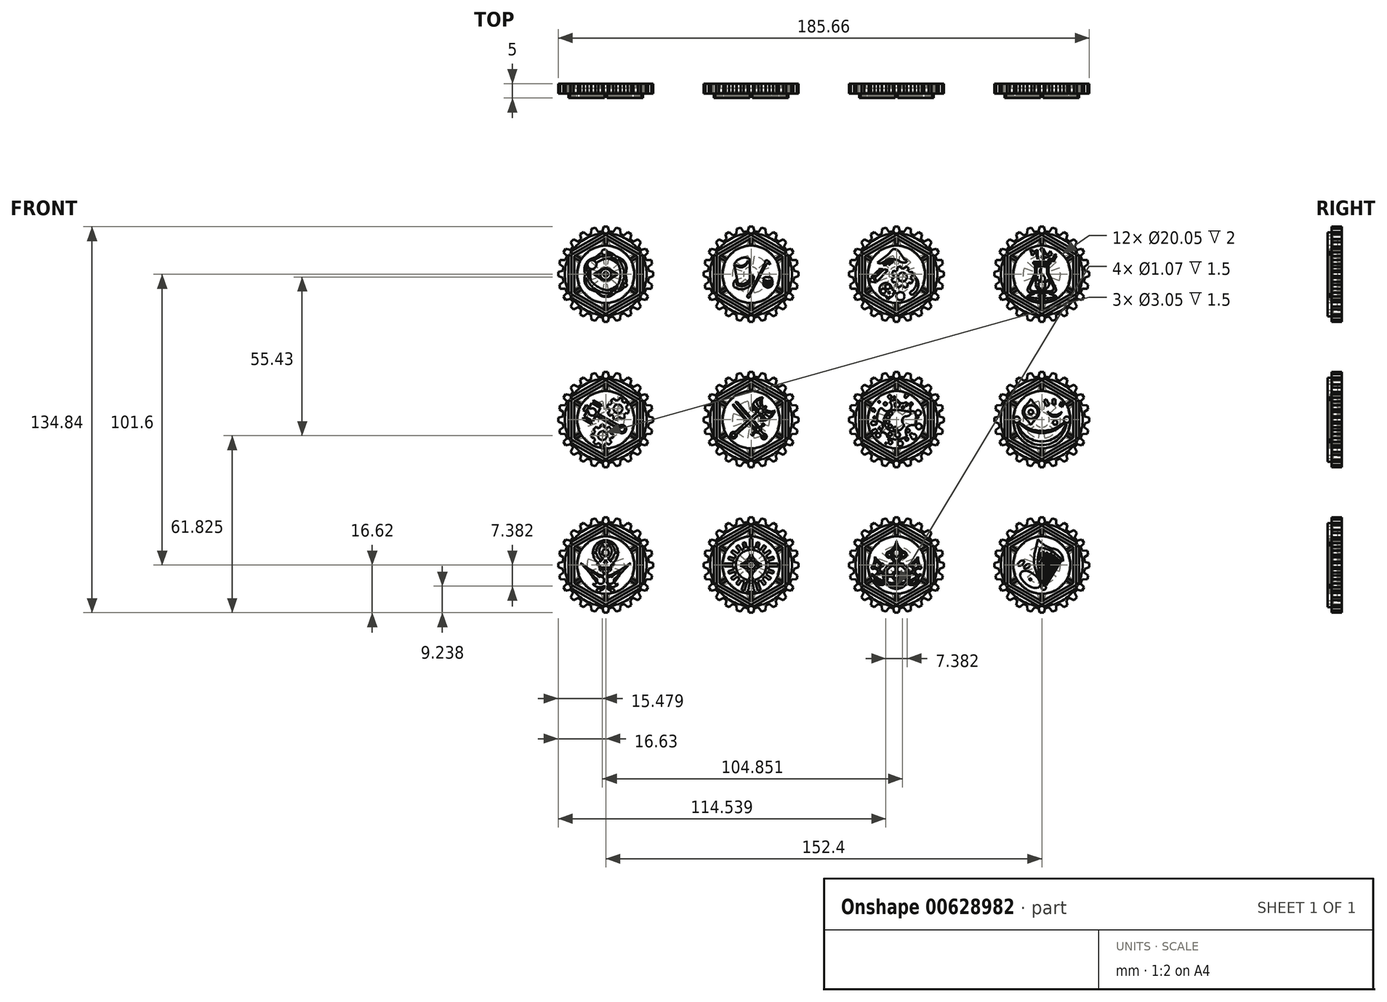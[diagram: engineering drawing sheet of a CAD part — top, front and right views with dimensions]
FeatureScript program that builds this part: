
annotation { "Feature Type Name" : "Feature", "Feature Type Description" : "" }
export const myFeature = defineFeature(function(context is Context, id is Id, definition is map)
    precondition{}
    {
        {
            var Q0;
            Q0=qCreatedBy(makeId("Front.planeOp"),FACE);
            var sketch = newSketch(context, id + "F0", { "sketchPlane" : qUnion([Q0])});
            skLineSegment(sketch, "E0", {"start": v(0, 15) * mm, "end": v(13, 7.5) * mm});
            skLineSegment(sketch, "E1", {"start": v(13, 7.5) * mm, "end": v(13, -7.5) * mm});
            skLineSegment(sketch, "E2", {"start": v(13, -7.5) * mm, "end": v(0, -15) * mm});
            skLineSegment(sketch, "E3", {"start": v(0, -15) * mm, "end": v(-13, -7.5) * mm});
            skLineSegment(sketch, "E4", {"start": v(-13, -7.5) * mm, "end": v(-13, 7.5) * mm});
            skLineSegment(sketch, "E5", {"start": v(-13, 7.5) * mm, "end": v(0, 15) * mm});
            skSolve(sketch);
        }
        {
            var Q0;
            Q0 = qSketchRegion(id + "F0", true);
            extrude(context, id + "F1", {"entities" : qUnion([Q0]), "depth" : 5 * mm, "offsetDistance" : 25.4 * mm});
        }
        {
            var Q0;
            Q0=makeQuery(id+"F1.opExtrude","CAP_FACE",FACE,{"disambiguationData":[OSD([sQuery(id+"F0.wireOp",EDGE,"E0"),sQuery(id+"F0.wireOp",EDGE,"E1"),sQuery(id+"F0.wireOp",EDGE,"E2"),sQuery(id+"F0.wireOp",EDGE,"E3"),sQuery(id+"F0.wireOp",EDGE,"E4"),sQuery(id+"F0.wireOp",EDGE,"E5")])],"isStart":false});
            var sketch = newSketch(context, id + "F2", { "sketchPlane" : qUnion([Q0])});
            skLineSegment(sketch, "E6.0", {"start": v(12, 6.92) * mm, "end": v(0, 13.85) * mm});
            skLineSegment(sketch, "E6.1", {"start": v(-12, 6.92) * mm, "end": v(-12, -6.92) * mm});
            skLineSegment(sketch, "E6.2", {"start": v(-12, -6.92) * mm, "end": v(0, -13.85) * mm});
            skLineSegment(sketch, "E6.3", {"start": v(0, 13.85) * mm, "end": v(-12, 6.92) * mm});
            skLineSegment(sketch, "E6.4", {"start": v(0, -13.85) * mm, "end": v(12, -6.92) * mm});
            skLineSegment(sketch, "E6.5", {"start": v(12, -6.92) * mm, "end": v(12, 6.92) * mm});
            skLineSegment(sketch, "E7.0", {"start": v(11, 6.35) * mm, "end": v(0, 12.7) * mm});
            skLineSegment(sketch, "E7.1", {"start": v(-11, 6.35) * mm, "end": v(-11, -6.35) * mm});
            skLineSegment(sketch, "E7.2", {"start": v(-11, -6.35) * mm, "end": v(0, -12.7) * mm});
            skLineSegment(sketch, "E7.3", {"start": v(0, 12.7) * mm, "end": v(-11, 6.35) * mm});
            skLineSegment(sketch, "E7.4", {"start": v(0, -12.7) * mm, "end": v(11, -6.35) * mm});
            skLineSegment(sketch, "E7.5", {"start": v(11, -6.35) * mm, "end": v(11, 6.35) * mm});
            skSolve(sketch);
        }
        {
            var Q0;
            Q0 = qSketchRegion(id + "F2", true);
            extrude(context, id + "F3", {"entities" : qUnion([Q0]), "operationType" : NewBodyOperationType.REMOVE, "oppositeDirection" : true, "depth" : 2 * mm, "offsetDistance" : 25.4 * mm});
        }
        {
            var Q0;
            Q0=makeQuery(id+"F3.boolean.opBoolean","SPLIT",FACE,{"disambiguationData":[TD([makeQuery(id+"F3.opExtrude","SWEPT_FACE",FACE,{"disambiguationData":[OSD([sQuery(id+"F2.wireOp",EDGE,"E7.0")])]})])],"derivedFrom":makeQuery(id+"F1.opExtrude","CAP_FACE",FACE,{"disambiguationData":[OSD([sQuery(id+"F0.wireOp",EDGE,"E0"),sQuery(id+"F0.wireOp",EDGE,"E1"),sQuery(id+"F0.wireOp",EDGE,"E2"),sQuery(id+"F0.wireOp",EDGE,"E3"),sQuery(id+"F0.wireOp",EDGE,"E4"),sQuery(id+"F0.wireOp",EDGE,"E5")])],"isStart":false})});
            var sketch = newSketch(context, id + "F4", { "sketchPlane" : qUnion([Q0])});
            skCircle(sketch, "E8", {"center": v(0, 0) * mm, "radius": 10.03 * mm});
            skSolve(sketch);
        }
        {
            var Q0;
            Q0 = qSketchRegion(id + "F4", true);
            extrude(context, id + "F5", {"entities" : qUnion([Q0]), "operationType" : NewBodyOperationType.REMOVE, "oppositeDirection" : true, "depth" : 2 * mm, "offsetDistance" : 25.4 * mm});
        }
        {
            var Q0;
            Q0=makeQuery(id+"F3.boolean.opBoolean","SPLIT",FACE,{"disambiguationData":[TD([makeQuery(id+"F3.opExtrude","SWEPT_FACE",FACE,{"disambiguationData":[OSD([sQuery(id+"F2.wireOp",EDGE,"E7.0")])]})])],"derivedFrom":makeQuery(id+"F1.opExtrude","CAP_FACE",FACE,{"disambiguationData":[OSD([sQuery(id+"F0.wireOp",EDGE,"E0"),sQuery(id+"F0.wireOp",EDGE,"E1"),sQuery(id+"F0.wireOp",EDGE,"E2"),sQuery(id+"F0.wireOp",EDGE,"E3"),sQuery(id+"F0.wireOp",EDGE,"E4"),sQuery(id+"F0.wireOp",EDGE,"E5")])],"isStart":false})});
            var sketch = newSketch(context, id + "F6", { "sketchPlane" : qUnion([Q0])});
            skLineSegment(sketch, "E9.bottom", {"start": v(-0.5, 17.5) * mm, "end": v(0.5, 17.5) * mm});
            skLineSegment(sketch, "E9.top", {"start": v(-0.5, -17.5) * mm, "end": v(0.5, -17.5) * mm});
            skLineSegment(sketch, "E9.left", {"start": v(-0.5, 17.5) * mm, "end": v(-0.5, -17.5) * mm});
            skLineSegment(sketch, "E9.right", {"start": v(0.5, 17.5) * mm, "end": v(0.5, -17.5) * mm});
            skPoint(sketch, "E9.middle", {"position": v(0, 0) * mm});
            skLineSegment(sketch, "E10", {"start": v(0, 0) * mm, "end": v(2.21, 3.83) * mm});
            skLineSegment(sketch, "E11.MirrorCS", {"start": v(14.9, 9.18) * mm, "end": v(-15.4, -8.32) * mm});
            skLineSegment(sketch, "E12.MirrorCS", {"start": v(15.4, 8.32) * mm, "end": v(-14.9, -9.18) * mm});
            skLineSegment(sketch, "E13.MirrorCS", {"start": v(15.4, -8.32) * mm, "end": v(-14.9, 9.18) * mm});
            skLineSegment(sketch, "E14.MirrorCS", {"start": v(14.9, -9.18) * mm, "end": v(-15.4, 8.32) * mm});
            skLineSegment(sketch, "E15", {"start": v(14.9, -9.18) * mm, "end": v(15.4, -8.32) * mm});
            skLineSegment(sketch, "E16", {"start": v(14.9, 9.18) * mm, "end": v(15.4, 8.32) * mm});
            skLineSegment(sketch, "E17", {"start": v(-15.4, -8.32) * mm, "end": v(-14.9, -9.18) * mm});
            skLineSegment(sketch, "E18", {"start": v(-14.9, 9.18) * mm, "end": v(-15.4, 8.32) * mm});
            skSolve(sketch);
        }
        {
            var Q0;
            Q0 = qSketchRegion(id + "F6", true);
            extrude(context, id + "F7", {"entities" : qUnion([Q0]), "operationType" : NewBodyOperationType.REMOVE, "oppositeDirection" : true, "depth" : 1.5 * mm, "offsetDistance" : 25.4 * mm});
        }
        {
            var Q0;
            Q0=makeQuery(id+"F5.boolean.opBoolean","COPY",FACE,{"derivedFrom":makeQuery(id+"F5.opExtrude","CAP_FACE",FACE,{"disambiguationData":[OSD([sQuery(id+"F4.wireOp",EDGE,"E8")])],"isStart":false})});
            var sketch = newSketch(context, id + "F8", { "sketchPlane" : qUnion([Q0])});
            skLineSegment(sketch, "E19", {"start": v(-0.66, -0.75) * mm, "end": v(-1.81, -2.05) * mm});
            skLineSegment(sketch, "E20.0", {"start": v(0.33, 0.37) * mm, "end": v(-1.1, 1.64) * mm});
            skLineSegment(sketch, "E20.1", {"start": v(0.33, 0.37) * mm, "end": v(4.83, -3.6) * mm});
            skLineSegment(sketch, "E21.0", {"start": v(-0.33, -0.37) * mm, "end": v(4.16, -4.34) * mm});
            skLineSegment(sketch, "E21.1", {"start": v(-0.33, -0.37) * mm, "end": v(-1.76, 0.9) * mm});
            skLineSegment(sketch, "E22", {"start": v(4.16, -4.34) * mm, "end": v(5.02, -5.1) * mm});
            skLineSegment(sketch, "E23", {"start": v(4.83, -3.6) * mm, "end": v(5.68, -4.34) * mm});
            skArc(sketch, "E24", {"start": v(5.02, -5.1) * mm, "mid": v(6.99, -6.15) * mm, "end": v(5.68, -4.34) * mm});
            skCircle(sketch, "E25", {"center": v(6.12, -5.4) * mm, "radius": 0.64 * mm});
            skArc(sketch, "E26.0", {"start": v(-1.88, 2.32) * mm, "mid": v(-1.75, 2.8) * mm, "end": v(-1.77, 3.29) * mm});
            skArc(sketch, "E27", {"start": v(0, 3.03) * mm, "mid": v(-0.36, 3.28) * mm, "end": v(-0.78, 3.42) * mm});
            skArc(sketch, "E28", {"start": v(0, 3.03) * mm, "mid": v(-1.18, 6.24) * mm, "end": v(-4.14, 7.93) * mm});
            skArc(sketch, "E29", {"start": v(-4.2, 4.37) * mm, "mid": v(-3.7, 6.15) * mm, "end": v(-4.14, 7.93) * mm});
            skPoint(sketch, "E30.orphan", {"position": v(-3.48, 1.35) * mm});
            skPoint(sketch, "E31.orphan", {"position": v(-1.77, 3.29) * mm});
            skCircle(sketch, "E32", {"center": v(-3.37, 2.97) * mm, "radius": 0.95 * mm});
            skArc(sketch, "E33.0", {"start": v(-3.53, 4.6) * mm, "mid": v(-3.22, 5.87) * mm, "end": v(-3.33, 7.19) * mm});
            skArc(sketch, "E34.trimOffspring", {"start": v(-3.9, 7.37) * mm, "mid": v(-4.06, 7.41) * mm, "end": v(-4.23, 7.44) * mm});
            skArc(sketch, "E35.trimOffspring", {"start": v(-3.52, 7.78) * mm, "mid": v(-3.6, 7.98) * mm, "end": v(-3.7, 8.17) * mm});
            skArc(sketch, "E36", {"start": v(-2.87, 4.52) * mm, "mid": v(-2.2, 5.29) * mm, "end": v(-1.86, 6.23) * mm});
            skArc(sketch, "E37", {"start": v(-2.18, 4.08) * mm, "mid": v(-1.5, 4.46) * mm, "end": v(-1, 5.06) * mm});
            skArc(sketch, "E38.trimOffspring", {"start": v(-1.86, 6.23) * mm, "mid": v(-2.55, 6.78) * mm, "end": v(-3.33, 7.19) * mm});
            skArc(sketch, "E39.trimOffspring", {"start": v(-2.87, 4.52) * mm, "mid": v(-3.2, 4.6) * mm, "end": v(-3.53, 4.6) * mm});
            skArc(sketch, "E40.trimOffspring", {"start": v(-4.2, 4.37) * mm, "mid": v(-4.3, 4.3) * mm, "end": v(-4.41, 4.22) * mm});
            skArc(sketch, "E41.trimOffspring", {"start": v(-1.9, 3.66) * mm, "mid": v(-2.02, 3.88) * mm, "end": v(-2.18, 4.08) * mm});
            skLineSegment(sketch, "E42", {"start": v(-1.1, 1.64) * mm, "end": v(-1.88, 2.32) * mm});
            skArc(sketch, "E43", {"start": v(0, 3.03) * mm, "mid": v(-0.85, 3.43) * mm, "end": v(-1.77, 3.29) * mm});
            skArc(sketch, "E44", {"start": v(-1.9, 3.66) * mm, "mid": v(-1.23, 3.71) * mm, "end": v(-0.57, 3.82) * mm});
            skArc(sketch, "E45.trimOffspring", {"start": v(-0.57, 3.82) * mm, "mid": v(-0.74, 4.46) * mm, "end": v(-1, 5.06) * mm});
            skArc(sketch, "E46", {"start": v(-4.41, 4.22) * mm, "mid": v(-4.55, 4.54) * mm, "end": v(-4.9, 4.62) * mm});
            skArc(sketch, "E47", {"start": v(-4.9, 4.62) * mm, "mid": v(-5.27, 4.65) * mm, "end": v(-5.2, 4.28) * mm});
            skArc(sketch, "E48.trimOffspring", {"start": v(-4.74, 3.85) * mm, "mid": v(-4.8, 3.74) * mm, "end": v(-4.86, 3.62) * mm});
            skArc(sketch, "E49.trimOffspring", {"start": v(-5.2, 4.28) * mm, "mid": v(-5.07, 3.95) * mm, "end": v(-4.74, 3.85) * mm});
            skArc(sketch, "E50.MirrorCS", {"start": v(-3.01, -0.38) * mm, "mid": v(-3.5, 0.41) * mm, "end": v(-3.48, 1.35) * mm});
            skArc(sketch, "E51.MirrorCS", {"start": v(-3.86, 1.42) * mm, "mid": v(-3.83, 0.76) * mm, "end": v(-3.86, 0.1) * mm});
            skArc(sketch, "E52.MirrorCS", {"start": v(-4.32, 1.65) * mm, "mid": v(-4.61, 0.93) * mm, "end": v(-5.15, 0.36) * mm});
            skArc(sketch, "E53.MirrorCS", {"start": v(-4.84, 2.28) * mm, "mid": v(-5.52, 1.53) * mm, "end": v(-6.42, 1.07) * mm});
            skArc(sketch, "E54.MirrorCS", {"start": v(-5, 2.93) * mm, "mid": v(-6.23, 2.47) * mm, "end": v(-7.54, 2.4) * mm});
            skArc(sketch, "E55.MirrorCS", {"start": v(-4.86, 3.62) * mm, "mid": v(-6.56, 2.92) * mm, "end": v(-8.39, 3.12) * mm});
            skArc(sketch, "E56.MirrorCS", {"start": v(-3.01, -0.38) * mm, "mid": v(-6.33, 0.4) * mm, "end": v(-8.39, 3.12) * mm});
            skArc(sketch, "E57.MirrorCS", {"start": v(-6.42, 1.07) * mm, "mid": v(-7.05, 1.68) * mm, "end": v(-7.54, 2.4) * mm});
            skArc(sketch, "E58.MirrorCS", {"start": v(-3.86, 0.1) * mm, "mid": v(-4.51, 0.18) * mm, "end": v(-5.15, 0.36) * mm});
            skArc(sketch, "E59.MirrorCS", {"start": v(-4.84, 2.28) * mm, "mid": v(-4.95, 2.6) * mm, "end": v(-5, 2.93) * mm});
            skArc(sketch, "E60.MirrorCS", {"start": v(-3.86, 1.42) * mm, "mid": v(-4.1, 1.52) * mm, "end": v(-4.32, 1.65) * mm});
            skArc(sketch, "E61.trimOffspring", {"start": v(-4.32, 1.65) * mm, "mid": v(-4.1, 1.52) * mm, "end": v(-3.86, 1.42) * mm});
            skArc(sketch, "E62.trimOffspring", {"start": v(-3.48, 1.35) * mm, "mid": v(-3, 1.39) * mm, "end": v(-2.54, 1.57) * mm});
            skLineSegment(sketch, "E63", {"start": v(-1.76, 0.9) * mm, "end": v(-2.54, 1.57) * mm});
            skArc(sketch, "E64", {"start": v(-4.34, -4.92) * mm, "mid": v(-5.15, -6.6) * mm, "end": v(-3.6, -5.58) * mm});
            skLineSegment(sketch, "E65", {"start": v(-3.88, -5.15) * mm, "end": v(-2.36, -3.43) * mm});
            skPoint(sketch, "E65.endSnap0", {"position": v(-1.7, -3.43) * mm});
            skArc(sketch, "E66", {"start": v(-1.35, -3.9) * mm, "mid": v(-1.26, -3.64) * mm, "end": v(-1.24, -3.36) * mm});
            skLineSegment(sketch, "E67", {"start": v(-1.35, -3.9) * mm, "end": v(-0.71, -4.77) * mm});
            skLineSegment(sketch, "E68.MirrorCS", {"start": v(-1.76, -4.38) * mm, "end": v(-0.83, -4.9) * mm});
            skArc(sketch, "E69", {"start": v(-0.83, -4.9) * mm, "mid": v(-0.17, -5.36) * mm, "end": v(-0.71, -4.77) * mm});
            skLineSegment(sketch, "E70.MirrorCS", {"start": v(-3.38, -2.95) * mm, "end": v(-4.01, -2.1) * mm});
            skLineSegment(sketch, "E71.MirrorCS", {"start": v(-2.96, -2.48) * mm, "end": v(-3.9, -1.96) * mm});
            skArc(sketch, "E72.MirrorC", {"start": v(-4.01, -2.1) * mm, "mid": v(-4.55, -1.5) * mm, "end": v(-3.9, -1.96) * mm});
            skLineSegment(sketch, "E73.trimOffspring", {"start": v(-2.65, -4.52) * mm, "end": v(-3.6, -5.58) * mm});
            skPoint(sketch, "E74.orphan", {"position": v(-2.28, -4.1) * mm});
            skLineSegment(sketch, "E75.trimOffspring", {"start": v(-3.4, -3.86) * mm, "end": v(-4.34, -4.92) * mm});
            skPoint(sketch, "E76.orphan", {"position": v(-3.03, -3.43) * mm});
            skPoint(sketch, "E77.orphan", {"position": v(-2.44, -2.77) * mm});
            skArc(sketch, "E78.trimOffspring", {"start": v(-3.38, -2.95) * mm, "mid": v(-3.49, -3.4) * mm, "end": v(-3.4, -3.86) * mm});
            skArc(sketch, "E79.trimOffspring", {"start": v(-2.65, -4.52) * mm, "mid": v(-2.2, -4.54) * mm, "end": v(-1.76, -4.38) * mm});
            skCircle(sketch, "E80", {"center": v(-2.36, -3.43) * mm, "radius": 0.67 * mm});
            skPoint(sketch, "E81.orphan", {"position": v(-4.89, -5.54) * mm});
            skPoint(sketch, "E82.end.orphan", {"position": v(-4.14, -6.2) * mm});
            skCircle(sketch, "E83", {"center": v(-4.51, -5.87) * mm, "radius": 0.5 * mm});
            skLineSegment(sketch, "E84.0", {"start": v(-1.04, -0.42) * mm, "end": v(-2.45, -2.02) * mm});
            skLineSegment(sketch, "E85", {"start": v(-2.45, -2.02) * mm, "end": v(-2.43, -2.31) * mm});
            skArc(sketch, "E86.trimOffspring", {"start": v(-2.43, -2.31) * mm, "mid": v(-2.7, -2.36) * mm, "end": v(-2.96, -2.48) * mm});
            skArc(sketch, "E87", {"start": v(-1.81, -2.05) * mm, "mid": v(-1.88, -2.24) * mm, "end": v(-1.83, -2.44) * mm});
            skLineSegment(sketch, "E88", {"start": v(-1.04, -0.42) * mm, "end": v(-0.66, -0.75) * mm});
            skLineSegment(sketch, "E89", {"start": v(4.76, 6.15) * mm, "end": v(5.48, 6.21) * mm});
            skLineSegment(sketch, "E90", {"start": v(0.29, 1.08) * mm, "end": v(0.66, 0.75) * mm});
            skLineSegment(sketch, "E91.trimOffspring", {"start": v(0.66, 0.75) * mm, "end": v(5.48, 6.21) * mm});
            skLineSegment(sketch, "E92.trimOffspring", {"start": v(0.29, 1.08) * mm, "end": v(4.76, 6.15) * mm});
            skPoint(sketch, "E93.orphan", {"position": v(0.75, -0.66) * mm});
            skLineSegment(sketch, "E94.MirrorCS", {"start": v(-0.95, -3.34) * mm, "end": v(-1.24, -3.36) * mm});
            skArc(sketch, "E95.MirrorCS", {"start": v(-1.06, -2.71) * mm, "mid": v(-1.24, -2.8) * mm, "end": v(-1.45, -2.78) * mm});
            skLineSegment(sketch, "E96.MirrorCS", {"start": v(0.09, -1.41) * mm, "end": v(-1.06, -2.71) * mm});
            skLineSegment(sketch, "E97.MirrorCS", {"start": v(0.46, -1.74) * mm, "end": v(-0.95, -3.34) * mm});
            skLineSegment(sketch, "E98.MirrorCS", {"start": v(0.46, -1.74) * mm, "end": v(0.09, -1.41) * mm});
            skLineSegment(sketch, "E99.MirrorCS", {"start": v(1.79, -0.24) * mm, "end": v(1.41, 0.09) * mm});
            skLineSegment(sketch, "E100.MirrorCS", {"start": v(1.41, 0.09) * mm, "end": v(6.23, 5.55) * mm});
            skLineSegment(sketch, "E101.MirrorCS", {"start": v(1.79, -0.24) * mm, "end": v(6.26, 4.82) * mm});
            skLineSegment(sketch, "E102.MirrorCS", {"start": v(6.26, 4.82) * mm, "end": v(6.23, 5.55) * mm});
            skArc(sketch, "E103.trimOffspring", {"start": v(-1.45, -2.78) * mm, "mid": v(-1.62, -2.59) * mm, "end": v(-1.83, -2.44) * mm});
            skSolve(sketch);
        }
        {
            var Q0;
            Q0 = qSketchRegion(id + "F8", true);
            extrude(context, id + "F9", {"entities" : qUnion([Q0]), "operationType" : NewBodyOperationType.ADD, "depth" : 1.5 * mm, "offsetDistance" : 25.4 * mm});
        }
        {
            var Q0;
            Q0=makeQuery(id+"F1.opExtrude","CAP_FACE",FACE,{"disambiguationData":[OSD([sQuery(id+"F0.wireOp",EDGE,"E0"),sQuery(id+"F0.wireOp",EDGE,"E1"),sQuery(id+"F0.wireOp",EDGE,"E2"),sQuery(id+"F0.wireOp",EDGE,"E3"),sQuery(id+"F0.wireOp",EDGE,"E4"),sQuery(id+"F0.wireOp",EDGE,"E5")])],"isStart":true});
            var sketch = newSketch(context, id + "F10", { "sketchPlane" : qUnion([Q0])});
            skCircle(sketch, "E104", {"center": v(0, 0) * mm, "radius": 14.3 * mm});
            skCircle(sketch, "E105", {"center": v(0, 0) * mm, "radius": 15 * mm});
            skLineSegment(sketch, "E106", {"start": v(4.3, 16.06) * mm, "end": v(3.63, 16.24) * mm});
            skLineSegment(sketch, "E107", {"start": v(3.85, 14.5) * mm, "end": v(2.69, 14.8) * mm});
            skLineSegment(sketch, "E108", {"start": v(3.63, 16.24) * mm, "end": v(2.69, 14.8) * mm});
            skLineSegment(sketch, "E109", {"start": v(2.69, 14.8) * mm, "end": v(2.55, 14.6) * mm});
            skLineSegment(sketch, "E110.MirrorCS", {"start": v(4.98, 15.88) * mm, "end": v(5.08, 14.17) * mm});
            skLineSegment(sketch, "E111.MirrorCS", {"start": v(5.08, 14.17) * mm, "end": v(5.1, 13.92) * mm});
            skLineSegment(sketch, "E112.MirrorCS", {"start": v(4.3, 16.06) * mm, "end": v(4.98, 15.88) * mm});
            skLineSegment(sketch, "E113.MirrorCS", {"start": v(7.7, 14.75) * mm, "end": v(6.43, 13.6) * mm});
            skLineSegment(sketch, "E114.MirrorCS", {"start": v(8.92, 14.05) * mm, "end": v(8.57, 12.37) * mm});
            skLineSegment(sketch, "E115.MirrorCS", {"start": v(6.43, 13.6) * mm, "end": v(6.24, 13.45) * mm});
            skLineSegment(sketch, "E116.MirrorCS", {"start": v(8.57, 12.37) * mm, "end": v(8.52, 12.13) * mm});
            skLineSegment(sketch, "E117.MirrorCS", {"start": v(8.31, 14.4) * mm, "end": v(8.92, 14.05) * mm});
            skLineSegment(sketch, "E118.MirrorCS", {"start": v(8.31, 14.4) * mm, "end": v(7.7, 14.75) * mm});
            skLineSegment(sketch, "E119.MirrorCS", {"start": v(11.26, 12.25) * mm, "end": v(9.73, 11.48) * mm});
            skLineSegment(sketch, "E120.MirrorCS", {"start": v(9.73, 11.48) * mm, "end": v(9.51, 11.37) * mm});
            skLineSegment(sketch, "E121.MirrorCS", {"start": v(11.48, 9.73) * mm, "end": v(11.37, 9.51) * mm});
            skLineSegment(sketch, "E122.MirrorCS", {"start": v(11.76, 11.76) * mm, "end": v(12.25, 11.26) * mm});
            skLineSegment(sketch, "E123.MirrorCS", {"start": v(11.76, 11.76) * mm, "end": v(11.26, 12.25) * mm});
            skLineSegment(sketch, "E124.MirrorCS", {"start": v(12.25, 11.26) * mm, "end": v(11.48, 9.73) * mm});
            skLineSegment(sketch, "E125.MirrorCS", {"start": v(-1.24, 15) * mm, "end": v(-1.31, 14.77) * mm});
            skLineSegment(sketch, "E126.MirrorCS", {"start": v(-0.7, 16.62) * mm, "end": v(-1.24, 15) * mm});
            skLineSegment(sketch, "E127.MirrorCS", {"start": v(1.24, 15) * mm, "end": v(1.31, 14.77) * mm});
            skLineSegment(sketch, "E128.MirrorCS", {"start": v(0.7, 16.62) * mm, "end": v(1.24, 15) * mm});
            skLineSegment(sketch, "E129.MirrorCS", {"start": v(0, 16.62) * mm, "end": v(-0.7, 16.62) * mm});
            skLineSegment(sketch, "E130.MirrorCS", {"start": v(0, 16.62) * mm, "end": v(0.7, 16.62) * mm});
            skLineSegment(sketch, "E131.MirrorCS", {"start": v(14.05, 8.92) * mm, "end": v(12.37, 8.57) * mm});
            skLineSegment(sketch, "E132.MirrorCS", {"start": v(14.75, 7.7) * mm, "end": v(13.6, 6.43) * mm});
            skLineSegment(sketch, "E133.MirrorCS", {"start": v(12.37, 8.57) * mm, "end": v(12.13, 8.52) * mm});
            skLineSegment(sketch, "E134.MirrorCS", {"start": v(13.6, 6.43) * mm, "end": v(13.45, 6.24) * mm});
            skLineSegment(sketch, "E135.MirrorCS", {"start": v(14.4, 8.31) * mm, "end": v(14.75, 7.7) * mm});
            skLineSegment(sketch, "E136.MirrorCS", {"start": v(14.4, 8.31) * mm, "end": v(14.05, 8.92) * mm});
            skLineSegment(sketch, "E137.MirrorCS", {"start": v(14.75, -7.7) * mm, "end": v(13.6, -6.43) * mm});
            skLineSegment(sketch, "E138.MirrorCS", {"start": v(2.69, -14.8) * mm, "end": v(2.55, -14.6) * mm});
            skLineSegment(sketch, "E139.MirrorCS", {"start": v(7.7, -14.75) * mm, "end": v(6.43, -13.6) * mm});
            skLineSegment(sketch, "E140.MirrorCS", {"start": v(8.92, -14.05) * mm, "end": v(8.57, -12.37) * mm});
            skLineSegment(sketch, "E141.MirrorCS", {"start": v(8.57, -12.37) * mm, "end": v(8.52, -12.13) * mm});
            skLineSegment(sketch, "E142.MirrorCS", {"start": v(6.43, -13.6) * mm, "end": v(6.24, -13.45) * mm});
            skLineSegment(sketch, "E143.MirrorCS", {"start": v(3.63, -16.24) * mm, "end": v(2.69, -14.8) * mm});
            skLineSegment(sketch, "E144.MirrorCS", {"start": v(4.3, -16.06) * mm, "end": v(4.98, -15.88) * mm});
            skLineSegment(sketch, "E145.MirrorCS", {"start": v(4.3, -16.06) * mm, "end": v(3.63, -16.24) * mm});
            skLineSegment(sketch, "E146.MirrorCS", {"start": v(8.31, -14.4) * mm, "end": v(7.7, -14.75) * mm});
            skLineSegment(sketch, "E147.MirrorCS", {"start": v(8.31, -14.4) * mm, "end": v(8.92, -14.05) * mm});
            skLineSegment(sketch, "E148.MirrorCS", {"start": v(0, -16.62) * mm, "end": v(-0.7, -16.62) * mm});
            skLineSegment(sketch, "E149.MirrorCS", {"start": v(13.6, -6.43) * mm, "end": v(13.45, -6.24) * mm});
            skLineSegment(sketch, "E150.MirrorCS", {"start": v(1.24, -15) * mm, "end": v(1.31, -14.77) * mm});
            skLineSegment(sketch, "E151.MirrorCS", {"start": v(0, -16.62) * mm, "end": v(0.7, -16.62) * mm});
            skLineSegment(sketch, "E152.MirrorCS", {"start": v(9.73, -11.48) * mm, "end": v(9.51, -11.37) * mm});
            skLineSegment(sketch, "E153.MirrorCS", {"start": v(14.4, -8.31) * mm, "end": v(14.05, -8.92) * mm});
            skLineSegment(sketch, "E154.MirrorCS", {"start": v(11.48, -9.73) * mm, "end": v(11.37, -9.51) * mm});
            skLineSegment(sketch, "E155.MirrorCS", {"start": v(5.08, -14.17) * mm, "end": v(5.1, -13.92) * mm});
            skLineSegment(sketch, "E156.MirrorCS", {"start": v(-0.7, -16.62) * mm, "end": v(-1.24, -15) * mm});
            skLineSegment(sketch, "E157.MirrorCS", {"start": v(11.76, -11.76) * mm, "end": v(11.26, -12.25) * mm});
            skLineSegment(sketch, "E158.MirrorCS", {"start": v(11.76, -11.76) * mm, "end": v(12.25, -11.26) * mm});
            skLineSegment(sketch, "E159.MirrorCS", {"start": v(12.25, -11.26) * mm, "end": v(11.48, -9.73) * mm});
            skLineSegment(sketch, "E160.MirrorCS", {"start": v(14.05, -8.92) * mm, "end": v(12.37, -8.57) * mm});
            skLineSegment(sketch, "E161.MirrorCS", {"start": v(0.7, -16.62) * mm, "end": v(1.24, -15) * mm});
            skLineSegment(sketch, "E162.MirrorCS", {"start": v(-1.24, -15) * mm, "end": v(-1.31, -14.77) * mm});
            skLineSegment(sketch, "E163.MirrorCS", {"start": v(12.37, -8.57) * mm, "end": v(12.13, -8.52) * mm});
            skLineSegment(sketch, "E164.MirrorCS", {"start": v(11.26, -12.25) * mm, "end": v(9.73, -11.48) * mm});
            skLineSegment(sketch, "E165.MirrorCS", {"start": v(14.4, -8.31) * mm, "end": v(14.75, -7.7) * mm});
            skLineSegment(sketch, "E166.MirrorCS", {"start": v(4.98, -15.88) * mm, "end": v(5.08, -14.17) * mm});
            skLineSegment(sketch, "E167.MirrorCS", {"start": v(3.85, -14.5) * mm, "end": v(2.69, -14.8) * mm});
            skLineSegment(sketch, "E168.MirrorCS", {"start": v(15.88, 4.98) * mm, "end": v(14.17, 5.08) * mm});
            skLineSegment(sketch, "E169.MirrorCS", {"start": v(16.24, 3.63) * mm, "end": v(14.8, 2.69) * mm});
            skLineSegment(sketch, "E170.MirrorCS", {"start": v(14.17, 5.08) * mm, "end": v(13.92, 5.1) * mm});
            skLineSegment(sketch, "E171.MirrorCS", {"start": v(16.06, 4.3) * mm, "end": v(16.24, 3.63) * mm});
            skLineSegment(sketch, "E172.MirrorCS", {"start": v(16.06, 4.3) * mm, "end": v(15.88, 4.98) * mm});
            skLineSegment(sketch, "E173.MirrorCS", {"start": v(14.8, 2.69) * mm, "end": v(14.6, 2.55) * mm});
            skLineSegment(sketch, "E174.MirrorCS", {"start": v(15, -1.28) * mm, "end": v(14.76, -1.36) * mm});
            skLineSegment(sketch, "E175.MirrorCS", {"start": v(15, 1.2) * mm, "end": v(14.77, 1.27) * mm});
            skLineSegment(sketch, "E176.MirrorCS", {"start": v(16.63, 0.65) * mm, "end": v(15, 1.2) * mm});
            skLineSegment(sketch, "E177.MirrorCS", {"start": v(16.62, -0.75) * mm, "end": v(15, -1.28) * mm});
            skLineSegment(sketch, "E178.MirrorCS", {"start": v(16.62, -0.05) * mm, "end": v(16.62, -0.75) * mm});
            skLineSegment(sketch, "E179.MirrorCS", {"start": v(16.62, -0.05) * mm, "end": v(16.63, 0.65) * mm});
            skLineSegment(sketch, "E180.MirrorCS", {"start": v(16.25, -3.58) * mm, "end": v(14.82, -2.64) * mm});
            skLineSegment(sketch, "E181.MirrorCS", {"start": v(14.82, -2.64) * mm, "end": v(14.61, -2.51) * mm});
            skLineSegment(sketch, "E182.MirrorCS", {"start": v(14.18, -5.04) * mm, "end": v(13.94, -5.05) * mm});
            skLineSegment(sketch, "E183.MirrorCS", {"start": v(15.9, -4.93) * mm, "end": v(14.18, -5.04) * mm});
            skLineSegment(sketch, "E184.MirrorCS", {"start": v(16.07, -4.26) * mm, "end": v(15.9, -4.93) * mm});
            skLineSegment(sketch, "E185.MirrorCS", {"start": v(16.07, -4.26) * mm, "end": v(16.25, -3.58) * mm});
            skLineSegment(sketch, "E186.MirrorCS", {"start": v(-8.31, 14.4) * mm, "end": v(-8.92, 14.05) * mm});
            skLineSegment(sketch, "E187.MirrorCS", {"start": v(-7.7, 14.75) * mm, "end": v(-6.43, 13.6) * mm});
            skLineSegment(sketch, "E188.MirrorCS", {"start": v(-3.85, 14.5) * mm, "end": v(-2.69, 14.8) * mm});
            skLineSegment(sketch, "E189.MirrorCS", {"start": v(-3.63, 16.24) * mm, "end": v(-2.69, 14.8) * mm});
            skLineSegment(sketch, "E190.MirrorCS", {"start": v(-2.69, 14.8) * mm, "end": v(-2.55, 14.6) * mm});
            skLineSegment(sketch, "E191.MirrorCS", {"start": v(-7.7, -14.75) * mm, "end": v(-6.43, -13.6) * mm});
            skLineSegment(sketch, "E192.MirrorCS", {"start": v(-8.92, -14.05) * mm, "end": v(-8.57, -12.37) * mm});
            skLineSegment(sketch, "E193.MirrorCS", {"start": v(-15, -1.28) * mm, "end": v(-14.76, -1.36) * mm});
            skLineSegment(sketch, "E194.MirrorCS", {"start": v(-14.82, -2.64) * mm, "end": v(-14.61, -2.51) * mm});
            skLineSegment(sketch, "E195.MirrorCS", {"start": v(-2.69, -14.8) * mm, "end": v(-2.55, -14.6) * mm});
            skLineSegment(sketch, "E196.MirrorCS", {"start": v(-3.63, -16.24) * mm, "end": v(-2.69, -14.8) * mm});
            skLineSegment(sketch, "E197.MirrorCS", {"start": v(-4.3, -16.06) * mm, "end": v(-4.98, -15.88) * mm});
            skLineSegment(sketch, "E198.MirrorCS", {"start": v(-3.85, -14.5) * mm, "end": v(-2.69, -14.8) * mm});
            skLineSegment(sketch, "E199.MirrorCS", {"start": v(-15, 1.2) * mm, "end": v(-14.77, 1.27) * mm});
            skLineSegment(sketch, "E200.MirrorCS", {"start": v(-8.31, -14.4) * mm, "end": v(-7.7, -14.75) * mm});
            skLineSegment(sketch, "E201.MirrorCS", {"start": v(-8.31, 14.4) * mm, "end": v(-7.7, 14.75) * mm});
            skLineSegment(sketch, "E202.MirrorCS", {"start": v(-9.73, -11.48) * mm, "end": v(-9.51, -11.37) * mm});
            skLineSegment(sketch, "E203.MirrorCS", {"start": v(-5.08, 14.17) * mm, "end": v(-5.1, 13.92) * mm});
            skLineSegment(sketch, "E204.MirrorCS", {"start": v(-8.92, 14.05) * mm, "end": v(-8.57, 12.37) * mm});
            skLineSegment(sketch, "E205.MirrorCS", {"start": v(-6.43, 13.6) * mm, "end": v(-6.24, 13.45) * mm});
            skLineSegment(sketch, "E206.MirrorCS", {"start": v(-8.57, 12.37) * mm, "end": v(-8.52, 12.13) * mm});
            skLineSegment(sketch, "E207.MirrorCS", {"start": v(-8.57, -12.37) * mm, "end": v(-8.52, -12.13) * mm});
            skLineSegment(sketch, "E208.MirrorCS", {"start": v(-6.43, -13.6) * mm, "end": v(-6.24, -13.45) * mm});
            skLineSegment(sketch, "E209.MirrorCS", {"start": v(-8.31, -14.4) * mm, "end": v(-8.92, -14.05) * mm});
            skLineSegment(sketch, "E210.MirrorCS", {"start": v(-9.73, 11.48) * mm, "end": v(-9.51, 11.37) * mm});
            skLineSegment(sketch, "E211.MirrorCS", {"start": v(-14.75, -7.7) * mm, "end": v(-13.6, -6.43) * mm});
            skLineSegment(sketch, "E212.MirrorCS", {"start": v(-11.76, -11.76) * mm, "end": v(-12.25, -11.26) * mm});
            skLineSegment(sketch, "E213.MirrorCS", {"start": v(-16.06, 4.3) * mm, "end": v(-16.24, 3.63) * mm});
            skLineSegment(sketch, "E214.MirrorCS", {"start": v(-14.8, 2.69) * mm, "end": v(-14.6, 2.55) * mm});
            skLineSegment(sketch, "E215.MirrorCS", {"start": v(-12.25, -11.26) * mm, "end": v(-11.48, -9.73) * mm});
            skLineSegment(sketch, "E216.MirrorCS", {"start": v(-14.05, -8.92) * mm, "end": v(-12.37, -8.57) * mm});
            skLineSegment(sketch, "E217.MirrorCS", {"start": v(-14.18, -5.04) * mm, "end": v(-13.94, -5.05) * mm});
            skLineSegment(sketch, "E218.MirrorCS", {"start": v(-14.4, -8.31) * mm, "end": v(-14.05, -8.92) * mm});
            skLineSegment(sketch, "E219.MirrorCS", {"start": v(-4.3, 16.06) * mm, "end": v(-3.63, 16.24) * mm});
            skLineSegment(sketch, "E220.MirrorCS", {"start": v(-4.98, 15.88) * mm, "end": v(-5.08, 14.17) * mm});
            skLineSegment(sketch, "E221.MirrorCS", {"start": v(-4.3, 16.06) * mm, "end": v(-4.98, 15.88) * mm});
            skLineSegment(sketch, "E222.MirrorCS", {"start": v(-11.76, -11.76) * mm, "end": v(-11.26, -12.25) * mm});
            skLineSegment(sketch, "E223.MirrorCS", {"start": v(-16.24, 3.63) * mm, "end": v(-14.8, 2.69) * mm});
            skLineSegment(sketch, "E224.MirrorCS", {"start": v(-4.3, -16.06) * mm, "end": v(-3.63, -16.24) * mm});
            skLineSegment(sketch, "E225.MirrorCS", {"start": v(-16.25, -3.58) * mm, "end": v(-14.82, -2.64) * mm});
            skLineSegment(sketch, "E226.MirrorCS", {"start": v(-11.26, -12.25) * mm, "end": v(-9.73, -11.48) * mm});
            skLineSegment(sketch, "E227.MirrorCS", {"start": v(-5.08, -14.17) * mm, "end": v(-5.1, -13.92) * mm});
            skLineSegment(sketch, "E228.MirrorCS", {"start": v(-15.88, 4.98) * mm, "end": v(-14.17, 5.08) * mm});
            skLineSegment(sketch, "E229.MirrorCS", {"start": v(-13.6, -6.43) * mm, "end": v(-13.45, -6.24) * mm});
            skLineSegment(sketch, "E230.MirrorCS", {"start": v(-11.26, 12.25) * mm, "end": v(-9.73, 11.48) * mm});
            skLineSegment(sketch, "E231.MirrorCS", {"start": v(-4.98, -15.88) * mm, "end": v(-5.08, -14.17) * mm});
            skLineSegment(sketch, "E232.MirrorCS", {"start": v(-12.37, -8.57) * mm, "end": v(-12.13, -8.52) * mm});
            skLineSegment(sketch, "E233.MirrorCS", {"start": v(-11.48, -9.73) * mm, "end": v(-11.37, -9.51) * mm});
            skLineSegment(sketch, "E234.MirrorCS", {"start": v(-16.06, 4.3) * mm, "end": v(-15.88, 4.98) * mm});
            skLineSegment(sketch, "E235.MirrorCS", {"start": v(-14.4, -8.31) * mm, "end": v(-14.75, -7.7) * mm});
            skLineSegment(sketch, "E236.MirrorCS", {"start": v(-16.07, -4.26) * mm, "end": v(-16.25, -3.58) * mm});
            skLineSegment(sketch, "E237.MirrorCS", {"start": v(-16.62, -0.75) * mm, "end": v(-15, -1.28) * mm});
            skLineSegment(sketch, "E238.MirrorCS", {"start": v(-16.63, 0.65) * mm, "end": v(-15, 1.2) * mm});
            skLineSegment(sketch, "E239.MirrorCS", {"start": v(-14.05, 8.92) * mm, "end": v(-12.37, 8.57) * mm});
            skLineSegment(sketch, "E240.MirrorCS", {"start": v(-11.76, 11.76) * mm, "end": v(-12.25, 11.26) * mm});
            skLineSegment(sketch, "E241.MirrorCS", {"start": v(-14.75, 7.7) * mm, "end": v(-13.6, 6.43) * mm});
            skLineSegment(sketch, "E242.MirrorCS", {"start": v(-11.76, 11.76) * mm, "end": v(-11.26, 12.25) * mm});
            skLineSegment(sketch, "E243.MirrorCS", {"start": v(-14.17, 5.08) * mm, "end": v(-13.92, 5.1) * mm});
            skLineSegment(sketch, "E244.MirrorCS", {"start": v(-14.4, 8.31) * mm, "end": v(-14.75, 7.7) * mm});
            skLineSegment(sketch, "E245.MirrorCS", {"start": v(-16.07, -4.26) * mm, "end": v(-15.9, -4.93) * mm});
            skLineSegment(sketch, "E246.MirrorCS", {"start": v(-13.6, 6.43) * mm, "end": v(-13.45, 6.24) * mm});
            skLineSegment(sketch, "E247.MirrorCS", {"start": v(-12.25, 11.26) * mm, "end": v(-11.48, 9.73) * mm});
            skLineSegment(sketch, "E248.MirrorCS", {"start": v(-12.37, 8.57) * mm, "end": v(-12.13, 8.52) * mm});
            skLineSegment(sketch, "E249.MirrorCS", {"start": v(-16.62, -0.05) * mm, "end": v(-16.63, 0.65) * mm});
            skLineSegment(sketch, "E250.MirrorCS", {"start": v(-15.9, -4.93) * mm, "end": v(-14.18, -5.04) * mm});
            skLineSegment(sketch, "E251.MirrorCS", {"start": v(-11.48, 9.73) * mm, "end": v(-11.37, 9.51) * mm});
            skLineSegment(sketch, "E252.MirrorCS", {"start": v(-16.62, -0.05) * mm, "end": v(-16.62, -0.75) * mm});
            skLineSegment(sketch, "E253.MirrorCS", {"start": v(-14.4, 8.31) * mm, "end": v(-14.05, 8.92) * mm});
            skSolve(sketch);
        }
        {
            var Q0;
            Q0 = qSketchRegion(id + "F10", true);
            extrude(context, id + "F11", {"entities" : qUnion([Q0]), "operationType" : NewBodyOperationType.ADD, "oppositeDirection" : true, "depth" : 3.5 * mm, "offsetDistance" : 25.4 * mm});
        }
        {
            var Q0;
            Q0=makeQuery(id+"F11.boolean.opBoolean","MERGE",FACE,{"derivedFrom":[makeQuery(id+"F1.opExtrude","CAP_FACE",FACE,{"disambiguationData":[OSD([sQuery(id+"F0.wireOp",EDGE,"E0"),sQuery(id+"F0.wireOp",EDGE,"E1"),sQuery(id+"F0.wireOp",EDGE,"E2"),sQuery(id+"F0.wireOp",EDGE,"E3"),sQuery(id+"F0.wireOp",EDGE,"E4"),sQuery(id+"F0.wireOp",EDGE,"E5")])],"isStart":true}),makeQuery(id+"F11.opExtrude","CAP_FACE",FACE,{"disambiguationData":[OSD([sQuery(id+"F10.wireOp",EDGE,"E106"),sQuery(id+"F10.wireOp",EDGE,"E108"),sQuery(id+"F10.wireOp",EDGE,"E109"),sQuery(id+"F10.wireOp",EDGE,"E110.MirrorCS"),sQuery(id+"F10.wireOp",EDGE,"E111.MirrorCS"),sQuery(id+"F10.wireOp",EDGE,"E112.MirrorCS"),sQuery(id+"F10.wireOp",EDGE,"E115.MirrorCS"),sQuery(id+"F10.wireOp",EDGE,"E116.MirrorCS"),sQuery(id+"F10.wireOp",EDGE,"E117.MirrorCS"),sQuery(id+"F10.wireOp",EDGE,"E118.MirrorCS"),sQuery(id+"F10.wireOp",EDGE,"E113.MirrorCS"),sQuery(id+"F10.wireOp",EDGE,"E114.MirrorCS"),sQuery(id+"F10.wireOp",EDGE,"E119.MirrorCS"),sQuery(id+"F10.wireOp",EDGE,"E120.MirrorCS"),sQuery(id+"F10.wireOp",EDGE,"E121.MirrorCS"),sQuery(id+"F10.wireOp",EDGE,"E122.MirrorCS"),sQuery(id+"F10.wireOp",EDGE,"E123.MirrorCS"),sQuery(id+"F10.wireOp",EDGE,"E124.MirrorCS"),sQuery(id+"F10.wireOp",EDGE,"E131.MirrorCS"),sQuery(id+"F10.wireOp",EDGE,"E132.MirrorCS"),sQuery(id+"F10.wireOp",EDGE,"E133.MirrorCS"),sQuery(id+"F10.wireOp",EDGE,"E134.MirrorCS"),sQuery(id+"F10.wireOp",EDGE,"E135.MirrorCS"),sQuery(id+"F10.wireOp",EDGE,"E136.MirrorCS"),sQuery(id+"F10.wireOp",EDGE,"E138.MirrorCS"),sQuery(id+"F10.wireOp",EDGE,"E141.MirrorCS"),sQuery(id+"F10.wireOp",EDGE,"E142.MirrorCS"),sQuery(id+"F10.wireOp",EDGE,"E140.MirrorCS"),sQuery(id+"F10.wireOp",EDGE,"E143.MirrorCS"),sQuery(id+"F10.wireOp",EDGE,"E139.MirrorCS"),sQuery(id+"F10.wireOp",EDGE,"E144.MirrorCS"),sQuery(id+"F10.wireOp",EDGE,"E145.MirrorCS"),sQuery(id+"F10.wireOp",EDGE,"E146.MirrorCS"),sQuery(id+"F10.wireOp",EDGE,"E147.MirrorCS"),sQuery(id+"F10.wireOp",EDGE,"E149.MirrorCS"),sQuery(id+"F10.wireOp",EDGE,"E152.MirrorCS"),sQuery(id+"F10.wireOp",EDGE,"E153.MirrorCS"),sQuery(id+"F10.wireOp",EDGE,"E154.MirrorCS"),sQuery(id+"F10.wireOp",EDGE,"E155.MirrorCS"),sQuery(id+"F10.wireOp",EDGE,"E157.MirrorCS"),sQuery(id+"F10.wireOp",EDGE,"E158.MirrorCS"),sQuery(id+"F10.wireOp",EDGE,"E137.MirrorCS"),sQuery(id+"F10.wireOp",EDGE,"E159.MirrorCS"),sQuery(id+"F10.wireOp",EDGE,"E160.MirrorCS"),sQuery(id+"F10.wireOp",EDGE,"E163.MirrorCS"),sQuery(id+"F10.wireOp",EDGE,"E164.MirrorCS"),sQuery(id+"F10.wireOp",EDGE,"E165.MirrorCS"),sQuery(id+"F10.wireOp",EDGE,"E166.MirrorCS"),sQuery(id+"F10.wireOp",EDGE,"E105"),sQuery(id+"F10.wireOp",EDGE,"E104"),sQuery(id+"F10.wireOp",EDGE,"E168.MirrorCS"),sQuery(id+"F10.wireOp",EDGE,"E169.MirrorCS"),sQuery(id+"F10.wireOp",EDGE,"E170.MirrorCS"),sQuery(id+"F10.wireOp",EDGE,"E171.MirrorCS"),sQuery(id+"F10.wireOp",EDGE,"E172.MirrorCS"),sQuery(id+"F10.wireOp",EDGE,"E173.MirrorCS"),sQuery(id+"F10.wireOp",EDGE,"E174.MirrorCS"),sQuery(id+"F10.wireOp",EDGE,"E175.MirrorCS"),sQuery(id+"F10.wireOp",EDGE,"E176.MirrorCS"),sQuery(id+"F10.wireOp",EDGE,"E177.MirrorCS"),sQuery(id+"F10.wireOp",EDGE,"E178.MirrorCS"),sQuery(id+"F10.wireOp",EDGE,"E179.MirrorCS"),sQuery(id+"F10.wireOp",EDGE,"E180.MirrorCS"),sQuery(id+"F10.wireOp",EDGE,"E181.MirrorCS"),sQuery(id+"F10.wireOp",EDGE,"E182.MirrorCS"),sQuery(id+"F10.wireOp",EDGE,"E183.MirrorCS"),sQuery(id+"F10.wireOp",EDGE,"E184.MirrorCS"),sQuery(id+"F10.wireOp",EDGE,"E185.MirrorCS"),sQuery(id+"F10.wireOp",EDGE,"E186.MirrorCS"),sQuery(id+"F10.wireOp",EDGE,"E189.MirrorCS"),sQuery(id+"F10.wireOp",EDGE,"E190.MirrorCS"),sQuery(id+"F10.wireOp",EDGE,"E125.MirrorCS"),sQuery(id+"F10.wireOp",EDGE,"E193.MirrorCS"),sQuery(id+"F10.wireOp",EDGE,"E194.MirrorCS"),sQuery(id+"F10.wireOp",EDGE,"E195.MirrorCS"),sQuery(id+"F10.wireOp",EDGE,"E196.MirrorCS"),sQuery(id+"F10.wireOp",EDGE,"E197.MirrorCS"),sQuery(id+"F10.wireOp",EDGE,"E191.MirrorCS"),sQuery(id+"F10.wireOp",EDGE,"E199.MirrorCS"),sQuery(id+"F10.wireOp",EDGE,"E200.MirrorCS"),sQuery(id+"F10.wireOp",EDGE,"E201.MirrorCS"),sQuery(id+"F10.wireOp",EDGE,"E202.MirrorCS"),sQuery(id+"F10.wireOp",EDGE,"E203.MirrorCS"),sQuery(id+"F10.wireOp",EDGE,"E187.MirrorCS"),sQuery(id+"F10.wireOp",EDGE,"E192.MirrorCS"),sQuery(id+"F10.wireOp",EDGE,"E205.MirrorCS"),sQuery(id+"F10.wireOp",EDGE,"E206.MirrorCS"),sQuery(id+"F10.wireOp",EDGE,"E207.MirrorCS"),sQuery(id+"F10.wireOp",EDGE,"E208.MirrorCS"),sQuery(id+"F10.wireOp",EDGE,"E127.MirrorCS"),sQuery(id+"F10.wireOp",EDGE,"E162.MirrorCS"),sQuery(id+"F10.wireOp",EDGE,"E209.MirrorCS"),sQuery(id+"F10.wireOp",EDGE,"E210.MirrorCS"),sQuery(id+"F10.wireOp",EDGE,"E126.MirrorCS"),sQuery(id+"F10.wireOp",EDGE,"E212.MirrorCS"),sQuery(id+"F10.wireOp",EDGE,"E213.MirrorCS"),sQuery(id+"F10.wireOp",EDGE,"E214.MirrorCS"),sQuery(id+"F10.wireOp",EDGE,"E215.MirrorCS"),sQuery(id+"F10.wireOp",EDGE,"E129.MirrorCS"),sQuery(id+"F10.wireOp",EDGE,"E216.MirrorCS"),sQuery(id+"F10.wireOp",EDGE,"E217.MirrorCS"),sQuery(id+"F10.wireOp",EDGE,"E218.MirrorCS"),sQuery(id+"F10.wireOp",EDGE,"E219.MirrorCS"),sQuery(id+"F10.wireOp",EDGE,"E220.MirrorCS"),sQuery(id+"F10.wireOp",EDGE,"E221.MirrorCS"),sQuery(id+"F10.wireOp",EDGE,"E222.MirrorCS"),sQuery(id+"F10.wireOp",EDGE,"E223.MirrorCS"),sQuery(id+"F10.wireOp",EDGE,"E224.MirrorCS"),sQuery(id+"F10.wireOp",EDGE,"E225.MirrorCS"),sQuery(id+"F10.wireOp",EDGE,"E226.MirrorCS"),sQuery(id+"F10.wireOp",EDGE,"E227.MirrorCS"),sQuery(id+"F10.wireOp",EDGE,"E228.MirrorCS"),sQuery(id+"F10.wireOp",EDGE,"E229.MirrorCS"),sQuery(id+"F10.wireOp",EDGE,"E128.MirrorCS"),sQuery(id+"F10.wireOp",EDGE,"E230.MirrorCS"),sQuery(id+"F10.wireOp",EDGE,"E231.MirrorCS"),sQuery(id+"F10.wireOp",EDGE,"E232.MirrorCS"),sQuery(id+"F10.wireOp",EDGE,"E233.MirrorCS"),sQuery(id+"F10.wireOp",EDGE,"E150.MirrorCS"),sQuery(id+"F10.wireOp",EDGE,"E234.MirrorCS"),sQuery(id+"F10.wireOp",EDGE,"E211.MirrorCS"),sQuery(id+"F10.wireOp",EDGE,"E204.MirrorCS"),sQuery(id+"F10.wireOp",EDGE,"E235.MirrorCS"),sQuery(id+"F10.wireOp",EDGE,"E236.MirrorCS"),sQuery(id+"F10.wireOp",EDGE,"E237.MirrorCS"),sQuery(id+"F10.wireOp",EDGE,"E130.MirrorCS"),sQuery(id+"F10.wireOp",EDGE,"E238.MirrorCS"),sQuery(id+"F10.wireOp",EDGE,"E239.MirrorCS"),sQuery(id+"F10.wireOp",EDGE,"E240.MirrorCS"),sQuery(id+"F10.wireOp",EDGE,"E241.MirrorCS"),sQuery(id+"F10.wireOp",EDGE,"E242.MirrorCS"),sQuery(id+"F10.wireOp",EDGE,"E156.MirrorCS"),sQuery(id+"F10.wireOp",EDGE,"E243.MirrorCS"),sQuery(id+"F10.wireOp",EDGE,"E148.MirrorCS"),sQuery(id+"F10.wireOp",EDGE,"E161.MirrorCS"),sQuery(id+"F10.wireOp",EDGE,"E244.MirrorCS"),sQuery(id+"F10.wireOp",EDGE,"E245.MirrorCS"),sQuery(id+"F10.wireOp",EDGE,"E246.MirrorCS"),sQuery(id+"F10.wireOp",EDGE,"E151.MirrorCS"),sQuery(id+"F10.wireOp",EDGE,"E247.MirrorCS"),sQuery(id+"F10.wireOp",EDGE,"E248.MirrorCS"),sQuery(id+"F10.wireOp",EDGE,"E249.MirrorCS"),sQuery(id+"F10.wireOp",EDGE,"E250.MirrorCS"),sQuery(id+"F10.wireOp",EDGE,"E251.MirrorCS"),sQuery(id+"F10.wireOp",EDGE,"E252.MirrorCS"),sQuery(id+"F10.wireOp",EDGE,"E253.MirrorCS")])],"isStart":true})]});
            var sketch = newSketch(context, id + "F12", { "sketchPlane" : qUnion([Q0])});
            skArc(sketch, "E254", {"start": v(-1.7, 9.54) * mm, "mid": v(-4.84, 8.4) * mm, "end": v(-7.41, 6.24) * mm});
            skLineSegment(sketch, "E255.0", {"start": v(-0.7, 12.62) * mm, "end": v(0.7, 12.62) * mm});
            skLineSegment(sketch, "E256", {"start": v(-0.7, 12.62) * mm, "end": v(-1.7, 9.54) * mm});
            skLineSegment(sketch, "E257.MirrorCS", {"start": v(0.7, 12.62) * mm, "end": v(1.7, 9.54) * mm});
            skLineSegment(sketch, "E258", {"start": v(1.32, 2.28) * mm, "end": v(6.5, 11.25) * mm});
            skLineSegment(sketch, "E259.MirrorCS", {"start": v(1.84, 13.44) * mm, "end": v(0.7, 12.62) * mm});
            skLineSegment(sketch, "E260.MirrorCS", {"start": v(10.58, 6.92) * mm, "end": v(7.41, 6.24) * mm});
            skLineSegment(sketch, "E261.MirrorCS", {"start": v(11.28, 5.7) * mm, "end": v(9.1, 3.3) * mm});
            skLineSegment(sketch, "E262.MirrorCS", {"start": v(11.28, 5.7) * mm, "end": v(10.58, 6.92) * mm});
            skLineSegment(sketch, "E263.MirrorCS", {"start": v(11.28, -5.7) * mm, "end": v(9.1, -3.3) * mm});
            skLineSegment(sketch, "E264.MirrorCS", {"start": v(10.58, -6.92) * mm, "end": v(7.41, -6.24) * mm});
            skLineSegment(sketch, "E265.MirrorCS", {"start": v(11.28, -5.7) * mm, "end": v(10.58, -6.92) * mm});
            skLineSegment(sketch, "E266.MirrorCS", {"start": v(0.7, -12.62) * mm, "end": v(1.7, -9.54) * mm});
            skLineSegment(sketch, "E267.MirrorCS", {"start": v(-0.7, -12.62) * mm, "end": v(-1.7, -9.54) * mm});
            skLineSegment(sketch, "E268.MirrorCS", {"start": v(-0.7, -12.62) * mm, "end": v(0.7, -12.62) * mm});
            skLineSegment(sketch, "E269.MirrorCS", {"start": v(-10.58, 6.92) * mm, "end": v(-7.41, 6.24) * mm});
            skLineSegment(sketch, "E270.MirrorCS", {"start": v(-11.28, 5.7) * mm, "end": v(-10.58, 6.92) * mm});
            skLineSegment(sketch, "E271.MirrorCS", {"start": v(-11.28, 5.7) * mm, "end": v(-9.1, 3.3) * mm});
            skLineSegment(sketch, "E272.MirrorCS", {"start": v(-11.28, -5.7) * mm, "end": v(-9.1, -3.3) * mm});
            skLineSegment(sketch, "E273.MirrorCS", {"start": v(-10.58, -6.92) * mm, "end": v(-7.41, -6.24) * mm});
            skLineSegment(sketch, "E274.MirrorCS", {"start": v(-11.28, -5.7) * mm, "end": v(-10.58, -6.92) * mm});
            skArc(sketch, "E275", {"start": v(-1.14, 6.4) * mm, "mid": v(-3.25, 5.63) * mm, "end": v(-4.97, 4.18) * mm});
            skArc(sketch, "E276", {"start": v(0.46, -2.6) * mm, "mid": v(1.32, -2.28) * mm, "end": v(2.01, -1.7) * mm});
            skLineSegment(sketch, "E277", {"start": v(-1.14, 6.4) * mm, "end": v(-0.46, 2.6) * mm});
            skLineSegment(sketch, "E278", {"start": v(1.14, 6.4) * mm, "end": v(0.46, 2.6) * mm});
            skLineSegment(sketch, "E279", {"start": v(4.97, 4.18) * mm, "end": v(2.01, 1.7) * mm});
            skLineSegment(sketch, "E280", {"start": v(6.11, 2.21) * mm, "end": v(2.47, 0.9) * mm});
            skLineSegment(sketch, "E281", {"start": v(6.11, -2.21) * mm, "end": v(2.47, -0.9) * mm});
            skLineSegment(sketch, "E282", {"start": v(4.97, -4.18) * mm, "end": v(2.01, -1.7) * mm});
            skLineSegment(sketch, "E283", {"start": v(-2.01, 1.7) * mm, "end": v(-4.97, 4.18) * mm});
            skLineSegment(sketch, "E284", {"start": v(-6.11, 2.21) * mm, "end": v(-2.47, 0.9) * mm});
            skLineSegment(sketch, "E285", {"start": v(-6.11, -2.21) * mm, "end": v(-2.47, -0.9) * mm});
            skLineSegment(sketch, "E286", {"start": v(-4.97, -4.18) * mm, "end": v(-2.01, -1.7) * mm});
            skLineSegment(sketch, "E287", {"start": v(-1.14, -6.4) * mm, "end": v(-0.46, -2.6) * mm});
            skLineSegment(sketch, "E288", {"start": v(1.14, -6.4) * mm, "end": v(0.46, -2.6) * mm});
            skArc(sketch, "E289.trimOffspring", {"start": v(-6.11, 2.21) * mm, "mid": v(-6.5, 0) * mm, "end": v(-6.11, -2.21) * mm});
            skArc(sketch, "E290.trimOffspring", {"start": v(-4.97, -4.18) * mm, "mid": v(-3.25, -5.63) * mm, "end": v(-1.14, -6.4) * mm});
            skArc(sketch, "E291.trimOffspring", {"start": v(1.14, -6.4) * mm, "mid": v(3.25, -5.63) * mm, "end": v(4.97, -4.18) * mm});
            skArc(sketch, "E292.trimOffspring", {"start": v(6.11, -2.21) * mm, "mid": v(6.5, 0) * mm, "end": v(6.11, 2.21) * mm});
            skArc(sketch, "E293.trimOffspring", {"start": v(4.97, 4.18) * mm, "mid": v(3.25, 5.63) * mm, "end": v(1.14, 6.4) * mm});
            skArc(sketch, "E294.trimOffspring", {"start": v(1.7, -9.54) * mm, "mid": v(4.84, -8.4) * mm, "end": v(7.41, -6.24) * mm});
            skArc(sketch, "E295.trimOffspring", {"start": v(9.1, -3.3) * mm, "mid": v(9.69, 0) * mm, "end": v(9.1, 3.3) * mm});
            skArc(sketch, "E296.trimOffspring", {"start": v(7.41, 6.24) * mm, "mid": v(4.84, 8.4) * mm, "end": v(1.7, 9.54) * mm});
            skArc(sketch, "E297.trimOffspring", {"start": v(-9.1, 3.3) * mm, "mid": v(-9.69, 0) * mm, "end": v(-9.1, -3.3) * mm});
            skArc(sketch, "E298.trimOffspring", {"start": v(-7.41, -6.24) * mm, "mid": v(-4.84, -8.4) * mm, "end": v(-1.7, -9.54) * mm});
            skArc(sketch, "E299.trimOffspring", {"start": v(-2.01, -1.7) * mm, "mid": v(-1.32, -2.28) * mm, "end": v(-0.46, -2.6) * mm});
            skArc(sketch, "E300.trimOffspring", {"start": v(-2.47, 0.9) * mm, "mid": v(-2.63, 0) * mm, "end": v(-2.47, -0.9) * mm});
            skArc(sketch, "E301.trimOffspring", {"start": v(-0.46, 2.6) * mm, "mid": v(-1.32, 2.28) * mm, "end": v(-2.01, 1.7) * mm});
            skArc(sketch, "E302.trimOffspring", {"start": v(2.01, 1.7) * mm, "mid": v(1.32, 2.28) * mm, "end": v(0.46, 2.6) * mm});
            skArc(sketch, "E303.trimOffspring", {"start": v(2.47, -0.9) * mm, "mid": v(2.63, 0) * mm, "end": v(2.47, 0.9) * mm});
            skSolve(sketch);
        }
        {
            var Q0;
            Q0 = qSketchRegion(id + "F12", true);
            extrude(context, id + "F13", {"entities" : qUnion([Q0]), "operationType" : NewBodyOperationType.REMOVE, "oppositeDirection" : true, "depth" : 1.5 * mm, "offsetDistance" : 25.4 * mm});
        }
        {
            var Q0;
            Q0=qCreatedBy(makeId("Right.planeOp"),FACE);
            cPlane(context, id + "F14", {"entities" : qUnion([Q0]), "cplaneType" : CPlaneType.OFFSET, "offset" : 25.4 * mm, "width" : 152.4 * mm, "height" : 152.4 * mm});
        }
        {
            var Q0;
            Q0=qCreatedBy(makeId("Right.planeOp"),FACE);
            cPlane(context, id + "F15", {"entities" : qUnion([Q0]), "cplaneType" : CPlaneType.OFFSET, "offset" : 25.4 * mm, "oppositeDirection" : true, "width" : 152.4 * mm, "height" : 152.4 * mm});
        }
        {
            var Q0;
            Q0=makeQuery(id+"F1.opExtrude","SWEPT_BODY",BODY,{"disambiguationData":[OSD([sQuery(id+"F0.wireOp",EDGE,"E0"),sQuery(id+"F0.wireOp",EDGE,"E1"),sQuery(id+"F0.wireOp",EDGE,"E2"),sQuery(id+"F0.wireOp",EDGE,"E3"),sQuery(id+"F0.wireOp",EDGE,"E4"),sQuery(id+"F0.wireOp",EDGE,"E5")])]});
            var Q1;
            Q1=qCreatedBy(id+"F14.planeOp",FACE);
            mirror(context, id + "F16", {"entities" : qUnion([Q0]), "mirrorPlane" : qUnion([Q1])});
        }
        {
            var Q0;
            Q0=makeQuery(id+"F1.opExtrude","SWEPT_BODY",BODY,{"disambiguationData":[OSD([sQuery(id+"F0.wireOp",EDGE,"E0"),sQuery(id+"F0.wireOp",EDGE,"E1"),sQuery(id+"F0.wireOp",EDGE,"E2"),sQuery(id+"F0.wireOp",EDGE,"E3"),sQuery(id+"F0.wireOp",EDGE,"E4"),sQuery(id+"F0.wireOp",EDGE,"E5")])]});
            var Q1;
            Q1=makeQuery(id+"F16.opPattern","COPY",BODY,{"derivedFrom":makeQuery(id+"F1.opExtrude","SWEPT_BODY",BODY,{"disambiguationData":[OSD([sQuery(id+"F0.wireOp",EDGE,"E0"),sQuery(id+"F0.wireOp",EDGE,"E1"),sQuery(id+"F0.wireOp",EDGE,"E2"),sQuery(id+"F0.wireOp",EDGE,"E3"),sQuery(id+"F0.wireOp",EDGE,"E4"),sQuery(id+"F0.wireOp",EDGE,"E5")])]}),"instanceName":"1"});
            var Q2;
            Q2=qCreatedBy(id+"F15.planeOp",FACE);
            mirror(context, id + "F17", {"entities" : qUnion([Q0, Q1]), "mirrorPlane" : qUnion([Q2])});
        }
        {
            var Q0;
            Q0=qCreatedBy(makeId("Top.planeOp"),FACE);
            cPlane(context, id + "F18", {"entities" : qUnion([Q0]), "cplaneType" : CPlaneType.OFFSET, "offset" : 25.4 * mm, "width" : 152.4 * mm, "height" : 152.4 * mm});
        }
        {
            var Q0;
            Q0=makeQuery(id+"F17.opPattern","COPY",BODY,{"derivedFrom":makeQuery(id+"F1.opExtrude","SWEPT_BODY",BODY,{"disambiguationData":[OSD([sQuery(id+"F0.wireOp",EDGE,"E0"),sQuery(id+"F0.wireOp",EDGE,"E1"),sQuery(id+"F0.wireOp",EDGE,"E2"),sQuery(id+"F0.wireOp",EDGE,"E3"),sQuery(id+"F0.wireOp",EDGE,"E4"),sQuery(id+"F0.wireOp",EDGE,"E5")])]}),"instanceName":"1"});
            var Q1;
            Q1=makeQuery(id+"F1.opExtrude","SWEPT_BODY",BODY,{"disambiguationData":[OSD([sQuery(id+"F0.wireOp",EDGE,"E0"),sQuery(id+"F0.wireOp",EDGE,"E1"),sQuery(id+"F0.wireOp",EDGE,"E2"),sQuery(id+"F0.wireOp",EDGE,"E3"),sQuery(id+"F0.wireOp",EDGE,"E4"),sQuery(id+"F0.wireOp",EDGE,"E5")])]});
            var Q2;
            Q2=makeQuery(id+"F16.opPattern","COPY",BODY,{"derivedFrom":makeQuery(id+"F1.opExtrude","SWEPT_BODY",BODY,{"disambiguationData":[OSD([sQuery(id+"F0.wireOp",EDGE,"E0"),sQuery(id+"F0.wireOp",EDGE,"E1"),sQuery(id+"F0.wireOp",EDGE,"E2"),sQuery(id+"F0.wireOp",EDGE,"E3"),sQuery(id+"F0.wireOp",EDGE,"E4"),sQuery(id+"F0.wireOp",EDGE,"E5")])]}),"instanceName":"1"});
            var Q3;
            Q3=makeQuery(id+"F17.opPattern","COPY",BODY,{"derivedFrom":makeQuery(id+"F16.opPattern","COPY",BODY,{"derivedFrom":makeQuery(id+"F1.opExtrude","SWEPT_BODY",BODY,{"disambiguationData":[OSD([sQuery(id+"F0.wireOp",EDGE,"E0"),sQuery(id+"F0.wireOp",EDGE,"E1"),sQuery(id+"F0.wireOp",EDGE,"E2"),sQuery(id+"F0.wireOp",EDGE,"E3"),sQuery(id+"F0.wireOp",EDGE,"E4"),sQuery(id+"F0.wireOp",EDGE,"E5")])]}),"instanceName":"1"}),"instanceName":"1"});
            var Q4;
            Q4=qCreatedBy(id+"F18.planeOp",FACE);
            mirror(context, id + "F19", {"entities" : qUnion([Q0, Q1, Q2, Q3]), "mirrorPlane" : qUnion([Q4])});
        }
        {
            var Q0;
            Q0=makeQuery(id+"F17.opPattern","COPY",FACE,{"derivedFrom":makeQuery(id+"F16.opPattern","COPY",FACE,{"derivedFrom":makeQuery(id+"F9.opExtrude","CAP_FACE",FACE,{"disambiguationData":[OSD([sQuery(id+"F8.wireOp",EDGE,"E20.0"),sQuery(id+"F8.wireOp",EDGE,"E20.1"),sQuery(id+"F8.wireOp",EDGE,"E21.0"),sQuery(id+"F8.wireOp",EDGE,"E21.1"),sQuery(id+"F8.wireOp",EDGE,"E22"),sQuery(id+"F8.wireOp",EDGE,"E23"),sQuery(id+"F8.wireOp",EDGE,"E24"),sQuery(id+"F8.wireOp",EDGE,"E25"),sQuery(id+"F8.wireOp",EDGE,"E26.0"),sQuery(id+"F8.wireOp",EDGE,"E28"),sQuery(id+"F8.wireOp",EDGE,"E29"),sQuery(id+"F8.wireOp",EDGE,"E32"),sQuery(id+"F8.wireOp",EDGE,"E33.0"),sQuery(id+"F8.wireOp",EDGE,"E36"),sQuery(id+"F8.wireOp",EDGE,"E37"),sQuery(id+"F8.wireOp",EDGE,"E38.trimOffspring"),sQuery(id+"F8.wireOp",EDGE,"E39.trimOffspring"),sQuery(id+"F8.wireOp",EDGE,"E40.trimOffspring"),sQuery(id+"F8.wireOp",EDGE,"E41.trimOffspring"),sQuery(id+"F8.wireOp",EDGE,"E42"),sQuery(id+"F8.wireOp",EDGE,"E43"),sQuery(id+"F8.wireOp",EDGE,"E44"),sQuery(id+"F8.wireOp",EDGE,"E45.trimOffspring"),sQuery(id+"F8.wireOp",EDGE,"E46"),sQuery(id+"F8.wireOp",EDGE,"E47"),sQuery(id+"F8.wireOp",EDGE,"E48.trimOffspring"),sQuery(id+"F8.wireOp",EDGE,"E49.trimOffspring"),sQuery(id+"F8.wireOp",EDGE,"E50.MirrorCS"),sQuery(id+"F8.wireOp",EDGE,"E51.MirrorCS"),sQuery(id+"F8.wireOp",EDGE,"E52.MirrorCS"),sQuery(id+"F8.wireOp",EDGE,"E53.MirrorCS"),sQuery(id+"F8.wireOp",EDGE,"E54.MirrorCS"),sQuery(id+"F8.wireOp",EDGE,"E55.MirrorCS"),sQuery(id+"F8.wireOp",EDGE,"E56.MirrorCS"),sQuery(id+"F8.wireOp",EDGE,"E57.MirrorCS"),sQuery(id+"F8.wireOp",EDGE,"E58.MirrorCS"),sQuery(id+"F8.wireOp",EDGE,"E59.MirrorCS"),sQuery(id+"F8.wireOp",EDGE,"E61.trimOffspring"),sQuery(id+"F8.wireOp",EDGE,"E62.trimOffspring"),sQuery(id+"F8.wireOp",EDGE,"E63")])],"isStart":false}),"instanceName":"1"}),"instanceName":"1"});
            var sketch = newSketch(context, id + "F20", { "sketchPlane" : qUnion([Q0])});
            skCircle(sketch, "E304.0.0", {"center": v(-101.6, 0) * mm, "radius": 10.03 * mm});
            skCircle(sketch, "E305.0.0", {"center": v(0, 0) * mm, "radius": 10.03 * mm});
            skCircle(sketch, "E306.0.0", {"center": v(50.8, 0) * mm, "radius": 10.03 * mm});
            skCircle(sketch, "E307.0.0", {"center": v(50.8, 50.8) * mm, "radius": 10.03 * mm});
            skCircle(sketch, "E308.0.0", {"center": v(0, 50.8) * mm, "radius": 10.03 * mm});
            skCircle(sketch, "E309.0.0", {"center": v(-50.8, 50.8) * mm, "radius": 10.03 * mm});
            skCircle(sketch, "E310.0.0", {"center": v(-101.6, 50.8) * mm, "radius": 10.03 * mm});
            skSolve(sketch);
        }
        {
            var Q0;
            Q0 = qSketchRegion(id + "F20", true);
            var Q1;
            {var subQ0=sQuery(id+"F4.wireOp",EDGE,"E8");Q1=makeQuery(id+"F19.opPattern","COPY",FACE,{"derivedFrom":makeQuery(id+"F17.opPattern","COPY",FACE,{"derivedFrom":makeQuery(id+"F9.boolean.opBoolean","SPLIT",FACE,{"disambiguationData":[TD([makeQuery(id+"F5.boolean.opBoolean","COPY",FACE,{"derivedFrom":makeQuery(id+"F5.opExtrude","SWEPT_FACE",FACE,{"disambiguationData":[OSD([subQ0])]})})])],"derivedFrom":makeQuery(id+"F5.boolean.opBoolean","COPY",FACE,{"derivedFrom":makeQuery(id+"F5.opExtrude","CAP_FACE",FACE,{"disambiguationData":[OSD([subQ0])],"isStart":false})})}),"instanceName":"1"}),"instanceName":"1"});}
            extrude(context, id + "F21", {"entities" : qUnion([Q0]), "operationType" : NewBodyOperationType.REMOVE, "endBound" : BoundingType.UP_TO_SURFACE, "oppositeDirection" : true, "depth" : 25.4 * mm, "endBoundEntityFace" : qUnion([Q1]), "offsetDistance" : 25.4 * mm});
        }
        {
            var Q0;
            {var subQ0=sQuery(id+"F4.wireOp",EDGE,"E8");var subQ1=makeQuery(id+"F5.boolean.opBoolean","COPY",FACE,{"derivedFrom":makeQuery(id+"F5.opExtrude","CAP_FACE",FACE,{"disambiguationData":[OSD([subQ0])],"isStart":false})});Q0=makeQuery(id+"F21.boolean.opBoolean","MERGE",FACE,{"derivedFrom":[makeQuery(id+"F9.boolean.opBoolean","SPLIT",FACE,{"disambiguationData":[TD([makeQuery(id+"F5.boolean.opBoolean","COPY",FACE,{"derivedFrom":makeQuery(id+"F5.opExtrude","SWEPT_FACE",FACE,{"disambiguationData":[OSD([subQ0])]})})])],"derivedFrom":subQ1}),makeQuery(id+"F9.boolean.opBoolean","SPLIT",FACE,{"disambiguationData":[TD([makeQuery(id+"F9.opExtrude","SWEPT_FACE",FACE,{"disambiguationData":[OSD([sQuery(id+"F8.wireOp",EDGE,"E25")])]})])],"derivedFrom":subQ1}),makeQuery(id+"F9.boolean.opBoolean","SPLIT",FACE,{"disambiguationData":[TD([makeQuery(id+"F9.opExtrude","SWEPT_FACE",FACE,{"disambiguationData":[OSD([sQuery(id+"F8.wireOp",EDGE,"E32")])]})])],"derivedFrom":subQ1}),makeQuery(id+"F9.boolean.opBoolean","SPLIT",FACE,{"disambiguationData":[TD([makeQuery(id+"F9.opExtrude","SWEPT_FACE",FACE,{"disambiguationData":[OSD([sQuery(id+"F8.wireOp",EDGE,"E33.0")])]})])],"derivedFrom":subQ1}),makeQuery(id+"F9.boolean.opBoolean","SPLIT",FACE,{"disambiguationData":[TD([makeQuery(id+"F9.opExtrude","SWEPT_FACE",FACE,{"disambiguationData":[OSD([sQuery(id+"F8.wireOp",EDGE,"E37")])]})])],"derivedFrom":subQ1}),makeQuery(id+"F9.boolean.opBoolean","SPLIT",FACE,{"disambiguationData":[TD([makeQuery(id+"F9.opExtrude","SWEPT_FACE",FACE,{"disambiguationData":[OSD([sQuery(id+"F8.wireOp",EDGE,"E51.MirrorCS")])]})])],"derivedFrom":subQ1}),makeQuery(id+"F9.boolean.opBoolean","SPLIT",FACE,{"disambiguationData":[TD([makeQuery(id+"F9.opExtrude","SWEPT_FACE",FACE,{"disambiguationData":[OSD([sQuery(id+"F8.wireOp",EDGE,"E53.MirrorCS")])]})])],"derivedFrom":subQ1}),makeQuery(id+"F9.boolean.opBoolean","SPLIT",FACE,{"disambiguationData":[TD([makeQuery(id+"F9.opExtrude","SWEPT_FACE",FACE,{"disambiguationData":[OSD([sQuery(id+"F8.wireOp",EDGE,"E80")])]})])],"derivedFrom":subQ1}),makeQuery(id+"F9.boolean.opBoolean","SPLIT",FACE,{"disambiguationData":[TD([makeQuery(id+"F9.opExtrude","SWEPT_FACE",FACE,{"disambiguationData":[OSD([sQuery(id+"F8.wireOp",EDGE,"E83")])]})])],"derivedFrom":subQ1}),makeQuery(id+"F21.opExtrude","CAP_FACE",FACE,{"disambiguationData":[OSD([sQuery(id+"F20.wireOp",EDGE,"E305.0.0")])],"isStart":false})]});}
            var sketch = newSketch(context, id + "F22", { "sketchPlane" : qUnion([Q0])});
            skArc(sketch, "E311", {"start": v(-0.67, 3.34) * mm, "mid": v(-3.74, -2.49) * mm, "end": v(2.8, -1.7) * mm});
            skArc(sketch, "E312", {"start": v(5.27, 2.55) * mm, "mid": v(2.33, 3.2) * mm, "end": v(-0.67, 3.34) * mm});
            skArc(sketch, "E313", {"start": v(3.6, 1.23) * mm, "mid": v(2.01, 0.08) * mm, "end": v(2.8, -1.7) * mm});
            skArc(sketch, "E314", {"start": v(3.46, 1.23) * mm, "mid": v(4.6, 1.57) * mm, "end": v(5.27, 2.55) * mm});
            skArc(sketch, "E315", {"start": v(6.62, -2.1) * mm, "mid": v(6.93, 0.5) * mm, "end": v(6.25, 3.03) * mm});
            skArc(sketch, "E316", {"start": v(-5.73, -3.93) * mm, "mid": v(-4.84, -1.7) * mm, "end": v(-6.93, -0.53) * mm});
            skArc(sketch, "E317", {"start": v(6.62, -2.1) * mm, "mid": v(3.7, -2.77) * mm, "end": v(3.88, -5.77) * mm});
            skCircle(sketch, "E318", {"center": v(0.42, -5.27) * mm, "radius": 0.87 * mm});
            skArc(sketch, "E319", {"start": v(-5.04, 4.78) * mm, "mid": v(-2.35, 3.28) * mm, "end": v(-2.91, 6.3) * mm});
            skArc(sketch, "E320", {"start": v(0.53, 6.93) * mm, "mid": v(1.66, 5.79) * mm, "end": v(3.22, 6.16) * mm});
            skCircle(sketch, "E321", {"center": v(5.2, 5.53) * mm, "radius": 0.47 * mm});
            skArc(sketch, "E322", {"start": v(-1.94, 7.64) * mm, "mid": v(-2.51, 8.61) * mm, "end": v(-2.55, 7.49) * mm});
            skCircle(sketch, "E323", {"center": v(-0.71, 7.86) * mm, "radius": 0.32 * mm});
            skCircle(sketch, "E324", {"center": v(-6.05, 6.24) * mm, "radius": 0.31 * mm});
            skArc(sketch, "E325", {"start": v(-7.6, 3.42) * mm, "mid": v(-8.51, 3.8) * mm, "end": v(-8.02, 2.94) * mm});
            skCircle(sketch, "E326", {"center": v(7.6, 2.4) * mm, "radius": 0.95 * mm});
            skCircle(sketch, "E327", {"center": v(7.33, 0.94) * mm, "radius": 0.4 * mm});
            skArc(sketch, "E328.trimOffspring", {"start": v(0.53, 6.93) * mm, "mid": v(-1.23, 6.84) * mm, "end": v(-2.91, 6.3) * mm});
            skArc(sketch, "E329.trimOffspring", {"start": v(-5.04, 4.78) * mm, "mid": v(-6.55, 2.32) * mm, "end": v(-6.93, -0.53) * mm});
            skArc(sketch, "E330.trimOffspring", {"start": v(-5.73, -3.93) * mm, "mid": v(-5.5, -4.26) * mm, "end": v(-5.24, -4.56) * mm});
            skArc(sketch, "E331", {"start": v(5.18, 4.63) * mm, "mid": v(4.97, 3.33) * mm, "end": v(6.25, 3.03) * mm});
            skArc(sketch, "E332.trimOffspring", {"start": v(5.18, 4.63) * mm, "mid": v(4.27, 5.48) * mm, "end": v(3.22, 6.16) * mm});
            skCircle(sketch, "E333", {"center": v(0.27, 5.22) * mm, "radius": 0.9 * mm});
            skCircle(sketch, "E334", {"center": v(2.3, 4.32) * mm, "radius": 0.42 * mm});
            skCircle(sketch, "E335", {"center": v(3.54, 5.04) * mm, "radius": 0.26 * mm});
            skArc(sketch, "E336", {"start": v(-3.3, -6.11) * mm, "mid": v(-3.8, -4.74) * mm, "end": v(-5.24, -4.56) * mm});
            skCircle(sketch, "E337", {"center": v(-2.22, -5.08) * mm, "radius": 0.63 * mm});
            skCircle(sketch, "E338", {"center": v(1.32, -8.35) * mm, "radius": 0.93 * mm});
            skArc(sketch, "E339", {"start": v(5.13, -5.84) * mm, "mid": v(6.76, -6.51) * mm, "end": v(5.85, -5) * mm});
            skCircle(sketch, "E340", {"center": v(4.06, -3.84) * mm, "radius": 0.58 * mm});
            skCircle(sketch, "E341", {"center": v(3.61, -6.8) * mm, "radius": 0.56 * mm});
            skCircle(sketch, "E342", {"center": v(7.82, -2.33) * mm, "radius": 1 * mm});
            skArc(sketch, "E343", {"start": v(-7.57, -0.73) * mm, "mid": v(-8.84, -1.17) * mm, "end": v(-7.62, -1.73) * mm});
            skCircle(sketch, "E344", {"center": v(-7.67, 0.75) * mm, "radius": 0.4 * mm});
            skArc(sketch, "E345", {"start": v(-7.9, -3.53) * mm, "mid": v(-8.52, -4.4) * mm, "end": v(-7.44, -4.45) * mm});
            skCircle(sketch, "E346", {"center": v(-2.48, -6.92) * mm, "radius": 0.35 * mm});
            skCircle(sketch, "E347", {"center": v(-3.68, -8.24) * mm, "radius": 0.24 * mm});
            skArc(sketch, "E348.trimOffspring", {"start": v(-3.3, -6.11) * mm, "mid": v(0.34, -6.94) * mm, "end": v(3.88, -5.77) * mm});
            skCircle(sketch, "E349", {"center": v(-6.39, -5.42) * mm, "radius": 0.79 * mm});
            skCircle(sketch, "E350", {"center": v(-0.75, -2.97) * mm, "radius": 0.8 * mm});
            skCircle(sketch, "E351", {"center": v(-2.3, -2.3) * mm, "radius": 0.8 * mm});
            skCircle(sketch, "E352", {"center": v(-3.38, -0.5) * mm, "radius": 0.8 * mm});
            skCircle(sketch, "E353", {"center": v(-2, 1.84) * mm, "radius": 0.8 * mm});
            skArc(sketch, "E354", {"start": v(-2.55, 7.49) * mm, "mid": v(-2.14, 7.16) * mm, "end": v(-1.94, 7.64) * mm});
            skArc(sketch, "E355", {"start": v(-8.02, 2.94) * mm, "mid": v(-7.47, 2.88) * mm, "end": v(-7.6, 3.42) * mm});
            skArc(sketch, "E356", {"start": v(-7.62, -1.73) * mm, "mid": v(-6.86, -1.26) * mm, "end": v(-7.57, -0.73) * mm});
            skArc(sketch, "E357", {"start": v(-7.44, -4.45) * mm, "mid": v(-6.9, -3.61) * mm, "end": v(-7.9, -3.53) * mm});
            skCircle(sketch, "E358", {"center": v(-5.91, -3) * mm, "radius": 0.32 * mm});
            skArc(sketch, "E359", {"start": v(5.85, -5) * mm, "mid": v(4.91, -4.92) * mm, "end": v(5.13, -5.84) * mm});
            skCircle(sketch, "E360", {"center": v(-2.1, -7.9) * mm, "radius": 0.66 * mm});
            skCircle(sketch, "E361", {"center": v(-3.9, 5.53) * mm, "radius": 0.55 * mm});
            skArc(sketch, "E362", {"start": v(3.68, 7.97) * mm, "mid": v(3.84, 9) * mm, "end": v(3, 8.37) * mm});
            skArc(sketch, "E363", {"start": v(3, 8.37) * mm, "mid": v(3.04, 7.66) * mm, "end": v(3.68, 7.97) * mm});
            skSolve(sketch);
        }
        {
            var Q0;
            Q0 = qSketchRegion(id + "F22", true);
            var Q1;
            Q1=makeQuery(id+"F17.opPattern","COPY",FACE,{"derivedFrom":makeQuery(id+"F9.opExtrude","CAP_FACE",FACE,{"disambiguationData":[OSD([sQuery(id+"F8.wireOp",EDGE,"E20.0"),sQuery(id+"F8.wireOp",EDGE,"E20.1"),sQuery(id+"F8.wireOp",EDGE,"E21.0"),sQuery(id+"F8.wireOp",EDGE,"E21.1"),sQuery(id+"F8.wireOp",EDGE,"E22"),sQuery(id+"F8.wireOp",EDGE,"E23"),sQuery(id+"F8.wireOp",EDGE,"E24"),sQuery(id+"F8.wireOp",EDGE,"E25"),sQuery(id+"F8.wireOp",EDGE,"E26.0"),sQuery(id+"F8.wireOp",EDGE,"E28"),sQuery(id+"F8.wireOp",EDGE,"E29"),sQuery(id+"F8.wireOp",EDGE,"E32"),sQuery(id+"F8.wireOp",EDGE,"E33.0"),sQuery(id+"F8.wireOp",EDGE,"E36"),sQuery(id+"F8.wireOp",EDGE,"E37"),sQuery(id+"F8.wireOp",EDGE,"E38.trimOffspring"),sQuery(id+"F8.wireOp",EDGE,"E39.trimOffspring"),sQuery(id+"F8.wireOp",EDGE,"E40.trimOffspring"),sQuery(id+"F8.wireOp",EDGE,"E41.trimOffspring"),sQuery(id+"F8.wireOp",EDGE,"E42"),sQuery(id+"F8.wireOp",EDGE,"E43"),sQuery(id+"F8.wireOp",EDGE,"E44"),sQuery(id+"F8.wireOp",EDGE,"E45.trimOffspring"),sQuery(id+"F8.wireOp",EDGE,"E46"),sQuery(id+"F8.wireOp",EDGE,"E47"),sQuery(id+"F8.wireOp",EDGE,"E48.trimOffspring"),sQuery(id+"F8.wireOp",EDGE,"E49.trimOffspring"),sQuery(id+"F8.wireOp",EDGE,"E50.MirrorCS"),sQuery(id+"F8.wireOp",EDGE,"E51.MirrorCS"),sQuery(id+"F8.wireOp",EDGE,"E52.MirrorCS"),sQuery(id+"F8.wireOp",EDGE,"E53.MirrorCS"),sQuery(id+"F8.wireOp",EDGE,"E54.MirrorCS"),sQuery(id+"F8.wireOp",EDGE,"E55.MirrorCS"),sQuery(id+"F8.wireOp",EDGE,"E56.MirrorCS"),sQuery(id+"F8.wireOp",EDGE,"E57.MirrorCS"),sQuery(id+"F8.wireOp",EDGE,"E58.MirrorCS"),sQuery(id+"F8.wireOp",EDGE,"E59.MirrorCS"),sQuery(id+"F8.wireOp",EDGE,"E61.trimOffspring"),sQuery(id+"F8.wireOp",EDGE,"E62.trimOffspring"),sQuery(id+"F8.wireOp",EDGE,"E63")])],"isStart":false}),"instanceName":"1"});
            extrude(context, id + "F23", {"entities" : qUnion([Q0]), "operationType" : NewBodyOperationType.ADD, "endBound" : BoundingType.UP_TO_SURFACE, "depth" : 25.4 * mm, "endBoundEntityFace" : qUnion([Q1]), "offsetDistance" : 25.4 * mm});
        }
        {
            var Q0;
            Q0=makeQuery(id+"F23.opExtrude","SWEPT_EDGE",EDGE,{"disambiguationData":[OSD([sQuery(id+"F22.wireOp",EDGE,"E312"),sQuery(id+"F22.wireOp",EDGE,"E314")])]});
            var Q1;
            Q1=makeQuery(id+"F23.opExtrude","SWEPT_EDGE",EDGE,{"disambiguationData":[OSD([sQuery(id+"F22.wireOp",EDGE,"E311"),sQuery(id+"F22.wireOp",EDGE,"E313")])]});
            var Q2;
            Q2=makeQuery(id+"F23.opExtrude","SWEPT_EDGE",EDGE,{"disambiguationData":[OSD([sQuery(id+"F22.wireOp",EDGE,"E319"),sQuery(id+"F22.wireOp",EDGE,"E329.trimOffspring")])]});
            var Q3;
            Q3=makeQuery(id+"F23.opExtrude","SWEPT_EDGE",EDGE,{"disambiguationData":[OSD([sQuery(id+"F22.wireOp",EDGE,"E316"),sQuery(id+"F22.wireOp",EDGE,"E329.trimOffspring")])]});
            var Q4;
            Q4=makeQuery(id+"F23.opExtrude","SWEPT_EDGE",EDGE,{"disambiguationData":[OSD([sQuery(id+"F22.wireOp",EDGE,"E316"),sQuery(id+"F22.wireOp",EDGE,"E330.trimOffspring")])]});
            var Q5;
            Q5=makeQuery(id+"F23.opExtrude","SWEPT_EDGE",EDGE,{"disambiguationData":[OSD([sQuery(id+"F22.wireOp",EDGE,"E336"),sQuery(id+"F22.wireOp",EDGE,"E348.trimOffspring")])]});
            var Q6;
            Q6=makeQuery(id+"F23.opExtrude","SWEPT_EDGE",EDGE,{"disambiguationData":[OSD([sQuery(id+"F22.wireOp",EDGE,"E315"),sQuery(id+"F22.wireOp",EDGE,"E317")])]});
            var Q7;
            Q7=makeQuery(id+"F23.opExtrude","SWEPT_EDGE",EDGE,{"disambiguationData":[OSD([sQuery(id+"F22.wireOp",EDGE,"E320"),sQuery(id+"F22.wireOp",EDGE,"E328.trimOffspring")])]});
            var Q8;
            Q8=makeQuery(id+"F23.opExtrude","SWEPT_EDGE",EDGE,{"disambiguationData":[OSD([sQuery(id+"F22.wireOp",EDGE,"E320"),sQuery(id+"F22.wireOp",EDGE,"E332.trimOffspring")])]});
            var Q9;
            Q9=makeQuery(id+"F23.opExtrude","SWEPT_EDGE",EDGE,{"disambiguationData":[OSD([sQuery(id+"F22.wireOp",EDGE,"E331"),sQuery(id+"F22.wireOp",EDGE,"E332.trimOffspring")])]});
            var Q10;
            Q10=makeQuery(id+"F23.opExtrude","SWEPT_EDGE",EDGE,{"disambiguationData":[OSD([sQuery(id+"F22.wireOp",EDGE,"E315"),sQuery(id+"F22.wireOp",EDGE,"E331")])]});
            var Q11;
            Q11=makeQuery(id+"F23.opExtrude","SWEPT_EDGE",EDGE,{"disambiguationData":[OSD([sQuery(id+"F22.wireOp",EDGE,"E319"),sQuery(id+"F22.wireOp",EDGE,"E328.trimOffspring")])]});
            var Q12;
            Q12=makeQuery(id+"F23.opExtrude","SWEPT_EDGE",EDGE,{"disambiguationData":[OSD([sQuery(id+"F22.wireOp",EDGE,"E317"),sQuery(id+"F22.wireOp",EDGE,"E348.trimOffspring")])]});
            fillet(context, id + "F24", {"entities" : qUnion([Q0, Q1, Q2, Q3, Q4, Q5, Q6, Q7, Q8, Q9, Q10, Q11, Q12]), "radius" : 0.7 * mm, "tangentPropagation" : true, "allowEdgeOverflow" : false});
        }
        {
            var Q0;
            {var subQ0=sQuery(id+"F4.wireOp",EDGE,"E8");var subQ1=makeQuery(id+"F5.boolean.opBoolean","COPY",FACE,{"derivedFrom":makeQuery(id+"F5.opExtrude","CAP_FACE",FACE,{"disambiguationData":[OSD([subQ0])],"isStart":false})});Q0=makeQuery(id+"F23.boolean.opBoolean","SPLIT",FACE,{"disambiguationData":[TD([makeQuery(id+"F23.opExtrude","SWEPT_FACE",FACE,{"disambiguationData":[OSD([sQuery(id+"F22.wireOp",EDGE,"E311")])]})])],"derivedFrom":makeQuery(id+"F21.boolean.opBoolean","MERGE",FACE,{"derivedFrom":[makeQuery(id+"F9.boolean.opBoolean","SPLIT",FACE,{"disambiguationData":[TD([makeQuery(id+"F5.boolean.opBoolean","COPY",FACE,{"derivedFrom":makeQuery(id+"F5.opExtrude","SWEPT_FACE",FACE,{"disambiguationData":[OSD([subQ0])]})})])],"derivedFrom":subQ1}),makeQuery(id+"F9.boolean.opBoolean","SPLIT",FACE,{"disambiguationData":[TD([makeQuery(id+"F9.opExtrude","SWEPT_FACE",FACE,{"disambiguationData":[OSD([sQuery(id+"F8.wireOp",EDGE,"E25")])]})])],"derivedFrom":subQ1}),makeQuery(id+"F9.boolean.opBoolean","SPLIT",FACE,{"disambiguationData":[TD([makeQuery(id+"F9.opExtrude","SWEPT_FACE",FACE,{"disambiguationData":[OSD([sQuery(id+"F8.wireOp",EDGE,"E32")])]})])],"derivedFrom":subQ1}),makeQuery(id+"F9.boolean.opBoolean","SPLIT",FACE,{"disambiguationData":[TD([makeQuery(id+"F9.opExtrude","SWEPT_FACE",FACE,{"disambiguationData":[OSD([sQuery(id+"F8.wireOp",EDGE,"E33.0")])]})])],"derivedFrom":subQ1}),makeQuery(id+"F9.boolean.opBoolean","SPLIT",FACE,{"disambiguationData":[TD([makeQuery(id+"F9.opExtrude","SWEPT_FACE",FACE,{"disambiguationData":[OSD([sQuery(id+"F8.wireOp",EDGE,"E37")])]})])],"derivedFrom":subQ1}),makeQuery(id+"F9.boolean.opBoolean","SPLIT",FACE,{"disambiguationData":[TD([makeQuery(id+"F9.opExtrude","SWEPT_FACE",FACE,{"disambiguationData":[OSD([sQuery(id+"F8.wireOp",EDGE,"E51.MirrorCS")])]})])],"derivedFrom":subQ1}),makeQuery(id+"F9.boolean.opBoolean","SPLIT",FACE,{"disambiguationData":[TD([makeQuery(id+"F9.opExtrude","SWEPT_FACE",FACE,{"disambiguationData":[OSD([sQuery(id+"F8.wireOp",EDGE,"E53.MirrorCS")])]})])],"derivedFrom":subQ1}),makeQuery(id+"F9.boolean.opBoolean","SPLIT",FACE,{"disambiguationData":[TD([makeQuery(id+"F9.opExtrude","SWEPT_FACE",FACE,{"disambiguationData":[OSD([sQuery(id+"F8.wireOp",EDGE,"E80")])]})])],"derivedFrom":subQ1}),makeQuery(id+"F9.boolean.opBoolean","SPLIT",FACE,{"disambiguationData":[TD([makeQuery(id+"F9.opExtrude","SWEPT_FACE",FACE,{"disambiguationData":[OSD([sQuery(id+"F8.wireOp",EDGE,"E83")])]})])],"derivedFrom":subQ1})],"fromTools":[makeQuery(id+"F21.opExtrude","CAP_FACE",FACE,{"disambiguationData":[OSD([sQuery(id+"F20.wireOp",EDGE,"E305.0.0")])],"isStart":false})]})});}
            var sketch = newSketch(context, id + "F25", { "sketchPlane" : qUnion([Q0])});
            skArc(sketch, "E364", {"start": v(-2, 2.18) * mm, "mid": v(-2.85, -1.4) * mm, "end": v(0.44, -3.03) * mm});
            skCircle(sketch, "E365", {"center": v(-0.44, -3.08) * mm, "radius": 0.61 * mm});
            skCircle(sketch, "E366", {"center": v(-2.2, -2.3) * mm, "radius": 0.61 * mm});
            skCircle(sketch, "E367", {"center": v(-3.07, -0.73) * mm, "radius": 0.61 * mm});
            skCircle(sketch, "E368", {"center": v(-2.94, 0.9) * mm, "radius": 0.61 * mm});
            skCircle(sketch, "E369", {"center": v(-2, 2.18) * mm, "radius": 0.61 * mm});
            skSolve(sketch);
        }
        {
            var Q0;
            Q0 = qSketchRegion(id + "F25", true);
            var Q1;
            Q1=makeQuery(id+"F23.opExtrude","CAP_FACE",FACE,{"disambiguationData":[OSD([sQuery(id+"F22.wireOp",EDGE,"E311"),sQuery(id+"F22.wireOp",EDGE,"E312"),sQuery(id+"F22.wireOp",EDGE,"E313"),sQuery(id+"F22.wireOp",EDGE,"E314"),sQuery(id+"F22.wireOp",EDGE,"E315"),sQuery(id+"F22.wireOp",EDGE,"E316"),sQuery(id+"F22.wireOp",EDGE,"E317"),sQuery(id+"F22.wireOp",EDGE,"E318"),sQuery(id+"F22.wireOp",EDGE,"E319"),sQuery(id+"F22.wireOp",EDGE,"E320"),sQuery(id+"F22.wireOp",EDGE,"E328.trimOffspring"),sQuery(id+"F22.wireOp",EDGE,"E329.trimOffspring"),sQuery(id+"F22.wireOp",EDGE,"E330.trimOffspring"),sQuery(id+"F22.wireOp",EDGE,"E331"),sQuery(id+"F22.wireOp",EDGE,"E332.trimOffspring"),sQuery(id+"F22.wireOp",EDGE,"E333"),sQuery(id+"F22.wireOp",EDGE,"E334"),sQuery(id+"F22.wireOp",EDGE,"E335"),sQuery(id+"F22.wireOp",EDGE,"E336"),sQuery(id+"F22.wireOp",EDGE,"E337"),sQuery(id+"F22.wireOp",EDGE,"E348.trimOffspring")])],"isStart":false});
            extrude(context, id + "F26", {"entities" : qUnion([Q0]), "operationType" : NewBodyOperationType.ADD, "depth" : 0.5 * mm, "endBoundEntityFace" : qUnion([Q1]), "offsetDistance" : 25.4 * mm});
        }
        {
            var Q0;
            {var subQ0=sQuery(id+"F4.wireOp",EDGE,"E8");var subQ1=makeQuery(id+"F5.boolean.opBoolean","COPY",FACE,{"derivedFrom":makeQuery(id+"F5.opExtrude","CAP_FACE",FACE,{"disambiguationData":[OSD([subQ0])],"isStart":false})});Q0=makeQuery(id+"F21.boolean.opBoolean","MERGE",FACE,{"derivedFrom":[makeQuery(id+"F16.opPattern","COPY",FACE,{"derivedFrom":makeQuery(id+"F9.boolean.opBoolean","SPLIT",FACE,{"disambiguationData":[TD([makeQuery(id+"F5.boolean.opBoolean","COPY",FACE,{"derivedFrom":makeQuery(id+"F5.opExtrude","SWEPT_FACE",FACE,{"disambiguationData":[OSD([subQ0])]})})])],"derivedFrom":subQ1}),"instanceName":"1"}),makeQuery(id+"F16.opPattern","COPY",FACE,{"derivedFrom":makeQuery(id+"F9.boolean.opBoolean","SPLIT",FACE,{"disambiguationData":[TD([makeQuery(id+"F9.opExtrude","SWEPT_FACE",FACE,{"disambiguationData":[OSD([sQuery(id+"F8.wireOp",EDGE,"E25")])]})])],"derivedFrom":subQ1}),"instanceName":"1"}),makeQuery(id+"F16.opPattern","COPY",FACE,{"derivedFrom":makeQuery(id+"F9.boolean.opBoolean","SPLIT",FACE,{"disambiguationData":[TD([makeQuery(id+"F9.opExtrude","SWEPT_FACE",FACE,{"disambiguationData":[OSD([sQuery(id+"F8.wireOp",EDGE,"E32")])]})])],"derivedFrom":subQ1}),"instanceName":"1"}),makeQuery(id+"F16.opPattern","COPY",FACE,{"derivedFrom":makeQuery(id+"F9.boolean.opBoolean","SPLIT",FACE,{"disambiguationData":[TD([makeQuery(id+"F9.opExtrude","SWEPT_FACE",FACE,{"disambiguationData":[OSD([sQuery(id+"F8.wireOp",EDGE,"E33.0")])]})])],"derivedFrom":subQ1}),"instanceName":"1"}),makeQuery(id+"F16.opPattern","COPY",FACE,{"derivedFrom":makeQuery(id+"F9.boolean.opBoolean","SPLIT",FACE,{"disambiguationData":[TD([makeQuery(id+"F9.opExtrude","SWEPT_FACE",FACE,{"disambiguationData":[OSD([sQuery(id+"F8.wireOp",EDGE,"E37")])]})])],"derivedFrom":subQ1}),"instanceName":"1"}),makeQuery(id+"F16.opPattern","COPY",FACE,{"derivedFrom":makeQuery(id+"F9.boolean.opBoolean","SPLIT",FACE,{"disambiguationData":[TD([makeQuery(id+"F9.opExtrude","SWEPT_FACE",FACE,{"disambiguationData":[OSD([sQuery(id+"F8.wireOp",EDGE,"E51.MirrorCS")])]})])],"derivedFrom":subQ1}),"instanceName":"1"}),makeQuery(id+"F16.opPattern","COPY",FACE,{"derivedFrom":makeQuery(id+"F9.boolean.opBoolean","SPLIT",FACE,{"disambiguationData":[TD([makeQuery(id+"F9.opExtrude","SWEPT_FACE",FACE,{"disambiguationData":[OSD([sQuery(id+"F8.wireOp",EDGE,"E53.MirrorCS")])]})])],"derivedFrom":subQ1}),"instanceName":"1"}),makeQuery(id+"F16.opPattern","COPY",FACE,{"derivedFrom":makeQuery(id+"F9.boolean.opBoolean","SPLIT",FACE,{"disambiguationData":[TD([makeQuery(id+"F9.opExtrude","SWEPT_FACE",FACE,{"disambiguationData":[OSD([sQuery(id+"F8.wireOp",EDGE,"E80")])]})])],"derivedFrom":subQ1}),"instanceName":"1"}),makeQuery(id+"F16.opPattern","COPY",FACE,{"derivedFrom":makeQuery(id+"F9.boolean.opBoolean","SPLIT",FACE,{"disambiguationData":[TD([makeQuery(id+"F9.opExtrude","SWEPT_FACE",FACE,{"disambiguationData":[OSD([sQuery(id+"F8.wireOp",EDGE,"E83")])]})])],"derivedFrom":subQ1}),"instanceName":"1"}),makeQuery(id+"F21.opExtrude","CAP_FACE",FACE,{"disambiguationData":[OSD([sQuery(id+"F20.wireOp",EDGE,"E306.0.0")])],"isStart":false})]});}
            var sketch = newSketch(context, id + "F27", { "sketchPlane" : qUnion([Q0])});
            skPoint(sketch, "E370.0", {"position": v(50.8, 12.7) * mm});
            skLineSegment(sketch, "E371", {"start": v(50.8, 12.7) * mm, "end": v(50.8, -3.45) * mm});
            skArc(sketch, "E372", {"start": v(43.3, -3.45) * mm, "mid": v(50.8, -7.63) * mm, "end": v(58.3, -3.45) * mm});
            skArc(sketch, "E373", {"start": v(42.27, -1.05) * mm, "mid": v(50.8, -7.63) * mm, "end": v(59.33, -1.05) * mm});
            skPoint(sketch, "E373.third.point", {"position": v(55.77, -6.1) * mm});
            skArc(sketch, "E374", {"start": v(42.7, -0.86) * mm, "mid": v(50.8, -4.67) * mm, "end": v(58.9, -0.86) * mm});
            skArc(sketch, "E375", {"start": v(42.8, -0.76) * mm, "mid": v(50.8, -3.9) * mm, "end": v(58.8, -0.76) * mm});
            skArc(sketch, "E376", {"start": v(42.1, -1.07) * mm, "mid": v(50.8, -8.88) * mm, "end": v(59.5, -1.07) * mm});
            skArc(sketch, "E377", {"start": v(42.8, -0.76) * mm, "mid": v(41.63, 0.98) * mm, "end": v(42.1, -1.07) * mm});
            skArc(sketch, "E378.MirrorC", {"start": v(58.8, -0.76) * mm, "mid": v(59.97, 0.98) * mm, "end": v(59.5, -1.07) * mm});
            skArc(sketch, "E379.trimOffspring", {"start": v(42.27, -1.05) * mm, "mid": v(42.5, -0.98) * mm, "end": v(42.7, -0.86) * mm});
            skArc(sketch, "E380.trimOffspring", {"start": v(59.33, -1.05) * mm, "mid": v(59.1, -0.98) * mm, "end": v(58.9, -0.86) * mm});
            skArc(sketch, "E381", {"start": v(45.17, 4.91) * mm, "mid": v(44.11, 2.68) * mm, "end": v(45.17, 0.44) * mm});
            skCircle(sketch, "E382", {"center": v(47, 2.68) * mm, "radius": 2.34 * mm});
            skCircle(sketch, "E383", {"center": v(47, 2.68) * mm, "radius": 1.22 * mm});
            skArc(sketch, "E384", {"start": v(47, -1.91) * mm, "mid": v(46.03, -0.5) * mm, "end": v(44.86, 0.73) * mm});
            skArc(sketch, "E385.MirrorCS", {"start": v(47, -1.91) * mm, "mid": v(47.97, -0.5) * mm, "end": v(49.13, 0.73) * mm});
            skArc(sketch, "E386.MirrorCS", {"start": v(47, 7.27) * mm, "mid": v(46.03, 5.86) * mm, "end": v(44.86, 4.62) * mm});
            skArc(sketch, "E387.MirrorCS", {"start": v(47, 7.27) * mm, "mid": v(47.97, 5.86) * mm, "end": v(49.13, 4.62) * mm});
            skArc(sketch, "E388.trimOffspring", {"start": v(48.83, 0.44) * mm, "mid": v(49.89, 2.68) * mm, "end": v(48.83, 4.91) * mm});
            skArc(sketch, "E389", {"start": v(52.82, 2.92) * mm, "mid": v(55.31, 1) * mm, "end": v(57.82, 2.9) * mm});
            skArc(sketch, "E390", {"start": v(52.82, 2.92) * mm, "mid": v(55.32, 1.66) * mm, "end": v(57.82, 2.9) * mm});
            skArc(sketch, "E391", {"start": v(54.91, -0.44) * mm, "mid": v(55.46, -1.77) * mm, "end": v(56.01, -0.44) * mm});
            skLineSegment(sketch, "E392", {"start": v(54.91, -0.44) * mm, "end": v(55.46, 0.1) * mm});
            skLineSegment(sketch, "E393.MirrorCS", {"start": v(56.01, -0.44) * mm, "end": v(55.46, 0.1) * mm});
            skSolve(sketch);
        }
        {
            var Q0;
            Q0 = qSketchRegion(id + "F27", true);
            var Q1;
            Q1=makeQuery(id+"F23.opExtrude","CAP_FACE",FACE,{"disambiguationData":[OSD([sQuery(id+"F22.wireOp",EDGE,"E338")])],"isStart":false});
            extrude(context, id + "F28", {"entities" : qUnion([Q0]), "operationType" : NewBodyOperationType.ADD, "endBound" : BoundingType.UP_TO_SURFACE, "depth" : 25.4 * mm, "endBoundEntityFace" : qUnion([Q1]), "offsetDistance" : 25.4 * mm});
        }
        {
            var Q0;
            {var subQ0=sQuery(id+"F4.wireOp",EDGE,"E8");var subQ1=makeQuery(id+"F5.boolean.opBoolean","COPY",FACE,{"derivedFrom":makeQuery(id+"F5.opExtrude","SWEPT_FACE",FACE,{"disambiguationData":[OSD([subQ0])]})});var subQ2=makeQuery(id+"F5.boolean.opBoolean","COPY",FACE,{"derivedFrom":makeQuery(id+"F5.opExtrude","CAP_FACE",FACE,{"disambiguationData":[OSD([subQ0])],"isStart":false})});Q0=makeQuery(id+"F28.boolean.opBoolean","SPLIT",FACE,{"disambiguationData":[TD([makeQuery(id+"F16.opPattern","COPY",FACE,{"derivedFrom":subQ1,"instanceName":"1"})])],"derivedFrom":makeQuery(id+"F21.boolean.opBoolean","MERGE",FACE,{"derivedFrom":[makeQuery(id+"F16.opPattern","COPY",FACE,{"derivedFrom":makeQuery(id+"F9.boolean.opBoolean","SPLIT",FACE,{"disambiguationData":[TD([subQ1])],"derivedFrom":subQ2}),"instanceName":"1"}),makeQuery(id+"F16.opPattern","COPY",FACE,{"derivedFrom":makeQuery(id+"F9.boolean.opBoolean","SPLIT",FACE,{"disambiguationData":[TD([makeQuery(id+"F9.opExtrude","SWEPT_FACE",FACE,{"disambiguationData":[OSD([sQuery(id+"F8.wireOp",EDGE,"E25")])]})])],"derivedFrom":subQ2}),"instanceName":"1"}),makeQuery(id+"F16.opPattern","COPY",FACE,{"derivedFrom":makeQuery(id+"F9.boolean.opBoolean","SPLIT",FACE,{"disambiguationData":[TD([makeQuery(id+"F9.opExtrude","SWEPT_FACE",FACE,{"disambiguationData":[OSD([sQuery(id+"F8.wireOp",EDGE,"E32")])]})])],"derivedFrom":subQ2}),"instanceName":"1"}),makeQuery(id+"F16.opPattern","COPY",FACE,{"derivedFrom":makeQuery(id+"F9.boolean.opBoolean","SPLIT",FACE,{"disambiguationData":[TD([makeQuery(id+"F9.opExtrude","SWEPT_FACE",FACE,{"disambiguationData":[OSD([sQuery(id+"F8.wireOp",EDGE,"E33.0")])]})])],"derivedFrom":subQ2}),"instanceName":"1"}),makeQuery(id+"F16.opPattern","COPY",FACE,{"derivedFrom":makeQuery(id+"F9.boolean.opBoolean","SPLIT",FACE,{"disambiguationData":[TD([makeQuery(id+"F9.opExtrude","SWEPT_FACE",FACE,{"disambiguationData":[OSD([sQuery(id+"F8.wireOp",EDGE,"E37")])]})])],"derivedFrom":subQ2}),"instanceName":"1"}),makeQuery(id+"F16.opPattern","COPY",FACE,{"derivedFrom":makeQuery(id+"F9.boolean.opBoolean","SPLIT",FACE,{"disambiguationData":[TD([makeQuery(id+"F9.opExtrude","SWEPT_FACE",FACE,{"disambiguationData":[OSD([sQuery(id+"F8.wireOp",EDGE,"E51.MirrorCS")])]})])],"derivedFrom":subQ2}),"instanceName":"1"}),makeQuery(id+"F16.opPattern","COPY",FACE,{"derivedFrom":makeQuery(id+"F9.boolean.opBoolean","SPLIT",FACE,{"disambiguationData":[TD([makeQuery(id+"F9.opExtrude","SWEPT_FACE",FACE,{"disambiguationData":[OSD([sQuery(id+"F8.wireOp",EDGE,"E53.MirrorCS")])]})])],"derivedFrom":subQ2}),"instanceName":"1"}),makeQuery(id+"F16.opPattern","COPY",FACE,{"derivedFrom":makeQuery(id+"F9.boolean.opBoolean","SPLIT",FACE,{"disambiguationData":[TD([makeQuery(id+"F9.opExtrude","SWEPT_FACE",FACE,{"disambiguationData":[OSD([sQuery(id+"F8.wireOp",EDGE,"E80")])]})])],"derivedFrom":subQ2}),"instanceName":"1"}),makeQuery(id+"F16.opPattern","COPY",FACE,{"derivedFrom":makeQuery(id+"F9.boolean.opBoolean","SPLIT",FACE,{"disambiguationData":[TD([makeQuery(id+"F9.opExtrude","SWEPT_FACE",FACE,{"disambiguationData":[OSD([sQuery(id+"F8.wireOp",EDGE,"E83")])]})])],"derivedFrom":subQ2}),"instanceName":"1"})],"fromTools":[makeQuery(id+"F21.opExtrude","CAP_FACE",FACE,{"disambiguationData":[OSD([sQuery(id+"F20.wireOp",EDGE,"E306.0.0")])],"isStart":false})]})});}
            var sketch = newSketch(context, id + "F29", { "sketchPlane" : qUnion([Q0])});
            skCircle(sketch, "E394", {"center": v(47, 2.68) * mm, "radius": 0.79 * mm});
            skArc(sketch, "E395", {"start": v(57.8, 4.5) * mm, "mid": v(55.15, 5.33) * mm, "end": v(52.42, 4.76) * mm});
            skLineSegment(sketch, "E396", {"start": v(52.42, 4.76) * mm, "end": v(51.97, 5.66) * mm});
            skLineSegment(sketch, "E397", {"start": v(57.8, 4.5) * mm, "end": v(58.33, 5.36) * mm});
            skLineSegment(sketch, "E398", {"start": v(51.97, 5.66) * mm, "end": v(51.45, 6.69) * mm});
            skLineSegment(sketch, "E399", {"start": v(51.45, 6.69) * mm, "end": v(52.34, 7.14) * mm});
            skLineSegment(sketch, "E400", {"start": v(58.33, 5.36) * mm, "end": v(58.56, 5.73) * mm});
            skLineSegment(sketch, "E401", {"start": v(58.56, 5.73) * mm, "end": v(57.7, 6.26) * mm});
            skLineSegment(sketch, "E402", {"start": v(57.7, 6.26) * mm, "end": v(56.9, 4.95) * mm});
            skLineSegment(sketch, "E403", {"start": v(55.57, 5.3) * mm, "end": v(55.57, 7.13) * mm});
            skLineSegment(sketch, "E404", {"start": v(55.57, 7.13) * mm, "end": v(54.57, 7.13) * mm});
            skLineSegment(sketch, "E405", {"start": v(54.57, 7.13) * mm, "end": v(54.57, 5.32) * mm});
            skLineSegment(sketch, "E406", {"start": v(52.34, 7.14) * mm, "end": v(53.36, 5.12) * mm});
            skSolve(sketch);
        }
        {
            var Q0;
            Q0 = qSketchRegion(id + "F29", true);
            extrude(context, id + "F30", {"entities" : qUnion([Q0]), "operationType" : NewBodyOperationType.ADD, "depth" : 1 * mm, "offsetDistance" : 25.4 * mm});
        }
        {
            var Q0;
            {var subQ0=sQuery(id+"F4.wireOp",EDGE,"E8");var subQ1=makeQuery(id+"F5.boolean.opBoolean","COPY",FACE,{"derivedFrom":makeQuery(id+"F5.opExtrude","CAP_FACE",FACE,{"disambiguationData":[OSD([subQ0])],"isStart":false})});Q0=makeQuery(id+"F21.boolean.opBoolean","MERGE",FACE,{"derivedFrom":[makeQuery(id+"F17.opPattern","COPY",FACE,{"derivedFrom":makeQuery(id+"F16.opPattern","COPY",FACE,{"derivedFrom":makeQuery(id+"F9.boolean.opBoolean","SPLIT",FACE,{"disambiguationData":[TD([makeQuery(id+"F5.boolean.opBoolean","COPY",FACE,{"derivedFrom":makeQuery(id+"F5.opExtrude","SWEPT_FACE",FACE,{"disambiguationData":[OSD([subQ0])]})})])],"derivedFrom":subQ1}),"instanceName":"1"}),"instanceName":"1"}),makeQuery(id+"F17.opPattern","COPY",FACE,{"derivedFrom":makeQuery(id+"F16.opPattern","COPY",FACE,{"derivedFrom":makeQuery(id+"F9.boolean.opBoolean","SPLIT",FACE,{"disambiguationData":[TD([makeQuery(id+"F9.opExtrude","SWEPT_FACE",FACE,{"disambiguationData":[OSD([sQuery(id+"F8.wireOp",EDGE,"E25")])]})])],"derivedFrom":subQ1}),"instanceName":"1"}),"instanceName":"1"}),makeQuery(id+"F17.opPattern","COPY",FACE,{"derivedFrom":makeQuery(id+"F16.opPattern","COPY",FACE,{"derivedFrom":makeQuery(id+"F9.boolean.opBoolean","SPLIT",FACE,{"disambiguationData":[TD([makeQuery(id+"F9.opExtrude","SWEPT_FACE",FACE,{"disambiguationData":[OSD([sQuery(id+"F8.wireOp",EDGE,"E32")])]})])],"derivedFrom":subQ1}),"instanceName":"1"}),"instanceName":"1"}),makeQuery(id+"F17.opPattern","COPY",FACE,{"derivedFrom":makeQuery(id+"F16.opPattern","COPY",FACE,{"derivedFrom":makeQuery(id+"F9.boolean.opBoolean","SPLIT",FACE,{"disambiguationData":[TD([makeQuery(id+"F9.opExtrude","SWEPT_FACE",FACE,{"disambiguationData":[OSD([sQuery(id+"F8.wireOp",EDGE,"E33.0")])]})])],"derivedFrom":subQ1}),"instanceName":"1"}),"instanceName":"1"}),makeQuery(id+"F17.opPattern","COPY",FACE,{"derivedFrom":makeQuery(id+"F16.opPattern","COPY",FACE,{"derivedFrom":makeQuery(id+"F9.boolean.opBoolean","SPLIT",FACE,{"disambiguationData":[TD([makeQuery(id+"F9.opExtrude","SWEPT_FACE",FACE,{"disambiguationData":[OSD([sQuery(id+"F8.wireOp",EDGE,"E37")])]})])],"derivedFrom":subQ1}),"instanceName":"1"}),"instanceName":"1"}),makeQuery(id+"F17.opPattern","COPY",FACE,{"derivedFrom":makeQuery(id+"F16.opPattern","COPY",FACE,{"derivedFrom":makeQuery(id+"F9.boolean.opBoolean","SPLIT",FACE,{"disambiguationData":[TD([makeQuery(id+"F9.opExtrude","SWEPT_FACE",FACE,{"disambiguationData":[OSD([sQuery(id+"F8.wireOp",EDGE,"E51.MirrorCS")])]})])],"derivedFrom":subQ1}),"instanceName":"1"}),"instanceName":"1"}),makeQuery(id+"F17.opPattern","COPY",FACE,{"derivedFrom":makeQuery(id+"F16.opPattern","COPY",FACE,{"derivedFrom":makeQuery(id+"F9.boolean.opBoolean","SPLIT",FACE,{"disambiguationData":[TD([makeQuery(id+"F9.opExtrude","SWEPT_FACE",FACE,{"disambiguationData":[OSD([sQuery(id+"F8.wireOp",EDGE,"E53.MirrorCS")])]})])],"derivedFrom":subQ1}),"instanceName":"1"}),"instanceName":"1"}),makeQuery(id+"F17.opPattern","COPY",FACE,{"derivedFrom":makeQuery(id+"F16.opPattern","COPY",FACE,{"derivedFrom":makeQuery(id+"F9.boolean.opBoolean","SPLIT",FACE,{"disambiguationData":[TD([makeQuery(id+"F9.opExtrude","SWEPT_FACE",FACE,{"disambiguationData":[OSD([sQuery(id+"F8.wireOp",EDGE,"E80")])]})])],"derivedFrom":subQ1}),"instanceName":"1"}),"instanceName":"1"}),makeQuery(id+"F17.opPattern","COPY",FACE,{"derivedFrom":makeQuery(id+"F16.opPattern","COPY",FACE,{"derivedFrom":makeQuery(id+"F9.boolean.opBoolean","SPLIT",FACE,{"disambiguationData":[TD([makeQuery(id+"F9.opExtrude","SWEPT_FACE",FACE,{"disambiguationData":[OSD([sQuery(id+"F8.wireOp",EDGE,"E83")])]})])],"derivedFrom":subQ1}),"instanceName":"1"}),"instanceName":"1"}),makeQuery(id+"F21.opExtrude","CAP_FACE",FACE,{"disambiguationData":[OSD([sQuery(id+"F20.wireOp",EDGE,"E304.0.0")])],"isStart":false})]});}
            var sketch = newSketch(context, id + "F31", { "sketchPlane" : qUnion([Q0])});
            skPoint(sketch, "E407.0", {"position": v(-92.68, -4.57) * mm});
            skPoint(sketch, "E408.0", {"position": v(-110.52, 4.57) * mm});
            skPoint(sketch, "E409.0", {"position": v(-110.02, 5.44) * mm});
            skPoint(sketch, "E410.0", {"position": v(-93.18, -5.44) * mm});
            skLineSegment(sketch, "E411", {"start": v(-96.84, -2.17) * mm, "end": v(-104.5, 2.26) * mm});
            skArc(sketch, "E412", {"start": v(-97.34, -3.04) * mm, "mid": v(-94.65, -4.01) * mm, "end": v(-96.84, -2.17) * mm});
            skPoint(sketch, "E413.orphan", {"position": v(-96.16, -3.72) * mm});
            skPoint(sketch, "E414.end.orphan", {"position": v(-95.66, -2.85) * mm});
            skLineSegment(sketch, "E415", {"start": v(-106.27, 2.7) * mm, "end": v(-103.75, 1.24) * mm});
            skArc(sketch, "E416", {"start": v(-107.57, 2.87) * mm, "mid": v(-105.13, 2.04) * mm, "end": v(-107.07, 3.73) * mm});
            skLineSegment(sketch, "E417", {"start": v(-107.52, 4) * mm, "end": v(-106.43, 5.89) * mm});
            skLineSegment(sketch, "E418", {"start": v(-106.43, 5.89) * mm, "end": v(-103.76, 4.34) * mm});
            skLineSegment(sketch, "E419.MirrorCS", {"start": v(-104.5, 2.26) * mm, "end": v(-103.42, 4.15) * mm});
            skLineSegment(sketch, "E420", {"start": v(-103.76, 4.34) * mm, "end": v(-103.42, 4.15) * mm});
            skLineSegment(sketch, "E421", {"start": v(-106.16, 6.36) * mm, "end": v(-105.9, 6.82) * mm});
            skLineSegment(sketch, "E422", {"start": v(-105.9, 6.82) * mm, "end": v(-102.63, 4.94) * mm});
            skLineSegment(sketch, "E423", {"start": v(-103.14, 4.62) * mm, "end": v(-102.53, 5.68) * mm});
            skLineSegment(sketch, "E424", {"start": v(-103.14, 4.62) * mm, "end": v(-106.81, 6.74) * mm});
            skLineSegment(sketch, "E425.trimOffspring", {"start": v(-107.07, 3.73) * mm, "end": v(-107.52, 4) * mm});
            skPoint(sketch, "E426.orphan", {"position": v(-106.02, 3.13) * mm});
            skPoint(sketch, "E427.end.orphan", {"position": v(-106.52, 2.26) * mm});
            skLineSegment(sketch, "E428.trimOffspring", {"start": v(-105.47, 1.65) * mm, "end": v(-97.34, -3.04) * mm});
            skLineSegment(sketch, "E429.MirrorCS", {"start": v(-105, 1.4) * mm, "end": v(-106.1, -0.5) * mm});
            skLineSegment(sketch, "E430.MirrorCS", {"start": v(-109.12, 1.24) * mm, "end": v(-106.44, -0.3) * mm});
            skLineSegment(sketch, "E431.MirrorCS", {"start": v(-106.44, -0.3) * mm, "end": v(-106.1, -0.5) * mm});
            skLineSegment(sketch, "E432.MirrorCS", {"start": v(-108.02, 3.13) * mm, "end": v(-109.12, 1.24) * mm});
            skLineSegment(sketch, "E433.MirrorCS", {"start": v(-107.57, 2.87) * mm, "end": v(-108.02, 3.13) * mm});
            skLineSegment(sketch, "E434.MirrorCS", {"start": v(-106.37, -0.98) * mm, "end": v(-110.04, 1.14) * mm});
            skLineSegment(sketch, "E435.MirrorCS", {"start": v(-106.37, -0.98) * mm, "end": v(-106.99, -2.04) * mm});
            skLineSegment(sketch, "E436.MirrorCS", {"start": v(-109.66, 0.3) * mm, "end": v(-106.39, -1.58) * mm});
            skLineSegment(sketch, "E437.MirrorCS", {"start": v(-109.4, 0.77) * mm, "end": v(-109.66, 0.3) * mm});
            skLineSegment(sketch, "E438", {"start": v(-109.5, 3.31) * mm, "end": v(-108.42, 5.18) * mm});
            skLineSegment(sketch, "E439", {"start": v(-106.27, 2.7) * mm, "end": v(-108.96, 4.25) * mm});
            skLineSegment(sketch, "E440", {"start": v(-109.5, 3.31) * mm, "end": v(-108.57, 2.78) * mm});
            skLineSegment(sketch, "E441", {"start": v(-108.57, 2.78) * mm, "end": v(-107.4, 4.8) * mm});
            skLineSegment(sketch, "E442", {"start": v(-108.42, 5.18) * mm, "end": v(-107.5, 4.65) * mm});
            skCircle(sketch, "E443", {"center": v(-95.9, -3.29) * mm, "radius": 0.96 * mm});
            skArc(sketch, "E444", {"start": v(-101.17, -3.03) * mm, "mid": v(-101.6, -2.81) * mm, "end": v(-102.06, -2.66) * mm});
            skArc(sketch, "E445", {"start": v(-104.91, -2.45) * mm, "mid": v(-105.45, -2.9) * mm, "end": v(-105.9, -3.43) * mm});
            skLineSegment(sketch, "E446.left", {"start": v(-103.44, -1.01) * mm, "end": v(-103.44, -2.66) * mm});
            skLineSegment(sketch, "E446.right", {"start": v(-102.06, -1.01) * mm, "end": v(-102.06, -2.66) * mm});
            skLineSegment(sketch, "E447.MirrorCS", {"start": v(-100, -1.86) * mm, "end": v(-101.17, -3.03) * mm});
            skLineSegment(sketch, "E448.MirrorCS", {"start": v(-99.02, -2.84) * mm, "end": v(-100.19, -4.01) * mm});
            skLineSegment(sketch, "E449.MirrorCS", {"start": v(-98.17, -4.9) * mm, "end": v(-99.82, -4.9) * mm});
            skLineSegment(sketch, "E450.MirrorCS", {"start": v(-98.17, -6.29) * mm, "end": v(-99.82, -6.29) * mm});
            skLineSegment(sketch, "E451.MirrorCS", {"start": v(-105.5, -1.86) * mm, "end": v(-104.33, -3.03) * mm});
            skLineSegment(sketch, "E452.MirrorCS", {"start": v(-106.48, -2.84) * mm, "end": v(-105.31, -4.01) * mm});
            skLineSegment(sketch, "E453.trimOffspring", {"start": v(-105.68, -4.9) * mm, "end": v(-107.33, -4.9) * mm});
            skLineSegment(sketch, "E454.trimOffspring", {"start": v(-105.68, -6.29) * mm, "end": v(-107.33, -6.29) * mm});
            skLineSegment(sketch, "E455.trimOffspring", {"start": v(-105.31, -7.18) * mm, "end": v(-106.48, -8.35) * mm});
            skLineSegment(sketch, "E456.trimOffspring", {"start": v(-104.33, -8.16) * mm, "end": v(-105.5, -9.33) * mm});
            skLineSegment(sketch, "E457.trimOffspring", {"start": v(-103.44, -8.53) * mm, "end": v(-103.44, -10.18) * mm});
            skLineSegment(sketch, "E458.trimOffspring", {"start": v(-102.06, -8.53) * mm, "end": v(-102.06, -10.18) * mm});
            skLineSegment(sketch, "E459.trimOffspring", {"start": v(-101.17, -8.16) * mm, "end": v(-100, -9.33) * mm});
            skLineSegment(sketch, "E460.trimOffspring", {"start": v(-100.19, -7.18) * mm, "end": v(-99.02, -8.35) * mm});
            skArc(sketch, "E461.trimOffspring", {"start": v(-106.5, -4.9) * mm, "mid": v(-106.57, -5.6) * mm, "end": v(-106.5, -6.29) * mm});
            skArc(sketch, "E462.trimOffspring", {"start": v(-105.9, -7.76) * mm, "mid": v(-105.45, -8.3) * mm, "end": v(-104.91, -8.74) * mm});
            skArc(sketch, "E463.trimOffspring", {"start": v(-103.44, -9.35) * mm, "mid": v(-102.75, -9.41) * mm, "end": v(-102.06, -9.35) * mm});
            skArc(sketch, "E464.trimOffspring", {"start": v(-100.59, -8.74) * mm, "mid": v(-100.05, -8.3) * mm, "end": v(-99.6, -7.76) * mm});
            skArc(sketch, "E465.trimOffspring", {"start": v(-99, -6.29) * mm, "mid": v(-98.93, -5.6) * mm, "end": v(-99, -4.9) * mm});
            skArc(sketch, "E466.trimOffspring", {"start": v(-99.6, -3.43) * mm, "mid": v(-100.05, -2.9) * mm, "end": v(-100.59, -2.45) * mm});
            skArc(sketch, "E467.trimOffspring", {"start": v(-102.06, -1.84) * mm, "mid": v(-102.75, -1.78) * mm, "end": v(-103.44, -1.84) * mm});
            skArc(sketch, "E468.trimOffspring", {"start": v(-103.44, -2.66) * mm, "mid": v(-103.9, -2.81) * mm, "end": v(-104.33, -3.03) * mm});
            skArc(sketch, "E469.trimOffspring", {"start": v(-105.31, -4.01) * mm, "mid": v(-105.53, -4.44) * mm, "end": v(-105.68, -4.9) * mm});
            skArc(sketch, "E470.trimOffspring", {"start": v(-105.68, -6.29) * mm, "mid": v(-105.53, -6.75) * mm, "end": v(-105.31, -7.18) * mm});
            skArc(sketch, "E471.trimOffspring", {"start": v(-104.33, -8.16) * mm, "mid": v(-103.9, -8.38) * mm, "end": v(-103.44, -8.53) * mm});
            skArc(sketch, "E472.trimOffspring", {"start": v(-102.06, -8.53) * mm, "mid": v(-101.6, -8.38) * mm, "end": v(-101.17, -8.16) * mm});
            skArc(sketch, "E473.trimOffspring", {"start": v(-100.19, -7.18) * mm, "mid": v(-99.97, -6.75) * mm, "end": v(-99.82, -6.29) * mm});
            skArc(sketch, "E474.trimOffspring", {"start": v(-99.82, -4.9) * mm, "mid": v(-99.97, -4.44) * mm, "end": v(-100.19, -4.01) * mm});
            skCircle(sketch, "E475", {"center": v(-102.75, -5.6) * mm, "radius": 1.53 * mm});
            skArc(sketch, "E476.MirrorCS", {"start": v(-94.45, 4.66) * mm, "mid": v(-94.34, 4.19) * mm, "end": v(-94.32, 3.7) * mm});
            skArc(sketch, "E477.MirrorCS", {"start": v(-99.98, 5.22) * mm, "mid": v(-99.72, 5.63) * mm, "end": v(-99.4, 5.99) * mm});
            skArc(sketch, "E478.MirrorCS", {"start": v(-100.22, 2.93) * mm, "mid": v(-100.32, 3.4) * mm, "end": v(-100.34, 3.88) * mm});
            skArc(sketch, "E479.MirrorCS", {"start": v(-96.47, 0.9) * mm, "mid": v(-96.94, 0.8) * mm, "end": v(-97.42, 0.78) * mm});
            skArc(sketch, "E480.MirrorCS", {"start": v(-98.2, 6.68) * mm, "mid": v(-97.72, 6.78) * mm, "end": v(-97.24, 6.8) * mm});
            skArc(sketch, "E481.MirrorCS", {"start": v(-98.76, 1.14) * mm, "mid": v(-99.16, 1.4) * mm, "end": v(-99.52, 1.73) * mm});
            skArc(sketch, "E482.MirrorCS", {"start": v(-95.9, 6.45) * mm, "mid": v(-95.5, 6.18) * mm, "end": v(-95.14, 5.86) * mm});
            skArc(sketch, "E483.MirrorCS", {"start": v(-94.68, 2.37) * mm, "mid": v(-94.94, 1.96) * mm, "end": v(-95.26, 1.6) * mm});
            skLineSegment(sketch, "E484.MirrorCS", {"start": v(-99.4, 5.99) * mm, "end": v(-100.22, 7.42) * mm});
            skLineSegment(sketch, "E485.MirrorCS", {"start": v(-94.32, 3.7) * mm, "end": v(-92.72, 3.28) * mm});
            skLineSegment(sketch, "E486.MirrorCS", {"start": v(-101.65, 2.1) * mm, "end": v(-100.22, 2.93) * mm});
            skLineSegment(sketch, "E487.MirrorCS", {"start": v(-95.64, -0.52) * mm, "end": v(-96.47, 0.9) * mm});
            skLineSegment(sketch, "E488.MirrorCS", {"start": v(-101.58, 5.65) * mm, "end": v(-99.98, 5.22) * mm});
            skLineSegment(sketch, "E489.MirrorCS", {"start": v(-95.9, 6.45) * mm, "end": v(-95.47, 8.04) * mm});
            skLineSegment(sketch, "E490.MirrorCS", {"start": v(-94.45, 4.66) * mm, "end": v(-93.01, 5.49) * mm});
            skLineSegment(sketch, "E491.MirrorCS", {"start": v(-94.44, 0.17) * mm, "end": v(-95.26, 1.6) * mm});
            skLineSegment(sketch, "E492.MirrorCS", {"start": v(-98.2, 6.68) * mm, "end": v(-99.02, 8.1) * mm});
            skLineSegment(sketch, "E493.MirrorCS", {"start": v(-97.85, -0.81) * mm, "end": v(-97.42, 0.78) * mm});
            skLineSegment(sketch, "E494.MirrorCS", {"start": v(-95.14, 5.86) * mm, "end": v(-93.7, 6.69) * mm});
            skLineSegment(sketch, "E495.MirrorCS", {"start": v(-97.24, 6.8) * mm, "end": v(-96.81, 8.4) * mm});
            skLineSegment(sketch, "E496.MirrorCS", {"start": v(-99.19, -0.45) * mm, "end": v(-98.76, 1.14) * mm});
            skLineSegment(sketch, "E497.MirrorCS", {"start": v(-100.95, 0.9) * mm, "end": v(-99.52, 1.73) * mm});
            skLineSegment(sketch, "E498.MirrorCS", {"start": v(-101.94, 4.31) * mm, "end": v(-100.34, 3.88) * mm});
            skLineSegment(sketch, "E499.MirrorCS", {"start": v(-94.68, 2.37) * mm, "end": v(-93.08, 1.94) * mm});
            skArc(sketch, "E500.MirrorCS", {"start": v(-94.85, 0.9) * mm, "mid": v(-95.42, 0.49) * mm, "end": v(-96.05, 0.2) * mm});
            skArc(sketch, "E501.MirrorCS", {"start": v(-97.63, 0) * mm, "mid": v(-98.32, 0.1) * mm, "end": v(-98.97, 0.35) * mm});
            skArc(sketch, "E502.MirrorCS", {"start": v(-97.03, 7.6) * mm, "mid": v(-96.34, 7.48) * mm, "end": v(-95.69, 7.24) * mm});
            skArc(sketch, "E503.MirrorCS", {"start": v(-94.43, 6.27) * mm, "mid": v(-94.03, 5.7) * mm, "end": v(-93.73, 5.07) * mm});
            skLineSegment(sketch, "E504.MirrorCS", {"start": v(-97.34, -3.04) * mm, "end": v(-105, 1.4) * mm});
            skArc(sketch, "E505.MirrorCS", {"start": v(-99.8, 6.7) * mm, "mid": v(-99.24, 7.1) * mm, "end": v(-98.6, 7.4) * mm});
            skArc(sketch, "E506.MirrorCS", {"start": v(-93.53, 3.5) * mm, "mid": v(-93.64, 2.8) * mm, "end": v(-93.88, 2.15) * mm});
            skArc(sketch, "E507.MirrorCS", {"start": v(-96.84, -2.17) * mm, "mid": v(-94.65, -4.01) * mm, "end": v(-97.34, -3.04) * mm});
            skArc(sketch, "E508.MirrorCS", {"start": v(-101.13, 4.1) * mm, "mid": v(-101.02, 4.78) * mm, "end": v(-100.78, 5.43) * mm});
            skArc(sketch, "E509.MirrorCS", {"start": v(-100.23, 1.32) * mm, "mid": v(-100.64, 1.89) * mm, "end": v(-100.93, 2.52) * mm});
            skCircle(sketch, "E510.MirrorC", {"center": v(-97.33, 3.8) * mm, "radius": 1.53 * mm});
            skLineSegment(sketch, "E511.MirrorCS", {"start": v(-104.97, 2.52) * mm, "end": v(-96.84, -2.17) * mm});
            skSolve(sketch);
        }
        {
            var Q0;
            Q0 = qSketchRegion(id + "F31", true);
            var Q1;
            Q1=makeQuery(id+"F17.opPattern","COPY",FACE,{"derivedFrom":makeQuery(id+"F9.opExtrude","CAP_FACE",FACE,{"disambiguationData":[OSD([sQuery(id+"F8.wireOp",EDGE,"E20.0"),sQuery(id+"F8.wireOp",EDGE,"E20.1"),sQuery(id+"F8.wireOp",EDGE,"E21.0"),sQuery(id+"F8.wireOp",EDGE,"E21.1"),sQuery(id+"F8.wireOp",EDGE,"E22"),sQuery(id+"F8.wireOp",EDGE,"E23"),sQuery(id+"F8.wireOp",EDGE,"E24"),sQuery(id+"F8.wireOp",EDGE,"E25"),sQuery(id+"F8.wireOp",EDGE,"E26.0"),sQuery(id+"F8.wireOp",EDGE,"E28"),sQuery(id+"F8.wireOp",EDGE,"E29"),sQuery(id+"F8.wireOp",EDGE,"E32"),sQuery(id+"F8.wireOp",EDGE,"E33.0"),sQuery(id+"F8.wireOp",EDGE,"E36"),sQuery(id+"F8.wireOp",EDGE,"E37"),sQuery(id+"F8.wireOp",EDGE,"E38.trimOffspring"),sQuery(id+"F8.wireOp",EDGE,"E39.trimOffspring"),sQuery(id+"F8.wireOp",EDGE,"E40.trimOffspring"),sQuery(id+"F8.wireOp",EDGE,"E41.trimOffspring"),sQuery(id+"F8.wireOp",EDGE,"E42"),sQuery(id+"F8.wireOp",EDGE,"E43"),sQuery(id+"F8.wireOp",EDGE,"E44"),sQuery(id+"F8.wireOp",EDGE,"E45.trimOffspring"),sQuery(id+"F8.wireOp",EDGE,"E46"),sQuery(id+"F8.wireOp",EDGE,"E47"),sQuery(id+"F8.wireOp",EDGE,"E48.trimOffspring"),sQuery(id+"F8.wireOp",EDGE,"E49.trimOffspring"),sQuery(id+"F8.wireOp",EDGE,"E50.MirrorCS"),sQuery(id+"F8.wireOp",EDGE,"E51.MirrorCS"),sQuery(id+"F8.wireOp",EDGE,"E52.MirrorCS"),sQuery(id+"F8.wireOp",EDGE,"E53.MirrorCS"),sQuery(id+"F8.wireOp",EDGE,"E54.MirrorCS"),sQuery(id+"F8.wireOp",EDGE,"E55.MirrorCS"),sQuery(id+"F8.wireOp",EDGE,"E56.MirrorCS"),sQuery(id+"F8.wireOp",EDGE,"E57.MirrorCS"),sQuery(id+"F8.wireOp",EDGE,"E58.MirrorCS"),sQuery(id+"F8.wireOp",EDGE,"E59.MirrorCS"),sQuery(id+"F8.wireOp",EDGE,"E61.trimOffspring"),sQuery(id+"F8.wireOp",EDGE,"E62.trimOffspring"),sQuery(id+"F8.wireOp",EDGE,"E63")])],"isStart":false}),"instanceName":"1"});
            extrude(context, id + "F32", {"entities" : qUnion([Q0]), "operationType" : NewBodyOperationType.ADD, "endBound" : BoundingType.UP_TO_SURFACE, "depth" : 25.4 * mm, "endBoundEntityFace" : qUnion([Q1]), "offsetDistance" : 25.4 * mm});
        }
        {
            var Q0;
            {var subQ0=sQuery(id+"F4.wireOp",EDGE,"E8");var subQ1=makeQuery(id+"F5.boolean.opBoolean","COPY",FACE,{"derivedFrom":makeQuery(id+"F5.opExtrude","CAP_FACE",FACE,{"disambiguationData":[OSD([subQ0])],"isStart":false})});Q0=makeQuery(id+"F21.boolean.opBoolean","MERGE",FACE,{"derivedFrom":[makeQuery(id+"F19.opPattern","COPY",FACE,{"derivedFrom":makeQuery(id+"F17.opPattern","COPY",FACE,{"derivedFrom":makeQuery(id+"F16.opPattern","COPY",FACE,{"derivedFrom":makeQuery(id+"F9.boolean.opBoolean","SPLIT",FACE,{"disambiguationData":[TD([makeQuery(id+"F5.boolean.opBoolean","COPY",FACE,{"derivedFrom":makeQuery(id+"F5.opExtrude","SWEPT_FACE",FACE,{"disambiguationData":[OSD([subQ0])]})})])],"derivedFrom":subQ1}),"instanceName":"1"}),"instanceName":"1"}),"instanceName":"1"}),makeQuery(id+"F19.opPattern","COPY",FACE,{"derivedFrom":makeQuery(id+"F17.opPattern","COPY",FACE,{"derivedFrom":makeQuery(id+"F16.opPattern","COPY",FACE,{"derivedFrom":makeQuery(id+"F9.boolean.opBoolean","SPLIT",FACE,{"disambiguationData":[TD([makeQuery(id+"F9.opExtrude","SWEPT_FACE",FACE,{"disambiguationData":[OSD([sQuery(id+"F8.wireOp",EDGE,"E25")])]})])],"derivedFrom":subQ1}),"instanceName":"1"}),"instanceName":"1"}),"instanceName":"1"}),makeQuery(id+"F19.opPattern","COPY",FACE,{"derivedFrom":makeQuery(id+"F17.opPattern","COPY",FACE,{"derivedFrom":makeQuery(id+"F16.opPattern","COPY",FACE,{"derivedFrom":makeQuery(id+"F9.boolean.opBoolean","SPLIT",FACE,{"disambiguationData":[TD([makeQuery(id+"F9.opExtrude","SWEPT_FACE",FACE,{"disambiguationData":[OSD([sQuery(id+"F8.wireOp",EDGE,"E32")])]})])],"derivedFrom":subQ1}),"instanceName":"1"}),"instanceName":"1"}),"instanceName":"1"}),makeQuery(id+"F19.opPattern","COPY",FACE,{"derivedFrom":makeQuery(id+"F17.opPattern","COPY",FACE,{"derivedFrom":makeQuery(id+"F16.opPattern","COPY",FACE,{"derivedFrom":makeQuery(id+"F9.boolean.opBoolean","SPLIT",FACE,{"disambiguationData":[TD([makeQuery(id+"F9.opExtrude","SWEPT_FACE",FACE,{"disambiguationData":[OSD([sQuery(id+"F8.wireOp",EDGE,"E33.0")])]})])],"derivedFrom":subQ1}),"instanceName":"1"}),"instanceName":"1"}),"instanceName":"1"}),makeQuery(id+"F19.opPattern","COPY",FACE,{"derivedFrom":makeQuery(id+"F17.opPattern","COPY",FACE,{"derivedFrom":makeQuery(id+"F16.opPattern","COPY",FACE,{"derivedFrom":makeQuery(id+"F9.boolean.opBoolean","SPLIT",FACE,{"disambiguationData":[TD([makeQuery(id+"F9.opExtrude","SWEPT_FACE",FACE,{"disambiguationData":[OSD([sQuery(id+"F8.wireOp",EDGE,"E37")])]})])],"derivedFrom":subQ1}),"instanceName":"1"}),"instanceName":"1"}),"instanceName":"1"}),makeQuery(id+"F19.opPattern","COPY",FACE,{"derivedFrom":makeQuery(id+"F17.opPattern","COPY",FACE,{"derivedFrom":makeQuery(id+"F16.opPattern","COPY",FACE,{"derivedFrom":makeQuery(id+"F9.boolean.opBoolean","SPLIT",FACE,{"disambiguationData":[TD([makeQuery(id+"F9.opExtrude","SWEPT_FACE",FACE,{"disambiguationData":[OSD([sQuery(id+"F8.wireOp",EDGE,"E51.MirrorCS")])]})])],"derivedFrom":subQ1}),"instanceName":"1"}),"instanceName":"1"}),"instanceName":"1"}),makeQuery(id+"F19.opPattern","COPY",FACE,{"derivedFrom":makeQuery(id+"F17.opPattern","COPY",FACE,{"derivedFrom":makeQuery(id+"F16.opPattern","COPY",FACE,{"derivedFrom":makeQuery(id+"F9.boolean.opBoolean","SPLIT",FACE,{"disambiguationData":[TD([makeQuery(id+"F9.opExtrude","SWEPT_FACE",FACE,{"disambiguationData":[OSD([sQuery(id+"F8.wireOp",EDGE,"E53.MirrorCS")])]})])],"derivedFrom":subQ1}),"instanceName":"1"}),"instanceName":"1"}),"instanceName":"1"}),makeQuery(id+"F19.opPattern","COPY",FACE,{"derivedFrom":makeQuery(id+"F17.opPattern","COPY",FACE,{"derivedFrom":makeQuery(id+"F16.opPattern","COPY",FACE,{"derivedFrom":makeQuery(id+"F9.boolean.opBoolean","SPLIT",FACE,{"disambiguationData":[TD([makeQuery(id+"F9.opExtrude","SWEPT_FACE",FACE,{"disambiguationData":[OSD([sQuery(id+"F8.wireOp",EDGE,"E80")])]})])],"derivedFrom":subQ1}),"instanceName":"1"}),"instanceName":"1"}),"instanceName":"1"}),makeQuery(id+"F19.opPattern","COPY",FACE,{"derivedFrom":makeQuery(id+"F17.opPattern","COPY",FACE,{"derivedFrom":makeQuery(id+"F16.opPattern","COPY",FACE,{"derivedFrom":makeQuery(id+"F9.boolean.opBoolean","SPLIT",FACE,{"disambiguationData":[TD([makeQuery(id+"F9.opExtrude","SWEPT_FACE",FACE,{"disambiguationData":[OSD([sQuery(id+"F8.wireOp",EDGE,"E83")])]})])],"derivedFrom":subQ1}),"instanceName":"1"}),"instanceName":"1"}),"instanceName":"1"}),makeQuery(id+"F21.opExtrude","CAP_FACE",FACE,{"disambiguationData":[OSD([sQuery(id+"F20.wireOp",EDGE,"E310.0.0")])],"isStart":false})]});}
            var sketch = newSketch(context, id + "F33", { "sketchPlane" : qUnion([Q0])});
            skPoint(sketch, "E512.0", {"position": v(-101.6, 38.1) * mm});
            skCircle(sketch, "E513", {"center": v(-101.6, 50.8) * mm, "radius": 1.35 * mm});
            skArc(sketch, "E514", {"start": v(-102.73, 48.95) * mm, "mid": v(-101.6, 48.64) * mm, "end": v(-100.47, 48.95) * mm});
            skLineSegment(sketch, "E515", {"start": v(-100.7, 52.78) * mm, "end": v(-97.05, 50.55) * mm});
            skLineSegment(sketch, "E516.bottom", {"start": v(-101.6, 50.8) * mm, "end": v(-101.04, 50.8) * mm});
            skLineSegment(sketch, "E516.left", {"start": v(-101.6, 50.8) * mm, "end": v(-101.6, 51.35) * mm});
            skLineSegment(sketch, "E516.right", {"start": v(-101.04, 50.8) * mm, "end": v(-101.04, 51.35) * mm});
            skLineSegment(sketch, "E517.MirrorCS", {"start": v(-100.7, 48.82) * mm, "end": v(-97.05, 51.05) * mm});
            skLineSegment(sketch, "E518.MirrorCS", {"start": v(-102.5, 52.78) * mm, "end": v(-106.15, 50.55) * mm});
            skLineSegment(sketch, "E519.MirrorCS", {"start": v(-102.5, 48.82) * mm, "end": v(-106.15, 51.05) * mm});
            skArc(sketch, "E520.trimOffspring", {"start": v(-100.47, 52.65) * mm, "mid": v(-101.6, 52.96) * mm, "end": v(-102.73, 52.65) * mm});
            skCircle(sketch, "E521", {"center": v(-101.6, 50.8) * mm, "radius": 1.9 * mm});
            skLineSegment(sketch, "E522", {"start": v(-101.6, 42.54) * mm, "end": v(-101.6, 59.06) * mm});
            skArc(sketch, "E523", {"start": v(-99.52, 43.94) * mm, "mid": v(-99.32, 44.12) * mm, "end": v(-99.13, 44.3) * mm});
            skArc(sketch, "E524", {"start": v(-99.6, 43.37) * mm, "mid": v(-98.77, 43.92) * mm, "end": v(-98, 44.56) * mm});
            skArc(sketch, "E525", {"start": v(-103.5, 58.1) * mm, "mid": v(-104.32, 57.48) * mm, "end": v(-105.05, 56.78) * mm});
            skArc(sketch, "E526", {"start": v(-99.52, 57.66) * mm, "mid": v(-101.65, 58.42) * mm, "end": v(-103.8, 57.72) * mm});
            skArc(sketch, "E527", {"start": v(-99.6, 58.23) * mm, "mid": v(-101.58, 58.7) * mm, "end": v(-103.5, 58.1) * mm});
            skArc(sketch, "E528.trimOffspring", {"start": v(-103.8, 57.72) * mm, "mid": v(-104.26, 57.3) * mm, "end": v(-104.7, 56.85) * mm});
            skArc(sketch, "E529.MirrorCS", {"start": v(-99.52, 43.94) * mm, "mid": v(-101.65, 43.18) * mm, "end": v(-103.8, 43.88) * mm});
            skArc(sketch, "E530.MirrorCS", {"start": v(-99.6, 43.37) * mm, "mid": v(-101.58, 42.9) * mm, "end": v(-103.5, 43.5) * mm});
            skPoint(sketch, "E531.orphan", {"position": v(-99.27, 58.03) * mm});
            skPoint(sketch, "E532.orphan", {"position": v(-99.27, 43.57) * mm});
            skLineSegment(sketch, "E533", {"start": v(-101.6, 50.8) * mm, "end": v(-99.83, 53.87) * mm});
            skArc(sketch, "E534.MirrorCS", {"start": v(-108.58, 49.17) * mm, "mid": v(-108.53, 49.43) * mm, "end": v(-108.46, 49.69) * mm});
            skArc(sketch, "E535.MirrorCS", {"start": v(-109.03, 48.81) * mm, "mid": v(-108.98, 49.81) * mm, "end": v(-108.8, 50.8) * mm});
            skArc(sketch, "E536.MirrorCS", {"start": v(-96.7, 56.04) * mm, "mid": v(-94.98, 54.57) * mm, "end": v(-94.5, 52.36) * mm});
            skArc(sketch, "E537.MirrorCS", {"start": v(-96.16, 56.24) * mm, "mid": v(-94.78, 54.77) * mm, "end": v(-94.33, 52.8) * mm});
            skArc(sketch, "E538.MirrorCS", {"start": v(-94.5, 52.36) * mm, "mid": v(-94.64, 51.75) * mm, "end": v(-94.8, 51.14) * mm});
            skArc(sketch, "E539.MirrorCS", {"start": v(-94.33, 52.8) * mm, "mid": v(-94.45, 51.79) * mm, "end": v(-94.7, 50.8) * mm});
            skArc(sketch, "E540.MirrorCS", {"start": v(-108.58, 49.17) * mm, "mid": v(-108.17, 46.95) * mm, "end": v(-106.5, 45.44) * mm});
            skArc(sketch, "E541.MirrorCS", {"start": v(-109.03, 48.81) * mm, "mid": v(-108.45, 46.87) * mm, "end": v(-106.97, 45.5) * mm});
            skArc(sketch, "E542.MirrorCS", {"start": v(-108.58, 52.43) * mm, "mid": v(-108.53, 52.17) * mm, "end": v(-108.46, 51.91) * mm});
            skArc(sketch, "E543.MirrorCS", {"start": v(-109.03, 52.79) * mm, "mid": v(-108.98, 51.79) * mm, "end": v(-108.8, 50.8) * mm});
            skArc(sketch, "E544.MirrorCS", {"start": v(-96.16, 45.36) * mm, "mid": v(-94.78, 46.83) * mm, "end": v(-94.33, 48.8) * mm});
            skArc(sketch, "E545.MirrorCS", {"start": v(-96.7, 45.56) * mm, "mid": v(-94.98, 47.03) * mm, "end": v(-94.5, 49.24) * mm});
            skArc(sketch, "E546.MirrorCS", {"start": v(-94.33, 48.8) * mm, "mid": v(-94.45, 49.81) * mm, "end": v(-94.7, 50.8) * mm});
            skArc(sketch, "E547.MirrorCS", {"start": v(-94.5, 49.24) * mm, "mid": v(-94.64, 49.85) * mm, "end": v(-94.8, 50.46) * mm});
            skArc(sketch, "E548.MirrorCS", {"start": v(-109.03, 52.79) * mm, "mid": v(-108.45, 54.73) * mm, "end": v(-106.97, 56.1) * mm});
            skArc(sketch, "E549.MirrorCS", {"start": v(-108.58, 52.43) * mm, "mid": v(-108.17, 54.65) * mm, "end": v(-106.5, 56.16) * mm});
            skPoint(sketch, "E550.centerSnap0", {"position": v(-98.88, 46.08) * mm});
            skArc(sketch, "E551.trimOffspring", {"start": v(-103.85, 56.7) * mm, "mid": v(-104.4, 56.66) * mm, "end": v(-104.94, 56.58) * mm});
            skArc(sketch, "E552.trimOffspring", {"start": v(-103.05, 57) * mm, "mid": v(-103.88, 56.97) * mm, "end": v(-104.7, 56.85) * mm});
            skArc(sketch, "E553.trimOffspring", {"start": v(-100.1, 56.48) * mm, "mid": v(-99.23, 56.49) * mm, "end": v(-98.36, 56.42) * mm});
            skArc(sketch, "E554.trimOffspring", {"start": v(-103.05, 57) * mm, "mid": v(-101.11, 57.38) * mm, "end": v(-99.13, 57.3) * mm});
            skArc(sketch, "E555.trimOffspring", {"start": v(-105.3, 56.51) * mm, "mid": v(-105.9, 56.36) * mm, "end": v(-106.5, 56.16) * mm});
            skArc(sketch, "E556.trimOffspring", {"start": v(-105.05, 56.78) * mm, "mid": v(-106.03, 56.5) * mm, "end": v(-106.97, 56.1) * mm});
            skArc(sketch, "E557.trimOffspring", {"start": v(-104.94, 56.58) * mm, "mid": v(-105.28, 56.15) * mm, "end": v(-105.6, 55.7) * mm});
            skArc(sketch, "E558.trimOffspring", {"start": v(-105.3, 56.51) * mm, "mid": v(-105.8, 55.86) * mm, "end": v(-106.25, 55.16) * mm});
            skArc(sketch, "E559.trimOffspring", {"start": v(-105.6, 55.7) * mm, "mid": v(-104.75, 56.26) * mm, "end": v(-103.85, 56.7) * mm});
            skArc(sketch, "E560.trimOffspring", {"start": v(-106.76, 53.04) * mm, "mid": v(-107.05, 50.8) * mm, "end": v(-106.76, 48.56) * mm});
            skArc(sketch, "E561.trimOffspring", {"start": v(-107.27, 52.35) * mm, "mid": v(-107.4, 50.8) * mm, "end": v(-107.27, 49.25) * mm});
            skArc(sketch, "E562.trimOffspring", {"start": v(-106.76, 53.04) * mm, "mid": v(-104.18, 55.26) * mm, "end": v(-100.96, 56.4) * mm});
            skArc(sketch, "E563.trimOffspring", {"start": v(-108.46, 51.91) * mm, "mid": v(-107.54, 53.67) * mm, "end": v(-106.25, 55.16) * mm});
            skArc(sketch, "E564.trimOffspring", {"start": v(-108.08, 50.8) * mm, "mid": v(-107.71, 50) * mm, "end": v(-107.27, 49.25) * mm});
            skArc(sketch, "E565.trimOffspring", {"start": v(-108.08, 50.8) * mm, "mid": v(-107.71, 51.6) * mm, "end": v(-107.27, 52.35) * mm});
            skArc(sketch, "E566.trimOffspring", {"start": v(-108.46, 49.69) * mm, "mid": v(-107.54, 47.93) * mm, "end": v(-106.25, 46.44) * mm});
            skArc(sketch, "E567.trimOffspring", {"start": v(-106.25, 46.44) * mm, "mid": v(-105.8, 45.74) * mm, "end": v(-105.3, 45.09) * mm});
            skArc(sketch, "E568.trimOffspring", {"start": v(-105.6, 45.9) * mm, "mid": v(-105.28, 45.45) * mm, "end": v(-104.94, 45.02) * mm});
            skArc(sketch, "E569.trimOffspring", {"start": v(-106.76, 48.56) * mm, "mid": v(-104.18, 46.34) * mm, "end": v(-100.96, 45.2) * mm});
            skArc(sketch, "E570.trimOffspring", {"start": v(-105.6, 45.9) * mm, "mid": v(-104.75, 45.34) * mm, "end": v(-103.85, 44.9) * mm});
            skArc(sketch, "E571.trimOffspring", {"start": v(-105.05, 44.82) * mm, "mid": v(-106.03, 45.1) * mm, "end": v(-106.97, 45.5) * mm});
            skArc(sketch, "E572.trimOffspring", {"start": v(-104.7, 44.75) * mm, "mid": v(-104.26, 44.3) * mm, "end": v(-103.8, 43.88) * mm});
            skArc(sketch, "E573.trimOffspring", {"start": v(-105.3, 45.09) * mm, "mid": v(-105.9, 45.24) * mm, "end": v(-106.5, 45.44) * mm});
            skArc(sketch, "E574.trimOffspring", {"start": v(-105.05, 44.82) * mm, "mid": v(-104.32, 44.12) * mm, "end": v(-103.5, 43.5) * mm});
            skArc(sketch, "E575.trimOffspring", {"start": v(-103.05, 44.6) * mm, "mid": v(-103.88, 44.63) * mm, "end": v(-104.7, 44.75) * mm});
            skArc(sketch, "E576.trimOffspring", {"start": v(-103.85, 44.9) * mm, "mid": v(-104.4, 44.94) * mm, "end": v(-104.94, 45.02) * mm});
            skArc(sketch, "E577.trimOffspring", {"start": v(-103.05, 44.6) * mm, "mid": v(-101.11, 44.22) * mm, "end": v(-99.13, 44.3) * mm});
            skArc(sketch, "E578.trimOffspring", {"start": v(-100.1, 45.12) * mm, "mid": v(-99.23, 45.11) * mm, "end": v(-98.36, 45.18) * mm});
            skArc(sketch, "E579.trimOffspring", {"start": v(-98.36, 45.18) * mm, "mid": v(-97.86, 45.9) * mm, "end": v(-97.43, 46.66) * mm});
            skArc(sketch, "E580.trimOffspring", {"start": v(-97.2, 45.41) * mm, "mid": v(-96.15, 47.09) * mm, "end": v(-95.5, 48.96) * mm});
            skArc(sketch, "E581.trimOffspring", {"start": v(-97.2, 45.41) * mm, "mid": v(-96.95, 45.49) * mm, "end": v(-96.7, 45.56) * mm});
            skArc(sketch, "E582.trimOffspring", {"start": v(-98, 44.56) * mm, "mid": v(-97.05, 44.9) * mm, "end": v(-96.16, 45.36) * mm});
            skArc(sketch, "E583.trimOffspring", {"start": v(-97.08, 47.45) * mm, "mid": v(-98.88, 46.08) * mm, "end": v(-100.96, 45.2) * mm});
            skArc(sketch, "E584.trimOffspring", {"start": v(-97.43, 46.66) * mm, "mid": v(-98.7, 45.77) * mm, "end": v(-100.1, 45.12) * mm});
            skArc(sketch, "E585.trimOffspring", {"start": v(-95.36, 49.8) * mm, "mid": v(-95.3, 50.8) * mm, "end": v(-95.36, 51.8) * mm});
            skArc(sketch, "E586.trimOffspring", {"start": v(-97.08, 47.45) * mm, "mid": v(-96.45, 50.8) * mm, "end": v(-97.08, 54.15) * mm});
            skArc(sketch, "E587.trimOffspring", {"start": v(-94.92, 50.8) * mm, "mid": v(-95.13, 50.29) * mm, "end": v(-95.36, 49.8) * mm});
            skArc(sketch, "E588.trimOffspring", {"start": v(-94.8, 51.14) * mm, "mid": v(-95.12, 51.9) * mm, "end": v(-95.5, 52.64) * mm});
            skArc(sketch, "E589.trimOffspring", {"start": v(-94.8, 50.46) * mm, "mid": v(-95.12, 49.7) * mm, "end": v(-95.5, 48.96) * mm});
            skArc(sketch, "E590.trimOffspring", {"start": v(-94.92, 50.8) * mm, "mid": v(-95.13, 51.31) * mm, "end": v(-95.36, 51.8) * mm});
            skArc(sketch, "E591.trimOffspring", {"start": v(-97.08, 54.15) * mm, "mid": v(-98.88, 55.52) * mm, "end": v(-100.96, 56.4) * mm});
            skArc(sketch, "E592.trimOffspring", {"start": v(-97.43, 54.94) * mm, "mid": v(-98.7, 55.83) * mm, "end": v(-100.1, 56.48) * mm});
            skArc(sketch, "E593.trimOffspring", {"start": v(-95.5, 52.64) * mm, "mid": v(-96.15, 54.51) * mm, "end": v(-97.2, 56.19) * mm});
            skArc(sketch, "E594.trimOffspring", {"start": v(-97.43, 54.94) * mm, "mid": v(-97.86, 55.7) * mm, "end": v(-98.36, 56.42) * mm});
            skArc(sketch, "E595.trimOffspring", {"start": v(-98, 57.04) * mm, "mid": v(-97.05, 56.7) * mm, "end": v(-96.16, 56.24) * mm});
            skArc(sketch, "E596.trimOffspring", {"start": v(-97.2, 56.19) * mm, "mid": v(-96.95, 56.11) * mm, "end": v(-96.7, 56.04) * mm});
            skArc(sketch, "E597.trimOffspring", {"start": v(-98, 57.04) * mm, "mid": v(-98.77, 57.68) * mm, "end": v(-99.6, 58.23) * mm});
            skArc(sketch, "E598.trimOffspring", {"start": v(-99.13, 57.3) * mm, "mid": v(-99.32, 57.48) * mm, "end": v(-99.52, 57.66) * mm});
            skSolve(sketch);
        }
        {
            var Q0;
            Q0 = qSketchRegion(id + "F33", true);
            extrude(context, id + "F34", {"entities" : qUnion([Q0]), "operationType" : NewBodyOperationType.ADD, "depth" : 1 * mm, "offsetDistance" : 25.4 * mm});
        }
        {
            var Q0;
            {var subQ4=sQuery(id+"F33.wireOp",EDGE,"E524");Q0=makeQuery(id+"F33.imprint","IMPRINT",FACE,{"disambiguationData":[TD([[makeQuery(id+"F33.imprint","IMPRINT",EDGE,{"derivedFrom":subQ4}),-1.0]])]});}
            var sketch = newSketch(context, id + "F35", { "sketchPlane" : qUnion([Q0])});
            skArc(sketch, "E599.0", {"start": v(-102.73, 48.95) * mm, "mid": v(-101.6, 48.64) * mm, "end": v(-100.47, 48.95) * mm});
            skLineSegment(sketch, "E599.1", {"start": v(-101.6, 50.8) * mm, "end": v(-101.04, 50.8) * mm});
            skArc(sketch, "E599.2", {"start": v(-100.47, 52.65) * mm, "mid": v(-101.6, 52.96) * mm, "end": v(-102.73, 52.65) * mm});
            skCircle(sketch, "E599.3", {"center": v(-101.6, 50.8) * mm, "radius": 1.35 * mm});
            skLineSegment(sketch, "E599.4", {"start": v(-100.7, 52.78) * mm, "end": v(-97.05, 50.55) * mm});
            skLineSegment(sketch, "E599.5", {"start": v(-101.6, 50.8) * mm, "end": v(-101.6, 51.35) * mm});
            skLineSegment(sketch, "E599.6", {"start": v(-101.04, 50.8) * mm, "end": v(-101.04, 51.35) * mm});
            skLineSegment(sketch, "E599.7", {"start": v(-100.7, 48.82) * mm, "end": v(-97.05, 51.05) * mm});
            skLineSegment(sketch, "E599.8", {"start": v(-102.5, 52.78) * mm, "end": v(-106.15, 50.55) * mm});
            skLineSegment(sketch, "E599.9", {"start": v(-102.5, 48.82) * mm, "end": v(-106.15, 51.05) * mm});
            skCircle(sketch, "E599.10", {"center": v(-101.6, 50.8) * mm, "radius": 1.9 * mm});
            skCircle(sketch, "E600", {"center": v(-102.04, 58.53) * mm, "radius": 0.95 * mm});
            skCircle(sketch, "E601", {"center": v(-106.42, 54.19) * mm, "radius": 1.55 * mm});
            skCircle(sketch, "E602", {"center": v(-94.83, 47.06) * mm, "radius": 0.64 * mm});
            skSolve(sketch);
        }
        {
            var Q0;
            Q0 = qSketchRegion(id + "F35", true);
            var Q1;
            Q1=makeQuery(id+"F32.opExtrude","CAP_FACE",FACE,{"disambiguationData":[OSD([sQuery(id+"F31.wireOp",EDGE,"E476.MirrorCS"),sQuery(id+"F31.wireOp",EDGE,"E477.MirrorCS"),sQuery(id+"F31.wireOp",EDGE,"E478.MirrorCS"),sQuery(id+"F31.wireOp",EDGE,"E479.MirrorCS"),sQuery(id+"F31.wireOp",EDGE,"E480.MirrorCS"),sQuery(id+"F31.wireOp",EDGE,"E481.MirrorCS"),sQuery(id+"F31.wireOp",EDGE,"E482.MirrorCS"),sQuery(id+"F31.wireOp",EDGE,"E483.MirrorCS"),sQuery(id+"F31.wireOp",EDGE,"E484.MirrorCS"),sQuery(id+"F31.wireOp",EDGE,"E485.MirrorCS"),sQuery(id+"F31.wireOp",EDGE,"E486.MirrorCS"),sQuery(id+"F31.wireOp",EDGE,"E487.MirrorCS"),sQuery(id+"F31.wireOp",EDGE,"E488.MirrorCS"),sQuery(id+"F31.wireOp",EDGE,"E489.MirrorCS"),sQuery(id+"F31.wireOp",EDGE,"E490.MirrorCS"),sQuery(id+"F31.wireOp",EDGE,"E491.MirrorCS"),sQuery(id+"F31.wireOp",EDGE,"E492.MirrorCS"),sQuery(id+"F31.wireOp",EDGE,"E493.MirrorCS"),sQuery(id+"F31.wireOp",EDGE,"E494.MirrorCS"),sQuery(id+"F31.wireOp",EDGE,"E495.MirrorCS"),sQuery(id+"F31.wireOp",EDGE,"E496.MirrorCS"),sQuery(id+"F31.wireOp",EDGE,"E497.MirrorCS"),sQuery(id+"F31.wireOp",EDGE,"E498.MirrorCS"),sQuery(id+"F31.wireOp",EDGE,"E499.MirrorCS"),sQuery(id+"F31.wireOp",EDGE,"E500.MirrorCS"),sQuery(id+"F31.wireOp",EDGE,"E501.MirrorCS"),sQuery(id+"F31.wireOp",EDGE,"E502.MirrorCS"),sQuery(id+"F31.wireOp",EDGE,"E503.MirrorCS"),sQuery(id+"F31.wireOp",EDGE,"E505.MirrorCS"),sQuery(id+"F31.wireOp",EDGE,"E506.MirrorCS"),sQuery(id+"F31.wireOp",EDGE,"E508.MirrorCS"),sQuery(id+"F31.wireOp",EDGE,"E509.MirrorCS"),sQuery(id+"F31.wireOp",EDGE,"E510.MirrorC")])],"isStart":false});
            extrude(context, id + "F36", {"entities" : qUnion([Q0]), "operationType" : NewBodyOperationType.ADD, "endBound" : BoundingType.UP_TO_SURFACE, "depth" : 25.4 * mm, "endBoundEntityFace" : qUnion([Q1]), "offsetDistance" : 25.4 * mm});
        }
        {
            var Q0;
            {var subQ0=sQuery(id+"F4.wireOp",EDGE,"E8");var subQ1=makeQuery(id+"F5.boolean.opBoolean","COPY",FACE,{"derivedFrom":makeQuery(id+"F5.opExtrude","CAP_FACE",FACE,{"disambiguationData":[OSD([subQ0])],"isStart":false})});Q0=makeQuery(id+"F36.boolean.opBoolean","SPLIT",FACE,{"disambiguationData":[TD([makeQuery(id+"F36.opExtrude","SWEPT_FACE",FACE,{"disambiguationData":[OSD([sQuery(id+"F35.wireOp",EDGE,"E599.10")])]})])],"derivedFrom":makeQuery(id+"F34.boolean.opBoolean","SPLIT",FACE,{"disambiguationData":[TD([makeQuery(id+"F34.opExtrude","SWEPT_FACE",FACE,{"disambiguationData":[OSD([sQuery(id+"F33.wireOp",EDGE,"E560.trimOffspring")])]})])],"derivedFrom":makeQuery(id+"F21.boolean.opBoolean","MERGE",FACE,{"derivedFrom":[makeQuery(id+"F19.opPattern","COPY",FACE,{"derivedFrom":makeQuery(id+"F17.opPattern","COPY",FACE,{"derivedFrom":makeQuery(id+"F16.opPattern","COPY",FACE,{"derivedFrom":makeQuery(id+"F9.boolean.opBoolean","SPLIT",FACE,{"disambiguationData":[TD([makeQuery(id+"F5.boolean.opBoolean","COPY",FACE,{"derivedFrom":makeQuery(id+"F5.opExtrude","SWEPT_FACE",FACE,{"disambiguationData":[OSD([subQ0])]})})])],"derivedFrom":subQ1}),"instanceName":"1"}),"instanceName":"1"}),"instanceName":"1"}),makeQuery(id+"F19.opPattern","COPY",FACE,{"derivedFrom":makeQuery(id+"F17.opPattern","COPY",FACE,{"derivedFrom":makeQuery(id+"F16.opPattern","COPY",FACE,{"derivedFrom":makeQuery(id+"F9.boolean.opBoolean","SPLIT",FACE,{"disambiguationData":[TD([makeQuery(id+"F9.opExtrude","SWEPT_FACE",FACE,{"disambiguationData":[OSD([sQuery(id+"F8.wireOp",EDGE,"E25")])]})])],"derivedFrom":subQ1}),"instanceName":"1"}),"instanceName":"1"}),"instanceName":"1"}),makeQuery(id+"F19.opPattern","COPY",FACE,{"derivedFrom":makeQuery(id+"F17.opPattern","COPY",FACE,{"derivedFrom":makeQuery(id+"F16.opPattern","COPY",FACE,{"derivedFrom":makeQuery(id+"F9.boolean.opBoolean","SPLIT",FACE,{"disambiguationData":[TD([makeQuery(id+"F9.opExtrude","SWEPT_FACE",FACE,{"disambiguationData":[OSD([sQuery(id+"F8.wireOp",EDGE,"E32")])]})])],"derivedFrom":subQ1}),"instanceName":"1"}),"instanceName":"1"}),"instanceName":"1"}),makeQuery(id+"F19.opPattern","COPY",FACE,{"derivedFrom":makeQuery(id+"F17.opPattern","COPY",FACE,{"derivedFrom":makeQuery(id+"F16.opPattern","COPY",FACE,{"derivedFrom":makeQuery(id+"F9.boolean.opBoolean","SPLIT",FACE,{"disambiguationData":[TD([makeQuery(id+"F9.opExtrude","SWEPT_FACE",FACE,{"disambiguationData":[OSD([sQuery(id+"F8.wireOp",EDGE,"E33.0")])]})])],"derivedFrom":subQ1}),"instanceName":"1"}),"instanceName":"1"}),"instanceName":"1"}),makeQuery(id+"F19.opPattern","COPY",FACE,{"derivedFrom":makeQuery(id+"F17.opPattern","COPY",FACE,{"derivedFrom":makeQuery(id+"F16.opPattern","COPY",FACE,{"derivedFrom":makeQuery(id+"F9.boolean.opBoolean","SPLIT",FACE,{"disambiguationData":[TD([makeQuery(id+"F9.opExtrude","SWEPT_FACE",FACE,{"disambiguationData":[OSD([sQuery(id+"F8.wireOp",EDGE,"E37")])]})])],"derivedFrom":subQ1}),"instanceName":"1"}),"instanceName":"1"}),"instanceName":"1"}),makeQuery(id+"F19.opPattern","COPY",FACE,{"derivedFrom":makeQuery(id+"F17.opPattern","COPY",FACE,{"derivedFrom":makeQuery(id+"F16.opPattern","COPY",FACE,{"derivedFrom":makeQuery(id+"F9.boolean.opBoolean","SPLIT",FACE,{"disambiguationData":[TD([makeQuery(id+"F9.opExtrude","SWEPT_FACE",FACE,{"disambiguationData":[OSD([sQuery(id+"F8.wireOp",EDGE,"E51.MirrorCS")])]})])],"derivedFrom":subQ1}),"instanceName":"1"}),"instanceName":"1"}),"instanceName":"1"}),makeQuery(id+"F19.opPattern","COPY",FACE,{"derivedFrom":makeQuery(id+"F17.opPattern","COPY",FACE,{"derivedFrom":makeQuery(id+"F16.opPattern","COPY",FACE,{"derivedFrom":makeQuery(id+"F9.boolean.opBoolean","SPLIT",FACE,{"disambiguationData":[TD([makeQuery(id+"F9.opExtrude","SWEPT_FACE",FACE,{"disambiguationData":[OSD([sQuery(id+"F8.wireOp",EDGE,"E53.MirrorCS")])]})])],"derivedFrom":subQ1}),"instanceName":"1"}),"instanceName":"1"}),"instanceName":"1"}),makeQuery(id+"F19.opPattern","COPY",FACE,{"derivedFrom":makeQuery(id+"F17.opPattern","COPY",FACE,{"derivedFrom":makeQuery(id+"F16.opPattern","COPY",FACE,{"derivedFrom":makeQuery(id+"F9.boolean.opBoolean","SPLIT",FACE,{"disambiguationData":[TD([makeQuery(id+"F9.opExtrude","SWEPT_FACE",FACE,{"disambiguationData":[OSD([sQuery(id+"F8.wireOp",EDGE,"E80")])]})])],"derivedFrom":subQ1}),"instanceName":"1"}),"instanceName":"1"}),"instanceName":"1"}),makeQuery(id+"F19.opPattern","COPY",FACE,{"derivedFrom":makeQuery(id+"F17.opPattern","COPY",FACE,{"derivedFrom":makeQuery(id+"F16.opPattern","COPY",FACE,{"derivedFrom":makeQuery(id+"F9.boolean.opBoolean","SPLIT",FACE,{"disambiguationData":[TD([makeQuery(id+"F9.opExtrude","SWEPT_FACE",FACE,{"disambiguationData":[OSD([sQuery(id+"F8.wireOp",EDGE,"E83")])]})])],"derivedFrom":subQ1}),"instanceName":"1"}),"instanceName":"1"}),"instanceName":"1"})],"fromTools":[makeQuery(id+"F21.opExtrude","CAP_FACE",FACE,{"disambiguationData":[OSD([sQuery(id+"F20.wireOp",EDGE,"E310.0.0")])],"isStart":false})]})})});}
            var sketch = newSketch(context, id + "F37", { "sketchPlane" : qUnion([Q0])});
            skCircle(sketch, "E603", {"center": v(-101.6, 50.8) * mm, "radius": 0.8 * mm});
            skSolve(sketch);
        }
        {
            var Q0;
            Q0 = qSketchRegion(id + "F37", true);
            var Q1;
            Q1=makeQuery(id+"F34.opExtrude","CAP_FACE",FACE,{"disambiguationData":[OSD([sQuery(id+"F33.wireOp",EDGE,"E523"),sQuery(id+"F33.wireOp",EDGE,"E524"),sQuery(id+"F33.wireOp",EDGE,"E525"),sQuery(id+"F33.wireOp",EDGE,"E526"),sQuery(id+"F33.wireOp",EDGE,"E527"),sQuery(id+"F33.wireOp",EDGE,"E528.trimOffspring"),sQuery(id+"F33.wireOp",EDGE,"E529.MirrorCS"),sQuery(id+"F33.wireOp",EDGE,"E530.MirrorCS"),sQuery(id+"F33.wireOp",EDGE,"E534.MirrorCS"),sQuery(id+"F33.wireOp",EDGE,"E535.MirrorCS"),sQuery(id+"F33.wireOp",EDGE,"E536.MirrorCS"),sQuery(id+"F33.wireOp",EDGE,"E537.MirrorCS"),sQuery(id+"F33.wireOp",EDGE,"E538.MirrorCS"),sQuery(id+"F33.wireOp",EDGE,"E539.MirrorCS"),sQuery(id+"F33.wireOp",EDGE,"E540.MirrorCS"),sQuery(id+"F33.wireOp",EDGE,"E541.MirrorCS"),sQuery(id+"F33.wireOp",EDGE,"E542.MirrorCS"),sQuery(id+"F33.wireOp",EDGE,"E543.MirrorCS"),sQuery(id+"F33.wireOp",EDGE,"E544.MirrorCS"),sQuery(id+"F33.wireOp",EDGE,"E545.MirrorCS"),sQuery(id+"F33.wireOp",EDGE,"E546.MirrorCS"),sQuery(id+"F33.wireOp",EDGE,"E547.MirrorCS"),sQuery(id+"F33.wireOp",EDGE,"E548.MirrorCS"),sQuery(id+"F33.wireOp",EDGE,"E549.MirrorCS"),sQuery(id+"F33.wireOp",EDGE,"E551.trimOffspring"),sQuery(id+"F33.wireOp",EDGE,"E552.trimOffspring"),sQuery(id+"F33.wireOp",EDGE,"E553.trimOffspring"),sQuery(id+"F33.wireOp",EDGE,"E554.trimOffspring"),sQuery(id+"F33.wireOp",EDGE,"E555.trimOffspring"),sQuery(id+"F33.wireOp",EDGE,"E556.trimOffspring"),sQuery(id+"F33.wireOp",EDGE,"E557.trimOffspring"),sQuery(id+"F33.wireOp",EDGE,"E558.trimOffspring"),sQuery(id+"F33.wireOp",EDGE,"E559.trimOffspring"),sQuery(id+"F33.wireOp",EDGE,"E560.trimOffspring"),sQuery(id+"F33.wireOp",EDGE,"E561.trimOffspring"),sQuery(id+"F33.wireOp",EDGE,"E562.trimOffspring"),sQuery(id+"F33.wireOp",EDGE,"E563.trimOffspring"),sQuery(id+"F33.wireOp",EDGE,"E564.trimOffspring"),sQuery(id+"F33.wireOp",EDGE,"E565.trimOffspring"),sQuery(id+"F33.wireOp",EDGE,"E566.trimOffspring"),sQuery(id+"F33.wireOp",EDGE,"E567.trimOffspring"),sQuery(id+"F33.wireOp",EDGE,"E568.trimOffspring"),sQuery(id+"F33.wireOp",EDGE,"E569.trimOffspring"),sQuery(id+"F33.wireOp",EDGE,"E570.trimOffspring"),sQuery(id+"F33.wireOp",EDGE,"E571.trimOffspring"),sQuery(id+"F33.wireOp",EDGE,"E572.trimOffspring"),sQuery(id+"F33.wireOp",EDGE,"E573.trimOffspring"),sQuery(id+"F33.wireOp",EDGE,"E574.trimOffspring"),sQuery(id+"F33.wireOp",EDGE,"E575.trimOffspring"),sQuery(id+"F33.wireOp",EDGE,"E576.trimOffspring"),sQuery(id+"F33.wireOp",EDGE,"E577.trimOffspring"),sQuery(id+"F33.wireOp",EDGE,"E578.trimOffspring"),sQuery(id+"F33.wireOp",EDGE,"E579.trimOffspring"),sQuery(id+"F33.wireOp",EDGE,"E580.trimOffspring"),sQuery(id+"F33.wireOp",EDGE,"E581.trimOffspring"),sQuery(id+"F33.wireOp",EDGE,"E582.trimOffspring"),sQuery(id+"F33.wireOp",EDGE,"E583.trimOffspring"),sQuery(id+"F33.wireOp",EDGE,"E584.trimOffspring"),sQuery(id+"F33.wireOp",EDGE,"E585.trimOffspring"),sQuery(id+"F33.wireOp",EDGE,"E586.trimOffspring"),sQuery(id+"F33.wireOp",EDGE,"E587.trimOffspring"),sQuery(id+"F33.wireOp",EDGE,"E588.trimOffspring"),sQuery(id+"F33.wireOp",EDGE,"E589.trimOffspring"),sQuery(id+"F33.wireOp",EDGE,"E590.trimOffspring"),sQuery(id+"F33.wireOp",EDGE,"E591.trimOffspring"),sQuery(id+"F33.wireOp",EDGE,"E592.trimOffspring"),sQuery(id+"F33.wireOp",EDGE,"E593.trimOffspring"),sQuery(id+"F33.wireOp",EDGE,"E594.trimOffspring"),sQuery(id+"F33.wireOp",EDGE,"E595.trimOffspring"),sQuery(id+"F33.wireOp",EDGE,"E596.trimOffspring"),sQuery(id+"F33.wireOp",EDGE,"E597.trimOffspring"),sQuery(id+"F33.wireOp",EDGE,"E598.trimOffspring")])],"isStart":false});
            extrude(context, id + "F38", {"entities" : qUnion([Q0]), "operationType" : NewBodyOperationType.ADD, "endBound" : BoundingType.UP_TO_SURFACE, "depth" : 25.4 * mm, "endBoundEntityFace" : qUnion([Q1]), "offsetDistance" : 25.4 * mm});
        }
        {
            var Q0;
            Q0=makeQuery(id+"F19.opPattern","COPY",BODY,{"derivedFrom":makeQuery(id+"F16.opPattern","COPY",BODY,{"derivedFrom":makeQuery(id+"F1.opExtrude","SWEPT_BODY",BODY,{"disambiguationData":[OSD([sQuery(id+"F0.wireOp",EDGE,"E0"),sQuery(id+"F0.wireOp",EDGE,"E1"),sQuery(id+"F0.wireOp",EDGE,"E2"),sQuery(id+"F0.wireOp",EDGE,"E3"),sQuery(id+"F0.wireOp",EDGE,"E4"),sQuery(id+"F0.wireOp",EDGE,"E5")])]}),"instanceName":"1"}),"instanceName":"1"});
            var Q1;
            Q1=makeQuery(id+"F19.opPattern","COPY",BODY,{"derivedFrom":makeQuery(id+"F1.opExtrude","SWEPT_BODY",BODY,{"disambiguationData":[OSD([sQuery(id+"F0.wireOp",EDGE,"E0"),sQuery(id+"F0.wireOp",EDGE,"E1"),sQuery(id+"F0.wireOp",EDGE,"E2"),sQuery(id+"F0.wireOp",EDGE,"E3"),sQuery(id+"F0.wireOp",EDGE,"E4"),sQuery(id+"F0.wireOp",EDGE,"E5")])]}),"instanceName":"1"});
            var Q2;
            Q2=makeQuery(id+"F19.opPattern","COPY",BODY,{"derivedFrom":makeQuery(id+"F17.opPattern","COPY",BODY,{"derivedFrom":makeQuery(id+"F1.opExtrude","SWEPT_BODY",BODY,{"disambiguationData":[OSD([sQuery(id+"F0.wireOp",EDGE,"E0"),sQuery(id+"F0.wireOp",EDGE,"E1"),sQuery(id+"F0.wireOp",EDGE,"E2"),sQuery(id+"F0.wireOp",EDGE,"E3"),sQuery(id+"F0.wireOp",EDGE,"E4"),sQuery(id+"F0.wireOp",EDGE,"E5")])]}),"instanceName":"1"}),"instanceName":"1"});
            var Q3;
            Q3=qCreatedBy(makeId("Top.planeOp"),FACE);
            mirror(context, id + "F39", {"entities" : qUnion([Q0, Q1, Q2]), "mirrorPlane" : qUnion([Q3])});
        }
        {
            var Q0;
            Q0=makeQuery(id+"F39.opPattern","COPY",BODY,{"derivedFrom":makeQuery(id+"F19.opPattern","COPY",BODY,{"derivedFrom":makeQuery(id+"F16.opPattern","COPY",BODY,{"derivedFrom":makeQuery(id+"F1.opExtrude","SWEPT_BODY",BODY,{"disambiguationData":[OSD([sQuery(id+"F0.wireOp",EDGE,"E0"),sQuery(id+"F0.wireOp",EDGE,"E1"),sQuery(id+"F0.wireOp",EDGE,"E2"),sQuery(id+"F0.wireOp",EDGE,"E3"),sQuery(id+"F0.wireOp",EDGE,"E4"),sQuery(id+"F0.wireOp",EDGE,"E5")])]}),"instanceName":"1"}),"instanceName":"1"}),"instanceName":"1"});
            var Q1;
            Q1=qCreatedBy(id+"F15.planeOp",FACE);
            mirror(context, id + "F40", {"entities" : qUnion([Q0]), "mirrorPlane" : qUnion([Q1])});
        }
        {
            var Q0;
            {var subQ0=sQuery(id+"F4.wireOp",EDGE,"E8");var subQ1=makeQuery(id+"F5.boolean.opBoolean","COPY",FACE,{"derivedFrom":makeQuery(id+"F5.opExtrude","CAP_FACE",FACE,{"disambiguationData":[OSD([subQ0])],"isStart":false})});Q0=makeQuery(id+"F21.boolean.opBoolean","MERGE",FACE,{"derivedFrom":[makeQuery(id+"F19.opPattern","COPY",FACE,{"derivedFrom":makeQuery(id+"F17.opPattern","COPY",FACE,{"derivedFrom":makeQuery(id+"F9.boolean.opBoolean","SPLIT",FACE,{"disambiguationData":[TD([makeQuery(id+"F5.boolean.opBoolean","COPY",FACE,{"derivedFrom":makeQuery(id+"F5.opExtrude","SWEPT_FACE",FACE,{"disambiguationData":[OSD([subQ0])]})})])],"derivedFrom":subQ1}),"instanceName":"1"}),"instanceName":"1"}),makeQuery(id+"F19.opPattern","COPY",FACE,{"derivedFrom":makeQuery(id+"F17.opPattern","COPY",FACE,{"derivedFrom":makeQuery(id+"F9.boolean.opBoolean","SPLIT",FACE,{"disambiguationData":[TD([makeQuery(id+"F9.opExtrude","SWEPT_FACE",FACE,{"disambiguationData":[OSD([sQuery(id+"F8.wireOp",EDGE,"E25")])]})])],"derivedFrom":subQ1}),"instanceName":"1"}),"instanceName":"1"}),makeQuery(id+"F19.opPattern","COPY",FACE,{"derivedFrom":makeQuery(id+"F17.opPattern","COPY",FACE,{"derivedFrom":makeQuery(id+"F9.boolean.opBoolean","SPLIT",FACE,{"disambiguationData":[TD([makeQuery(id+"F9.opExtrude","SWEPT_FACE",FACE,{"disambiguationData":[OSD([sQuery(id+"F8.wireOp",EDGE,"E32")])]})])],"derivedFrom":subQ1}),"instanceName":"1"}),"instanceName":"1"}),makeQuery(id+"F19.opPattern","COPY",FACE,{"derivedFrom":makeQuery(id+"F17.opPattern","COPY",FACE,{"derivedFrom":makeQuery(id+"F9.boolean.opBoolean","SPLIT",FACE,{"disambiguationData":[TD([makeQuery(id+"F9.opExtrude","SWEPT_FACE",FACE,{"disambiguationData":[OSD([sQuery(id+"F8.wireOp",EDGE,"E33.0")])]})])],"derivedFrom":subQ1}),"instanceName":"1"}),"instanceName":"1"}),makeQuery(id+"F19.opPattern","COPY",FACE,{"derivedFrom":makeQuery(id+"F17.opPattern","COPY",FACE,{"derivedFrom":makeQuery(id+"F9.boolean.opBoolean","SPLIT",FACE,{"disambiguationData":[TD([makeQuery(id+"F9.opExtrude","SWEPT_FACE",FACE,{"disambiguationData":[OSD([sQuery(id+"F8.wireOp",EDGE,"E37")])]})])],"derivedFrom":subQ1}),"instanceName":"1"}),"instanceName":"1"}),makeQuery(id+"F19.opPattern","COPY",FACE,{"derivedFrom":makeQuery(id+"F17.opPattern","COPY",FACE,{"derivedFrom":makeQuery(id+"F9.boolean.opBoolean","SPLIT",FACE,{"disambiguationData":[TD([makeQuery(id+"F9.opExtrude","SWEPT_FACE",FACE,{"disambiguationData":[OSD([sQuery(id+"F8.wireOp",EDGE,"E51.MirrorCS")])]})])],"derivedFrom":subQ1}),"instanceName":"1"}),"instanceName":"1"}),makeQuery(id+"F19.opPattern","COPY",FACE,{"derivedFrom":makeQuery(id+"F17.opPattern","COPY",FACE,{"derivedFrom":makeQuery(id+"F9.boolean.opBoolean","SPLIT",FACE,{"disambiguationData":[TD([makeQuery(id+"F9.opExtrude","SWEPT_FACE",FACE,{"disambiguationData":[OSD([sQuery(id+"F8.wireOp",EDGE,"E53.MirrorCS")])]})])],"derivedFrom":subQ1}),"instanceName":"1"}),"instanceName":"1"}),makeQuery(id+"F19.opPattern","COPY",FACE,{"derivedFrom":makeQuery(id+"F17.opPattern","COPY",FACE,{"derivedFrom":makeQuery(id+"F9.boolean.opBoolean","SPLIT",FACE,{"disambiguationData":[TD([makeQuery(id+"F9.opExtrude","SWEPT_FACE",FACE,{"disambiguationData":[OSD([sQuery(id+"F8.wireOp",EDGE,"E80")])]})])],"derivedFrom":subQ1}),"instanceName":"1"}),"instanceName":"1"}),makeQuery(id+"F19.opPattern","COPY",FACE,{"derivedFrom":makeQuery(id+"F17.opPattern","COPY",FACE,{"derivedFrom":makeQuery(id+"F9.boolean.opBoolean","SPLIT",FACE,{"disambiguationData":[TD([makeQuery(id+"F9.opExtrude","SWEPT_FACE",FACE,{"disambiguationData":[OSD([sQuery(id+"F8.wireOp",EDGE,"E83")])]})])],"derivedFrom":subQ1}),"instanceName":"1"}),"instanceName":"1"}),makeQuery(id+"F21.opExtrude","CAP_FACE",FACE,{"disambiguationData":[OSD([sQuery(id+"F20.wireOp",EDGE,"E309.0.0")])],"isStart":false})]});}
            var sketch = newSketch(context, id + "F41", { "sketchPlane" : qUnion([Q0])});
            skLineSegment(sketch, "E604", {"start": v(-55.42, 47.63) * mm, "end": v(-56.7, 54.28) * mm});
            skArc(sketch, "E605", {"start": v(-52.76, 56.67) * mm, "mid": v(-55.1, 56.09) * mm, "end": v(-56.7, 54.28) * mm});
            skArc(sketch, "E606", {"start": v(-51.27, 56.09) * mm, "mid": v(-52, 56.43) * mm, "end": v(-52.76, 56.67) * mm});
            skLineSegment(sketch, "E607", {"start": v(-51.27, 56.09) * mm, "end": v(-51.27, 49.33) * mm});
            skArc(sketch, "E608", {"start": v(-55.42, 47.63) * mm, "mid": v(-52.98, 47.6) * mm, "end": v(-51.27, 49.33) * mm});
            skArc(sketch, "E609", {"start": v(-56.77, 46.44) * mm, "mid": v(-52.18, 46.1) * mm, "end": v(-49.89, 50.08) * mm});
            skArc(sketch, "E610", {"start": v(-56.13, 48.83) * mm, "mid": v(-56.9, 47.75) * mm, "end": v(-56.77, 46.44) * mm});
            skLineSegment(sketch, "E611", {"start": v(-56.13, 48.83) * mm, "end": v(-55.81, 47.16) * mm});
            skArc(sketch, "E612", {"start": v(-55.81, 47.16) * mm, "mid": v(-52.56, 47.01) * mm, "end": v(-50.52, 49.55) * mm});
            skLineSegment(sketch, "E613", {"start": v(-50.77, 48.8) * mm, "end": v(-50.77, 50.48) * mm});
            skArc(sketch, "E614", {"start": v(-49.89, 50.08) * mm, "mid": v(-50.28, 50.4) * mm, "end": v(-50.77, 50.48) * mm});
            skArc(sketch, "E615", {"start": v(-56.24, 54.12) * mm, "mid": v(-53.69, 53.87) * mm, "end": v(-51.85, 55.66) * mm});
            skArc(sketch, "E616", {"start": v(-56.24, 54.12) * mm, "mid": v(-53.53, 53.4) * mm, "end": v(-51.85, 55.66) * mm});
            skLineSegment(sketch, "E617", {"start": v(-51.85, 43.18) * mm, "end": v(-51.65, 43.56) * mm});
            skArc(sketch, "E618", {"start": v(-51.96, 43.48) * mm, "mid": v(-51.9, 42.7) * mm, "end": v(-51.23, 43.1) * mm});
            skLineSegment(sketch, "E619.trimOffspring", {"start": v(-51.43, 43.99) * mm, "end": v(-46.38, 53.66) * mm});
            skArc(sketch, "E620.trimOffspring", {"start": v(-51.23, 43.1) * mm, "mid": v(-51, 43.43) * mm, "end": v(-51.1, 43.82) * mm});
            skLineSegment(sketch, "E621.trimOffspring", {"start": v(-51.1, 43.82) * mm, "end": v(-45.93, 53.5) * mm});
            skArc(sketch, "E622.trimOffspring", {"start": v(-51.43, 43.99) * mm, "mid": v(-51.81, 43.86) * mm, "end": v(-51.96, 43.48) * mm});
            skArc(sketch, "E623", {"start": v(-45.41, 54.47) * mm, "mid": v(-45.14, 54.5) * mm, "end": v(-44.91, 54.65) * mm});
            skArc(sketch, "E624", {"start": v(-44.11, 54.38) * mm, "mid": v(-44.46, 55.1) * mm, "end": v(-45.07, 55.63) * mm});
            skLineSegment(sketch, "E625", {"start": v(-44.11, 54.38) * mm, "end": v(-44.18, 54.26) * mm});
            skLineSegment(sketch, "E626", {"start": v(-44.18, 54.26) * mm, "end": v(-45.4, 54.9) * mm});
            skArc(sketch, "E627", {"start": v(-46.04, 54.3) * mm, "mid": v(-46.4, 54.08) * mm, "end": v(-46.38, 53.66) * mm});
            skLineSegment(sketch, "E628.trimOffspring", {"start": v(-45.65, 54.03) * mm, "end": v(-45.41, 54.47) * mm});
            skLineSegment(sketch, "E629.trimOffspring", {"start": v(-46.04, 54.3) * mm, "end": v(-45.84, 54.7) * mm});
            skArc(sketch, "E630.trimOffspring", {"start": v(-45.93, 53.5) * mm, "mid": v(-45.68, 53.7) * mm, "end": v(-45.65, 54.03) * mm});
            skPoint(sketch, "E631.orphan", {"position": v(-45.58, 55.2) * mm});
            skPoint(sketch, "E632.trimOffspring.end.orphan", {"position": v(-45.14, 54.97) * mm});
            skArc(sketch, "E633.trimOffspring", {"start": v(-45.02, 55.6) * mm, "mid": v(-45.8, 55.5) * mm, "end": v(-45.84, 54.7) * mm});
            skPoint(sketch, "E634.end.orphan", {"position": v(-44.71, 54.75) * mm});
            skArc(sketch, "E635", {"start": v(-43.25, 49.2) * mm, "mid": v(-44.91, 49.88) * mm, "end": v(-46.63, 49.35) * mm});
            skArc(sketch, "E636", {"start": v(-46.63, 49.35) * mm, "mid": v(-44.98, 48.45) * mm, "end": v(-43.25, 49.2) * mm});
            skArc(sketch, "E637", {"start": v(-46.63, 48.83) * mm, "mid": v(-44.94, 48.12) * mm, "end": v(-43.25, 48.83) * mm});
            skPoint(sketch, "E637.startSnap0", {"position": v(-48.9, 48.83) * mm});
            skPoint(sketch, "E637.endSnap0", {"position": v(-48.9, 48.83) * mm});
            skArc(sketch, "E638", {"start": v(-46.63, 48.83) * mm, "mid": v(-44.94, 47.75) * mm, "end": v(-43.25, 48.83) * mm});
            skArc(sketch, "E639", {"start": v(-46.63, 48.22) * mm, "mid": v(-44.94, 47.35) * mm, "end": v(-43.25, 48.24) * mm});
            skArc(sketch, "E640", {"start": v(-46.63, 48.22) * mm, "mid": v(-44.93, 46.87) * mm, "end": v(-43.25, 48.24) * mm});
            skArc(sketch, "E641", {"start": v(-46.63, 47.64) * mm, "mid": v(-44.97, 46.55) * mm, "end": v(-43.25, 47.55) * mm});
            skArc(sketch, "E642", {"start": v(-46.63, 47.64) * mm, "mid": v(-44.98, 46.16) * mm, "end": v(-43.25, 47.55) * mm});
            skSolve(sketch);
        }
        {
            var Q0;
            Q0 = qSketchRegion(id + "F41", true);
            var Q1;
            Q1=makeQuery(id+"F17.opPattern","COPY",FACE,{"derivedFrom":makeQuery(id+"F9.opExtrude","CAP_FACE",FACE,{"disambiguationData":[OSD([sQuery(id+"F8.wireOp",EDGE,"E20.0"),sQuery(id+"F8.wireOp",EDGE,"E20.1"),sQuery(id+"F8.wireOp",EDGE,"E21.0"),sQuery(id+"F8.wireOp",EDGE,"E21.1"),sQuery(id+"F8.wireOp",EDGE,"E22"),sQuery(id+"F8.wireOp",EDGE,"E23"),sQuery(id+"F8.wireOp",EDGE,"E24"),sQuery(id+"F8.wireOp",EDGE,"E25"),sQuery(id+"F8.wireOp",EDGE,"E26.0"),sQuery(id+"F8.wireOp",EDGE,"E28"),sQuery(id+"F8.wireOp",EDGE,"E29"),sQuery(id+"F8.wireOp",EDGE,"E32"),sQuery(id+"F8.wireOp",EDGE,"E33.0"),sQuery(id+"F8.wireOp",EDGE,"E36"),sQuery(id+"F8.wireOp",EDGE,"E37"),sQuery(id+"F8.wireOp",EDGE,"E38.trimOffspring"),sQuery(id+"F8.wireOp",EDGE,"E39.trimOffspring"),sQuery(id+"F8.wireOp",EDGE,"E40.trimOffspring"),sQuery(id+"F8.wireOp",EDGE,"E41.trimOffspring"),sQuery(id+"F8.wireOp",EDGE,"E42"),sQuery(id+"F8.wireOp",EDGE,"E43"),sQuery(id+"F8.wireOp",EDGE,"E44"),sQuery(id+"F8.wireOp",EDGE,"E45.trimOffspring"),sQuery(id+"F8.wireOp",EDGE,"E46"),sQuery(id+"F8.wireOp",EDGE,"E47"),sQuery(id+"F8.wireOp",EDGE,"E48.trimOffspring"),sQuery(id+"F8.wireOp",EDGE,"E49.trimOffspring"),sQuery(id+"F8.wireOp",EDGE,"E50.MirrorCS"),sQuery(id+"F8.wireOp",EDGE,"E51.MirrorCS"),sQuery(id+"F8.wireOp",EDGE,"E52.MirrorCS"),sQuery(id+"F8.wireOp",EDGE,"E53.MirrorCS"),sQuery(id+"F8.wireOp",EDGE,"E54.MirrorCS"),sQuery(id+"F8.wireOp",EDGE,"E55.MirrorCS"),sQuery(id+"F8.wireOp",EDGE,"E56.MirrorCS"),sQuery(id+"F8.wireOp",EDGE,"E57.MirrorCS"),sQuery(id+"F8.wireOp",EDGE,"E58.MirrorCS"),sQuery(id+"F8.wireOp",EDGE,"E59.MirrorCS"),sQuery(id+"F8.wireOp",EDGE,"E61.trimOffspring"),sQuery(id+"F8.wireOp",EDGE,"E62.trimOffspring"),sQuery(id+"F8.wireOp",EDGE,"E63")])],"isStart":false}),"instanceName":"1"});
            extrude(context, id + "F42", {"entities" : qUnion([Q0]), "operationType" : NewBodyOperationType.ADD, "endBound" : BoundingType.UP_TO_SURFACE, "depth" : 25.4 * mm, "endBoundEntityFace" : qUnion([Q1]), "offsetDistance" : 25.4 * mm});
        }
        {
            var Q0;
            Q0=makeQuery(id+"F42.opExtrude","CAP_FACE",FACE,{"disambiguationData":[OSD([sQuery(id+"F41.wireOp",EDGE,"E604"),sQuery(id+"F41.wireOp",EDGE,"E605"),sQuery(id+"F41.wireOp",EDGE,"E606"),sQuery(id+"F41.wireOp",EDGE,"E607"),sQuery(id+"F41.wireOp",EDGE,"E608"),sQuery(id+"F41.wireOp",EDGE,"E615"),sQuery(id+"F41.wireOp",EDGE,"E616")])],"isStart":false});
            var sketch = newSketch(context, id + "F43", { "sketchPlane" : qUnion([Q0])});
            skLineSegment(sketch, "E643.0.0", {"start": v(-56.7, 54.28) * mm, "end": v(-55.42, 47.63) * mm});
            skArc(sketch, "E643.0.1", {"start": v(-55.42, 47.63) * mm, "mid": v(-52.98, 47.6) * mm, "end": v(-51.27, 49.33) * mm});
            skLineSegment(sketch, "E643.0.2", {"start": v(-51.27, 49.33) * mm, "end": v(-51.27, 56.09) * mm});
            skArc(sketch, "E643.0.3", {"start": v(-51.27, 56.09) * mm, "mid": v(-52, 56.43) * mm, "end": v(-52.76, 56.67) * mm});
            skArc(sketch, "E643.0.4", {"start": v(-52.76, 56.67) * mm, "mid": v(-55.1, 56.09) * mm, "end": v(-56.7, 54.28) * mm});
            skSolve(sketch);
        }
        {
            var Q0;
            Q0 = qSketchRegion(id + "F43", true);
            extrude(context, id + "F44", {"entities" : qUnion([Q0]), "operationType" : NewBodyOperationType.REMOVE, "oppositeDirection" : true, "depth" : 0.5 * mm, "offsetDistance" : 25.4 * mm});
        }
        {
            var Q0;
            {var subQ0=sQuery(id+"F4.wireOp",EDGE,"E8");var subQ1=makeQuery(id+"F5.boolean.opBoolean","COPY",FACE,{"derivedFrom":makeQuery(id+"F5.opExtrude","CAP_FACE",FACE,{"disambiguationData":[OSD([subQ0])],"isStart":false})});Q0=makeQuery(id+"F21.boolean.opBoolean","MERGE",FACE,{"derivedFrom":[makeQuery(id+"F19.opPattern","COPY",FACE,{"derivedFrom":makeQuery(id+"F9.boolean.opBoolean","SPLIT",FACE,{"disambiguationData":[TD([makeQuery(id+"F5.boolean.opBoolean","COPY",FACE,{"derivedFrom":makeQuery(id+"F5.opExtrude","SWEPT_FACE",FACE,{"disambiguationData":[OSD([subQ0])]})})])],"derivedFrom":subQ1}),"instanceName":"1"}),makeQuery(id+"F19.opPattern","COPY",FACE,{"derivedFrom":makeQuery(id+"F9.boolean.opBoolean","SPLIT",FACE,{"disambiguationData":[TD([makeQuery(id+"F9.opExtrude","SWEPT_FACE",FACE,{"disambiguationData":[OSD([sQuery(id+"F8.wireOp",EDGE,"E25")])]})])],"derivedFrom":subQ1}),"instanceName":"1"}),makeQuery(id+"F19.opPattern","COPY",FACE,{"derivedFrom":makeQuery(id+"F9.boolean.opBoolean","SPLIT",FACE,{"disambiguationData":[TD([makeQuery(id+"F9.opExtrude","SWEPT_FACE",FACE,{"disambiguationData":[OSD([sQuery(id+"F8.wireOp",EDGE,"E32")])]})])],"derivedFrom":subQ1}),"instanceName":"1"}),makeQuery(id+"F19.opPattern","COPY",FACE,{"derivedFrom":makeQuery(id+"F9.boolean.opBoolean","SPLIT",FACE,{"disambiguationData":[TD([makeQuery(id+"F9.opExtrude","SWEPT_FACE",FACE,{"disambiguationData":[OSD([sQuery(id+"F8.wireOp",EDGE,"E33.0")])]})])],"derivedFrom":subQ1}),"instanceName":"1"}),makeQuery(id+"F19.opPattern","COPY",FACE,{"derivedFrom":makeQuery(id+"F9.boolean.opBoolean","SPLIT",FACE,{"disambiguationData":[TD([makeQuery(id+"F9.opExtrude","SWEPT_FACE",FACE,{"disambiguationData":[OSD([sQuery(id+"F8.wireOp",EDGE,"E37")])]})])],"derivedFrom":subQ1}),"instanceName":"1"}),makeQuery(id+"F19.opPattern","COPY",FACE,{"derivedFrom":makeQuery(id+"F9.boolean.opBoolean","SPLIT",FACE,{"disambiguationData":[TD([makeQuery(id+"F9.opExtrude","SWEPT_FACE",FACE,{"disambiguationData":[OSD([sQuery(id+"F8.wireOp",EDGE,"E51.MirrorCS")])]})])],"derivedFrom":subQ1}),"instanceName":"1"}),makeQuery(id+"F19.opPattern","COPY",FACE,{"derivedFrom":makeQuery(id+"F9.boolean.opBoolean","SPLIT",FACE,{"disambiguationData":[TD([makeQuery(id+"F9.opExtrude","SWEPT_FACE",FACE,{"disambiguationData":[OSD([sQuery(id+"F8.wireOp",EDGE,"E53.MirrorCS")])]})])],"derivedFrom":subQ1}),"instanceName":"1"}),makeQuery(id+"F19.opPattern","COPY",FACE,{"derivedFrom":makeQuery(id+"F9.boolean.opBoolean","SPLIT",FACE,{"disambiguationData":[TD([makeQuery(id+"F9.opExtrude","SWEPT_FACE",FACE,{"disambiguationData":[OSD([sQuery(id+"F8.wireOp",EDGE,"E80")])]})])],"derivedFrom":subQ1}),"instanceName":"1"}),makeQuery(id+"F19.opPattern","COPY",FACE,{"derivedFrom":makeQuery(id+"F9.boolean.opBoolean","SPLIT",FACE,{"disambiguationData":[TD([makeQuery(id+"F9.opExtrude","SWEPT_FACE",FACE,{"disambiguationData":[OSD([sQuery(id+"F8.wireOp",EDGE,"E83")])]})])],"derivedFrom":subQ1}),"instanceName":"1"}),makeQuery(id+"F21.opExtrude","CAP_FACE",FACE,{"disambiguationData":[OSD([sQuery(id+"F20.wireOp",EDGE,"E308.0.0")])],"isStart":false})]});}
            var sketch = newSketch(context, id + "F45", { "sketchPlane" : qUnion([Q0])});
            skArc(sketch, "E644", {"start": v(-1.56, 45.54) * mm, "mid": v(-5.29, 47.16) * mm, "end": v(-3.78, 43.38) * mm});
            skLineSegment(sketch, "E645", {"start": v(-3.78, 43.38) * mm, "end": v(-2.98, 42.03) * mm});
            skLineSegment(sketch, "E646.MirrorCS", {"start": v(-1.56, 45.54) * mm, "end": v(-0.23, 44.7) * mm});
            skArc(sketch, "E647", {"start": v(-2.98, 42.03) * mm, "mid": v(-2.63, 42.25) * mm, "end": v(-2.3, 42.5) * mm});
            skLineSegment(sketch, "E648", {"start": v(-2.3, 42.5) * mm, "end": v(-2.58, 43.19) * mm});
            skLineSegment(sketch, "E649", {"start": v(-2.58, 43.19) * mm, "end": v(-2, 42.73) * mm});
            skLineSegment(sketch, "E650.MirrorCS", {"start": v(-1.4, 44.34) * mm, "end": v(-0.96, 43.74) * mm});
            skLineSegment(sketch, "E651.MirrorCS", {"start": v(-0.7, 44.04) * mm, "end": v(-1.4, 44.34) * mm});
            skLineSegment(sketch, "E652", {"start": v(-2.9, 44.7) * mm, "end": v(-2.73, 43.86) * mm});
            skLineSegment(sketch, "E653", {"start": v(-2.73, 43.86) * mm, "end": v(-2.4, 44.18) * mm});
            skLineSegment(sketch, "E654.MirrorCS", {"start": v(-2.9, 44.7) * mm, "end": v(-2.06, 44.5) * mm});
            skLineSegment(sketch, "E655.MirrorCS", {"start": v(-2.06, 44.5) * mm, "end": v(-2.4, 44.18) * mm});
            skCircle(sketch, "E656", {"center": v(-4.62, 44.92) * mm, "radius": 0.86 * mm});
            skCircle(sketch, "E657.MirrorC", {"center": v(-3.07, 46.43) * mm, "radius": 0.86 * mm});
            skArc(sketch, "E658.trimOffspring", {"start": v(-2, 42.73) * mm, "mid": v(-1.45, 43.22) * mm, "end": v(-0.96, 43.74) * mm});
            skArc(sketch, "E659.trimOffspring", {"start": v(-0.7, 44.04) * mm, "mid": v(-0.46, 44.36) * mm, "end": v(-0.23, 44.7) * mm});
            skArc(sketch, "E660", {"start": v(5.06, 44.8) * mm, "mid": v(6.87, 47.13) * mm, "end": v(6.47, 50.06) * mm});
            skArc(sketch, "E661", {"start": v(5.7, 43.78) * mm, "mid": v(7.65, 46.73) * mm, "end": v(6.47, 50.06) * mm});
            skLineSegment(sketch, "E662", {"start": v(-47.62, 26.81) * mm, "end": v(-49.71, 31.34) * mm});
            skArc(sketch, "E663.MirrorCS", {"start": v(1.47, 46.89) * mm, "mid": v(1.95, 46.83) * mm, "end": v(2.43, 46.84) * mm});
            skLineSegment(sketch, "E664.MirrorCS", {"start": v(1.47, 46.89) * mm, "end": v(1.12, 46.15) * mm});
            skLineSegment(sketch, "E665.MirrorCS", {"start": v(-0.43, 48.2) * mm, "end": v(-1.2, 47.92) * mm});
            skArc(sketch, "E666.MirrorCS", {"start": v(-1.67, 49.22) * mm, "mid": v(-1.5, 48.55) * mm, "end": v(-1.2, 47.92) * mm});
            skLineSegment(sketch, "E667.MirrorCS", {"start": v(-0.13, 46.74) * mm, "end": v(0.22, 47.48) * mm});
            skArc(sketch, "E668.MirrorCS", {"start": v(-0.43, 48.2) * mm, "mid": v(-0.13, 47.81) * mm, "end": v(0.22, 47.48) * mm});
            skLineSegment(sketch, "E669.MirrorCS", {"start": v(4.63, 51.48) * mm, "end": v(5.4, 51.75) * mm});
            skArc(sketch, "E670.MirrorCS", {"start": v(-0.13, 46.74) * mm, "mid": v(0.47, 46.39) * mm, "end": v(1.12, 46.15) * mm});
            skArc(sketch, "E671.MirrorCS", {"start": v(0.46, 52.36) * mm, "mid": v(0.08, 52.07) * mm, "end": v(-0.25, 51.71) * mm});
            skArc(sketch, "E672.MirrorCS", {"start": v(3.74, 47.3) * mm, "mid": v(4.12, 47.6) * mm, "end": v(4.45, 47.96) * mm});
            skLineSegment(sketch, "E673.MirrorCS", {"start": v(2.73, 52.78) * mm, "end": v(3.08, 53.52) * mm});
            skArc(sketch, "E674.MirrorCS", {"start": v(4.63, 51.48) * mm, "mid": v(4.33, 51.86) * mm, "end": v(3.98, 52.19) * mm});
            skLineSegment(sketch, "E675.MirrorCS", {"start": v(4.33, 52.93) * mm, "end": v(3.98, 52.19) * mm});
            skArc(sketch, "E676.MirrorCS", {"start": v(4.33, 52.93) * mm, "mid": v(3.73, 53.29) * mm, "end": v(3.08, 53.52) * mm});
            skArc(sketch, "E677.MirrorCS", {"start": v(2.73, 52.78) * mm, "mid": v(2.25, 52.84) * mm, "end": v(1.76, 52.83) * mm});
            skLineSegment(sketch, "E678.MirrorCS", {"start": v(5.87, 50.45) * mm, "end": v(5.1, 50.17) * mm});
            skLineSegment(sketch, "E679.MirrorCS", {"start": v(-1.67, 49.22) * mm, "end": v(-0.9, 49.5) * mm});
            skLineSegment(sketch, "E680.MirrorCS", {"start": v(0.46, 52.36) * mm, "end": v(0.18, 53.13) * mm});
            skLineSegment(sketch, "E681.MirrorCS", {"start": v(1.49, 53.6) * mm, "end": v(1.76, 52.83) * mm});
            skArc(sketch, "E682.MirrorCS", {"start": v(5.87, 50.45) * mm, "mid": v(5.7, 51.12) * mm, "end": v(5.4, 51.75) * mm});
            skLineSegment(sketch, "E683.MirrorCS", {"start": v(2.71, 46.07) * mm, "end": v(2.43, 46.84) * mm});
            skArc(sketch, "E684.MirrorCS", {"start": v(5.05, 49.2) * mm, "mid": v(5.1, 49.69) * mm, "end": v(5.1, 50.17) * mm});
            skArc(sketch, "E685.MirrorCS", {"start": v(-0.85, 50.46) * mm, "mid": v(-0.9, 49.98) * mm, "end": v(-0.9, 49.5) * mm});
            skArc(sketch, "E686.MirrorCS", {"start": v(5.2, 47.6) * mm, "mid": v(5.55, 48.2) * mm, "end": v(5.79, 48.86) * mm});
            skLineSegment(sketch, "E687.MirrorCS", {"start": v(5.2, 47.6) * mm, "end": v(4.45, 47.96) * mm});
            skArc(sketch, "E688.MirrorCS", {"start": v(-1, 52.07) * mm, "mid": v(-1.35, 51.47) * mm, "end": v(-1.59, 50.81) * mm});
            skLineSegment(sketch, "E689.MirrorCS", {"start": v(-1, 52.07) * mm, "end": v(-0.25, 51.71) * mm});
            skLineSegment(sketch, "E690.MirrorCS", {"start": v(5.05, 49.2) * mm, "end": v(5.79, 48.86) * mm});
            skLineSegment(sketch, "E691.MirrorCS", {"start": v(-0.85, 50.46) * mm, "end": v(-1.59, 50.81) * mm});
            skLineSegment(sketch, "E692.MirrorCS", {"start": v(3.74, 47.3) * mm, "end": v(4.02, 46.54) * mm});
            skArc(sketch, "E693.MirrorCS", {"start": v(2.71, 46.07) * mm, "mid": v(3.39, 46.24) * mm, "end": v(4.02, 46.54) * mm});
            skArc(sketch, "E694.MirrorCS", {"start": v(1.49, 53.6) * mm, "mid": v(0.81, 53.43) * mm, "end": v(0.18, 53.13) * mm});
            skCircle(sketch, "E695.MirrorC", {"center": v(2.1, 49.84) * mm, "radius": 1.53 * mm});
            skLineSegment(sketch, "E696", {"start": v(-7.6, 49.54) * mm, "end": v(-4.25, 52.62) * mm});
            skLineSegment(sketch, "E697", {"start": v(-4.25, 52.62) * mm, "end": v(-2.95, 52.22) * mm});
            skLineSegment(sketch, "E698", {"start": v(-2.95, 52.22) * mm, "end": v(-6.9, 48.17) * mm});
            skLineSegment(sketch, "E699", {"start": v(-6.9, 48.17) * mm, "end": v(-7.6, 49.54) * mm});
            skLineSegment(sketch, "E700", {"start": v(-7.9, 49.44) * mm, "end": v(-7.1, 47.92) * mm});
            skLineSegment(sketch, "E701", {"start": v(-7.1, 47.92) * mm, "end": v(-9.3, 48.3) * mm});
            skLineSegment(sketch, "E702", {"start": v(-9.3, 48.3) * mm, "end": v(-8.91, 49.54) * mm});
            skLineSegment(sketch, "E703", {"start": v(-8.91, 49.54) * mm, "end": v(-7.9, 49.44) * mm});
            skLineSegment(sketch, "E704", {"start": v(-8.79, 49.86) * mm, "end": v(-7.93, 49.77) * mm});
            skLineSegment(sketch, "E705", {"start": v(-7.93, 49.77) * mm, "end": v(-4.78, 52.67) * mm});
            skLineSegment(sketch, "E706", {"start": v(-4.78, 52.67) * mm, "end": v(-5.68, 52.76) * mm});
            skLineSegment(sketch, "E707", {"start": v(-5.68, 52.76) * mm, "end": v(-8.79, 49.86) * mm});
            skArc(sketch, "E708", {"start": v(1.4, 57.9) * mm, "mid": v(0.36, 59.26) * mm, "end": v(-1.32, 59.52) * mm});
            skLineSegment(sketch, "E709", {"start": v(-3.1, 57.52) * mm, "end": v(-6.68, 54.95) * mm});
            skLineSegment(sketch, "E710", {"start": v(-6.68, 54.95) * mm, "end": v(-6.34, 54.76) * mm});
            skLineSegment(sketch, "E711", {"start": v(-5.2, 54.75) * mm, "end": v(-2.77, 56.08) * mm});
            skLineSegment(sketch, "E712", {"start": v(1.4, 57.9) * mm, "end": v(2.71, 56) * mm});
            skLineSegment(sketch, "E713", {"start": v(2.71, 56) * mm, "end": v(3.75, 55.53) * mm});
            skArc(sketch, "E714", {"start": v(0.78, 55.62) * mm, "mid": v(-0.97, 56.07) * mm, "end": v(-2.77, 56.08) * mm});
            skLineSegment(sketch, "E715", {"start": v(-3.63, 55.6) * mm, "end": v(-4.58, 54.03) * mm});
            skLineSegment(sketch, "E716", {"start": v(-3.29, 54.44) * mm, "end": v(-2.17, 56.12) * mm});
            skLineSegment(sketch, "E717", {"start": v(-2.5, 55.62) * mm, "end": v(-2.74, 54.18) * mm});
            skLineSegment(sketch, "E718", {"start": v(-2.16, 54.44) * mm, "end": v(-1.6, 56.12) * mm});
            skLineSegment(sketch, "E719", {"start": v(-1.7, 55.86) * mm, "end": v(-1.7, 54.75) * mm});
            skLineSegment(sketch, "E720", {"start": v(-1.3, 55.07) * mm, "end": v(-1.3, 56.1) * mm});
            skLineSegment(sketch, "E721", {"start": v(-3.1, 57.52) * mm, "end": v(-1.32, 59.52) * mm});
            skArc(sketch, "E722", {"start": v(0.78, 55.62) * mm, "mid": v(2.1, 54.93) * mm, "end": v(3.58, 55.14) * mm});
            skLineSegment(sketch, "E723", {"start": v(3.58, 55.14) * mm, "end": v(3.75, 55.53) * mm});
            skArc(sketch, "E724", {"start": v(-6.4, 54.8) * mm, "mid": v(-5.77, 54.62) * mm, "end": v(-5.13, 54.79) * mm});
            skArc(sketch, "E725", {"start": v(-4, 54.03) * mm, "mid": v(-3.6, 54.17) * mm, "end": v(-3.29, 54.44) * mm});
            skPoint(sketch, "E726.orphan", {"position": v(-5.77, 54.44) * mm});
            skSolve(sketch);
        }
        {
            var Q0;
            Q0 = qSketchRegion(id + "F45", true);
            var Q1;
            Q1=makeQuery(id+"F23.opExtrude","CAP_FACE",FACE,{"disambiguationData":[OSD([sQuery(id+"F22.wireOp",EDGE,"E311"),sQuery(id+"F22.wireOp",EDGE,"E312"),sQuery(id+"F22.wireOp",EDGE,"E313"),sQuery(id+"F22.wireOp",EDGE,"E314"),sQuery(id+"F22.wireOp",EDGE,"E315"),sQuery(id+"F22.wireOp",EDGE,"E316"),sQuery(id+"F22.wireOp",EDGE,"E317"),sQuery(id+"F22.wireOp",EDGE,"E318"),sQuery(id+"F22.wireOp",EDGE,"E319"),sQuery(id+"F22.wireOp",EDGE,"E320"),sQuery(id+"F22.wireOp",EDGE,"E328.trimOffspring"),sQuery(id+"F22.wireOp",EDGE,"E329.trimOffspring"),sQuery(id+"F22.wireOp",EDGE,"E330.trimOffspring"),sQuery(id+"F22.wireOp",EDGE,"E331"),sQuery(id+"F22.wireOp",EDGE,"E332.trimOffspring"),sQuery(id+"F22.wireOp",EDGE,"E333"),sQuery(id+"F22.wireOp",EDGE,"E334"),sQuery(id+"F22.wireOp",EDGE,"E335"),sQuery(id+"F22.wireOp",EDGE,"E336"),sQuery(id+"F22.wireOp",EDGE,"E337"),sQuery(id+"F22.wireOp",EDGE,"E348.trimOffspring")])],"isStart":false});
            extrude(context, id + "F46", {"entities" : qUnion([Q0]), "operationType" : NewBodyOperationType.ADD, "endBound" : BoundingType.UP_TO_SURFACE, "depth" : 25.4 * mm, "endBoundEntityFace" : qUnion([Q1]), "offsetDistance" : 25.4 * mm});
        }
        {
            var Q0;
            {var subQ0=sQuery(id+"F4.wireOp",EDGE,"E8");var subQ1=makeQuery(id+"F5.boolean.opBoolean","COPY",FACE,{"derivedFrom":makeQuery(id+"F5.opExtrude","SWEPT_FACE",FACE,{"disambiguationData":[OSD([subQ0])]})});var subQ2=makeQuery(id+"F5.boolean.opBoolean","COPY",FACE,{"derivedFrom":makeQuery(id+"F5.opExtrude","CAP_FACE",FACE,{"disambiguationData":[OSD([subQ0])],"isStart":false})});Q0=makeQuery(id+"F46.boolean.opBoolean","SPLIT",FACE,{"disambiguationData":[TD([makeQuery(id+"F19.opPattern","COPY",FACE,{"derivedFrom":subQ1,"instanceName":"1"})])],"derivedFrom":makeQuery(id+"F21.boolean.opBoolean","MERGE",FACE,{"derivedFrom":[makeQuery(id+"F19.opPattern","COPY",FACE,{"derivedFrom":makeQuery(id+"F9.boolean.opBoolean","SPLIT",FACE,{"disambiguationData":[TD([subQ1])],"derivedFrom":subQ2}),"instanceName":"1"}),makeQuery(id+"F19.opPattern","COPY",FACE,{"derivedFrom":makeQuery(id+"F9.boolean.opBoolean","SPLIT",FACE,{"disambiguationData":[TD([makeQuery(id+"F9.opExtrude","SWEPT_FACE",FACE,{"disambiguationData":[OSD([sQuery(id+"F8.wireOp",EDGE,"E25")])]})])],"derivedFrom":subQ2}),"instanceName":"1"}),makeQuery(id+"F19.opPattern","COPY",FACE,{"derivedFrom":makeQuery(id+"F9.boolean.opBoolean","SPLIT",FACE,{"disambiguationData":[TD([makeQuery(id+"F9.opExtrude","SWEPT_FACE",FACE,{"disambiguationData":[OSD([sQuery(id+"F8.wireOp",EDGE,"E32")])]})])],"derivedFrom":subQ2}),"instanceName":"1"}),makeQuery(id+"F19.opPattern","COPY",FACE,{"derivedFrom":makeQuery(id+"F9.boolean.opBoolean","SPLIT",FACE,{"disambiguationData":[TD([makeQuery(id+"F9.opExtrude","SWEPT_FACE",FACE,{"disambiguationData":[OSD([sQuery(id+"F8.wireOp",EDGE,"E33.0")])]})])],"derivedFrom":subQ2}),"instanceName":"1"}),makeQuery(id+"F19.opPattern","COPY",FACE,{"derivedFrom":makeQuery(id+"F9.boolean.opBoolean","SPLIT",FACE,{"disambiguationData":[TD([makeQuery(id+"F9.opExtrude","SWEPT_FACE",FACE,{"disambiguationData":[OSD([sQuery(id+"F8.wireOp",EDGE,"E37")])]})])],"derivedFrom":subQ2}),"instanceName":"1"}),makeQuery(id+"F19.opPattern","COPY",FACE,{"derivedFrom":makeQuery(id+"F9.boolean.opBoolean","SPLIT",FACE,{"disambiguationData":[TD([makeQuery(id+"F9.opExtrude","SWEPT_FACE",FACE,{"disambiguationData":[OSD([sQuery(id+"F8.wireOp",EDGE,"E51.MirrorCS")])]})])],"derivedFrom":subQ2}),"instanceName":"1"}),makeQuery(id+"F19.opPattern","COPY",FACE,{"derivedFrom":makeQuery(id+"F9.boolean.opBoolean","SPLIT",FACE,{"disambiguationData":[TD([makeQuery(id+"F9.opExtrude","SWEPT_FACE",FACE,{"disambiguationData":[OSD([sQuery(id+"F8.wireOp",EDGE,"E53.MirrorCS")])]})])],"derivedFrom":subQ2}),"instanceName":"1"}),makeQuery(id+"F19.opPattern","COPY",FACE,{"derivedFrom":makeQuery(id+"F9.boolean.opBoolean","SPLIT",FACE,{"disambiguationData":[TD([makeQuery(id+"F9.opExtrude","SWEPT_FACE",FACE,{"disambiguationData":[OSD([sQuery(id+"F8.wireOp",EDGE,"E80")])]})])],"derivedFrom":subQ2}),"instanceName":"1"}),makeQuery(id+"F19.opPattern","COPY",FACE,{"derivedFrom":makeQuery(id+"F9.boolean.opBoolean","SPLIT",FACE,{"disambiguationData":[TD([makeQuery(id+"F9.opExtrude","SWEPT_FACE",FACE,{"disambiguationData":[OSD([sQuery(id+"F8.wireOp",EDGE,"E83")])]})])],"derivedFrom":subQ2}),"instanceName":"1"})],"fromTools":[makeQuery(id+"F21.opExtrude","CAP_FACE",FACE,{"disambiguationData":[OSD([sQuery(id+"F20.wireOp",EDGE,"E308.0.0")])],"isStart":false})]})});}
            var sketch = newSketch(context, id + "F47", { "sketchPlane" : qUnion([Q0])});
            skArc(sketch, "E727.0", {"start": v(5.06, 44.8) * mm, "mid": v(6.87, 47.13) * mm, "end": v(6.47, 50.06) * mm});
            skLineSegment(sketch, "E728.0", {"start": v(-3.63, 55.6) * mm, "end": v(-4.58, 54.03) * mm});
            skArc(sketch, "E729.0", {"start": v(-4, 54.03) * mm, "mid": v(-3.6, 54.17) * mm, "end": v(-3.29, 54.44) * mm});
            skLineSegment(sketch, "E730.0", {"start": v(-3.29, 54.44) * mm, "end": v(-2.17, 56.12) * mm});
            skLineSegment(sketch, "E731.0", {"start": v(-2.5, 55.62) * mm, "end": v(-2.74, 54.18) * mm});
            skLineSegment(sketch, "E732.0", {"start": v(-2.16, 54.44) * mm, "end": v(-1.6, 56.12) * mm});
            skLineSegment(sketch, "E733.0", {"start": v(-1.7, 55.86) * mm, "end": v(-1.7, 54.75) * mm});
            skLineSegment(sketch, "E734.0", {"start": v(-1.3, 55.07) * mm, "end": v(-1.3, 56.1) * mm});
            skLineSegment(sketch, "E735", {"start": v(-4, 54.03) * mm, "end": v(-4.58, 54.03) * mm});
            skArc(sketch, "E736", {"start": v(-2.74, 54.18) * mm, "mid": v(-2.4, 54.18) * mm, "end": v(-2.16, 54.44) * mm});
            skArc(sketch, "E737", {"start": v(-1.7, 54.75) * mm, "mid": v(-1.42, 54.82) * mm, "end": v(-1.3, 55.07) * mm});
            skLineSegment(sketch, "E738.0", {"start": v(-5.2, 54.75) * mm, "end": v(-2.77, 56.08) * mm});
            skArc(sketch, "E739.0", {"start": v(0.78, 55.62) * mm, "mid": v(-0.97, 56.07) * mm, "end": v(-2.77, 56.08) * mm});
            skArc(sketch, "E740.0", {"start": v(5.7, 43.78) * mm, "mid": v(7.65, 46.73) * mm, "end": v(6.47, 50.06) * mm});
            skLineSegment(sketch, "E741", {"start": v(5.06, 44.8) * mm, "end": v(5.7, 43.78) * mm});
            skCircle(sketch, "E742", {"center": v(5.38, 44.29) * mm, "radius": 0.6 * mm});
            skCircle(sketch, "E743", {"center": v(1.4, 43.16) * mm, "radius": 1.4 * mm});
            skSolve(sketch);
        }
        {
            var Q0;
            Q0 = qSketchRegion(id + "F47", true);
            var Q1;
            Q1=makeQuery(id+"F34.opExtrude","CAP_FACE",FACE,{"disambiguationData":[OSD([sQuery(id+"F33.wireOp",EDGE,"E523"),sQuery(id+"F33.wireOp",EDGE,"E524"),sQuery(id+"F33.wireOp",EDGE,"E525"),sQuery(id+"F33.wireOp",EDGE,"E526"),sQuery(id+"F33.wireOp",EDGE,"E527"),sQuery(id+"F33.wireOp",EDGE,"E528.trimOffspring"),sQuery(id+"F33.wireOp",EDGE,"E529.MirrorCS"),sQuery(id+"F33.wireOp",EDGE,"E530.MirrorCS"),sQuery(id+"F33.wireOp",EDGE,"E534.MirrorCS"),sQuery(id+"F33.wireOp",EDGE,"E535.MirrorCS"),sQuery(id+"F33.wireOp",EDGE,"E536.MirrorCS"),sQuery(id+"F33.wireOp",EDGE,"E537.MirrorCS"),sQuery(id+"F33.wireOp",EDGE,"E538.MirrorCS"),sQuery(id+"F33.wireOp",EDGE,"E539.MirrorCS"),sQuery(id+"F33.wireOp",EDGE,"E540.MirrorCS"),sQuery(id+"F33.wireOp",EDGE,"E541.MirrorCS"),sQuery(id+"F33.wireOp",EDGE,"E542.MirrorCS"),sQuery(id+"F33.wireOp",EDGE,"E543.MirrorCS"),sQuery(id+"F33.wireOp",EDGE,"E544.MirrorCS"),sQuery(id+"F33.wireOp",EDGE,"E545.MirrorCS"),sQuery(id+"F33.wireOp",EDGE,"E546.MirrorCS"),sQuery(id+"F33.wireOp",EDGE,"E547.MirrorCS"),sQuery(id+"F33.wireOp",EDGE,"E548.MirrorCS"),sQuery(id+"F33.wireOp",EDGE,"E549.MirrorCS"),sQuery(id+"F33.wireOp",EDGE,"E551.trimOffspring"),sQuery(id+"F33.wireOp",EDGE,"E552.trimOffspring"),sQuery(id+"F33.wireOp",EDGE,"E553.trimOffspring"),sQuery(id+"F33.wireOp",EDGE,"E554.trimOffspring"),sQuery(id+"F33.wireOp",EDGE,"E555.trimOffspring"),sQuery(id+"F33.wireOp",EDGE,"E556.trimOffspring"),sQuery(id+"F33.wireOp",EDGE,"E557.trimOffspring"),sQuery(id+"F33.wireOp",EDGE,"E558.trimOffspring"),sQuery(id+"F33.wireOp",EDGE,"E559.trimOffspring"),sQuery(id+"F33.wireOp",EDGE,"E560.trimOffspring"),sQuery(id+"F33.wireOp",EDGE,"E561.trimOffspring"),sQuery(id+"F33.wireOp",EDGE,"E562.trimOffspring"),sQuery(id+"F33.wireOp",EDGE,"E563.trimOffspring"),sQuery(id+"F33.wireOp",EDGE,"E564.trimOffspring"),sQuery(id+"F33.wireOp",EDGE,"E565.trimOffspring"),sQuery(id+"F33.wireOp",EDGE,"E566.trimOffspring"),sQuery(id+"F33.wireOp",EDGE,"E567.trimOffspring"),sQuery(id+"F33.wireOp",EDGE,"E568.trimOffspring"),sQuery(id+"F33.wireOp",EDGE,"E569.trimOffspring"),sQuery(id+"F33.wireOp",EDGE,"E570.trimOffspring"),sQuery(id+"F33.wireOp",EDGE,"E571.trimOffspring"),sQuery(id+"F33.wireOp",EDGE,"E572.trimOffspring"),sQuery(id+"F33.wireOp",EDGE,"E573.trimOffspring"),sQuery(id+"F33.wireOp",EDGE,"E574.trimOffspring"),sQuery(id+"F33.wireOp",EDGE,"E575.trimOffspring"),sQuery(id+"F33.wireOp",EDGE,"E576.trimOffspring"),sQuery(id+"F33.wireOp",EDGE,"E577.trimOffspring"),sQuery(id+"F33.wireOp",EDGE,"E578.trimOffspring"),sQuery(id+"F33.wireOp",EDGE,"E579.trimOffspring"),sQuery(id+"F33.wireOp",EDGE,"E580.trimOffspring"),sQuery(id+"F33.wireOp",EDGE,"E581.trimOffspring"),sQuery(id+"F33.wireOp",EDGE,"E582.trimOffspring"),sQuery(id+"F33.wireOp",EDGE,"E583.trimOffspring"),sQuery(id+"F33.wireOp",EDGE,"E584.trimOffspring"),sQuery(id+"F33.wireOp",EDGE,"E585.trimOffspring"),sQuery(id+"F33.wireOp",EDGE,"E586.trimOffspring"),sQuery(id+"F33.wireOp",EDGE,"E587.trimOffspring"),sQuery(id+"F33.wireOp",EDGE,"E588.trimOffspring"),sQuery(id+"F33.wireOp",EDGE,"E589.trimOffspring"),sQuery(id+"F33.wireOp",EDGE,"E590.trimOffspring"),sQuery(id+"F33.wireOp",EDGE,"E591.trimOffspring"),sQuery(id+"F33.wireOp",EDGE,"E592.trimOffspring"),sQuery(id+"F33.wireOp",EDGE,"E593.trimOffspring"),sQuery(id+"F33.wireOp",EDGE,"E594.trimOffspring"),sQuery(id+"F33.wireOp",EDGE,"E595.trimOffspring"),sQuery(id+"F33.wireOp",EDGE,"E596.trimOffspring"),sQuery(id+"F33.wireOp",EDGE,"E597.trimOffspring"),sQuery(id+"F33.wireOp",EDGE,"E598.trimOffspring")])],"isStart":false});
            extrude(context, id + "F48", {"entities" : qUnion([Q0]), "operationType" : NewBodyOperationType.ADD, "endBound" : BoundingType.UP_TO_SURFACE, "depth" : 25.4 * mm, "endBoundEntityFace" : qUnion([Q1]), "offsetDistance" : 25.4 * mm});
        }
        {
            var Q0;
            {var subQ0=sQuery(id+"F4.wireOp",EDGE,"E8");var subQ1=makeQuery(id+"F5.boolean.opBoolean","COPY",FACE,{"derivedFrom":makeQuery(id+"F5.opExtrude","CAP_FACE",FACE,{"disambiguationData":[OSD([subQ0])],"isStart":false})});Q0=makeQuery(id+"F21.boolean.opBoolean","MERGE",FACE,{"derivedFrom":[makeQuery(id+"F19.opPattern","COPY",FACE,{"derivedFrom":makeQuery(id+"F16.opPattern","COPY",FACE,{"derivedFrom":makeQuery(id+"F9.boolean.opBoolean","SPLIT",FACE,{"disambiguationData":[TD([makeQuery(id+"F5.boolean.opBoolean","COPY",FACE,{"derivedFrom":makeQuery(id+"F5.opExtrude","SWEPT_FACE",FACE,{"disambiguationData":[OSD([subQ0])]})})])],"derivedFrom":subQ1}),"instanceName":"1"}),"instanceName":"1"}),makeQuery(id+"F19.opPattern","COPY",FACE,{"derivedFrom":makeQuery(id+"F16.opPattern","COPY",FACE,{"derivedFrom":makeQuery(id+"F9.boolean.opBoolean","SPLIT",FACE,{"disambiguationData":[TD([makeQuery(id+"F9.opExtrude","SWEPT_FACE",FACE,{"disambiguationData":[OSD([sQuery(id+"F8.wireOp",EDGE,"E25")])]})])],"derivedFrom":subQ1}),"instanceName":"1"}),"instanceName":"1"}),makeQuery(id+"F19.opPattern","COPY",FACE,{"derivedFrom":makeQuery(id+"F16.opPattern","COPY",FACE,{"derivedFrom":makeQuery(id+"F9.boolean.opBoolean","SPLIT",FACE,{"disambiguationData":[TD([makeQuery(id+"F9.opExtrude","SWEPT_FACE",FACE,{"disambiguationData":[OSD([sQuery(id+"F8.wireOp",EDGE,"E32")])]})])],"derivedFrom":subQ1}),"instanceName":"1"}),"instanceName":"1"}),makeQuery(id+"F19.opPattern","COPY",FACE,{"derivedFrom":makeQuery(id+"F16.opPattern","COPY",FACE,{"derivedFrom":makeQuery(id+"F9.boolean.opBoolean","SPLIT",FACE,{"disambiguationData":[TD([makeQuery(id+"F9.opExtrude","SWEPT_FACE",FACE,{"disambiguationData":[OSD([sQuery(id+"F8.wireOp",EDGE,"E33.0")])]})])],"derivedFrom":subQ1}),"instanceName":"1"}),"instanceName":"1"}),makeQuery(id+"F19.opPattern","COPY",FACE,{"derivedFrom":makeQuery(id+"F16.opPattern","COPY",FACE,{"derivedFrom":makeQuery(id+"F9.boolean.opBoolean","SPLIT",FACE,{"disambiguationData":[TD([makeQuery(id+"F9.opExtrude","SWEPT_FACE",FACE,{"disambiguationData":[OSD([sQuery(id+"F8.wireOp",EDGE,"E37")])]})])],"derivedFrom":subQ1}),"instanceName":"1"}),"instanceName":"1"}),makeQuery(id+"F19.opPattern","COPY",FACE,{"derivedFrom":makeQuery(id+"F16.opPattern","COPY",FACE,{"derivedFrom":makeQuery(id+"F9.boolean.opBoolean","SPLIT",FACE,{"disambiguationData":[TD([makeQuery(id+"F9.opExtrude","SWEPT_FACE",FACE,{"disambiguationData":[OSD([sQuery(id+"F8.wireOp",EDGE,"E51.MirrorCS")])]})])],"derivedFrom":subQ1}),"instanceName":"1"}),"instanceName":"1"}),makeQuery(id+"F19.opPattern","COPY",FACE,{"derivedFrom":makeQuery(id+"F16.opPattern","COPY",FACE,{"derivedFrom":makeQuery(id+"F9.boolean.opBoolean","SPLIT",FACE,{"disambiguationData":[TD([makeQuery(id+"F9.opExtrude","SWEPT_FACE",FACE,{"disambiguationData":[OSD([sQuery(id+"F8.wireOp",EDGE,"E53.MirrorCS")])]})])],"derivedFrom":subQ1}),"instanceName":"1"}),"instanceName":"1"}),makeQuery(id+"F19.opPattern","COPY",FACE,{"derivedFrom":makeQuery(id+"F16.opPattern","COPY",FACE,{"derivedFrom":makeQuery(id+"F9.boolean.opBoolean","SPLIT",FACE,{"disambiguationData":[TD([makeQuery(id+"F9.opExtrude","SWEPT_FACE",FACE,{"disambiguationData":[OSD([sQuery(id+"F8.wireOp",EDGE,"E80")])]})])],"derivedFrom":subQ1}),"instanceName":"1"}),"instanceName":"1"}),makeQuery(id+"F19.opPattern","COPY",FACE,{"derivedFrom":makeQuery(id+"F16.opPattern","COPY",FACE,{"derivedFrom":makeQuery(id+"F9.boolean.opBoolean","SPLIT",FACE,{"disambiguationData":[TD([makeQuery(id+"F9.opExtrude","SWEPT_FACE",FACE,{"disambiguationData":[OSD([sQuery(id+"F8.wireOp",EDGE,"E83")])]})])],"derivedFrom":subQ1}),"instanceName":"1"}),"instanceName":"1"}),makeQuery(id+"F21.opExtrude","CAP_FACE",FACE,{"disambiguationData":[OSD([sQuery(id+"F20.wireOp",EDGE,"E307.0.0")])],"isStart":false})]});}
            var sketch = newSketch(context, id + "F49", { "sketchPlane" : qUnion([Q0])});
            skPoint(sketch, "E744.middle", {"position": v(50.8, 50.8) * mm});
            skLineSegment(sketch, "E745", {"start": v(50.8, 50.8) * mm, "end": v(50.8, 49.82) * mm});
            skLineSegment(sketch, "E746", {"start": v(50.8, 49.82) * mm, "end": v(50.8, 45.22) * mm});
            skPoint(sketch, "E747.orphan", {"position": v(50.8, 42.58) * mm});
            skLineSegment(sketch, "E748", {"start": v(45.25, 44.38) * mm, "end": v(56.35, 44.38) * mm});
            skLineSegment(sketch, "E749", {"start": v(50.8, 45.22) * mm, "end": v(50.8, 44.38) * mm});
            skLineSegment(sketch, "E750", {"start": v(48.5, 51.25) * mm, "end": v(45.25, 44.38) * mm});
            skLineSegment(sketch, "E751", {"start": v(53.1, 51.25) * mm, "end": v(56.35, 44.38) * mm});
            skLineSegment(sketch, "E752.top", {"start": v(48.5, 54.1) * mm, "end": v(53.1, 54.1) * mm});
            skLineSegment(sketch, "E752.left", {"start": v(48.5, 51.25) * mm, "end": v(48.5, 54.1) * mm});
            skLineSegment(sketch, "E752.right", {"start": v(53.1, 51.25) * mm, "end": v(53.1, 54.1) * mm});
            skLineSegment(sketch, "E753.bottom", {"start": v(47.78, 54.37) * mm, "end": v(53.82, 54.37) * mm});
            skLineSegment(sketch, "E753.top", {"start": v(47.78, 55.18) * mm, "end": v(53.82, 55.18) * mm});
            skLineSegment(sketch, "E753.left", {"start": v(47.78, 54.37) * mm, "end": v(47.78, 55.18) * mm});
            skLineSegment(sketch, "E753.right", {"start": v(53.82, 54.37) * mm, "end": v(53.82, 55.18) * mm});
            skLineSegment(sketch, "E754", {"start": v(50.8, 50.8) * mm, "end": v(50.8, 54.37) * mm});
            skSolve(sketch);
        }
        {
            var Q0;
            Q0 = qSketchRegion(id + "F49", true);
            var Q1;
            Q1=makeQuery(id+"F23.opExtrude","CAP_FACE",FACE,{"disambiguationData":[OSD([sQuery(id+"F22.wireOp",EDGE,"E311"),sQuery(id+"F22.wireOp",EDGE,"E312"),sQuery(id+"F22.wireOp",EDGE,"E313"),sQuery(id+"F22.wireOp",EDGE,"E314"),sQuery(id+"F22.wireOp",EDGE,"E315"),sQuery(id+"F22.wireOp",EDGE,"E316"),sQuery(id+"F22.wireOp",EDGE,"E317"),sQuery(id+"F22.wireOp",EDGE,"E318"),sQuery(id+"F22.wireOp",EDGE,"E319"),sQuery(id+"F22.wireOp",EDGE,"E320"),sQuery(id+"F22.wireOp",EDGE,"E328.trimOffspring"),sQuery(id+"F22.wireOp",EDGE,"E329.trimOffspring"),sQuery(id+"F22.wireOp",EDGE,"E330.trimOffspring"),sQuery(id+"F22.wireOp",EDGE,"E331"),sQuery(id+"F22.wireOp",EDGE,"E332.trimOffspring"),sQuery(id+"F22.wireOp",EDGE,"E333"),sQuery(id+"F22.wireOp",EDGE,"E334"),sQuery(id+"F22.wireOp",EDGE,"E335"),sQuery(id+"F22.wireOp",EDGE,"E336"),sQuery(id+"F22.wireOp",EDGE,"E337"),sQuery(id+"F22.wireOp",EDGE,"E348.trimOffspring")])],"isStart":false});
            extrude(context, id + "F50", {"entities" : qUnion([Q0]), "operationType" : NewBodyOperationType.ADD, "endBound" : BoundingType.UP_TO_SURFACE, "depth" : 25.4 * mm, "endBoundEntityFace" : qUnion([Q1]), "offsetDistance" : 25.4 * mm});
        }
        {
            var Q0;
            Q0=makeQuery(id+"F50.opExtrude","SWEPT_EDGE",EDGE,{"disambiguationData":[OSD([sQuery(id+"F49.wireOp",EDGE,"iLWqzsmg-zepa-Gpg1-nXND-mnUxTbBmFSW4"),sQuery(id+"F49.wireOp",EDGE,"S1MNSfih-TVQp-NaXl-chtE-904AVflmhuvJ")])]});
            var Q1;
            Q1=makeQuery(id+"F50.opExtrude","SWEPT_EDGE",EDGE,{"disambiguationData":[OSD([sQuery(id+"F49.wireOp",EDGE,"S1MNSfih-TVQp-NaXl-chtE-904AVflmhuvJ"),sQuery(id+"F49.wireOp",EDGE,"a3d734aa-b8b1-48fe-a1d4-cdd2bb729c6e0.MirrorCS")])]});
            var Q2;
            Q2=makeQuery(id+"F50.opExtrude","SWEPT_EDGE",EDGE,{"disambiguationData":[OSD([sQuery(id+"F49.wireOp",EDGE,"E748"),sQuery(id+"F49.wireOp",EDGE,"E750")])]});
            var Q3;
            Q3=makeQuery(id+"F50.opExtrude","SWEPT_EDGE",EDGE,{"disambiguationData":[OSD([sQuery(id+"F49.wireOp",EDGE,"E748"),sQuery(id+"F49.wireOp",EDGE,"E751")])]});
            fillet(context, id + "F51", {"entities" : qUnion([Q0, Q1, Q2, Q3]), "radius" : 1 * mm, "tangentPropagation" : true, "allowEdgeOverflow" : false});
        }
        {
            var Q0;
            {var subQ0=sQuery(id+"F4.wireOp",EDGE,"E8");var subQ1=makeQuery(id+"F5.boolean.opBoolean","COPY",FACE,{"derivedFrom":makeQuery(id+"F5.opExtrude","CAP_FACE",FACE,{"disambiguationData":[OSD([subQ0])],"isStart":false})});Q0=makeQuery(id+"F21.boolean.opBoolean","MERGE",FACE,{"derivedFrom":[makeQuery(id+"F19.opPattern","COPY",FACE,{"derivedFrom":makeQuery(id+"F16.opPattern","COPY",FACE,{"derivedFrom":makeQuery(id+"F9.boolean.opBoolean","SPLIT",FACE,{"disambiguationData":[TD([makeQuery(id+"F5.boolean.opBoolean","COPY",FACE,{"derivedFrom":makeQuery(id+"F5.opExtrude","SWEPT_FACE",FACE,{"disambiguationData":[OSD([subQ0])]})})])],"derivedFrom":subQ1}),"instanceName":"1"}),"instanceName":"1"}),makeQuery(id+"F19.opPattern","COPY",FACE,{"derivedFrom":makeQuery(id+"F16.opPattern","COPY",FACE,{"derivedFrom":makeQuery(id+"F9.boolean.opBoolean","SPLIT",FACE,{"disambiguationData":[TD([makeQuery(id+"F9.opExtrude","SWEPT_FACE",FACE,{"disambiguationData":[OSD([sQuery(id+"F8.wireOp",EDGE,"E25")])]})])],"derivedFrom":subQ1}),"instanceName":"1"}),"instanceName":"1"}),makeQuery(id+"F19.opPattern","COPY",FACE,{"derivedFrom":makeQuery(id+"F16.opPattern","COPY",FACE,{"derivedFrom":makeQuery(id+"F9.boolean.opBoolean","SPLIT",FACE,{"disambiguationData":[TD([makeQuery(id+"F9.opExtrude","SWEPT_FACE",FACE,{"disambiguationData":[OSD([sQuery(id+"F8.wireOp",EDGE,"E32")])]})])],"derivedFrom":subQ1}),"instanceName":"1"}),"instanceName":"1"}),makeQuery(id+"F19.opPattern","COPY",FACE,{"derivedFrom":makeQuery(id+"F16.opPattern","COPY",FACE,{"derivedFrom":makeQuery(id+"F9.boolean.opBoolean","SPLIT",FACE,{"disambiguationData":[TD([makeQuery(id+"F9.opExtrude","SWEPT_FACE",FACE,{"disambiguationData":[OSD([sQuery(id+"F8.wireOp",EDGE,"E33.0")])]})])],"derivedFrom":subQ1}),"instanceName":"1"}),"instanceName":"1"}),makeQuery(id+"F19.opPattern","COPY",FACE,{"derivedFrom":makeQuery(id+"F16.opPattern","COPY",FACE,{"derivedFrom":makeQuery(id+"F9.boolean.opBoolean","SPLIT",FACE,{"disambiguationData":[TD([makeQuery(id+"F9.opExtrude","SWEPT_FACE",FACE,{"disambiguationData":[OSD([sQuery(id+"F8.wireOp",EDGE,"E37")])]})])],"derivedFrom":subQ1}),"instanceName":"1"}),"instanceName":"1"}),makeQuery(id+"F19.opPattern","COPY",FACE,{"derivedFrom":makeQuery(id+"F16.opPattern","COPY",FACE,{"derivedFrom":makeQuery(id+"F9.boolean.opBoolean","SPLIT",FACE,{"disambiguationData":[TD([makeQuery(id+"F9.opExtrude","SWEPT_FACE",FACE,{"disambiguationData":[OSD([sQuery(id+"F8.wireOp",EDGE,"E51.MirrorCS")])]})])],"derivedFrom":subQ1}),"instanceName":"1"}),"instanceName":"1"}),makeQuery(id+"F19.opPattern","COPY",FACE,{"derivedFrom":makeQuery(id+"F16.opPattern","COPY",FACE,{"derivedFrom":makeQuery(id+"F9.boolean.opBoolean","SPLIT",FACE,{"disambiguationData":[TD([makeQuery(id+"F9.opExtrude","SWEPT_FACE",FACE,{"disambiguationData":[OSD([sQuery(id+"F8.wireOp",EDGE,"E53.MirrorCS")])]})])],"derivedFrom":subQ1}),"instanceName":"1"}),"instanceName":"1"}),makeQuery(id+"F19.opPattern","COPY",FACE,{"derivedFrom":makeQuery(id+"F16.opPattern","COPY",FACE,{"derivedFrom":makeQuery(id+"F9.boolean.opBoolean","SPLIT",FACE,{"disambiguationData":[TD([makeQuery(id+"F9.opExtrude","SWEPT_FACE",FACE,{"disambiguationData":[OSD([sQuery(id+"F8.wireOp",EDGE,"E80")])]})])],"derivedFrom":subQ1}),"instanceName":"1"}),"instanceName":"1"}),makeQuery(id+"F19.opPattern","COPY",FACE,{"derivedFrom":makeQuery(id+"F16.opPattern","COPY",FACE,{"derivedFrom":makeQuery(id+"F9.boolean.opBoolean","SPLIT",FACE,{"disambiguationData":[TD([makeQuery(id+"F9.opExtrude","SWEPT_FACE",FACE,{"disambiguationData":[OSD([sQuery(id+"F8.wireOp",EDGE,"E83")])]})])],"derivedFrom":subQ1}),"instanceName":"1"}),"instanceName":"1"}),makeQuery(id+"F21.opExtrude","CAP_FACE",FACE,{"disambiguationData":[OSD([sQuery(id+"F20.wireOp",EDGE,"E307.0.0")])],"isStart":false})]});}
            var sketch = newSketch(context, id + "F52", { "sketchPlane" : qUnion([Q0])});
            skLineSegment(sketch, "E755", {"start": v(46.74, 59.32) * mm, "end": v(47.5, 57.26) * mm});
            skLineSegment(sketch, "E756", {"start": v(47.5, 57.26) * mm, "end": v(48.75, 58.56) * mm});
            skLineSegment(sketch, "E757", {"start": v(48.75, 58.56) * mm, "end": v(49.33, 56.1) * mm});
            skLineSegment(sketch, "E758", {"start": v(49.33, 56.1) * mm, "end": v(49.33, 59.36) * mm});
            skLineSegment(sketch, "E759", {"start": v(49.33, 59.36) * mm, "end": v(47.76, 58.6) * mm});
            skLineSegment(sketch, "E760", {"start": v(47.76, 58.6) * mm, "end": v(47.35, 59.45) * mm});
            skLineSegment(sketch, "E761", {"start": v(47.35, 59.45) * mm, "end": v(46.74, 59.32) * mm});
            skLineSegment(sketch, "E762", {"start": v(51.52, 55.88) * mm, "end": v(50.54, 56.9) * mm});
            skLineSegment(sketch, "E763", {"start": v(50.54, 56.9) * mm, "end": v(51.79, 57.48) * mm});
            skLineSegment(sketch, "E764", {"start": v(51.79, 57.48) * mm, "end": v(50.22, 59.8) * mm});
            skLineSegment(sketch, "E765", {"start": v(50.22, 59.8) * mm, "end": v(51.2, 59.8) * mm});
            skLineSegment(sketch, "E766", {"start": v(51.2, 59.8) * mm, "end": v(52.6, 57.35) * mm});
            skLineSegment(sketch, "E767", {"start": v(52.6, 57.35) * mm, "end": v(53.82, 58.92) * mm});
            skLineSegment(sketch, "E768", {"start": v(53.82, 58.92) * mm, "end": v(54.47, 57.7) * mm});
            skLineSegment(sketch, "E769", {"start": v(54.47, 57.7) * mm, "end": v(52.51, 56.65) * mm});
            skLineSegment(sketch, "E770", {"start": v(52.51, 56.65) * mm, "end": v(51.43, 56.65) * mm});
            skLineSegment(sketch, "E771", {"start": v(51.43, 56.65) * mm, "end": v(51.52, 55.88) * mm});
            skLineSegment(sketch, "E772", {"start": v(52.94, 55.6) * mm, "end": v(53.5, 56.42) * mm});
            skLineSegment(sketch, "E773", {"start": v(53.5, 56.42) * mm, "end": v(54.46, 55.76) * mm});
            skLineSegment(sketch, "E774", {"start": v(54.46, 55.76) * mm, "end": v(55.45, 58.02) * mm});
            skLineSegment(sketch, "E775", {"start": v(55.45, 58.02) * mm, "end": v(55.94, 57.35) * mm});
            skLineSegment(sketch, "E776", {"start": v(55.94, 57.35) * mm, "end": v(54.66, 55.18) * mm});
            skLineSegment(sketch, "E777", {"start": v(54.66, 55.18) * mm, "end": v(53.48, 55.88) * mm});
            skLineSegment(sketch, "E778", {"start": v(53.48, 55.88) * mm, "end": v(52.94, 55.6) * mm});
            skSolve(sketch);
        }
        {
            var Q0;
            Q0 = qSketchRegion(id + "F52", true);
            var Q1;
            Q1=makeQuery(id+"F34.opExtrude","CAP_FACE",FACE,{"disambiguationData":[OSD([sQuery(id+"F33.wireOp",EDGE,"E523"),sQuery(id+"F33.wireOp",EDGE,"E524"),sQuery(id+"F33.wireOp",EDGE,"E525"),sQuery(id+"F33.wireOp",EDGE,"E526"),sQuery(id+"F33.wireOp",EDGE,"E527"),sQuery(id+"F33.wireOp",EDGE,"E528.trimOffspring"),sQuery(id+"F33.wireOp",EDGE,"E529.MirrorCS"),sQuery(id+"F33.wireOp",EDGE,"E530.MirrorCS"),sQuery(id+"F33.wireOp",EDGE,"E534.MirrorCS"),sQuery(id+"F33.wireOp",EDGE,"E535.MirrorCS"),sQuery(id+"F33.wireOp",EDGE,"E536.MirrorCS"),sQuery(id+"F33.wireOp",EDGE,"E537.MirrorCS"),sQuery(id+"F33.wireOp",EDGE,"E538.MirrorCS"),sQuery(id+"F33.wireOp",EDGE,"E539.MirrorCS"),sQuery(id+"F33.wireOp",EDGE,"E540.MirrorCS"),sQuery(id+"F33.wireOp",EDGE,"E541.MirrorCS"),sQuery(id+"F33.wireOp",EDGE,"E542.MirrorCS"),sQuery(id+"F33.wireOp",EDGE,"E543.MirrorCS"),sQuery(id+"F33.wireOp",EDGE,"E544.MirrorCS"),sQuery(id+"F33.wireOp",EDGE,"E545.MirrorCS"),sQuery(id+"F33.wireOp",EDGE,"E546.MirrorCS"),sQuery(id+"F33.wireOp",EDGE,"E547.MirrorCS"),sQuery(id+"F33.wireOp",EDGE,"E548.MirrorCS"),sQuery(id+"F33.wireOp",EDGE,"E549.MirrorCS"),sQuery(id+"F33.wireOp",EDGE,"E551.trimOffspring"),sQuery(id+"F33.wireOp",EDGE,"E552.trimOffspring"),sQuery(id+"F33.wireOp",EDGE,"E553.trimOffspring"),sQuery(id+"F33.wireOp",EDGE,"E554.trimOffspring"),sQuery(id+"F33.wireOp",EDGE,"E555.trimOffspring"),sQuery(id+"F33.wireOp",EDGE,"E556.trimOffspring"),sQuery(id+"F33.wireOp",EDGE,"E557.trimOffspring"),sQuery(id+"F33.wireOp",EDGE,"E558.trimOffspring"),sQuery(id+"F33.wireOp",EDGE,"E559.trimOffspring"),sQuery(id+"F33.wireOp",EDGE,"E560.trimOffspring"),sQuery(id+"F33.wireOp",EDGE,"E561.trimOffspring"),sQuery(id+"F33.wireOp",EDGE,"E562.trimOffspring"),sQuery(id+"F33.wireOp",EDGE,"E563.trimOffspring"),sQuery(id+"F33.wireOp",EDGE,"E564.trimOffspring"),sQuery(id+"F33.wireOp",EDGE,"E565.trimOffspring"),sQuery(id+"F33.wireOp",EDGE,"E566.trimOffspring"),sQuery(id+"F33.wireOp",EDGE,"E567.trimOffspring"),sQuery(id+"F33.wireOp",EDGE,"E568.trimOffspring"),sQuery(id+"F33.wireOp",EDGE,"E569.trimOffspring"),sQuery(id+"F33.wireOp",EDGE,"E570.trimOffspring"),sQuery(id+"F33.wireOp",EDGE,"E571.trimOffspring"),sQuery(id+"F33.wireOp",EDGE,"E572.trimOffspring"),sQuery(id+"F33.wireOp",EDGE,"E573.trimOffspring"),sQuery(id+"F33.wireOp",EDGE,"E574.trimOffspring"),sQuery(id+"F33.wireOp",EDGE,"E575.trimOffspring"),sQuery(id+"F33.wireOp",EDGE,"E576.trimOffspring"),sQuery(id+"F33.wireOp",EDGE,"E577.trimOffspring"),sQuery(id+"F33.wireOp",EDGE,"E578.trimOffspring"),sQuery(id+"F33.wireOp",EDGE,"E579.trimOffspring"),sQuery(id+"F33.wireOp",EDGE,"E580.trimOffspring"),sQuery(id+"F33.wireOp",EDGE,"E581.trimOffspring"),sQuery(id+"F33.wireOp",EDGE,"E582.trimOffspring"),sQuery(id+"F33.wireOp",EDGE,"E583.trimOffspring"),sQuery(id+"F33.wireOp",EDGE,"E584.trimOffspring"),sQuery(id+"F33.wireOp",EDGE,"E585.trimOffspring"),sQuery(id+"F33.wireOp",EDGE,"E586.trimOffspring"),sQuery(id+"F33.wireOp",EDGE,"E587.trimOffspring"),sQuery(id+"F33.wireOp",EDGE,"E588.trimOffspring"),sQuery(id+"F33.wireOp",EDGE,"E589.trimOffspring"),sQuery(id+"F33.wireOp",EDGE,"E590.trimOffspring"),sQuery(id+"F33.wireOp",EDGE,"E591.trimOffspring"),sQuery(id+"F33.wireOp",EDGE,"E592.trimOffspring"),sQuery(id+"F33.wireOp",EDGE,"E593.trimOffspring"),sQuery(id+"F33.wireOp",EDGE,"E594.trimOffspring"),sQuery(id+"F33.wireOp",EDGE,"E595.trimOffspring"),sQuery(id+"F33.wireOp",EDGE,"E596.trimOffspring"),sQuery(id+"F33.wireOp",EDGE,"E597.trimOffspring"),sQuery(id+"F33.wireOp",EDGE,"E598.trimOffspring")])],"isStart":false});
            extrude(context, id + "F53", {"entities" : qUnion([Q0]), "operationType" : NewBodyOperationType.ADD, "endBound" : BoundingType.UP_TO_SURFACE, "depth" : 25.4 * mm, "endBoundEntityFace" : qUnion([Q1]), "offsetDistance" : 25.4 * mm});
        }
        {
            var Q0;
            {var subQ0=sQuery(id+"F4.wireOp",EDGE,"E8");var subQ1=makeQuery(id+"F5.boolean.opBoolean","COPY",FACE,{"derivedFrom":makeQuery(id+"F5.opExtrude","CAP_FACE",FACE,{"disambiguationData":[OSD([subQ0])],"isStart":false})});Q0=makeQuery(id+"F21.boolean.opBoolean","MERGE",FACE,{"derivedFrom":[makeQuery(id+"F19.opPattern","COPY",FACE,{"derivedFrom":makeQuery(id+"F16.opPattern","COPY",FACE,{"derivedFrom":makeQuery(id+"F9.boolean.opBoolean","SPLIT",FACE,{"disambiguationData":[TD([makeQuery(id+"F5.boolean.opBoolean","COPY",FACE,{"derivedFrom":makeQuery(id+"F5.opExtrude","SWEPT_FACE",FACE,{"disambiguationData":[OSD([subQ0])]})})])],"derivedFrom":subQ1}),"instanceName":"1"}),"instanceName":"1"}),makeQuery(id+"F19.opPattern","COPY",FACE,{"derivedFrom":makeQuery(id+"F16.opPattern","COPY",FACE,{"derivedFrom":makeQuery(id+"F9.boolean.opBoolean","SPLIT",FACE,{"disambiguationData":[TD([makeQuery(id+"F9.opExtrude","SWEPT_FACE",FACE,{"disambiguationData":[OSD([sQuery(id+"F8.wireOp",EDGE,"E25")])]})])],"derivedFrom":subQ1}),"instanceName":"1"}),"instanceName":"1"}),makeQuery(id+"F19.opPattern","COPY",FACE,{"derivedFrom":makeQuery(id+"F16.opPattern","COPY",FACE,{"derivedFrom":makeQuery(id+"F9.boolean.opBoolean","SPLIT",FACE,{"disambiguationData":[TD([makeQuery(id+"F9.opExtrude","SWEPT_FACE",FACE,{"disambiguationData":[OSD([sQuery(id+"F8.wireOp",EDGE,"E32")])]})])],"derivedFrom":subQ1}),"instanceName":"1"}),"instanceName":"1"}),makeQuery(id+"F19.opPattern","COPY",FACE,{"derivedFrom":makeQuery(id+"F16.opPattern","COPY",FACE,{"derivedFrom":makeQuery(id+"F9.boolean.opBoolean","SPLIT",FACE,{"disambiguationData":[TD([makeQuery(id+"F9.opExtrude","SWEPT_FACE",FACE,{"disambiguationData":[OSD([sQuery(id+"F8.wireOp",EDGE,"E33.0")])]})])],"derivedFrom":subQ1}),"instanceName":"1"}),"instanceName":"1"}),makeQuery(id+"F19.opPattern","COPY",FACE,{"derivedFrom":makeQuery(id+"F16.opPattern","COPY",FACE,{"derivedFrom":makeQuery(id+"F9.boolean.opBoolean","SPLIT",FACE,{"disambiguationData":[TD([makeQuery(id+"F9.opExtrude","SWEPT_FACE",FACE,{"disambiguationData":[OSD([sQuery(id+"F8.wireOp",EDGE,"E37")])]})])],"derivedFrom":subQ1}),"instanceName":"1"}),"instanceName":"1"}),makeQuery(id+"F19.opPattern","COPY",FACE,{"derivedFrom":makeQuery(id+"F16.opPattern","COPY",FACE,{"derivedFrom":makeQuery(id+"F9.boolean.opBoolean","SPLIT",FACE,{"disambiguationData":[TD([makeQuery(id+"F9.opExtrude","SWEPT_FACE",FACE,{"disambiguationData":[OSD([sQuery(id+"F8.wireOp",EDGE,"E51.MirrorCS")])]})])],"derivedFrom":subQ1}),"instanceName":"1"}),"instanceName":"1"}),makeQuery(id+"F19.opPattern","COPY",FACE,{"derivedFrom":makeQuery(id+"F16.opPattern","COPY",FACE,{"derivedFrom":makeQuery(id+"F9.boolean.opBoolean","SPLIT",FACE,{"disambiguationData":[TD([makeQuery(id+"F9.opExtrude","SWEPT_FACE",FACE,{"disambiguationData":[OSD([sQuery(id+"F8.wireOp",EDGE,"E53.MirrorCS")])]})])],"derivedFrom":subQ1}),"instanceName":"1"}),"instanceName":"1"}),makeQuery(id+"F19.opPattern","COPY",FACE,{"derivedFrom":makeQuery(id+"F16.opPattern","COPY",FACE,{"derivedFrom":makeQuery(id+"F9.boolean.opBoolean","SPLIT",FACE,{"disambiguationData":[TD([makeQuery(id+"F9.opExtrude","SWEPT_FACE",FACE,{"disambiguationData":[OSD([sQuery(id+"F8.wireOp",EDGE,"E80")])]})])],"derivedFrom":subQ1}),"instanceName":"1"}),"instanceName":"1"}),makeQuery(id+"F19.opPattern","COPY",FACE,{"derivedFrom":makeQuery(id+"F16.opPattern","COPY",FACE,{"derivedFrom":makeQuery(id+"F9.boolean.opBoolean","SPLIT",FACE,{"disambiguationData":[TD([makeQuery(id+"F9.opExtrude","SWEPT_FACE",FACE,{"disambiguationData":[OSD([sQuery(id+"F8.wireOp",EDGE,"E83")])]})])],"derivedFrom":subQ1}),"instanceName":"1"}),"instanceName":"1"}),makeQuery(id+"F21.opExtrude","CAP_FACE",FACE,{"disambiguationData":[OSD([sQuery(id+"F20.wireOp",EDGE,"E307.0.0")])],"isStart":false})]});}
            var sketch = newSketch(context, id + "F54", { "sketchPlane" : qUnion([Q0])});
            skLineSegment(sketch, "E779", {"start": v(50.8, 44.38) * mm, "end": v(50.8, 45.14) * mm});
            skPoint(sketch, "E779.endSnap0", {"position": v(50.8, 44.38) * mm});
            skArc(sketch, "E780", {"start": v(48.65, 47.48) * mm, "mid": v(50, 45.3) * mm, "end": v(52.5, 45.96) * mm});
            skArc(sketch, "E781", {"start": v(49.4, 50.21) * mm, "mid": v(48.85, 48.9) * mm, "end": v(48.65, 47.48) * mm});
            skArc(sketch, "E782", {"start": v(49.4, 50.21) * mm, "mid": v(49.28, 49.24) * mm, "end": v(49.76, 48.39) * mm});
            skArc(sketch, "E783", {"start": v(49.76, 48.39) * mm, "mid": v(50.63, 49.66) * mm, "end": v(50.28, 51.15) * mm});
            skArc(sketch, "E784", {"start": v(50.62, 52.98) * mm, "mid": v(50.16, 52.12) * mm, "end": v(50.28, 51.15) * mm});
            skArc(sketch, "E785", {"start": v(50.62, 52.98) * mm, "mid": v(50.56, 51.55) * mm, "end": v(51.37, 50.38) * mm});
            skArc(sketch, "E786", {"start": v(51.82, 48.39) * mm, "mid": v(52.65, 48.3) * mm, "end": v(52.84, 49.1) * mm});
            skArc(sketch, "E787", {"start": v(52.5, 45.96) * mm, "mid": v(53.43, 47.45) * mm, "end": v(52.84, 49.1) * mm});
            skCircle(sketch, "E788", {"center": v(50.8, 47.02) * mm, "radius": 1.27 * mm});
            skArc(sketch, "E789.trimOffspring", {"start": v(51.82, 48.39) * mm, "mid": v(51.9, 49.45) * mm, "end": v(51.37, 50.38) * mm});
            skPoint(sketch, "E790.start.orphan", {"position": v(51.37, 47.7) * mm});
            skSolve(sketch);
        }
        {
            var Q0;
            Q0 = qSketchRegion(id + "F54", true);
            extrude(context, id + "F55", {"entities" : qUnion([Q0]), "operationType" : NewBodyOperationType.REMOVE, "depth" : 25.4 * mm, "offsetDistance" : 25.4 * mm});
        }
        {
            var Q0;
            {var subQ0=sQuery(id+"F49.wireOp",EDGE,"E751");var subQ1=sQuery(id+"F49.wireOp",EDGE,"E748");var subQ2=sQuery(id+"F49.wireOp",EDGE,"E750");var subQ3=sQuery(id+"F49.wireOp",EDGE,"E752.right");var subQ4=sQuery(id+"F49.wireOp",EDGE,"E752.left");var subQ5=sQuery(id+"F49.wireOp",EDGE,"E752.top");Q0=makeQuery(id+"F55.boolean.opBoolean","SPLIT",FACE,{"disambiguationData":[TD([makeQuery(id+"F50.opExtrude","SWEPT_FACE",FACE,{"disambiguationData":[OSD([subQ1])]})])],"derivedFrom":makeQuery(id+"F50.opExtrude","CAP_FACE",FACE,{"disambiguationData":[OSD([subQ1,subQ2,subQ0,subQ5,subQ4,subQ3])],"isStart":false})});}
            var sketch = newSketch(context, id + "F56", { "sketchPlane" : qUnion([Q0])});
            skLineSegment(sketch, "E791.0", {"start": v(49, 51.13) * mm, "end": v(46.04, 44.88) * mm});
            skLineSegment(sketch, "E791.1", {"start": v(55.56, 44.88) * mm, "end": v(52.6, 51.13) * mm});
            skLineSegment(sketch, "E791.2", {"start": v(52.6, 51.13) * mm, "end": v(52.6, 53.6) * mm});
            skLineSegment(sketch, "E791.3", {"start": v(46.04, 44.88) * mm, "end": v(55.56, 44.88) * mm});
            skLineSegment(sketch, "E791.4", {"start": v(52.6, 53.6) * mm, "end": v(49, 53.6) * mm});
            skLineSegment(sketch, "E791.5", {"start": v(49, 53.6) * mm, "end": v(49, 51.13) * mm});
            skSolve(sketch);
        }
        {
            var Q0;
            Q0 = qSketchRegion(id + "F56", true);
            var Q1;
            Q1=makeQuery(id+"F53.opExtrude","CAP_FACE",FACE,{"disambiguationData":[OSD([sQuery(id+"F52.wireOp",EDGE,"E762"),sQuery(id+"F52.wireOp",EDGE,"E763"),sQuery(id+"F52.wireOp",EDGE,"E764"),sQuery(id+"F52.wireOp",EDGE,"E765"),sQuery(id+"F52.wireOp",EDGE,"E766"),sQuery(id+"F52.wireOp",EDGE,"E767"),sQuery(id+"F52.wireOp",EDGE,"E768"),sQuery(id+"F52.wireOp",EDGE,"E769"),sQuery(id+"F52.wireOp",EDGE,"E770"),sQuery(id+"F52.wireOp",EDGE,"E771")])],"isStart":false});
            extrude(context, id + "F57", {"entities" : qUnion([Q0]), "operationType" : NewBodyOperationType.REMOVE, "endBound" : BoundingType.UP_TO_SURFACE, "oppositeDirection" : true, "depth" : 25.4 * mm, "endBoundEntityFace" : qUnion([Q1]), "offsetDistance" : 25.4 * mm});
        }
        {
            var Q0;
            Q0=makeQuery(id+"F57.boolean.opBoolean","COPY",EDGE,{"derivedFrom":makeQuery(id+"F57.opExtrude","SWEPT_EDGE",EDGE,{"disambiguationData":[OSD([sQuery(id+"F56.wireOp",EDGE,"E791.1"),sQuery(id+"F56.wireOp",EDGE,"E791.3")])]})});
            var Q1;
            Q1=makeQuery(id+"F57.boolean.opBoolean","COPY",EDGE,{"derivedFrom":makeQuery(id+"F57.opExtrude","SWEPT_EDGE",EDGE,{"disambiguationData":[OSD([sQuery(id+"F56.wireOp",EDGE,"E791.0"),sQuery(id+"F56.wireOp",EDGE,"E791.3")])]})});
            fillet(context, id + "F58", {"entities" : qUnion([Q0, Q1]), "radius" : 1 * mm, "tangentPropagation" : true, "allowEdgeOverflow" : false});
        }
        {
            var Q0;
            Q0=makeQuery(id+"F55.boolean.opBoolean","COPY",EDGE,{"derivedFrom":makeQuery(id+"F55.opExtrude","SWEPT_EDGE",EDGE,{"disambiguationData":[OSD([sQuery(id+"F54.wireOp",EDGE,"E782"),sQuery(id+"F54.wireOp",EDGE,"E783")])]})});
            var Q1;
            Q1=makeQuery(id+"F55.boolean.opBoolean","COPY",EDGE,{"derivedFrom":makeQuery(id+"F55.opExtrude","SWEPT_EDGE",EDGE,{"disambiguationData":[OSD([sQuery(id+"F54.wireOp",EDGE,"E786"),sQuery(id+"F54.wireOp",EDGE,"E789.trimOffspring")])]})});
            var Q2;
            Q2=makeQuery(id+"F55.boolean.opBoolean","COPY",EDGE,{"derivedFrom":makeQuery(id+"F55.opExtrude","SWEPT_EDGE",EDGE,{"disambiguationData":[OSD([sQuery(id+"F54.wireOp",EDGE,"E780"),sQuery(id+"F54.wireOp",EDGE,"E787")])]})});
            fillet(context, id + "F59", {"entities" : qUnion([Q0, Q1, Q2]), "radius" : 0.4 * mm, "tangentPropagation" : true, "allowEdgeOverflow" : false});
        }
        {
            var Q0;
            Q0=makeQuery(id+"F23.opExtrude","CAP_FACE",FACE,{"disambiguationData":[OSD([sQuery(id+"F22.wireOp",EDGE,"E311"),sQuery(id+"F22.wireOp",EDGE,"E312"),sQuery(id+"F22.wireOp",EDGE,"E313"),sQuery(id+"F22.wireOp",EDGE,"E314"),sQuery(id+"F22.wireOp",EDGE,"E315"),sQuery(id+"F22.wireOp",EDGE,"E316"),sQuery(id+"F22.wireOp",EDGE,"E317"),sQuery(id+"F22.wireOp",EDGE,"E318"),sQuery(id+"F22.wireOp",EDGE,"E319"),sQuery(id+"F22.wireOp",EDGE,"E320"),sQuery(id+"F22.wireOp",EDGE,"E328.trimOffspring"),sQuery(id+"F22.wireOp",EDGE,"E329.trimOffspring"),sQuery(id+"F22.wireOp",EDGE,"E330.trimOffspring"),sQuery(id+"F22.wireOp",EDGE,"E331"),sQuery(id+"F22.wireOp",EDGE,"E332.trimOffspring"),sQuery(id+"F22.wireOp",EDGE,"E333"),sQuery(id+"F22.wireOp",EDGE,"E334"),sQuery(id+"F22.wireOp",EDGE,"E335"),sQuery(id+"F22.wireOp",EDGE,"E336"),sQuery(id+"F22.wireOp",EDGE,"E337"),sQuery(id+"F22.wireOp",EDGE,"E348.trimOffspring")])],"isStart":false});
            var sketch = newSketch(context, id + "F60", { "sketchPlane" : qUnion([Q0])});
            skPoint(sketch, "E792.0", {"position": v(3.84, 9) * mm});
            skCircle(sketch, "E793.0", {"center": v(5.2, 5.53) * mm, "radius": 0.47 * mm});
            skArc(sketch, "E794.0.0", {"start": v(3, 8.37) * mm, "mid": v(3.04, 7.66) * mm, "end": v(3.68, 7.97) * mm});
            skArc(sketch, "E794.0.1", {"start": v(3.68, 7.97) * mm, "mid": v(3.84, 9) * mm, "end": v(3, 8.37) * mm});
            skCircle(sketch, "E795.0.0", {"center": v(7.33, 0.94) * mm, "radius": 0.4 * mm});
            skCircle(sketch, "E796.0.0", {"center": v(7.82, -2.33) * mm, "radius": 1 * mm});
            skCircle(sketch, "E797.0.0", {"center": v(4.06, -3.84) * mm, "radius": 0.58 * mm});
            skArc(sketch, "E798.0.0", {"start": v(5.85, -5) * mm, "mid": v(4.91, -4.92) * mm, "end": v(5.13, -5.84) * mm});
            skCircle(sketch, "E799.0.0", {"center": v(3.61, -6.8) * mm, "radius": 0.56 * mm});
            skCircle(sketch, "E800.0.0", {"center": v(-2.1, -7.9) * mm, "radius": 0.66 * mm});
            skCircle(sketch, "E801.0.0", {"center": v(-2.48, -6.92) * mm, "radius": 0.35 * mm});
            skCircle(sketch, "E802.0", {"center": v(-3.68, -8.24) * mm, "radius": 0.24 * mm});
            skCircle(sketch, "E803.0.0", {"center": v(-6.39, -5.42) * mm, "radius": 0.79 * mm});
            skArc(sketch, "E804.0.0", {"start": v(-7.44, -4.45) * mm, "mid": v(-6.9, -3.61) * mm, "end": v(-7.9, -3.53) * mm});
            skArc(sketch, "E804.0.1", {"start": v(-7.9, -3.53) * mm, "mid": v(-8.52, -4.4) * mm, "end": v(-7.44, -4.45) * mm});
            skCircle(sketch, "E805.0.0", {"center": v(-5.91, -3) * mm, "radius": 0.32 * mm});
            skArc(sketch, "E806.0.0", {"start": v(-7.62, -1.73) * mm, "mid": v(-6.86, -1.26) * mm, "end": v(-7.57, -0.73) * mm});
            skCircle(sketch, "E807.0.0", {"center": v(-7.67, 0.75) * mm, "radius": 0.4 * mm});
            skArc(sketch, "E808.0.0", {"start": v(-8.02, 2.94) * mm, "mid": v(-7.47, 2.88) * mm, "end": v(-7.6, 3.42) * mm});
            skArc(sketch, "E808.0.1", {"start": v(-7.6, 3.42) * mm, "mid": v(-8.51, 3.8) * mm, "end": v(-8.02, 2.94) * mm});
            skCircle(sketch, "E809.0.0", {"center": v(-6.05, 6.24) * mm, "radius": 0.31 * mm});
            skArc(sketch, "E810.0.0", {"start": v(-2.55, 7.49) * mm, "mid": v(-2.14, 7.16) * mm, "end": v(-1.94, 7.64) * mm});
            skArc(sketch, "E810.0.1", {"start": v(-1.94, 7.64) * mm, "mid": v(-2.51, 8.61) * mm, "end": v(-2.55, 7.49) * mm});
            skCircle(sketch, "E811.0.0", {"center": v(-0.71, 7.86) * mm, "radius": 0.32 * mm});
            skCircle(sketch, "E812.0.0", {"center": v(-2, 2.18) * mm, "radius": 0.61 * mm});
            skCircle(sketch, "E813.0.0", {"center": v(-2.94, 0.9) * mm, "radius": 0.61 * mm});
            skCircle(sketch, "E814.0.0", {"center": v(-3.07, -0.73) * mm, "radius": 0.61 * mm});
            skCircle(sketch, "E815.0.0", {"center": v(-2.2, -2.3) * mm, "radius": 0.61 * mm});
            skCircle(sketch, "E816.0.0", {"center": v(-0.44, -3.08) * mm, "radius": 0.61 * mm});
            skSolve(sketch);
        }
        {
            var Q0;
            Q0 = qSketchRegion(id + "F60", true);
            var Q1;
            Q1=makeQuery(id+"F34.opExtrude","CAP_FACE",FACE,{"disambiguationData":[OSD([sQuery(id+"F33.wireOp",EDGE,"E523"),sQuery(id+"F33.wireOp",EDGE,"E524"),sQuery(id+"F33.wireOp",EDGE,"E525"),sQuery(id+"F33.wireOp",EDGE,"E526"),sQuery(id+"F33.wireOp",EDGE,"E527"),sQuery(id+"F33.wireOp",EDGE,"E528.trimOffspring"),sQuery(id+"F33.wireOp",EDGE,"E529.MirrorCS"),sQuery(id+"F33.wireOp",EDGE,"E530.MirrorCS"),sQuery(id+"F33.wireOp",EDGE,"E534.MirrorCS"),sQuery(id+"F33.wireOp",EDGE,"E535.MirrorCS"),sQuery(id+"F33.wireOp",EDGE,"E536.MirrorCS"),sQuery(id+"F33.wireOp",EDGE,"E537.MirrorCS"),sQuery(id+"F33.wireOp",EDGE,"E538.MirrorCS"),sQuery(id+"F33.wireOp",EDGE,"E539.MirrorCS"),sQuery(id+"F33.wireOp",EDGE,"E540.MirrorCS"),sQuery(id+"F33.wireOp",EDGE,"E541.MirrorCS"),sQuery(id+"F33.wireOp",EDGE,"E542.MirrorCS"),sQuery(id+"F33.wireOp",EDGE,"E543.MirrorCS"),sQuery(id+"F33.wireOp",EDGE,"E544.MirrorCS"),sQuery(id+"F33.wireOp",EDGE,"E545.MirrorCS"),sQuery(id+"F33.wireOp",EDGE,"E546.MirrorCS"),sQuery(id+"F33.wireOp",EDGE,"E547.MirrorCS"),sQuery(id+"F33.wireOp",EDGE,"E548.MirrorCS"),sQuery(id+"F33.wireOp",EDGE,"E549.MirrorCS"),sQuery(id+"F33.wireOp",EDGE,"E551.trimOffspring"),sQuery(id+"F33.wireOp",EDGE,"E552.trimOffspring"),sQuery(id+"F33.wireOp",EDGE,"E553.trimOffspring"),sQuery(id+"F33.wireOp",EDGE,"E554.trimOffspring"),sQuery(id+"F33.wireOp",EDGE,"E555.trimOffspring"),sQuery(id+"F33.wireOp",EDGE,"E556.trimOffspring"),sQuery(id+"F33.wireOp",EDGE,"E557.trimOffspring"),sQuery(id+"F33.wireOp",EDGE,"E558.trimOffspring"),sQuery(id+"F33.wireOp",EDGE,"E559.trimOffspring"),sQuery(id+"F33.wireOp",EDGE,"E560.trimOffspring"),sQuery(id+"F33.wireOp",EDGE,"E561.trimOffspring"),sQuery(id+"F33.wireOp",EDGE,"E562.trimOffspring"),sQuery(id+"F33.wireOp",EDGE,"E563.trimOffspring"),sQuery(id+"F33.wireOp",EDGE,"E564.trimOffspring"),sQuery(id+"F33.wireOp",EDGE,"E565.trimOffspring"),sQuery(id+"F33.wireOp",EDGE,"E566.trimOffspring"),sQuery(id+"F33.wireOp",EDGE,"E567.trimOffspring"),sQuery(id+"F33.wireOp",EDGE,"E568.trimOffspring"),sQuery(id+"F33.wireOp",EDGE,"E569.trimOffspring"),sQuery(id+"F33.wireOp",EDGE,"E570.trimOffspring"),sQuery(id+"F33.wireOp",EDGE,"E571.trimOffspring"),sQuery(id+"F33.wireOp",EDGE,"E572.trimOffspring"),sQuery(id+"F33.wireOp",EDGE,"E573.trimOffspring"),sQuery(id+"F33.wireOp",EDGE,"E574.trimOffspring"),sQuery(id+"F33.wireOp",EDGE,"E575.trimOffspring"),sQuery(id+"F33.wireOp",EDGE,"E576.trimOffspring"),sQuery(id+"F33.wireOp",EDGE,"E577.trimOffspring"),sQuery(id+"F33.wireOp",EDGE,"E578.trimOffspring"),sQuery(id+"F33.wireOp",EDGE,"E579.trimOffspring"),sQuery(id+"F33.wireOp",EDGE,"E580.trimOffspring"),sQuery(id+"F33.wireOp",EDGE,"E581.trimOffspring"),sQuery(id+"F33.wireOp",EDGE,"E582.trimOffspring"),sQuery(id+"F33.wireOp",EDGE,"E583.trimOffspring"),sQuery(id+"F33.wireOp",EDGE,"E584.trimOffspring"),sQuery(id+"F33.wireOp",EDGE,"E585.trimOffspring"),sQuery(id+"F33.wireOp",EDGE,"E586.trimOffspring"),sQuery(id+"F33.wireOp",EDGE,"E587.trimOffspring"),sQuery(id+"F33.wireOp",EDGE,"E588.trimOffspring"),sQuery(id+"F33.wireOp",EDGE,"E589.trimOffspring"),sQuery(id+"F33.wireOp",EDGE,"E590.trimOffspring"),sQuery(id+"F33.wireOp",EDGE,"E591.trimOffspring"),sQuery(id+"F33.wireOp",EDGE,"E592.trimOffspring"),sQuery(id+"F33.wireOp",EDGE,"E593.trimOffspring"),sQuery(id+"F33.wireOp",EDGE,"E594.trimOffspring"),sQuery(id+"F33.wireOp",EDGE,"E595.trimOffspring"),sQuery(id+"F33.wireOp",EDGE,"E596.trimOffspring"),sQuery(id+"F33.wireOp",EDGE,"E597.trimOffspring"),sQuery(id+"F33.wireOp",EDGE,"E598.trimOffspring")])],"isStart":false});
            extrude(context, id + "F61", {"entities" : qUnion([Q0]), "operationType" : NewBodyOperationType.REMOVE, "endBound" : BoundingType.UP_TO_SURFACE, "oppositeDirection" : true, "depth" : 25.4 * mm, "endBoundEntityFace" : qUnion([Q1]), "offsetDistance" : 25.4 * mm});
        }
        {
            var Q0;
            {var subQ0=sQuery(id+"F4.wireOp",EDGE,"E8");var subQ1=makeQuery(id+"F5.boolean.opBoolean","COPY",FACE,{"derivedFrom":makeQuery(id+"F5.opExtrude","CAP_FACE",FACE,{"disambiguationData":[OSD([subQ0])],"isStart":false})});Q0=makeQuery(id+"F40.opPattern","COPY",FACE,{"derivedFrom":makeQuery(id+"F39.opPattern","COPY",FACE,{"derivedFrom":makeQuery(id+"F21.boolean.opBoolean","MERGE",FACE,{"derivedFrom":[makeQuery(id+"F19.opPattern","COPY",FACE,{"derivedFrom":makeQuery(id+"F16.opPattern","COPY",FACE,{"derivedFrom":makeQuery(id+"F9.boolean.opBoolean","SPLIT",FACE,{"disambiguationData":[TD([makeQuery(id+"F5.boolean.opBoolean","COPY",FACE,{"derivedFrom":makeQuery(id+"F5.opExtrude","SWEPT_FACE",FACE,{"disambiguationData":[OSD([subQ0])]})})])],"derivedFrom":subQ1}),"instanceName":"1"}),"instanceName":"1"}),makeQuery(id+"F19.opPattern","COPY",FACE,{"derivedFrom":makeQuery(id+"F16.opPattern","COPY",FACE,{"derivedFrom":makeQuery(id+"F9.boolean.opBoolean","SPLIT",FACE,{"disambiguationData":[TD([makeQuery(id+"F9.opExtrude","SWEPT_FACE",FACE,{"disambiguationData":[OSD([sQuery(id+"F8.wireOp",EDGE,"E25")])]})])],"derivedFrom":subQ1}),"instanceName":"1"}),"instanceName":"1"}),makeQuery(id+"F19.opPattern","COPY",FACE,{"derivedFrom":makeQuery(id+"F16.opPattern","COPY",FACE,{"derivedFrom":makeQuery(id+"F9.boolean.opBoolean","SPLIT",FACE,{"disambiguationData":[TD([makeQuery(id+"F9.opExtrude","SWEPT_FACE",FACE,{"disambiguationData":[OSD([sQuery(id+"F8.wireOp",EDGE,"E32")])]})])],"derivedFrom":subQ1}),"instanceName":"1"}),"instanceName":"1"}),makeQuery(id+"F19.opPattern","COPY",FACE,{"derivedFrom":makeQuery(id+"F16.opPattern","COPY",FACE,{"derivedFrom":makeQuery(id+"F9.boolean.opBoolean","SPLIT",FACE,{"disambiguationData":[TD([makeQuery(id+"F9.opExtrude","SWEPT_FACE",FACE,{"disambiguationData":[OSD([sQuery(id+"F8.wireOp",EDGE,"E33.0")])]})])],"derivedFrom":subQ1}),"instanceName":"1"}),"instanceName":"1"}),makeQuery(id+"F19.opPattern","COPY",FACE,{"derivedFrom":makeQuery(id+"F16.opPattern","COPY",FACE,{"derivedFrom":makeQuery(id+"F9.boolean.opBoolean","SPLIT",FACE,{"disambiguationData":[TD([makeQuery(id+"F9.opExtrude","SWEPT_FACE",FACE,{"disambiguationData":[OSD([sQuery(id+"F8.wireOp",EDGE,"E37")])]})])],"derivedFrom":subQ1}),"instanceName":"1"}),"instanceName":"1"}),makeQuery(id+"F19.opPattern","COPY",FACE,{"derivedFrom":makeQuery(id+"F16.opPattern","COPY",FACE,{"derivedFrom":makeQuery(id+"F9.boolean.opBoolean","SPLIT",FACE,{"disambiguationData":[TD([makeQuery(id+"F9.opExtrude","SWEPT_FACE",FACE,{"disambiguationData":[OSD([sQuery(id+"F8.wireOp",EDGE,"E51.MirrorCS")])]})])],"derivedFrom":subQ1}),"instanceName":"1"}),"instanceName":"1"}),makeQuery(id+"F19.opPattern","COPY",FACE,{"derivedFrom":makeQuery(id+"F16.opPattern","COPY",FACE,{"derivedFrom":makeQuery(id+"F9.boolean.opBoolean","SPLIT",FACE,{"disambiguationData":[TD([makeQuery(id+"F9.opExtrude","SWEPT_FACE",FACE,{"disambiguationData":[OSD([sQuery(id+"F8.wireOp",EDGE,"E53.MirrorCS")])]})])],"derivedFrom":subQ1}),"instanceName":"1"}),"instanceName":"1"}),makeQuery(id+"F19.opPattern","COPY",FACE,{"derivedFrom":makeQuery(id+"F16.opPattern","COPY",FACE,{"derivedFrom":makeQuery(id+"F9.boolean.opBoolean","SPLIT",FACE,{"disambiguationData":[TD([makeQuery(id+"F9.opExtrude","SWEPT_FACE",FACE,{"disambiguationData":[OSD([sQuery(id+"F8.wireOp",EDGE,"E80")])]})])],"derivedFrom":subQ1}),"instanceName":"1"}),"instanceName":"1"}),makeQuery(id+"F19.opPattern","COPY",FACE,{"derivedFrom":makeQuery(id+"F16.opPattern","COPY",FACE,{"derivedFrom":makeQuery(id+"F9.boolean.opBoolean","SPLIT",FACE,{"disambiguationData":[TD([makeQuery(id+"F9.opExtrude","SWEPT_FACE",FACE,{"disambiguationData":[OSD([sQuery(id+"F8.wireOp",EDGE,"E83")])]})])],"derivedFrom":subQ1}),"instanceName":"1"}),"instanceName":"1"}),makeQuery(id+"F21.opExtrude","CAP_FACE",FACE,{"disambiguationData":[OSD([sQuery(id+"F20.wireOp",EDGE,"E307.0.0")])],"isStart":false})]}),"instanceName":"1"}),"instanceName":"1"});}
            var sketch = newSketch(context, id + "F62", { "sketchPlane" : qUnion([Q0])});
            skPoint(sketch, "E817.0", {"position": v(-101.6, -38.1) * mm});
            skLineSegment(sketch, "E818", {"start": v(-101.6, -38.1) * mm, "end": v(-101.6, -46.35) * mm});
            skArc(sketch, "E819", {"start": v(-99.34, -49.75) * mm, "mid": v(-101.6, -42.27) * mm, "end": v(-103.86, -49.75) * mm});
            skLineSegment(sketch, "E820.MirrorCS", {"start": v(-99.34, -49.75) * mm, "end": v(-98.94, -51.1) * mm});
            skLineSegment(sketch, "E821", {"start": v(-102.23, -51.89) * mm, "end": v(-102.13, -50.98) * mm});
            skLineSegment(sketch, "E822", {"start": v(-102.13, -50.98) * mm, "end": v(-102.4, -51.86) * mm});
            skLineSegment(sketch, "E823", {"start": v(-103.14, -50.84) * mm, "end": v(-103.51, -51.52) * mm});
            skLineSegment(sketch, "E824.MirrorCS", {"start": v(-100.97, -51.89) * mm, "end": v(-101.07, -50.98) * mm});
            skLineSegment(sketch, "E825.MirrorCS", {"start": v(-101.07, -50.98) * mm, "end": v(-100.8, -51.86) * mm});
            skLineSegment(sketch, "E826.MirrorCS", {"start": v(-99.83, -51.58) * mm, "end": v(-100.06, -50.84) * mm});
            skLineSegment(sketch, "E827.MirrorCS", {"start": v(-100.06, -50.84) * mm, "end": v(-99.69, -51.52) * mm});
            skLineSegment(sketch, "E828", {"start": v(-101.6, -49.03) * mm, "end": v(-102.11, -48.67) * mm});
            skLineSegment(sketch, "E829", {"start": v(-102.11, -48.67) * mm, "end": v(-102.11, -49.63) * mm});
            skLineSegment(sketch, "E830", {"start": v(-102.11, -49.63) * mm, "end": v(-101.6, -49.63) * mm});
            skLineSegment(sketch, "E831.MirrorCS", {"start": v(-101.6, -49.03) * mm, "end": v(-101.09, -48.67) * mm});
            skLineSegment(sketch, "E832.MirrorCS", {"start": v(-101.09, -48.67) * mm, "end": v(-101.09, -49.63) * mm});
            skLineSegment(sketch, "E833.MirrorCS", {"start": v(-101.09, -49.63) * mm, "end": v(-101.6, -49.63) * mm});
            skLineSegment(sketch, "E834", {"start": v(-104.66, -47.24) * mm, "end": v(-103.3, -48.25) * mm});
            skLineSegment(sketch, "E835", {"start": v(-102.31, -47.24) * mm, "end": v(-103.34, -45.54) * mm});
            skArc(sketch, "E836", {"start": v(-103.34, -45.54) * mm, "mid": v(-104.87, -45.72) * mm, "end": v(-104.66, -47.24) * mm});
            skArc(sketch, "E837", {"start": v(-103.3, -48.25) * mm, "mid": v(-102.41, -48.13) * mm, "end": v(-102.31, -47.24) * mm});
            skLineSegment(sketch, "E838.MirrorCS", {"start": v(-100.89, -47.24) * mm, "end": v(-99.86, -45.54) * mm});
            skArc(sketch, "E839.MirrorCS", {"start": v(-99.86, -45.54) * mm, "mid": v(-98.33, -45.72) * mm, "end": v(-98.54, -47.24) * mm});
            skLineSegment(sketch, "E840.MirrorCS", {"start": v(-98.54, -47.24) * mm, "end": v(-99.9, -48.25) * mm});
            skArc(sketch, "E841.MirrorCS", {"start": v(-99.9, -48.25) * mm, "mid": v(-100.79, -48.13) * mm, "end": v(-100.89, -47.24) * mm});
            skCircle(sketch, "E842", {"center": v(-101.6, -56.85) * mm, "radius": 0.73 * mm});
            skCircle(sketch, "E843", {"center": v(-101.6, -56.85) * mm, "radius": 1.53 * mm});
            skLineSegment(sketch, "E844", {"start": v(-109.5, -49.9) * mm, "end": v(-99, -59.14) * mm});
            skArc(sketch, "E845.MirrorCS", {"start": v(-109.5, -49.9) * mm, "mid": v(-108.33, -50.06) * mm, "end": v(-107.19, -50.36) * mm});
            skArc(sketch, "E846", {"start": v(-104.26, -51.1) * mm, "mid": v(-104, -51.26) * mm, "end": v(-103.75, -51.4) * mm});
            skLineSegment(sketch, "E847.trimOffspring", {"start": v(-103.37, -51.58) * mm, "end": v(-103.14, -50.84) * mm});
            skPoint(sketch, "E848.trimOffspring.end.orphan", {"position": v(-104.66, -52.45) * mm});
            skPoint(sketch, "E849.trimOffspring.end.orphan", {"position": v(-104.15, -52.68) * mm});
            skPoint(sketch, "E850.orphan", {"position": v(-103.74, -52.83) * mm});
            skPoint(sketch, "E851.trimOffspring.end.orphan", {"position": v(-100.85, -53.13) * mm});
            skPoint(sketch, "E851.trimOffspring.start.orphan", {"position": v(-102.35, -53.13) * mm});
            skPoint(sketch, "E852.trimOffspring.end.orphan", {"position": v(-99.46, -52.83) * mm});
            skPoint(sketch, "E852.trimOffspring.start.orphan", {"position": v(-100.43, -53.07) * mm});
            skPoint(sketch, "E853.trimOffspring.end.orphan", {"position": v(-98.54, -52.45) * mm});
            skPoint(sketch, "E853.trimOffspring.start.orphan", {"position": v(-99.05, -52.68) * mm});
            skPoint(sketch, "E854.trimOffspring.end.orphan", {"position": v(-102.77, -53.07) * mm});
            skLineSegment(sketch, "E855", {"start": v(-103.86, -49.75) * mm, "end": v(-104.26, -51.1) * mm});
            skArc(sketch, "E856.trimOffspring", {"start": v(-103.37, -51.58) * mm, "mid": v(-103.03, -51.7) * mm, "end": v(-102.7, -51.8) * mm});
            skArc(sketch, "E857.trimOffspring", {"start": v(-102.23, -51.89) * mm, "mid": v(-101.6, -51.93) * mm, "end": v(-100.97, -51.89) * mm});
            skArc(sketch, "E858.trimOffspring", {"start": v(-100.5, -51.8) * mm, "mid": v(-100.17, -51.7) * mm, "end": v(-99.83, -51.58) * mm});
            skArc(sketch, "E859.trimOffspring", {"start": v(-99.45, -51.4) * mm, "mid": v(-99.2, -51.26) * mm, "end": v(-98.94, -51.1) * mm});
            skLineSegment(sketch, "E860", {"start": v(-102.23, -51.89) * mm, "end": v(-102.05, -50.17) * mm});
            skLineSegment(sketch, "E861", {"start": v(-102.05, -50.17) * mm, "end": v(-102.7, -51.8) * mm});
            skLineSegment(sketch, "E862", {"start": v(-103.37, -51.58) * mm, "end": v(-102.94, -50.17) * mm});
            skLineSegment(sketch, "E863", {"start": v(-102.94, -50.17) * mm, "end": v(-103.75, -51.4) * mm});
            skLineSegment(sketch, "E864.MirrorCS", {"start": v(-100.97, -51.89) * mm, "end": v(-101.15, -50.17) * mm});
            skLineSegment(sketch, "E865.MirrorCS", {"start": v(-101.15, -50.17) * mm, "end": v(-100.5, -51.8) * mm});
            skLineSegment(sketch, "E866.MirrorCS", {"start": v(-99.83, -51.58) * mm, "end": v(-100.26, -50.17) * mm});
            skLineSegment(sketch, "E867.MirrorCS", {"start": v(-100.26, -50.17) * mm, "end": v(-99.45, -51.4) * mm});
            skArc(sketch, "E868.MirrorCS", {"start": v(-109.5, -49.9) * mm, "mid": v(-109.2, -51.04) * mm, "end": v(-108.75, -52.14) * mm});
            skCircle(sketch, "E869", {"center": v(-99, -59.14) * mm, "radius": 0.8 * mm});
            skArc(sketch, "E870", {"start": v(-100.94, -58.23) * mm, "mid": v(-100.48, -58.82) * mm, "end": v(-99.8, -59.14) * mm});
            skArc(sketch, "E871.MirrorCS", {"start": v(-100.14, -57.33) * mm, "mid": v(-99.5, -57.71) * mm, "end": v(-99.1, -58.34) * mm});
            skArc(sketch, "E872.MirrorCS", {"start": v(-103.06, -57.33) * mm, "mid": v(-103.7, -57.71) * mm, "end": v(-104.1, -58.34) * mm});
            skArc(sketch, "E873", {"start": v(-107.19, -50.36) * mm, "mid": v(-104.74, -53.27) * mm, "end": v(-101.54, -55.32) * mm});
            skArc(sketch, "E874", {"start": v(-108.75, -52.14) * mm, "mid": v(-106.32, -55.06) * mm, "end": v(-103.11, -57.1) * mm});
            skSolve(sketch);
        }
        {
            var Q0;
            Q0 = qSketchRegion(id + "F62", true);
            var Q1;
            Q1=makeQuery(id+"F23.opExtrude","CAP_FACE",FACE,{"disambiguationData":[OSD([sQuery(id+"F22.wireOp",EDGE,"E311"),sQuery(id+"F22.wireOp",EDGE,"E312"),sQuery(id+"F22.wireOp",EDGE,"E313"),sQuery(id+"F22.wireOp",EDGE,"E314"),sQuery(id+"F22.wireOp",EDGE,"E315"),sQuery(id+"F22.wireOp",EDGE,"E316"),sQuery(id+"F22.wireOp",EDGE,"E317"),sQuery(id+"F22.wireOp",EDGE,"E318"),sQuery(id+"F22.wireOp",EDGE,"E319"),sQuery(id+"F22.wireOp",EDGE,"E320"),sQuery(id+"F22.wireOp",EDGE,"E328.trimOffspring"),sQuery(id+"F22.wireOp",EDGE,"E329.trimOffspring"),sQuery(id+"F22.wireOp",EDGE,"E330.trimOffspring"),sQuery(id+"F22.wireOp",EDGE,"E331"),sQuery(id+"F22.wireOp",EDGE,"E332.trimOffspring"),sQuery(id+"F22.wireOp",EDGE,"E333"),sQuery(id+"F22.wireOp",EDGE,"E334"),sQuery(id+"F22.wireOp",EDGE,"E335"),sQuery(id+"F22.wireOp",EDGE,"E336"),sQuery(id+"F22.wireOp",EDGE,"E337"),sQuery(id+"F22.wireOp",EDGE,"E348.trimOffspring")])],"isStart":false});
            extrude(context, id + "F63", {"entities" : qUnion([Q0]), "operationType" : NewBodyOperationType.ADD, "endBound" : BoundingType.UP_TO_SURFACE, "depth" : 25.4 * mm, "endBoundEntityFace" : qUnion([Q1]), "offsetDistance" : 25.4 * mm});
        }
        {
            var Q0;
            {var subQ4=sQuery(id+"F4.wireOp",EDGE,"E8");var subQ5=makeQuery(id+"F5.boolean.opBoolean","COPY",FACE,{"derivedFrom":makeQuery(id+"F5.opExtrude","SWEPT_FACE",FACE,{"disambiguationData":[OSD([subQ4])]})});var subQ8=makeQuery(id+"F5.boolean.opBoolean","COPY",FACE,{"derivedFrom":makeQuery(id+"F5.opExtrude","CAP_FACE",FACE,{"disambiguationData":[OSD([subQ4])],"isStart":false})});Q0=makeQuery(id+"F63.boolean.opBoolean","SPLIT",FACE,{"disambiguationData":[TD([makeQuery(id+"F40.opPattern","COPY",FACE,{"derivedFrom":makeQuery(id+"F39.opPattern","COPY",FACE,{"derivedFrom":makeQuery(id+"F19.opPattern","COPY",FACE,{"derivedFrom":makeQuery(id+"F16.opPattern","COPY",FACE,{"derivedFrom":subQ5,"instanceName":"1"}),"instanceName":"1"}),"instanceName":"1"}),"instanceName":"1"})])],"derivedFrom":makeQuery(id+"F40.opPattern","COPY",FACE,{"derivedFrom":makeQuery(id+"F39.opPattern","COPY",FACE,{"derivedFrom":makeQuery(id+"F21.boolean.opBoolean","MERGE",FACE,{"derivedFrom":[makeQuery(id+"F19.opPattern","COPY",FACE,{"derivedFrom":makeQuery(id+"F16.opPattern","COPY",FACE,{"derivedFrom":makeQuery(id+"F9.boolean.opBoolean","SPLIT",FACE,{"disambiguationData":[TD([subQ5])],"derivedFrom":subQ8}),"instanceName":"1"}),"instanceName":"1"}),makeQuery(id+"F19.opPattern","COPY",FACE,{"derivedFrom":makeQuery(id+"F16.opPattern","COPY",FACE,{"derivedFrom":makeQuery(id+"F9.boolean.opBoolean","SPLIT",FACE,{"disambiguationData":[TD([makeQuery(id+"F9.opExtrude","SWEPT_FACE",FACE,{"disambiguationData":[OSD([sQuery(id+"F8.wireOp",EDGE,"E25")])]})])],"derivedFrom":subQ8}),"instanceName":"1"}),"instanceName":"1"}),makeQuery(id+"F19.opPattern","COPY",FACE,{"derivedFrom":makeQuery(id+"F16.opPattern","COPY",FACE,{"derivedFrom":makeQuery(id+"F9.boolean.opBoolean","SPLIT",FACE,{"disambiguationData":[TD([makeQuery(id+"F9.opExtrude","SWEPT_FACE",FACE,{"disambiguationData":[OSD([sQuery(id+"F8.wireOp",EDGE,"E32")])]})])],"derivedFrom":subQ8}),"instanceName":"1"}),"instanceName":"1"}),makeQuery(id+"F19.opPattern","COPY",FACE,{"derivedFrom":makeQuery(id+"F16.opPattern","COPY",FACE,{"derivedFrom":makeQuery(id+"F9.boolean.opBoolean","SPLIT",FACE,{"disambiguationData":[TD([makeQuery(id+"F9.opExtrude","SWEPT_FACE",FACE,{"disambiguationData":[OSD([sQuery(id+"F8.wireOp",EDGE,"E33.0")])]})])],"derivedFrom":subQ8}),"instanceName":"1"}),"instanceName":"1"}),makeQuery(id+"F19.opPattern","COPY",FACE,{"derivedFrom":makeQuery(id+"F16.opPattern","COPY",FACE,{"derivedFrom":makeQuery(id+"F9.boolean.opBoolean","SPLIT",FACE,{"disambiguationData":[TD([makeQuery(id+"F9.opExtrude","SWEPT_FACE",FACE,{"disambiguationData":[OSD([sQuery(id+"F8.wireOp",EDGE,"E37")])]})])],"derivedFrom":subQ8}),"instanceName":"1"}),"instanceName":"1"}),makeQuery(id+"F19.opPattern","COPY",FACE,{"derivedFrom":makeQuery(id+"F16.opPattern","COPY",FACE,{"derivedFrom":makeQuery(id+"F9.boolean.opBoolean","SPLIT",FACE,{"disambiguationData":[TD([makeQuery(id+"F9.opExtrude","SWEPT_FACE",FACE,{"disambiguationData":[OSD([sQuery(id+"F8.wireOp",EDGE,"E51.MirrorCS")])]})])],"derivedFrom":subQ8}),"instanceName":"1"}),"instanceName":"1"}),makeQuery(id+"F19.opPattern","COPY",FACE,{"derivedFrom":makeQuery(id+"F16.opPattern","COPY",FACE,{"derivedFrom":makeQuery(id+"F9.boolean.opBoolean","SPLIT",FACE,{"disambiguationData":[TD([makeQuery(id+"F9.opExtrude","SWEPT_FACE",FACE,{"disambiguationData":[OSD([sQuery(id+"F8.wireOp",EDGE,"E53.MirrorCS")])]})])],"derivedFrom":subQ8}),"instanceName":"1"}),"instanceName":"1"}),makeQuery(id+"F19.opPattern","COPY",FACE,{"derivedFrom":makeQuery(id+"F16.opPattern","COPY",FACE,{"derivedFrom":makeQuery(id+"F9.boolean.opBoolean","SPLIT",FACE,{"disambiguationData":[TD([makeQuery(id+"F9.opExtrude","SWEPT_FACE",FACE,{"disambiguationData":[OSD([sQuery(id+"F8.wireOp",EDGE,"E80")])]})])],"derivedFrom":subQ8}),"instanceName":"1"}),"instanceName":"1"}),makeQuery(id+"F19.opPattern","COPY",FACE,{"derivedFrom":makeQuery(id+"F16.opPattern","COPY",FACE,{"derivedFrom":makeQuery(id+"F9.boolean.opBoolean","SPLIT",FACE,{"disambiguationData":[TD([makeQuery(id+"F9.opExtrude","SWEPT_FACE",FACE,{"disambiguationData":[OSD([sQuery(id+"F8.wireOp",EDGE,"E83")])]})])],"derivedFrom":subQ8}),"instanceName":"1"}),"instanceName":"1"})],"fromTools":[makeQuery(id+"F21.opExtrude","CAP_FACE",FACE,{"disambiguationData":[OSD([sQuery(id+"F20.wireOp",EDGE,"E307.0.0")])],"isStart":false})]}),"instanceName":"1"}),"instanceName":"1"})});}
            var sketch = newSketch(context, id + "F64", { "sketchPlane" : qUnion([Q0])});
            skCircle(sketch, "E875.5", {"center": v(-101.6, -56.85) * mm, "radius": 1.53 * mm});
            skCircle(sketch, "E875.9", {"center": v(-99, -59.14) * mm, "radius": 0.8 * mm});
            skArc(sketch, "E875.11", {"start": v(-109.5, -49.9) * mm, "mid": v(-108.33, -50.06) * mm, "end": v(-107.19, -50.36) * mm});
            skArc(sketch, "E875.12", {"start": v(-102.23, -51.89) * mm, "mid": v(-101.6, -51.93) * mm, "end": v(-100.97, -51.89) * mm});
            skCircle(sketch, "E875.14", {"center": v(-101.6, -56.85) * mm, "radius": 0.73 * mm});
            skArc(sketch, "E875.15", {"start": v(-100.94, -58.23) * mm, "mid": v(-100.48, -58.82) * mm, "end": v(-99.8, -59.14) * mm});
            skArc(sketch, "E875.20", {"start": v(-100.14, -57.33) * mm, "mid": v(-99.5, -57.71) * mm, "end": v(-99.1, -58.34) * mm});
            skArc(sketch, "E875.22", {"start": v(-103.06, -57.33) * mm, "mid": v(-103.7, -57.71) * mm, "end": v(-104.1, -58.34) * mm});
            skLineSegment(sketch, "E875.23", {"start": v(-109.5, -49.9) * mm, "end": v(-99, -59.14) * mm});
            skArc(sketch, "E875.24", {"start": v(-109.5, -49.9) * mm, "mid": v(-109.2, -51.04) * mm, "end": v(-108.75, -52.14) * mm});
            skCircle(sketch, "E876.MirrorC", {"center": v(-104.2, -59.14) * mm, "radius": 0.8 * mm});
            skArc(sketch, "E877.MirrorCS", {"start": v(-100.97, -51.89) * mm, "mid": v(-101.6, -51.93) * mm, "end": v(-102.23, -51.89) * mm});
            skArc(sketch, "E878.MirrorCS", {"start": v(-93.7, -49.9) * mm, "mid": v(-94.87, -50.06) * mm, "end": v(-96.01, -50.36) * mm});
            skArc(sketch, "E879.MirrorCS", {"start": v(-102.26, -58.23) * mm, "mid": v(-102.72, -58.82) * mm, "end": v(-103.4, -59.14) * mm});
            skArc(sketch, "E880.MirrorCS", {"start": v(-93.7, -49.9) * mm, "mid": v(-94, -51.04) * mm, "end": v(-94.45, -52.14) * mm});
            skLineSegment(sketch, "E881.MirrorCS", {"start": v(-93.7, -49.9) * mm, "end": v(-104.2, -59.14) * mm});
            skLineSegment(sketch, "E882", {"start": v(-101.6, -47.27) * mm, "end": v(-101.6, -51.29) * mm});
            skArc(sketch, "E883.0", {"start": v(-107.19, -50.36) * mm, "mid": v(-104.74, -53.27) * mm, "end": v(-101.54, -55.32) * mm});
            skArc(sketch, "E884.0", {"start": v(-108.75, -52.14) * mm, "mid": v(-106.32, -55.06) * mm, "end": v(-103.11, -57.1) * mm});
            skArc(sketch, "E885.MirrorCS", {"start": v(-96.01, -50.36) * mm, "mid": v(-98.46, -53.27) * mm, "end": v(-101.66, -55.32) * mm});
            skArc(sketch, "E886.MirrorCS", {"start": v(-94.45, -52.14) * mm, "mid": v(-96.88, -55.06) * mm, "end": v(-100.09, -57.1) * mm});
            skSolve(sketch);
        }
        {
            var Q0;
            Q0 = qSketchRegion(id + "F64", true);
            var Q1;
            Q1=makeQuery(id+"F34.opExtrude","CAP_FACE",FACE,{"disambiguationData":[OSD([sQuery(id+"F33.wireOp",EDGE,"E523"),sQuery(id+"F33.wireOp",EDGE,"E524"),sQuery(id+"F33.wireOp",EDGE,"E525"),sQuery(id+"F33.wireOp",EDGE,"E526"),sQuery(id+"F33.wireOp",EDGE,"E527"),sQuery(id+"F33.wireOp",EDGE,"E528.trimOffspring"),sQuery(id+"F33.wireOp",EDGE,"E529.MirrorCS"),sQuery(id+"F33.wireOp",EDGE,"E530.MirrorCS"),sQuery(id+"F33.wireOp",EDGE,"E534.MirrorCS"),sQuery(id+"F33.wireOp",EDGE,"E535.MirrorCS"),sQuery(id+"F33.wireOp",EDGE,"E536.MirrorCS"),sQuery(id+"F33.wireOp",EDGE,"E537.MirrorCS"),sQuery(id+"F33.wireOp",EDGE,"E538.MirrorCS"),sQuery(id+"F33.wireOp",EDGE,"E539.MirrorCS"),sQuery(id+"F33.wireOp",EDGE,"E540.MirrorCS"),sQuery(id+"F33.wireOp",EDGE,"E541.MirrorCS"),sQuery(id+"F33.wireOp",EDGE,"E542.MirrorCS"),sQuery(id+"F33.wireOp",EDGE,"E543.MirrorCS"),sQuery(id+"F33.wireOp",EDGE,"E544.MirrorCS"),sQuery(id+"F33.wireOp",EDGE,"E545.MirrorCS"),sQuery(id+"F33.wireOp",EDGE,"E546.MirrorCS"),sQuery(id+"F33.wireOp",EDGE,"E547.MirrorCS"),sQuery(id+"F33.wireOp",EDGE,"E548.MirrorCS"),sQuery(id+"F33.wireOp",EDGE,"E549.MirrorCS"),sQuery(id+"F33.wireOp",EDGE,"E551.trimOffspring"),sQuery(id+"F33.wireOp",EDGE,"E552.trimOffspring"),sQuery(id+"F33.wireOp",EDGE,"E553.trimOffspring"),sQuery(id+"F33.wireOp",EDGE,"E554.trimOffspring"),sQuery(id+"F33.wireOp",EDGE,"E555.trimOffspring"),sQuery(id+"F33.wireOp",EDGE,"E556.trimOffspring"),sQuery(id+"F33.wireOp",EDGE,"E557.trimOffspring"),sQuery(id+"F33.wireOp",EDGE,"E558.trimOffspring"),sQuery(id+"F33.wireOp",EDGE,"E559.trimOffspring"),sQuery(id+"F33.wireOp",EDGE,"E560.trimOffspring"),sQuery(id+"F33.wireOp",EDGE,"E561.trimOffspring"),sQuery(id+"F33.wireOp",EDGE,"E562.trimOffspring"),sQuery(id+"F33.wireOp",EDGE,"E563.trimOffspring"),sQuery(id+"F33.wireOp",EDGE,"E564.trimOffspring"),sQuery(id+"F33.wireOp",EDGE,"E565.trimOffspring"),sQuery(id+"F33.wireOp",EDGE,"E566.trimOffspring"),sQuery(id+"F33.wireOp",EDGE,"E567.trimOffspring"),sQuery(id+"F33.wireOp",EDGE,"E568.trimOffspring"),sQuery(id+"F33.wireOp",EDGE,"E569.trimOffspring"),sQuery(id+"F33.wireOp",EDGE,"E570.trimOffspring"),sQuery(id+"F33.wireOp",EDGE,"E571.trimOffspring"),sQuery(id+"F33.wireOp",EDGE,"E572.trimOffspring"),sQuery(id+"F33.wireOp",EDGE,"E573.trimOffspring"),sQuery(id+"F33.wireOp",EDGE,"E574.trimOffspring"),sQuery(id+"F33.wireOp",EDGE,"E575.trimOffspring"),sQuery(id+"F33.wireOp",EDGE,"E576.trimOffspring"),sQuery(id+"F33.wireOp",EDGE,"E577.trimOffspring"),sQuery(id+"F33.wireOp",EDGE,"E578.trimOffspring"),sQuery(id+"F33.wireOp",EDGE,"E579.trimOffspring"),sQuery(id+"F33.wireOp",EDGE,"E580.trimOffspring"),sQuery(id+"F33.wireOp",EDGE,"E581.trimOffspring"),sQuery(id+"F33.wireOp",EDGE,"E582.trimOffspring"),sQuery(id+"F33.wireOp",EDGE,"E583.trimOffspring"),sQuery(id+"F33.wireOp",EDGE,"E584.trimOffspring"),sQuery(id+"F33.wireOp",EDGE,"E585.trimOffspring"),sQuery(id+"F33.wireOp",EDGE,"E586.trimOffspring"),sQuery(id+"F33.wireOp",EDGE,"E587.trimOffspring"),sQuery(id+"F33.wireOp",EDGE,"E588.trimOffspring"),sQuery(id+"F33.wireOp",EDGE,"E589.trimOffspring"),sQuery(id+"F33.wireOp",EDGE,"E590.trimOffspring"),sQuery(id+"F33.wireOp",EDGE,"E591.trimOffspring"),sQuery(id+"F33.wireOp",EDGE,"E592.trimOffspring"),sQuery(id+"F33.wireOp",EDGE,"E593.trimOffspring"),sQuery(id+"F33.wireOp",EDGE,"E594.trimOffspring"),sQuery(id+"F33.wireOp",EDGE,"E595.trimOffspring"),sQuery(id+"F33.wireOp",EDGE,"E596.trimOffspring"),sQuery(id+"F33.wireOp",EDGE,"E597.trimOffspring"),sQuery(id+"F33.wireOp",EDGE,"E598.trimOffspring")])],"isStart":false});
            extrude(context, id + "F65", {"entities" : qUnion([Q0]), "operationType" : NewBodyOperationType.ADD, "endBound" : BoundingType.UP_TO_SURFACE, "depth" : 25.4 * mm, "endBoundEntityFace" : qUnion([Q1]), "offsetDistance" : 25.4 * mm});
        }
        {
            var Q0;
            Q0=makeQuery(id+"F63.opExtrude","CAP_FACE",FACE,{"disambiguationData":[OSD([sQuery(id+"F62.wireOp",EDGE,"E842"),sQuery(id+"F62.wireOp",EDGE,"E843"),sQuery(id+"F62.wireOp",EDGE,"E845.MirrorCS"),sQuery(id+"F62.wireOp",EDGE,"E868.MirrorCS"),sQuery(id+"F62.wireOp",EDGE,"E869"),sQuery(id+"F62.wireOp",EDGE,"E870"),sQuery(id+"F62.wireOp",EDGE,"E871.MirrorCS"),sQuery(id+"F62.wireOp",EDGE,"E873"),sQuery(id+"F62.wireOp",EDGE,"E874")])],"isStart":false});
            var sketch = newSketch(context, id + "F66", { "sketchPlane" : qUnion([Q0])});
            skArc(sketch, "E887", {"start": v(-100.09, -57.1) * mm, "mid": v(-101.6, -55.32) * mm, "end": v(-103.11, -57.1) * mm});
            skArc(sketch, "E888", {"start": v(-99.52, -56.83) * mm, "mid": v(-99.88, -55.67) * mm, "end": v(-100.83, -54.91) * mm});
            skArc(sketch, "E889.0", {"start": v(-107.19, -50.36) * mm, "mid": v(-104.74, -53.27) * mm, "end": v(-101.54, -55.32) * mm});
            skArc(sketch, "E890.0", {"start": v(-108.75, -52.14) * mm, "mid": v(-106.32, -55.06) * mm, "end": v(-103.11, -57.1) * mm});
            skLineSegment(sketch, "E891", {"start": v(-101.6, -56.85) * mm, "end": v(-101.6, -55.8) * mm});
            skArc(sketch, "E892.MirrorCS", {"start": v(-96.01, -50.36) * mm, "mid": v(-98.46, -53.27) * mm, "end": v(-101.66, -55.32) * mm});
            skArc(sketch, "E893.MirrorCS", {"start": v(-94.45, -52.14) * mm, "mid": v(-96.88, -55.06) * mm, "end": v(-100.09, -57.1) * mm});
            skArc(sketch, "E894.trimOffspring", {"start": v(-102.37, -54.91) * mm, "mid": v(-103.32, -55.67) * mm, "end": v(-103.68, -56.83) * mm});
            skArc(sketch, "E895", {"start": v(-99.98, -55.54) * mm, "mid": v(-98.1, -54.3) * mm, "end": v(-96.4, -52.82) * mm});
            skArc(sketch, "E896", {"start": v(-99.63, -56.18) * mm, "mid": v(-97.78, -54.72) * mm, "end": v(-96.4, -52.82) * mm});
            skArc(sketch, "E897.MirrorCS", {"start": v(-103.22, -55.54) * mm, "mid": v(-105.1, -54.3) * mm, "end": v(-106.8, -52.82) * mm});
            skArc(sketch, "E898.MirrorCS", {"start": v(-103.57, -56.18) * mm, "mid": v(-105.42, -54.72) * mm, "end": v(-106.8, -52.82) * mm});
            skSolve(sketch);
        }
        {
            var Q0;
            Q0 = qSketchRegion(id + "F66", true);
            var Q1;
            {var subQ4=sQuery(id+"F4.wireOp",EDGE,"E8");var subQ5=makeQuery(id+"F5.boolean.opBoolean","COPY",FACE,{"derivedFrom":makeQuery(id+"F5.opExtrude","SWEPT_FACE",FACE,{"disambiguationData":[OSD([subQ4])]})});var subQ8=makeQuery(id+"F5.boolean.opBoolean","COPY",FACE,{"derivedFrom":makeQuery(id+"F5.opExtrude","CAP_FACE",FACE,{"disambiguationData":[OSD([subQ4])],"isStart":false})});Q1=makeQuery(id+"F63.boolean.opBoolean","SPLIT",FACE,{"disambiguationData":[TD([makeQuery(id+"F40.opPattern","COPY",FACE,{"derivedFrom":makeQuery(id+"F39.opPattern","COPY",FACE,{"derivedFrom":makeQuery(id+"F19.opPattern","COPY",FACE,{"derivedFrom":makeQuery(id+"F16.opPattern","COPY",FACE,{"derivedFrom":subQ5,"instanceName":"1"}),"instanceName":"1"}),"instanceName":"1"}),"instanceName":"1"})])],"derivedFrom":makeQuery(id+"F40.opPattern","COPY",FACE,{"derivedFrom":makeQuery(id+"F39.opPattern","COPY",FACE,{"derivedFrom":makeQuery(id+"F21.boolean.opBoolean","MERGE",FACE,{"derivedFrom":[makeQuery(id+"F19.opPattern","COPY",FACE,{"derivedFrom":makeQuery(id+"F16.opPattern","COPY",FACE,{"derivedFrom":makeQuery(id+"F9.boolean.opBoolean","SPLIT",FACE,{"disambiguationData":[TD([subQ5])],"derivedFrom":subQ8}),"instanceName":"1"}),"instanceName":"1"}),makeQuery(id+"F19.opPattern","COPY",FACE,{"derivedFrom":makeQuery(id+"F16.opPattern","COPY",FACE,{"derivedFrom":makeQuery(id+"F9.boolean.opBoolean","SPLIT",FACE,{"disambiguationData":[TD([makeQuery(id+"F9.opExtrude","SWEPT_FACE",FACE,{"disambiguationData":[OSD([sQuery(id+"F8.wireOp",EDGE,"E25")])]})])],"derivedFrom":subQ8}),"instanceName":"1"}),"instanceName":"1"}),makeQuery(id+"F19.opPattern","COPY",FACE,{"derivedFrom":makeQuery(id+"F16.opPattern","COPY",FACE,{"derivedFrom":makeQuery(id+"F9.boolean.opBoolean","SPLIT",FACE,{"disambiguationData":[TD([makeQuery(id+"F9.opExtrude","SWEPT_FACE",FACE,{"disambiguationData":[OSD([sQuery(id+"F8.wireOp",EDGE,"E32")])]})])],"derivedFrom":subQ8}),"instanceName":"1"}),"instanceName":"1"}),makeQuery(id+"F19.opPattern","COPY",FACE,{"derivedFrom":makeQuery(id+"F16.opPattern","COPY",FACE,{"derivedFrom":makeQuery(id+"F9.boolean.opBoolean","SPLIT",FACE,{"disambiguationData":[TD([makeQuery(id+"F9.opExtrude","SWEPT_FACE",FACE,{"disambiguationData":[OSD([sQuery(id+"F8.wireOp",EDGE,"E33.0")])]})])],"derivedFrom":subQ8}),"instanceName":"1"}),"instanceName":"1"}),makeQuery(id+"F19.opPattern","COPY",FACE,{"derivedFrom":makeQuery(id+"F16.opPattern","COPY",FACE,{"derivedFrom":makeQuery(id+"F9.boolean.opBoolean","SPLIT",FACE,{"disambiguationData":[TD([makeQuery(id+"F9.opExtrude","SWEPT_FACE",FACE,{"disambiguationData":[OSD([sQuery(id+"F8.wireOp",EDGE,"E37")])]})])],"derivedFrom":subQ8}),"instanceName":"1"}),"instanceName":"1"}),makeQuery(id+"F19.opPattern","COPY",FACE,{"derivedFrom":makeQuery(id+"F16.opPattern","COPY",FACE,{"derivedFrom":makeQuery(id+"F9.boolean.opBoolean","SPLIT",FACE,{"disambiguationData":[TD([makeQuery(id+"F9.opExtrude","SWEPT_FACE",FACE,{"disambiguationData":[OSD([sQuery(id+"F8.wireOp",EDGE,"E51.MirrorCS")])]})])],"derivedFrom":subQ8}),"instanceName":"1"}),"instanceName":"1"}),makeQuery(id+"F19.opPattern","COPY",FACE,{"derivedFrom":makeQuery(id+"F16.opPattern","COPY",FACE,{"derivedFrom":makeQuery(id+"F9.boolean.opBoolean","SPLIT",FACE,{"disambiguationData":[TD([makeQuery(id+"F9.opExtrude","SWEPT_FACE",FACE,{"disambiguationData":[OSD([sQuery(id+"F8.wireOp",EDGE,"E53.MirrorCS")])]})])],"derivedFrom":subQ8}),"instanceName":"1"}),"instanceName":"1"}),makeQuery(id+"F19.opPattern","COPY",FACE,{"derivedFrom":makeQuery(id+"F16.opPattern","COPY",FACE,{"derivedFrom":makeQuery(id+"F9.boolean.opBoolean","SPLIT",FACE,{"disambiguationData":[TD([makeQuery(id+"F9.opExtrude","SWEPT_FACE",FACE,{"disambiguationData":[OSD([sQuery(id+"F8.wireOp",EDGE,"E80")])]})])],"derivedFrom":subQ8}),"instanceName":"1"}),"instanceName":"1"}),makeQuery(id+"F19.opPattern","COPY",FACE,{"derivedFrom":makeQuery(id+"F16.opPattern","COPY",FACE,{"derivedFrom":makeQuery(id+"F9.boolean.opBoolean","SPLIT",FACE,{"disambiguationData":[TD([makeQuery(id+"F9.opExtrude","SWEPT_FACE",FACE,{"disambiguationData":[OSD([sQuery(id+"F8.wireOp",EDGE,"E83")])]})])],"derivedFrom":subQ8}),"instanceName":"1"}),"instanceName":"1"})],"fromTools":[makeQuery(id+"F21.opExtrude","CAP_FACE",FACE,{"disambiguationData":[OSD([sQuery(id+"F20.wireOp",EDGE,"E307.0.0")])],"isStart":false})]}),"instanceName":"1"}),"instanceName":"1"})});}
            extrude(context, id + "F67", {"entities" : qUnion([Q0]), "operationType" : NewBodyOperationType.REMOVE, "endBound" : BoundingType.UP_TO_SURFACE, "oppositeDirection" : true, "depth" : 25.4 * mm, "endBoundEntityFace" : qUnion([Q1]), "offsetDistance" : 25.4 * mm});
        }
        {
            var Q0;
            {var subQ0=sQuery(id+"F4.wireOp",EDGE,"E8");var subQ1=makeQuery(id+"F5.boolean.opBoolean","COPY",FACE,{"derivedFrom":makeQuery(id+"F5.opExtrude","CAP_FACE",FACE,{"disambiguationData":[OSD([subQ0])],"isStart":false})});Q0=makeQuery(id+"F39.opPattern","COPY",FACE,{"derivedFrom":makeQuery(id+"F21.boolean.opBoolean","MERGE",FACE,{"derivedFrom":[makeQuery(id+"F19.opPattern","COPY",FACE,{"derivedFrom":makeQuery(id+"F17.opPattern","COPY",FACE,{"derivedFrom":makeQuery(id+"F9.boolean.opBoolean","SPLIT",FACE,{"disambiguationData":[TD([makeQuery(id+"F5.boolean.opBoolean","COPY",FACE,{"derivedFrom":makeQuery(id+"F5.opExtrude","SWEPT_FACE",FACE,{"disambiguationData":[OSD([subQ0])]})})])],"derivedFrom":subQ1}),"instanceName":"1"}),"instanceName":"1"}),makeQuery(id+"F19.opPattern","COPY",FACE,{"derivedFrom":makeQuery(id+"F17.opPattern","COPY",FACE,{"derivedFrom":makeQuery(id+"F9.boolean.opBoolean","SPLIT",FACE,{"disambiguationData":[TD([makeQuery(id+"F9.opExtrude","SWEPT_FACE",FACE,{"disambiguationData":[OSD([sQuery(id+"F8.wireOp",EDGE,"E25")])]})])],"derivedFrom":subQ1}),"instanceName":"1"}),"instanceName":"1"}),makeQuery(id+"F19.opPattern","COPY",FACE,{"derivedFrom":makeQuery(id+"F17.opPattern","COPY",FACE,{"derivedFrom":makeQuery(id+"F9.boolean.opBoolean","SPLIT",FACE,{"disambiguationData":[TD([makeQuery(id+"F9.opExtrude","SWEPT_FACE",FACE,{"disambiguationData":[OSD([sQuery(id+"F8.wireOp",EDGE,"E32")])]})])],"derivedFrom":subQ1}),"instanceName":"1"}),"instanceName":"1"}),makeQuery(id+"F19.opPattern","COPY",FACE,{"derivedFrom":makeQuery(id+"F17.opPattern","COPY",FACE,{"derivedFrom":makeQuery(id+"F9.boolean.opBoolean","SPLIT",FACE,{"disambiguationData":[TD([makeQuery(id+"F9.opExtrude","SWEPT_FACE",FACE,{"disambiguationData":[OSD([sQuery(id+"F8.wireOp",EDGE,"E33.0")])]})])],"derivedFrom":subQ1}),"instanceName":"1"}),"instanceName":"1"}),makeQuery(id+"F19.opPattern","COPY",FACE,{"derivedFrom":makeQuery(id+"F17.opPattern","COPY",FACE,{"derivedFrom":makeQuery(id+"F9.boolean.opBoolean","SPLIT",FACE,{"disambiguationData":[TD([makeQuery(id+"F9.opExtrude","SWEPT_FACE",FACE,{"disambiguationData":[OSD([sQuery(id+"F8.wireOp",EDGE,"E37")])]})])],"derivedFrom":subQ1}),"instanceName":"1"}),"instanceName":"1"}),makeQuery(id+"F19.opPattern","COPY",FACE,{"derivedFrom":makeQuery(id+"F17.opPattern","COPY",FACE,{"derivedFrom":makeQuery(id+"F9.boolean.opBoolean","SPLIT",FACE,{"disambiguationData":[TD([makeQuery(id+"F9.opExtrude","SWEPT_FACE",FACE,{"disambiguationData":[OSD([sQuery(id+"F8.wireOp",EDGE,"E51.MirrorCS")])]})])],"derivedFrom":subQ1}),"instanceName":"1"}),"instanceName":"1"}),makeQuery(id+"F19.opPattern","COPY",FACE,{"derivedFrom":makeQuery(id+"F17.opPattern","COPY",FACE,{"derivedFrom":makeQuery(id+"F9.boolean.opBoolean","SPLIT",FACE,{"disambiguationData":[TD([makeQuery(id+"F9.opExtrude","SWEPT_FACE",FACE,{"disambiguationData":[OSD([sQuery(id+"F8.wireOp",EDGE,"E53.MirrorCS")])]})])],"derivedFrom":subQ1}),"instanceName":"1"}),"instanceName":"1"}),makeQuery(id+"F19.opPattern","COPY",FACE,{"derivedFrom":makeQuery(id+"F17.opPattern","COPY",FACE,{"derivedFrom":makeQuery(id+"F9.boolean.opBoolean","SPLIT",FACE,{"disambiguationData":[TD([makeQuery(id+"F9.opExtrude","SWEPT_FACE",FACE,{"disambiguationData":[OSD([sQuery(id+"F8.wireOp",EDGE,"E80")])]})])],"derivedFrom":subQ1}),"instanceName":"1"}),"instanceName":"1"}),makeQuery(id+"F19.opPattern","COPY",FACE,{"derivedFrom":makeQuery(id+"F17.opPattern","COPY",FACE,{"derivedFrom":makeQuery(id+"F9.boolean.opBoolean","SPLIT",FACE,{"disambiguationData":[TD([makeQuery(id+"F9.opExtrude","SWEPT_FACE",FACE,{"disambiguationData":[OSD([sQuery(id+"F8.wireOp",EDGE,"E83")])]})])],"derivedFrom":subQ1}),"instanceName":"1"}),"instanceName":"1"}),makeQuery(id+"F21.opExtrude","CAP_FACE",FACE,{"disambiguationData":[OSD([sQuery(id+"F20.wireOp",EDGE,"E309.0.0")])],"isStart":false})]}),"instanceName":"1"});}
            var sketch = newSketch(context, id + "F68", { "sketchPlane" : qUnion([Q0])});
            skPoint(sketch, "E899.0", {"position": v(-50.8, -38.1) * mm});
            skArc(sketch, "E900", {"start": v(-52.87, -42.8) * mm, "mid": v(-53.35, -42.95) * mm, "end": v(-53.82, -43.12) * mm});
            skCircle(sketch, "E901", {"center": v(-50.8, -50.8) * mm, "radius": 5.34 * mm});
            skLineSegment(sketch, "E902.top", {"start": v(-51.3, -60.05) * mm, "end": v(-50.3, -60.05) * mm});
            skLineSegment(sketch, "E902.left", {"start": v(-51.3, -41.55) * mm, "end": v(-51.3, -44.6) * mm});
            skLineSegment(sketch, "E902.right", {"start": v(-50.3, -41.55) * mm, "end": v(-50.3, -44.6) * mm});
            skArc(sketch, "E903", {"start": v(-54.85, -46.08) * mm, "mid": v(-55.2, -46.4) * mm, "end": v(-55.52, -46.75) * mm});
            skLineSegment(sketch, "E904.MirrorCS", {"start": v(-45.77, -43.02) * mm, "end": v(-47.56, -45.5) * mm});
            skLineSegment(sketch, "E905.MirrorCS", {"start": v(-44.96, -43.6) * mm, "end": v(-46.75, -46.08) * mm});
            skLineSegment(sketch, "E906.MirrorCS", {"start": v(-42.16, -47.47) * mm, "end": v(-45.06, -48.4) * mm});
            skLineSegment(sketch, "E907.MirrorCS", {"start": v(-41.85, -48.42) * mm, "end": v(-44.75, -49.36) * mm});
            skLineSegment(sketch, "E908.MirrorCS", {"start": v(-41.85, -53.18) * mm, "end": v(-44.75, -52.24) * mm});
            skLineSegment(sketch, "E909.MirrorCS", {"start": v(-42.16, -54.13) * mm, "end": v(-45.06, -53.2) * mm});
            skLineSegment(sketch, "E910.MirrorCS", {"start": v(-44.96, -58) * mm, "end": v(-46.75, -55.52) * mm});
            skLineSegment(sketch, "E911.MirrorCS", {"start": v(-45.77, -58.58) * mm, "end": v(-47.56, -56.1) * mm});
            skLineSegment(sketch, "E912.MirrorCS", {"start": v(-48.42, -41.85) * mm, "end": v(-49.36, -44.75) * mm});
            skLineSegment(sketch, "E913.MirrorCS", {"start": v(-47.47, -42.16) * mm, "end": v(-48.4, -45.06) * mm});
            skLineSegment(sketch, "E914.MirrorCS", {"start": v(-53.18, -41.85) * mm, "end": v(-52.24, -44.75) * mm});
            skLineSegment(sketch, "E915.MirrorCS", {"start": v(-54.13, -42.16) * mm, "end": v(-53.2, -45.06) * mm});
            skLineSegment(sketch, "E916.MirrorCS", {"start": v(-58, -44.96) * mm, "end": v(-55.52, -46.75) * mm});
            skLineSegment(sketch, "E917.MirrorCS", {"start": v(-58.58, -45.77) * mm, "end": v(-56.1, -47.56) * mm});
            skLineSegment(sketch, "E918.MirrorCS", {"start": v(-60.05, -50.3) * mm, "end": v(-57, -50.3) * mm});
            skLineSegment(sketch, "E919.MirrorCS", {"start": v(-60.05, -51.3) * mm, "end": v(-57, -51.3) * mm});
            skLineSegment(sketch, "E920.MirrorCS", {"start": v(-58.58, -55.83) * mm, "end": v(-56.1, -54.04) * mm});
            skLineSegment(sketch, "E921.MirrorCS", {"start": v(-58, -56.64) * mm, "end": v(-55.52, -54.85) * mm});
            skArc(sketch, "E922.trimOffspring", {"start": v(-50.3, -42.56) * mm, "mid": v(-50.8, -42.55) * mm, "end": v(-51.3, -42.56) * mm});
            skArc(sketch, "E923.trimOffspring", {"start": v(-47.78, -43.12) * mm, "mid": v(-48.25, -42.95) * mm, "end": v(-48.73, -42.8) * mm});
            skArc(sketch, "E924.trimOffspring", {"start": v(-45.55, -44.43) * mm, "mid": v(-45.95, -44.12) * mm, "end": v(-46.36, -43.84) * mm});
            skArc(sketch, "E925.trimOffspring", {"start": v(-43.84, -46.36) * mm, "mid": v(-44.12, -45.95) * mm, "end": v(-44.43, -45.55) * mm});
            skArc(sketch, "E926.trimOffspring", {"start": v(-42.8, -48.73) * mm, "mid": v(-42.95, -48.25) * mm, "end": v(-43.12, -47.78) * mm});
            skArc(sketch, "E927.trimOffspring", {"start": v(-42.56, -51.3) * mm, "mid": v(-42.55, -50.8) * mm, "end": v(-42.56, -50.3) * mm});
            skArc(sketch, "E928.trimOffspring", {"start": v(-43.12, -53.82) * mm, "mid": v(-42.95, -53.35) * mm, "end": v(-42.8, -52.87) * mm});
            skArc(sketch, "E929.trimOffspring", {"start": v(-44.43, -56.05) * mm, "mid": v(-44.12, -55.65) * mm, "end": v(-43.84, -55.24) * mm});
            skArc(sketch, "E930.trimOffspring", {"start": v(-46.36, -57.76) * mm, "mid": v(-45.95, -57.48) * mm, "end": v(-45.55, -57.17) * mm});
            skArc(sketch, "E931.trimOffspring", {"start": v(-48.73, -58.8) * mm, "mid": v(-48.25, -58.65) * mm, "end": v(-47.78, -58.48) * mm});
            skArc(sketch, "E932.trimOffspring", {"start": v(-51.3, -59.04) * mm, "mid": v(-50.8, -59.05) * mm, "end": v(-50.3, -59.04) * mm});
            skArc(sketch, "E933.trimOffspring", {"start": v(-53.82, -58.48) * mm, "mid": v(-53.35, -58.65) * mm, "end": v(-52.87, -58.8) * mm});
            skArc(sketch, "E934.trimOffspring", {"start": v(-56.05, -57.17) * mm, "mid": v(-55.65, -57.48) * mm, "end": v(-55.24, -57.76) * mm});
            skArc(sketch, "E935.trimOffspring", {"start": v(-57.76, -55.24) * mm, "mid": v(-57.48, -55.65) * mm, "end": v(-57.17, -56.05) * mm});
            skArc(sketch, "E936.trimOffspring", {"start": v(-58.8, -52.87) * mm, "mid": v(-58.65, -53.35) * mm, "end": v(-58.48, -53.82) * mm});
            skArc(sketch, "E937.trimOffspring", {"start": v(-59.04, -50.3) * mm, "mid": v(-59.05, -50.8) * mm, "end": v(-59.04, -51.3) * mm});
            skArc(sketch, "E938.trimOffspring", {"start": v(-58.48, -47.78) * mm, "mid": v(-58.65, -48.25) * mm, "end": v(-58.8, -48.73) * mm});
            skArc(sketch, "E939.trimOffspring", {"start": v(-57.17, -45.55) * mm, "mid": v(-57.48, -45.95) * mm, "end": v(-57.76, -46.36) * mm});
            skArc(sketch, "E940.trimOffspring", {"start": v(-55.24, -43.84) * mm, "mid": v(-55.65, -44.12) * mm, "end": v(-56.05, -44.43) * mm});
            skArc(sketch, "E941.trimOffspring", {"start": v(-53.2, -45.06) * mm, "mid": v(-53.62, -45.26) * mm, "end": v(-54.04, -45.5) * mm});
            skArc(sketch, "E942.trimOffspring", {"start": v(-51.3, -44.6) * mm, "mid": v(-51.77, -44.66) * mm, "end": v(-52.24, -44.75) * mm});
            skArc(sketch, "E943.trimOffspring", {"start": v(-49.36, -44.75) * mm, "mid": v(-49.83, -44.66) * mm, "end": v(-50.3, -44.6) * mm});
            skArc(sketch, "E944.trimOffspring", {"start": v(-47.56, -45.5) * mm, "mid": v(-47.98, -45.26) * mm, "end": v(-48.4, -45.06) * mm});
            skArc(sketch, "E945.trimOffspring", {"start": v(-46.08, -46.75) * mm, "mid": v(-46.4, -46.4) * mm, "end": v(-46.75, -46.08) * mm});
            skArc(sketch, "E946.trimOffspring", {"start": v(-45.06, -48.4) * mm, "mid": v(-45.26, -47.98) * mm, "end": v(-45.5, -47.56) * mm});
            skArc(sketch, "E947.trimOffspring", {"start": v(-44.6, -50.3) * mm, "mid": v(-44.66, -49.83) * mm, "end": v(-44.75, -49.36) * mm});
            skArc(sketch, "E948.trimOffspring", {"start": v(-44.75, -52.24) * mm, "mid": v(-44.66, -51.77) * mm, "end": v(-44.6, -51.3) * mm});
            skArc(sketch, "E949.trimOffspring", {"start": v(-45.5, -54.04) * mm, "mid": v(-45.26, -53.62) * mm, "end": v(-45.06, -53.2) * mm});
            skArc(sketch, "E950.trimOffspring", {"start": v(-46.75, -55.52) * mm, "mid": v(-46.4, -55.2) * mm, "end": v(-46.08, -54.85) * mm});
            skArc(sketch, "E951.trimOffspring", {"start": v(-48.4, -56.54) * mm, "mid": v(-47.98, -56.34) * mm, "end": v(-47.56, -56.1) * mm});
            skArc(sketch, "E952.trimOffspring", {"start": v(-50.3, -57) * mm, "mid": v(-49.83, -56.94) * mm, "end": v(-49.36, -56.85) * mm});
            skArc(sketch, "E953.trimOffspring", {"start": v(-52.24, -56.85) * mm, "mid": v(-51.77, -56.94) * mm, "end": v(-51.3, -57) * mm});
            skArc(sketch, "E954.trimOffspring", {"start": v(-54.04, -56.1) * mm, "mid": v(-53.62, -56.34) * mm, "end": v(-53.2, -56.54) * mm});
            skArc(sketch, "E955.trimOffspring", {"start": v(-55.52, -54.85) * mm, "mid": v(-55.2, -55.2) * mm, "end": v(-54.85, -55.52) * mm});
            skArc(sketch, "E956.trimOffspring", {"start": v(-56.54, -53.2) * mm, "mid": v(-56.34, -53.62) * mm, "end": v(-56.1, -54.04) * mm});
            skArc(sketch, "E957.trimOffspring", {"start": v(-57, -51.3) * mm, "mid": v(-56.94, -51.77) * mm, "end": v(-56.85, -52.24) * mm});
            skArc(sketch, "E958.trimOffspring", {"start": v(-56.85, -49.36) * mm, "mid": v(-56.94, -49.83) * mm, "end": v(-57, -50.3) * mm});
            skArc(sketch, "E959.trimOffspring", {"start": v(-56.1, -47.56) * mm, "mid": v(-56.34, -47.98) * mm, "end": v(-56.54, -48.4) * mm});
            skLineSegment(sketch, "E960.trimOffspring", {"start": v(-54.85, -46.08) * mm, "end": v(-56.64, -43.6) * mm});
            skLineSegment(sketch, "E961.trimOffspring", {"start": v(-54.04, -45.5) * mm, "end": v(-55.83, -43.02) * mm});
            skLineSegment(sketch, "E962.trimOffspring", {"start": v(-46.08, -46.75) * mm, "end": v(-43.6, -44.96) * mm});
            skLineSegment(sketch, "E963.trimOffspring", {"start": v(-45.5, -47.56) * mm, "end": v(-43.02, -45.77) * mm});
            skLineSegment(sketch, "E964.trimOffspring", {"start": v(-44.6, -50.3) * mm, "end": v(-41.55, -50.3) * mm});
            skLineSegment(sketch, "E965.trimOffspring", {"start": v(-44.6, -51.3) * mm, "end": v(-41.55, -51.3) * mm});
            skLineSegment(sketch, "E966.trimOffspring", {"start": v(-45.5, -54.04) * mm, "end": v(-43.02, -55.83) * mm});
            skLineSegment(sketch, "E967.trimOffspring", {"start": v(-46.08, -54.85) * mm, "end": v(-43.6, -56.64) * mm});
            skLineSegment(sketch, "E968.trimOffspring", {"start": v(-48.4, -56.54) * mm, "end": v(-47.47, -59.44) * mm});
            skLineSegment(sketch, "E969.trimOffspring", {"start": v(-49.36, -56.85) * mm, "end": v(-48.42, -59.75) * mm});
            skLineSegment(sketch, "E970.trimOffspring", {"start": v(-50.3, -57) * mm, "end": v(-50.3, -60.05) * mm});
            skLineSegment(sketch, "E971.trimOffspring", {"start": v(-51.3, -57) * mm, "end": v(-51.3, -60.05) * mm});
            skLineSegment(sketch, "E972.trimOffspring", {"start": v(-52.24, -56.85) * mm, "end": v(-53.18, -59.75) * mm});
            skLineSegment(sketch, "E973.trimOffspring", {"start": v(-53.2, -56.54) * mm, "end": v(-54.13, -59.44) * mm});
            skLineSegment(sketch, "E974.trimOffspring", {"start": v(-54.04, -56.1) * mm, "end": v(-55.83, -58.58) * mm});
            skLineSegment(sketch, "E975.trimOffspring", {"start": v(-54.85, -55.52) * mm, "end": v(-56.64, -58) * mm});
            skLineSegment(sketch, "E976.trimOffspring", {"start": v(-56.54, -53.2) * mm, "end": v(-59.44, -54.13) * mm});
            skLineSegment(sketch, "E977.trimOffspring", {"start": v(-56.85, -52.24) * mm, "end": v(-59.75, -53.18) * mm});
            skLineSegment(sketch, "E978.trimOffspring", {"start": v(-56.85, -49.36) * mm, "end": v(-59.75, -48.42) * mm});
            skLineSegment(sketch, "E979.trimOffspring", {"start": v(-56.54, -48.4) * mm, "end": v(-59.44, -47.47) * mm});
            skCircle(sketch, "E980", {"center": v(-50.8, -50.8) * mm, "radius": 1.57 * mm});
            skArc(sketch, "E981", {"start": v(-50.8, -48.52) * mm, "mid": v(-53.08, -50.8) * mm, "end": v(-50.8, -53.08) * mm});
            skLineSegment(sketch, "E982.top", {"start": v(-51.29, -55.05) * mm, "end": v(-50.31, -55.05) * mm});
            skLineSegment(sketch, "E983.left", {"start": v(-46.55, -50.31) * mm, "end": v(-46.55, -51.29) * mm});
            skLineSegment(sketch, "E983.right", {"start": v(-55.05, -50.31) * mm, "end": v(-55.05, -51.29) * mm});
            skArc(sketch, "E984", {"start": v(-50.43, -46.88) * mm, "mid": v(-49.96, -46.58) * mm, "end": v(-50.37, -46.2) * mm});
            skArc(sketch, "E985", {"start": v(-50.37, -46.2) * mm, "mid": v(-50.8, -45.66) * mm, "end": v(-51.23, -46.2) * mm});
            skPoint(sketch, "E985.centerSnap0", {"position": v(-50.8, -46.55) * mm});
            skLineSegment(sketch, "E986", {"start": v(-50.8, -46.55) * mm, "end": v(-50.8, -46.86) * mm});
            skArc(sketch, "E987.MirrorC", {"start": v(-51.17, -46.88) * mm, "mid": v(-51.64, -46.58) * mm, "end": v(-51.23, -46.2) * mm});
            skArc(sketch, "E988", {"start": v(-50.43, -46.88) * mm, "mid": v(-50.57, -47.4) * mm, "end": v(-50.5, -47.92) * mm});
            skArc(sketch, "E989.MirrorCS", {"start": v(-51.17, -46.88) * mm, "mid": v(-51.03, -47.4) * mm, "end": v(-51.1, -47.92) * mm});
            skLineSegment(sketch, "E990", {"start": v(-51.1, -47.92) * mm, "end": v(-50.8, -48.2) * mm});
            skLineSegment(sketch, "E991", {"start": v(-50.8, -48.2) * mm, "end": v(-50.5, -47.92) * mm});
            skArc(sketch, "E992.trimOffspring", {"start": v(-50.94, -46.52) * mm, "mid": v(-50.8, -46.55) * mm, "end": v(-50.66, -46.52) * mm});
            skLineSegment(sketch, "E993", {"start": v(-50.8, -50.8) * mm, "end": v(-48.72, -48.72) * mm});
            skLineSegment(sketch, "E994", {"start": v(-50.8, -50.8) * mm, "end": v(-48.57, -50.8) * mm});
            skLineSegment(sketch, "E995.MirrorCS", {"start": v(-51.1, -53.68) * mm, "end": v(-50.8, -53.4) * mm});
            skArc(sketch, "E996.MirrorCS", {"start": v(-50.94, -55.08) * mm, "mid": v(-50.8, -55.05) * mm, "end": v(-50.66, -55.08) * mm});
            skLineSegment(sketch, "E997.MirrorCS", {"start": v(-50.8, -53.4) * mm, "end": v(-50.5, -53.68) * mm});
            skLineSegment(sketch, "E998.MirrorCS", {"start": v(-50.8, -55.05) * mm, "end": v(-50.8, -54.74) * mm});
            skArc(sketch, "E999.MirrorCS", {"start": v(-50.37, -55.4) * mm, "mid": v(-50.8, -55.94) * mm, "end": v(-51.23, -55.4) * mm});
            skArc(sketch, "E1000.MirrorCS", {"start": v(-51.17, -54.72) * mm, "mid": v(-51.64, -55.02) * mm, "end": v(-51.23, -55.4) * mm});
            skArc(sketch, "E1001.MirrorCS", {"start": v(-50.8, -53.08) * mm, "mid": v(-54.43, -50.8) * mm, "end": v(-50.8, -48.52) * mm});
            skArc(sketch, "E1002.MirrorCS", {"start": v(-50.43, -54.72) * mm, "mid": v(-50.57, -54.2) * mm, "end": v(-50.5, -53.68) * mm});
            skPoint(sketch, "E1003.MirrorP", {"position": v(-50.8, -55.05) * mm});
            skArc(sketch, "E1004.MirrorCS", {"start": v(-51.17, -54.72) * mm, "mid": v(-51.03, -54.2) * mm, "end": v(-51.1, -53.68) * mm});
            skArc(sketch, "E1005.MirrorCS", {"start": v(-50.43, -54.72) * mm, "mid": v(-49.96, -55.02) * mm, "end": v(-50.37, -55.4) * mm});
            skArc(sketch, "E1006.MirrorCS", {"start": v(-46.52, -50.94) * mm, "mid": v(-46.55, -50.8) * mm, "end": v(-46.52, -50.66) * mm});
            skArc(sketch, "E1007.MirrorCS", {"start": v(-46.88, -51.17) * mm, "mid": v(-46.58, -51.64) * mm, "end": v(-46.2, -51.23) * mm});
            skLineSegment(sketch, "E1008.MirrorCS", {"start": v(-46.55, -50.8) * mm, "end": v(-46.86, -50.8) * mm});
            skArc(sketch, "E1009.MirrorCS", {"start": v(-46.88, -50.43) * mm, "mid": v(-47.4, -50.57) * mm, "end": v(-47.92, -50.5) * mm});
            skArc(sketch, "E1010.MirrorCS", {"start": v(-46.88, -50.43) * mm, "mid": v(-46.58, -49.96) * mm, "end": v(-46.2, -50.37) * mm});
            skArc(sketch, "E1011.MirrorCS", {"start": v(-46.88, -51.17) * mm, "mid": v(-47.4, -51.03) * mm, "end": v(-47.92, -51.1) * mm});
            skLineSegment(sketch, "E1012.MirrorCS", {"start": v(-47.92, -51.1) * mm, "end": v(-48.2, -50.8) * mm});
            skArc(sketch, "E1013.MirrorCS", {"start": v(-46.2, -50.37) * mm, "mid": v(-45.66, -50.8) * mm, "end": v(-46.2, -51.23) * mm});
            skLineSegment(sketch, "E1014.MirrorCS", {"start": v(-48.2, -50.8) * mm, "end": v(-47.92, -50.5) * mm});
            skPoint(sketch, "E1015.MirrorP", {"position": v(-46.55, -50.8) * mm});
            skArc(sketch, "E1016.MirrorCS", {"start": v(-55.08, -50.94) * mm, "mid": v(-55.05, -50.8) * mm, "end": v(-55.08, -50.66) * mm});
            skLineSegment(sketch, "E1017.MirrorCS", {"start": v(-53.68, -51.1) * mm, "end": v(-53.4, -50.8) * mm});
            skLineSegment(sketch, "E1018.MirrorCS", {"start": v(-55.05, -51.29) * mm, "end": v(-55.05, -50.31) * mm});
            skLineSegment(sketch, "E1019.MirrorCS", {"start": v(-53.4, -50.8) * mm, "end": v(-53.68, -50.5) * mm});
            skLineSegment(sketch, "E1020.MirrorCS", {"start": v(-55.05, -50.8) * mm, "end": v(-54.74, -50.8) * mm});
            skArc(sketch, "E1021.MirrorCS", {"start": v(-54.72, -50.43) * mm, "mid": v(-55.02, -49.96) * mm, "end": v(-55.4, -50.37) * mm});
            skArc(sketch, "E1022.MirrorCS", {"start": v(-55.4, -50.37) * mm, "mid": v(-55.94, -50.8) * mm, "end": v(-55.4, -51.23) * mm});
            skPoint(sketch, "E1023.MirrorP", {"position": v(-55.05, -50.8) * mm});
            skArc(sketch, "E1024.MirrorCS", {"start": v(-54.72, -51.17) * mm, "mid": v(-55.02, -51.64) * mm, "end": v(-55.4, -51.23) * mm});
            skArc(sketch, "E1025.0", {"start": v(-50.58, -48.07) * mm, "mid": v(-50.6, -48.06) * mm, "end": v(-50.63, -48.04) * mm});
            skArc(sketch, "E1026.trimOffspring", {"start": v(-50.63, -53.56) * mm, "mid": v(-50.6, -53.54) * mm, "end": v(-50.58, -53.53) * mm});
            skArc(sketch, "E1027.trimOffspring", {"start": v(-54.83, -50.04) * mm, "mid": v(-54.93, -50.8) * mm, "end": v(-54.83, -51.56) * mm});
            skSolve(sketch);
        }
        {
            var Q0;
            Q0 = qSketchRegion(id + "F68", true);
            var Q1;
            Q1=makeQuery(id+"F63.opExtrude","CAP_FACE",FACE,{"disambiguationData":[OSD([sQuery(id+"F62.wireOp",EDGE,"E819"),sQuery(id+"F62.wireOp",EDGE,"E820.MirrorCS"),sQuery(id+"F62.wireOp",EDGE,"E828"),sQuery(id+"F62.wireOp",EDGE,"E829"),sQuery(id+"F62.wireOp",EDGE,"E830"),sQuery(id+"F62.wireOp",EDGE,"E831.MirrorCS"),sQuery(id+"F62.wireOp",EDGE,"E832.MirrorCS"),sQuery(id+"F62.wireOp",EDGE,"E833.MirrorCS"),sQuery(id+"F62.wireOp",EDGE,"E834"),sQuery(id+"F62.wireOp",EDGE,"E835"),sQuery(id+"F62.wireOp",EDGE,"E836"),sQuery(id+"F62.wireOp",EDGE,"E837"),sQuery(id+"F62.wireOp",EDGE,"E838.MirrorCS"),sQuery(id+"F62.wireOp",EDGE,"E839.MirrorCS"),sQuery(id+"F62.wireOp",EDGE,"E840.MirrorCS"),sQuery(id+"F62.wireOp",EDGE,"E841.MirrorCS"),sQuery(id+"F62.wireOp",EDGE,"E846"),sQuery(id+"F62.wireOp",EDGE,"E855"),sQuery(id+"F62.wireOp",EDGE,"E856.trimOffspring"),sQuery(id+"F62.wireOp",EDGE,"E857.trimOffspring"),sQuery(id+"F62.wireOp",EDGE,"E858.trimOffspring"),sQuery(id+"F62.wireOp",EDGE,"E859.trimOffspring"),sQuery(id+"F62.wireOp",EDGE,"E860"),sQuery(id+"F62.wireOp",EDGE,"E861"),sQuery(id+"F62.wireOp",EDGE,"E862"),sQuery(id+"F62.wireOp",EDGE,"E863"),sQuery(id+"F62.wireOp",EDGE,"E864.MirrorCS"),sQuery(id+"F62.wireOp",EDGE,"E865.MirrorCS"),sQuery(id+"F62.wireOp",EDGE,"E866.MirrorCS"),sQuery(id+"F62.wireOp",EDGE,"E867.MirrorCS")])],"isStart":false});
            extrude(context, id + "F69", {"entities" : qUnion([Q0]), "operationType" : NewBodyOperationType.ADD, "endBound" : BoundingType.UP_TO_SURFACE, "depth" : 25.4 * mm, "endBoundEntityFace" : qUnion([Q1]), "offsetDistance" : 25.4 * mm});
        }
        {
            var Q0;
            Q0=makeQuery(id+"F69.opExtrude","CAP_FACE",FACE,{"disambiguationData":[OSD([sQuery(id+"F68.wireOp",EDGE,"E900"),sQuery(id+"F68.wireOp",EDGE,"E902.top"),sQuery(id+"F68.wireOp",EDGE,"E902.left"),sQuery(id+"F68.wireOp",EDGE,"E902.right"),sQuery(id+"F68.wireOp",EDGE,"E903"),sQuery(id+"F68.wireOp",EDGE,"E904.MirrorCS"),sQuery(id+"F68.wireOp",EDGE,"E905.MirrorCS"),sQuery(id+"F68.wireOp",EDGE,"E906.MirrorCS"),sQuery(id+"F68.wireOp",EDGE,"E907.MirrorCS"),sQuery(id+"F68.wireOp",EDGE,"E908.MirrorCS"),sQuery(id+"F68.wireOp",EDGE,"E909.MirrorCS"),sQuery(id+"F68.wireOp",EDGE,"E910.MirrorCS"),sQuery(id+"F68.wireOp",EDGE,"E911.MirrorCS"),sQuery(id+"F68.wireOp",EDGE,"E912.MirrorCS"),sQuery(id+"F68.wireOp",EDGE,"E913.MirrorCS"),sQuery(id+"F68.wireOp",EDGE,"E914.MirrorCS"),sQuery(id+"F68.wireOp",EDGE,"E915.MirrorCS"),sQuery(id+"F68.wireOp",EDGE,"E916.MirrorCS"),sQuery(id+"F68.wireOp",EDGE,"E917.MirrorCS"),sQuery(id+"F68.wireOp",EDGE,"E918.MirrorCS"),sQuery(id+"F68.wireOp",EDGE,"E919.MirrorCS"),sQuery(id+"F68.wireOp",EDGE,"E920.MirrorCS"),sQuery(id+"F68.wireOp",EDGE,"E921.MirrorCS"),sQuery(id+"F68.wireOp",EDGE,"E922.trimOffspring"),sQuery(id+"F68.wireOp",EDGE,"E923.trimOffspring"),sQuery(id+"F68.wireOp",EDGE,"E924.trimOffspring"),sQuery(id+"F68.wireOp",EDGE,"E925.trimOffspring"),sQuery(id+"F68.wireOp",EDGE,"E926.trimOffspring"),sQuery(id+"F68.wireOp",EDGE,"E927.trimOffspring"),sQuery(id+"F68.wireOp",EDGE,"E928.trimOffspring"),sQuery(id+"F68.wireOp",EDGE,"E929.trimOffspring"),sQuery(id+"F68.wireOp",EDGE,"E930.trimOffspring"),sQuery(id+"F68.wireOp",EDGE,"E931.trimOffspring"),sQuery(id+"F68.wireOp",EDGE,"E933.trimOffspring"),sQuery(id+"F68.wireOp",EDGE,"E934.trimOffspring"),sQuery(id+"F68.wireOp",EDGE,"E935.trimOffspring"),sQuery(id+"F68.wireOp",EDGE,"E936.trimOffspring"),sQuery(id+"F68.wireOp",EDGE,"E937.trimOffspring"),sQuery(id+"F68.wireOp",EDGE,"E938.trimOffspring"),sQuery(id+"F68.wireOp",EDGE,"E939.trimOffspring"),sQuery(id+"F68.wireOp",EDGE,"E940.trimOffspring"),sQuery(id+"F68.wireOp",EDGE,"E941.trimOffspring"),sQuery(id+"F68.wireOp",EDGE,"E942.trimOffspring"),sQuery(id+"F68.wireOp",EDGE,"E943.trimOffspring"),sQuery(id+"F68.wireOp",EDGE,"E944.trimOffspring"),sQuery(id+"F68.wireOp",EDGE,"E945.trimOffspring"),sQuery(id+"F68.wireOp",EDGE,"E946.trimOffspring"),sQuery(id+"F68.wireOp",EDGE,"E947.trimOffspring"),sQuery(id+"F68.wireOp",EDGE,"E948.trimOffspring"),sQuery(id+"F68.wireOp",EDGE,"E949.trimOffspring"),sQuery(id+"F68.wireOp",EDGE,"E950.trimOffspring"),sQuery(id+"F68.wireOp",EDGE,"E951.trimOffspring"),sQuery(id+"F68.wireOp",EDGE,"E952.trimOffspring"),sQuery(id+"F68.wireOp",EDGE,"E953.trimOffspring"),sQuery(id+"F68.wireOp",EDGE,"E954.trimOffspring"),sQuery(id+"F68.wireOp",EDGE,"E955.trimOffspring"),sQuery(id+"F68.wireOp",EDGE,"E956.trimOffspring"),sQuery(id+"F68.wireOp",EDGE,"E957.trimOffspring"),sQuery(id+"F68.wireOp",EDGE,"E958.trimOffspring"),sQuery(id+"F68.wireOp",EDGE,"E959.trimOffspring"),sQuery(id+"F68.wireOp",EDGE,"E960.trimOffspring"),sQuery(id+"F68.wireOp",EDGE,"E961.trimOffspring"),sQuery(id+"F68.wireOp",EDGE,"E962.trimOffspring"),sQuery(id+"F68.wireOp",EDGE,"E963.trimOffspring"),sQuery(id+"F68.wireOp",EDGE,"E964.trimOffspring"),sQuery(id+"F68.wireOp",EDGE,"E965.trimOffspring"),sQuery(id+"F68.wireOp",EDGE,"E966.trimOffspring"),sQuery(id+"F68.wireOp",EDGE,"E967.trimOffspring"),sQuery(id+"F68.wireOp",EDGE,"E968.trimOffspring"),sQuery(id+"F68.wireOp",EDGE,"E969.trimOffspring"),sQuery(id+"F68.wireOp",EDGE,"E970.trimOffspring"),sQuery(id+"F68.wireOp",EDGE,"E971.trimOffspring"),sQuery(id+"F68.wireOp",EDGE,"E972.trimOffspring"),sQuery(id+"F68.wireOp",EDGE,"E973.trimOffspring"),sQuery(id+"F68.wireOp",EDGE,"E974.trimOffspring"),sQuery(id+"F68.wireOp",EDGE,"E975.trimOffspring"),sQuery(id+"F68.wireOp",EDGE,"E976.trimOffspring"),sQuery(id+"F68.wireOp",EDGE,"E977.trimOffspring"),sQuery(id+"F68.wireOp",EDGE,"E978.trimOffspring"),sQuery(id+"F68.wireOp",EDGE,"E979.trimOffspring"),sQuery(id+"F68.wireOp",EDGE,"E901")])],"isStart":false});
            var sketch = newSketch(context, id + "F70", { "sketchPlane" : qUnion([Q0])});
            skLineSegment(sketch, "E1028.bottom", {"start": v(-51.3, -42.56) * mm, "end": v(-50.3, -42.56) * mm});
            skLineSegment(sketch, "E1028.top", {"start": v(-51.3, -41.47) * mm, "end": v(-50.3, -41.47) * mm});
            skLineSegment(sketch, "E1028.left", {"start": v(-51.3, -42.56) * mm, "end": v(-51.3, -41.47) * mm});
            skLineSegment(sketch, "E1028.right", {"start": v(-50.3, -42.56) * mm, "end": v(-50.3, -41.47) * mm});
            skLineSegment(sketch, "E1029", {"start": v(-50.8, -50.8) * mm, "end": v(-48.5, -50.8) * mm});
            skLineSegment(sketch, "E1030", {"start": v(-50.8, -50.8) * mm, "end": v(-48.44, -48.44) * mm});
            skLineSegment(sketch, "E1031.MirrorCS", {"start": v(-42.56, -50.3) * mm, "end": v(-41.47, -50.3) * mm});
            skLineSegment(sketch, "E1032.MirrorCS", {"start": v(-41.47, -51.3) * mm, "end": v(-41.47, -50.3) * mm});
            skLineSegment(sketch, "E1033.MirrorCS", {"start": v(-42.56, -51.3) * mm, "end": v(-41.47, -51.3) * mm});
            skLineSegment(sketch, "E1034.MirrorCS", {"start": v(-42.56, -51.3) * mm, "end": v(-42.56, -50.3) * mm});
            skLineSegment(sketch, "E1035.MirrorCS", {"start": v(-51.3, -59.04) * mm, "end": v(-50.3, -59.04) * mm});
            skLineSegment(sketch, "E1036.MirrorCS", {"start": v(-51.3, -59.04) * mm, "end": v(-51.3, -60.13) * mm});
            skLineSegment(sketch, "E1037.MirrorCS", {"start": v(-51.3, -60.13) * mm, "end": v(-50.3, -60.13) * mm});
            skLineSegment(sketch, "E1038.MirrorCS", {"start": v(-50.3, -59.04) * mm, "end": v(-50.3, -60.13) * mm});
            skLineSegment(sketch, "E1039.MirrorCS", {"start": v(-60.13, -51.3) * mm, "end": v(-60.13, -50.3) * mm});
            skLineSegment(sketch, "E1040.MirrorCS", {"start": v(-59.04, -51.3) * mm, "end": v(-59.04, -50.3) * mm});
            skLineSegment(sketch, "E1041.MirrorCS", {"start": v(-59.04, -51.3) * mm, "end": v(-60.13, -51.3) * mm});
            skLineSegment(sketch, "E1042.MirrorCS", {"start": v(-59.04, -50.3) * mm, "end": v(-60.13, -50.3) * mm});
            skSolve(sketch);
        }
        {
            var Q0;
            Q0 = qSketchRegion(id + "F70", true);
            var Q1;
            {var subQ0=sQuery(id+"F4.wireOp",EDGE,"E8");var subQ1=makeQuery(id+"F5.boolean.opBoolean","COPY",FACE,{"derivedFrom":makeQuery(id+"F5.opExtrude","SWEPT_FACE",FACE,{"disambiguationData":[OSD([subQ0])]})});var subQ2=makeQuery(id+"F5.boolean.opBoolean","COPY",FACE,{"derivedFrom":makeQuery(id+"F5.opExtrude","CAP_FACE",FACE,{"disambiguationData":[OSD([subQ0])],"isStart":false})});Q1=makeQuery(id+"F69.boolean.opBoolean","SPLIT",FACE,{"disambiguationData":[TD([makeQuery(id+"F39.opPattern","COPY",FACE,{"derivedFrom":makeQuery(id+"F19.opPattern","COPY",FACE,{"derivedFrom":makeQuery(id+"F17.opPattern","COPY",FACE,{"derivedFrom":subQ1,"instanceName":"1"}),"instanceName":"1"}),"instanceName":"1"})])],"derivedFrom":makeQuery(id+"F39.opPattern","COPY",FACE,{"derivedFrom":makeQuery(id+"F21.boolean.opBoolean","MERGE",FACE,{"derivedFrom":[makeQuery(id+"F19.opPattern","COPY",FACE,{"derivedFrom":makeQuery(id+"F17.opPattern","COPY",FACE,{"derivedFrom":makeQuery(id+"F9.boolean.opBoolean","SPLIT",FACE,{"disambiguationData":[TD([subQ1])],"derivedFrom":subQ2}),"instanceName":"1"}),"instanceName":"1"}),makeQuery(id+"F19.opPattern","COPY",FACE,{"derivedFrom":makeQuery(id+"F17.opPattern","COPY",FACE,{"derivedFrom":makeQuery(id+"F9.boolean.opBoolean","SPLIT",FACE,{"disambiguationData":[TD([makeQuery(id+"F9.opExtrude","SWEPT_FACE",FACE,{"disambiguationData":[OSD([sQuery(id+"F8.wireOp",EDGE,"E25")])]})])],"derivedFrom":subQ2}),"instanceName":"1"}),"instanceName":"1"}),makeQuery(id+"F19.opPattern","COPY",FACE,{"derivedFrom":makeQuery(id+"F17.opPattern","COPY",FACE,{"derivedFrom":makeQuery(id+"F9.boolean.opBoolean","SPLIT",FACE,{"disambiguationData":[TD([makeQuery(id+"F9.opExtrude","SWEPT_FACE",FACE,{"disambiguationData":[OSD([sQuery(id+"F8.wireOp",EDGE,"E32")])]})])],"derivedFrom":subQ2}),"instanceName":"1"}),"instanceName":"1"}),makeQuery(id+"F19.opPattern","COPY",FACE,{"derivedFrom":makeQuery(id+"F17.opPattern","COPY",FACE,{"derivedFrom":makeQuery(id+"F9.boolean.opBoolean","SPLIT",FACE,{"disambiguationData":[TD([makeQuery(id+"F9.opExtrude","SWEPT_FACE",FACE,{"disambiguationData":[OSD([sQuery(id+"F8.wireOp",EDGE,"E33.0")])]})])],"derivedFrom":subQ2}),"instanceName":"1"}),"instanceName":"1"}),makeQuery(id+"F19.opPattern","COPY",FACE,{"derivedFrom":makeQuery(id+"F17.opPattern","COPY",FACE,{"derivedFrom":makeQuery(id+"F9.boolean.opBoolean","SPLIT",FACE,{"disambiguationData":[TD([makeQuery(id+"F9.opExtrude","SWEPT_FACE",FACE,{"disambiguationData":[OSD([sQuery(id+"F8.wireOp",EDGE,"E37")])]})])],"derivedFrom":subQ2}),"instanceName":"1"}),"instanceName":"1"}),makeQuery(id+"F19.opPattern","COPY",FACE,{"derivedFrom":makeQuery(id+"F17.opPattern","COPY",FACE,{"derivedFrom":makeQuery(id+"F9.boolean.opBoolean","SPLIT",FACE,{"disambiguationData":[TD([makeQuery(id+"F9.opExtrude","SWEPT_FACE",FACE,{"disambiguationData":[OSD([sQuery(id+"F8.wireOp",EDGE,"E51.MirrorCS")])]})])],"derivedFrom":subQ2}),"instanceName":"1"}),"instanceName":"1"}),makeQuery(id+"F19.opPattern","COPY",FACE,{"derivedFrom":makeQuery(id+"F17.opPattern","COPY",FACE,{"derivedFrom":makeQuery(id+"F9.boolean.opBoolean","SPLIT",FACE,{"disambiguationData":[TD([makeQuery(id+"F9.opExtrude","SWEPT_FACE",FACE,{"disambiguationData":[OSD([sQuery(id+"F8.wireOp",EDGE,"E53.MirrorCS")])]})])],"derivedFrom":subQ2}),"instanceName":"1"}),"instanceName":"1"}),makeQuery(id+"F19.opPattern","COPY",FACE,{"derivedFrom":makeQuery(id+"F17.opPattern","COPY",FACE,{"derivedFrom":makeQuery(id+"F9.boolean.opBoolean","SPLIT",FACE,{"disambiguationData":[TD([makeQuery(id+"F9.opExtrude","SWEPT_FACE",FACE,{"disambiguationData":[OSD([sQuery(id+"F8.wireOp",EDGE,"E80")])]})])],"derivedFrom":subQ2}),"instanceName":"1"}),"instanceName":"1"}),makeQuery(id+"F19.opPattern","COPY",FACE,{"derivedFrom":makeQuery(id+"F17.opPattern","COPY",FACE,{"derivedFrom":makeQuery(id+"F9.boolean.opBoolean","SPLIT",FACE,{"disambiguationData":[TD([makeQuery(id+"F9.opExtrude","SWEPT_FACE",FACE,{"disambiguationData":[OSD([sQuery(id+"F8.wireOp",EDGE,"E83")])]})])],"derivedFrom":subQ2}),"instanceName":"1"}),"instanceName":"1"})],"fromTools":[makeQuery(id+"F21.opExtrude","CAP_FACE",FACE,{"disambiguationData":[OSD([sQuery(id+"F20.wireOp",EDGE,"E309.0.0")])],"isStart":false})]}),"instanceName":"1"})});}
            extrude(context, id + "F71", {"entities" : qUnion([Q0]), "operationType" : NewBodyOperationType.ADD, "endBound" : BoundingType.UP_TO_SURFACE, "oppositeDirection" : true, "depth" : 25.4 * mm, "endBoundEntityFace" : qUnion([Q1]), "offsetDistance" : 25.4 * mm});
        }
        {
            var Q0;
            Q0=makeQuery(id+"F71.boolean.opBoolean","MERGE",FACE,{"derivedFrom":[makeQuery(id+"F69.opExtrude","CAP_FACE",FACE,{"disambiguationData":[OSD([sQuery(id+"F68.wireOp",EDGE,"E900"),sQuery(id+"F68.wireOp",EDGE,"E902.top"),sQuery(id+"F68.wireOp",EDGE,"E902.left"),sQuery(id+"F68.wireOp",EDGE,"E902.right"),sQuery(id+"F68.wireOp",EDGE,"E903"),sQuery(id+"F68.wireOp",EDGE,"E904.MirrorCS"),sQuery(id+"F68.wireOp",EDGE,"E905.MirrorCS"),sQuery(id+"F68.wireOp",EDGE,"E906.MirrorCS"),sQuery(id+"F68.wireOp",EDGE,"E907.MirrorCS"),sQuery(id+"F68.wireOp",EDGE,"E908.MirrorCS"),sQuery(id+"F68.wireOp",EDGE,"E909.MirrorCS"),sQuery(id+"F68.wireOp",EDGE,"E910.MirrorCS"),sQuery(id+"F68.wireOp",EDGE,"E911.MirrorCS"),sQuery(id+"F68.wireOp",EDGE,"E912.MirrorCS"),sQuery(id+"F68.wireOp",EDGE,"E913.MirrorCS"),sQuery(id+"F68.wireOp",EDGE,"E914.MirrorCS"),sQuery(id+"F68.wireOp",EDGE,"E915.MirrorCS"),sQuery(id+"F68.wireOp",EDGE,"E916.MirrorCS"),sQuery(id+"F68.wireOp",EDGE,"E917.MirrorCS"),sQuery(id+"F68.wireOp",EDGE,"E918.MirrorCS"),sQuery(id+"F68.wireOp",EDGE,"E919.MirrorCS"),sQuery(id+"F68.wireOp",EDGE,"E920.MirrorCS"),sQuery(id+"F68.wireOp",EDGE,"E921.MirrorCS"),sQuery(id+"F68.wireOp",EDGE,"E922.trimOffspring"),sQuery(id+"F68.wireOp",EDGE,"E923.trimOffspring"),sQuery(id+"F68.wireOp",EDGE,"E924.trimOffspring"),sQuery(id+"F68.wireOp",EDGE,"E925.trimOffspring"),sQuery(id+"F68.wireOp",EDGE,"E926.trimOffspring"),sQuery(id+"F68.wireOp",EDGE,"E927.trimOffspring"),sQuery(id+"F68.wireOp",EDGE,"E928.trimOffspring"),sQuery(id+"F68.wireOp",EDGE,"E929.trimOffspring"),sQuery(id+"F68.wireOp",EDGE,"E930.trimOffspring"),sQuery(id+"F68.wireOp",EDGE,"E931.trimOffspring"),sQuery(id+"F68.wireOp",EDGE,"E933.trimOffspring"),sQuery(id+"F68.wireOp",EDGE,"E934.trimOffspring"),sQuery(id+"F68.wireOp",EDGE,"E935.trimOffspring"),sQuery(id+"F68.wireOp",EDGE,"E936.trimOffspring"),sQuery(id+"F68.wireOp",EDGE,"E937.trimOffspring"),sQuery(id+"F68.wireOp",EDGE,"E938.trimOffspring"),sQuery(id+"F68.wireOp",EDGE,"E939.trimOffspring"),sQuery(id+"F68.wireOp",EDGE,"E940.trimOffspring"),sQuery(id+"F68.wireOp",EDGE,"E941.trimOffspring"),sQuery(id+"F68.wireOp",EDGE,"E942.trimOffspring"),sQuery(id+"F68.wireOp",EDGE,"E943.trimOffspring"),sQuery(id+"F68.wireOp",EDGE,"E944.trimOffspring"),sQuery(id+"F68.wireOp",EDGE,"E945.trimOffspring"),sQuery(id+"F68.wireOp",EDGE,"E946.trimOffspring"),sQuery(id+"F68.wireOp",EDGE,"E947.trimOffspring"),sQuery(id+"F68.wireOp",EDGE,"E948.trimOffspring"),sQuery(id+"F68.wireOp",EDGE,"E949.trimOffspring"),sQuery(id+"F68.wireOp",EDGE,"E950.trimOffspring"),sQuery(id+"F68.wireOp",EDGE,"E951.trimOffspring"),sQuery(id+"F68.wireOp",EDGE,"E952.trimOffspring"),sQuery(id+"F68.wireOp",EDGE,"E953.trimOffspring"),sQuery(id+"F68.wireOp",EDGE,"E954.trimOffspring"),sQuery(id+"F68.wireOp",EDGE,"E955.trimOffspring"),sQuery(id+"F68.wireOp",EDGE,"E956.trimOffspring"),sQuery(id+"F68.wireOp",EDGE,"E957.trimOffspring"),sQuery(id+"F68.wireOp",EDGE,"E958.trimOffspring"),sQuery(id+"F68.wireOp",EDGE,"E959.trimOffspring"),sQuery(id+"F68.wireOp",EDGE,"E960.trimOffspring"),sQuery(id+"F68.wireOp",EDGE,"E961.trimOffspring"),sQuery(id+"F68.wireOp",EDGE,"E962.trimOffspring"),sQuery(id+"F68.wireOp",EDGE,"E963.trimOffspring"),sQuery(id+"F68.wireOp",EDGE,"E964.trimOffspring"),sQuery(id+"F68.wireOp",EDGE,"E965.trimOffspring"),sQuery(id+"F68.wireOp",EDGE,"E966.trimOffspring"),sQuery(id+"F68.wireOp",EDGE,"E967.trimOffspring"),sQuery(id+"F68.wireOp",EDGE,"E968.trimOffspring"),sQuery(id+"F68.wireOp",EDGE,"E969.trimOffspring"),sQuery(id+"F68.wireOp",EDGE,"E970.trimOffspring"),sQuery(id+"F68.wireOp",EDGE,"E971.trimOffspring"),sQuery(id+"F68.wireOp",EDGE,"E972.trimOffspring"),sQuery(id+"F68.wireOp",EDGE,"E973.trimOffspring"),sQuery(id+"F68.wireOp",EDGE,"E974.trimOffspring"),sQuery(id+"F68.wireOp",EDGE,"E975.trimOffspring"),sQuery(id+"F68.wireOp",EDGE,"E976.trimOffspring"),sQuery(id+"F68.wireOp",EDGE,"E977.trimOffspring"),sQuery(id+"F68.wireOp",EDGE,"E978.trimOffspring"),sQuery(id+"F68.wireOp",EDGE,"E979.trimOffspring"),sQuery(id+"F68.wireOp",EDGE,"E901")])],"isStart":false}),makeQuery(id+"F71.opExtrude","CAP_FACE",FACE,{"disambiguationData":[OSD([sQuery(id+"F70.wireOp",EDGE,"E1028.bottom"),sQuery(id+"F70.wireOp",EDGE,"E1028.top"),sQuery(id+"F70.wireOp",EDGE,"E1028.left"),sQuery(id+"F70.wireOp",EDGE,"E1028.right")])],"isStart":true}),makeQuery(id+"F71.opExtrude","CAP_FACE",FACE,{"disambiguationData":[OSD([sQuery(id+"F70.wireOp",EDGE,"E1031.MirrorCS"),sQuery(id+"F70.wireOp",EDGE,"E1032.MirrorCS"),sQuery(id+"F70.wireOp",EDGE,"E1033.MirrorCS"),sQuery(id+"F70.wireOp",EDGE,"E1034.MirrorCS")])],"isStart":true}),makeQuery(id+"F71.opExtrude","CAP_FACE",FACE,{"disambiguationData":[OSD([sQuery(id+"F70.wireOp",EDGE,"E1035.MirrorCS"),sQuery(id+"F70.wireOp",EDGE,"E1036.MirrorCS"),sQuery(id+"F70.wireOp",EDGE,"E1037.MirrorCS"),sQuery(id+"F70.wireOp",EDGE,"E1038.MirrorCS")])],"isStart":true}),makeQuery(id+"F71.opExtrude","CAP_FACE",FACE,{"disambiguationData":[OSD([sQuery(id+"F70.wireOp",EDGE,"E1039.MirrorCS"),sQuery(id+"F70.wireOp",EDGE,"E1040.MirrorCS"),sQuery(id+"F70.wireOp",EDGE,"E1041.MirrorCS"),sQuery(id+"F70.wireOp",EDGE,"E1042.MirrorCS")])],"isStart":true})]});
            var sketch = newSketch(context, id + "F72", { "sketchPlane" : qUnion([Q0])});
            skLineSegment(sketch, "E1043", {"start": v(-51.77, -56.94) * mm, "end": v(-50.8, -50.8) * mm});
            skLineSegment(sketch, "E1044.0", {"start": v(-51.3, -57) * mm, "end": v(-51.3, -60.13) * mm});
            skLineSegment(sketch, "E1045.0", {"start": v(-50.3, -57) * mm, "end": v(-50.3, -60.13) * mm});
            skLineSegment(sketch, "E1046", {"start": v(-50.8, -50.8) * mm, "end": v(-50.8, -52.9) * mm});
            skLineSegment(sketch, "E1047.MirrorCS", {"start": v(-52.24, -56.85) * mm, "end": v(-53.2, -59.83) * mm});
            skLineSegment(sketch, "E1048.MirrorCS", {"start": v(-53.2, -56.54) * mm, "end": v(-54.16, -59.52) * mm});
            skLineSegment(sketch, "E1049.MirrorCS", {"start": v(-49.36, -56.85) * mm, "end": v(-48.4, -59.83) * mm});
            skLineSegment(sketch, "E1050.MirrorCS", {"start": v(-48.4, -56.54) * mm, "end": v(-47.44, -59.52) * mm});
            skLineSegment(sketch, "E1051", {"start": v(-54.16, -59.52) * mm, "end": v(-53.2, -59.83) * mm});
            skLineSegment(sketch, "E1052", {"start": v(-52.24, -56.85) * mm, "end": v(-53.2, -56.54) * mm});
            skLineSegment(sketch, "E1053", {"start": v(-48.4, -59.83) * mm, "end": v(-47.44, -59.52) * mm});
            skLineSegment(sketch, "E1054", {"start": v(-49.36, -56.85) * mm, "end": v(-48.4, -56.54) * mm});
            skSolve(sketch);
        }
        {
            var Q0;
            Q0 = qSketchRegion(id + "F72", true);
            var Q1;
            {var subQ0=sQuery(id+"F4.wireOp",EDGE,"E8");var subQ1=makeQuery(id+"F5.boolean.opBoolean","COPY",FACE,{"derivedFrom":makeQuery(id+"F5.opExtrude","SWEPT_FACE",FACE,{"disambiguationData":[OSD([subQ0])]})});var subQ2=makeQuery(id+"F5.boolean.opBoolean","COPY",FACE,{"derivedFrom":makeQuery(id+"F5.opExtrude","CAP_FACE",FACE,{"disambiguationData":[OSD([subQ0])],"isStart":false})});Q1=makeQuery(id+"F69.boolean.opBoolean","SPLIT",FACE,{"disambiguationData":[TD([makeQuery(id+"F39.opPattern","COPY",FACE,{"derivedFrom":makeQuery(id+"F19.opPattern","COPY",FACE,{"derivedFrom":makeQuery(id+"F17.opPattern","COPY",FACE,{"derivedFrom":subQ1,"instanceName":"1"}),"instanceName":"1"}),"instanceName":"1"})])],"derivedFrom":makeQuery(id+"F39.opPattern","COPY",FACE,{"derivedFrom":makeQuery(id+"F21.boolean.opBoolean","MERGE",FACE,{"derivedFrom":[makeQuery(id+"F19.opPattern","COPY",FACE,{"derivedFrom":makeQuery(id+"F17.opPattern","COPY",FACE,{"derivedFrom":makeQuery(id+"F9.boolean.opBoolean","SPLIT",FACE,{"disambiguationData":[TD([subQ1])],"derivedFrom":subQ2}),"instanceName":"1"}),"instanceName":"1"}),makeQuery(id+"F19.opPattern","COPY",FACE,{"derivedFrom":makeQuery(id+"F17.opPattern","COPY",FACE,{"derivedFrom":makeQuery(id+"F9.boolean.opBoolean","SPLIT",FACE,{"disambiguationData":[TD([makeQuery(id+"F9.opExtrude","SWEPT_FACE",FACE,{"disambiguationData":[OSD([sQuery(id+"F8.wireOp",EDGE,"E25")])]})])],"derivedFrom":subQ2}),"instanceName":"1"}),"instanceName":"1"}),makeQuery(id+"F19.opPattern","COPY",FACE,{"derivedFrom":makeQuery(id+"F17.opPattern","COPY",FACE,{"derivedFrom":makeQuery(id+"F9.boolean.opBoolean","SPLIT",FACE,{"disambiguationData":[TD([makeQuery(id+"F9.opExtrude","SWEPT_FACE",FACE,{"disambiguationData":[OSD([sQuery(id+"F8.wireOp",EDGE,"E32")])]})])],"derivedFrom":subQ2}),"instanceName":"1"}),"instanceName":"1"}),makeQuery(id+"F19.opPattern","COPY",FACE,{"derivedFrom":makeQuery(id+"F17.opPattern","COPY",FACE,{"derivedFrom":makeQuery(id+"F9.boolean.opBoolean","SPLIT",FACE,{"disambiguationData":[TD([makeQuery(id+"F9.opExtrude","SWEPT_FACE",FACE,{"disambiguationData":[OSD([sQuery(id+"F8.wireOp",EDGE,"E33.0")])]})])],"derivedFrom":subQ2}),"instanceName":"1"}),"instanceName":"1"}),makeQuery(id+"F19.opPattern","COPY",FACE,{"derivedFrom":makeQuery(id+"F17.opPattern","COPY",FACE,{"derivedFrom":makeQuery(id+"F9.boolean.opBoolean","SPLIT",FACE,{"disambiguationData":[TD([makeQuery(id+"F9.opExtrude","SWEPT_FACE",FACE,{"disambiguationData":[OSD([sQuery(id+"F8.wireOp",EDGE,"E37")])]})])],"derivedFrom":subQ2}),"instanceName":"1"}),"instanceName":"1"}),makeQuery(id+"F19.opPattern","COPY",FACE,{"derivedFrom":makeQuery(id+"F17.opPattern","COPY",FACE,{"derivedFrom":makeQuery(id+"F9.boolean.opBoolean","SPLIT",FACE,{"disambiguationData":[TD([makeQuery(id+"F9.opExtrude","SWEPT_FACE",FACE,{"disambiguationData":[OSD([sQuery(id+"F8.wireOp",EDGE,"E51.MirrorCS")])]})])],"derivedFrom":subQ2}),"instanceName":"1"}),"instanceName":"1"}),makeQuery(id+"F19.opPattern","COPY",FACE,{"derivedFrom":makeQuery(id+"F17.opPattern","COPY",FACE,{"derivedFrom":makeQuery(id+"F9.boolean.opBoolean","SPLIT",FACE,{"disambiguationData":[TD([makeQuery(id+"F9.opExtrude","SWEPT_FACE",FACE,{"disambiguationData":[OSD([sQuery(id+"F8.wireOp",EDGE,"E53.MirrorCS")])]})])],"derivedFrom":subQ2}),"instanceName":"1"}),"instanceName":"1"}),makeQuery(id+"F19.opPattern","COPY",FACE,{"derivedFrom":makeQuery(id+"F17.opPattern","COPY",FACE,{"derivedFrom":makeQuery(id+"F9.boolean.opBoolean","SPLIT",FACE,{"disambiguationData":[TD([makeQuery(id+"F9.opExtrude","SWEPT_FACE",FACE,{"disambiguationData":[OSD([sQuery(id+"F8.wireOp",EDGE,"E80")])]})])],"derivedFrom":subQ2}),"instanceName":"1"}),"instanceName":"1"}),makeQuery(id+"F19.opPattern","COPY",FACE,{"derivedFrom":makeQuery(id+"F17.opPattern","COPY",FACE,{"derivedFrom":makeQuery(id+"F9.boolean.opBoolean","SPLIT",FACE,{"disambiguationData":[TD([makeQuery(id+"F9.opExtrude","SWEPT_FACE",FACE,{"disambiguationData":[OSD([sQuery(id+"F8.wireOp",EDGE,"E83")])]})])],"derivedFrom":subQ2}),"instanceName":"1"}),"instanceName":"1"})],"fromTools":[makeQuery(id+"F21.opExtrude","CAP_FACE",FACE,{"disambiguationData":[OSD([sQuery(id+"F20.wireOp",EDGE,"E309.0.0")])],"isStart":false})]}),"instanceName":"1"})});}
            extrude(context, id + "F73", {"entities" : qUnion([Q0]), "operationType" : NewBodyOperationType.ADD, "endBound" : BoundingType.UP_TO_SURFACE, "oppositeDirection" : true, "depth" : 25.4 * mm, "endBoundEntityFace" : qUnion([Q1]), "offsetDistance" : 25.4 * mm});
        }
        {
            var Q0;
            Q0=makeQuery(id+"F73.boolean.opBoolean","MERGE",FACE,{"derivedFrom":[makeQuery(id+"F71.boolean.opBoolean","MERGE",FACE,{"derivedFrom":[makeQuery(id+"F69.opExtrude","CAP_FACE",FACE,{"disambiguationData":[OSD([sQuery(id+"F68.wireOp",EDGE,"E900"),sQuery(id+"F68.wireOp",EDGE,"E902.top"),sQuery(id+"F68.wireOp",EDGE,"E902.left"),sQuery(id+"F68.wireOp",EDGE,"E902.right"),sQuery(id+"F68.wireOp",EDGE,"E903"),sQuery(id+"F68.wireOp",EDGE,"E904.MirrorCS"),sQuery(id+"F68.wireOp",EDGE,"E905.MirrorCS"),sQuery(id+"F68.wireOp",EDGE,"E906.MirrorCS"),sQuery(id+"F68.wireOp",EDGE,"E907.MirrorCS"),sQuery(id+"F68.wireOp",EDGE,"E908.MirrorCS"),sQuery(id+"F68.wireOp",EDGE,"E909.MirrorCS"),sQuery(id+"F68.wireOp",EDGE,"E910.MirrorCS"),sQuery(id+"F68.wireOp",EDGE,"E911.MirrorCS"),sQuery(id+"F68.wireOp",EDGE,"E912.MirrorCS"),sQuery(id+"F68.wireOp",EDGE,"E913.MirrorCS"),sQuery(id+"F68.wireOp",EDGE,"E914.MirrorCS"),sQuery(id+"F68.wireOp",EDGE,"E915.MirrorCS"),sQuery(id+"F68.wireOp",EDGE,"E916.MirrorCS"),sQuery(id+"F68.wireOp",EDGE,"E917.MirrorCS"),sQuery(id+"F68.wireOp",EDGE,"E918.MirrorCS"),sQuery(id+"F68.wireOp",EDGE,"E919.MirrorCS"),sQuery(id+"F68.wireOp",EDGE,"E920.MirrorCS"),sQuery(id+"F68.wireOp",EDGE,"E921.MirrorCS"),sQuery(id+"F68.wireOp",EDGE,"E922.trimOffspring"),sQuery(id+"F68.wireOp",EDGE,"E923.trimOffspring"),sQuery(id+"F68.wireOp",EDGE,"E924.trimOffspring"),sQuery(id+"F68.wireOp",EDGE,"E925.trimOffspring"),sQuery(id+"F68.wireOp",EDGE,"E926.trimOffspring"),sQuery(id+"F68.wireOp",EDGE,"E927.trimOffspring"),sQuery(id+"F68.wireOp",EDGE,"E928.trimOffspring"),sQuery(id+"F68.wireOp",EDGE,"E929.trimOffspring"),sQuery(id+"F68.wireOp",EDGE,"E930.trimOffspring"),sQuery(id+"F68.wireOp",EDGE,"E931.trimOffspring"),sQuery(id+"F68.wireOp",EDGE,"E933.trimOffspring"),sQuery(id+"F68.wireOp",EDGE,"E934.trimOffspring"),sQuery(id+"F68.wireOp",EDGE,"E935.trimOffspring"),sQuery(id+"F68.wireOp",EDGE,"E936.trimOffspring"),sQuery(id+"F68.wireOp",EDGE,"E937.trimOffspring"),sQuery(id+"F68.wireOp",EDGE,"E938.trimOffspring"),sQuery(id+"F68.wireOp",EDGE,"E939.trimOffspring"),sQuery(id+"F68.wireOp",EDGE,"E940.trimOffspring"),sQuery(id+"F68.wireOp",EDGE,"E941.trimOffspring"),sQuery(id+"F68.wireOp",EDGE,"E942.trimOffspring"),sQuery(id+"F68.wireOp",EDGE,"E943.trimOffspring"),sQuery(id+"F68.wireOp",EDGE,"E944.trimOffspring"),sQuery(id+"F68.wireOp",EDGE,"E945.trimOffspring"),sQuery(id+"F68.wireOp",EDGE,"E946.trimOffspring"),sQuery(id+"F68.wireOp",EDGE,"E947.trimOffspring"),sQuery(id+"F68.wireOp",EDGE,"E948.trimOffspring"),sQuery(id+"F68.wireOp",EDGE,"E949.trimOffspring"),sQuery(id+"F68.wireOp",EDGE,"E950.trimOffspring"),sQuery(id+"F68.wireOp",EDGE,"E951.trimOffspring"),sQuery(id+"F68.wireOp",EDGE,"E952.trimOffspring"),sQuery(id+"F68.wireOp",EDGE,"E953.trimOffspring"),sQuery(id+"F68.wireOp",EDGE,"E954.trimOffspring"),sQuery(id+"F68.wireOp",EDGE,"E955.trimOffspring"),sQuery(id+"F68.wireOp",EDGE,"E956.trimOffspring"),sQuery(id+"F68.wireOp",EDGE,"E957.trimOffspring"),sQuery(id+"F68.wireOp",EDGE,"E958.trimOffspring"),sQuery(id+"F68.wireOp",EDGE,"E959.trimOffspring"),sQuery(id+"F68.wireOp",EDGE,"E960.trimOffspring"),sQuery(id+"F68.wireOp",EDGE,"E961.trimOffspring"),sQuery(id+"F68.wireOp",EDGE,"E962.trimOffspring"),sQuery(id+"F68.wireOp",EDGE,"E963.trimOffspring"),sQuery(id+"F68.wireOp",EDGE,"E964.trimOffspring"),sQuery(id+"F68.wireOp",EDGE,"E965.trimOffspring"),sQuery(id+"F68.wireOp",EDGE,"E966.trimOffspring"),sQuery(id+"F68.wireOp",EDGE,"E967.trimOffspring"),sQuery(id+"F68.wireOp",EDGE,"E968.trimOffspring"),sQuery(id+"F68.wireOp",EDGE,"E969.trimOffspring"),sQuery(id+"F68.wireOp",EDGE,"E970.trimOffspring"),sQuery(id+"F68.wireOp",EDGE,"E971.trimOffspring"),sQuery(id+"F68.wireOp",EDGE,"E972.trimOffspring"),sQuery(id+"F68.wireOp",EDGE,"E973.trimOffspring"),sQuery(id+"F68.wireOp",EDGE,"E974.trimOffspring"),sQuery(id+"F68.wireOp",EDGE,"E975.trimOffspring"),sQuery(id+"F68.wireOp",EDGE,"E976.trimOffspring"),sQuery(id+"F68.wireOp",EDGE,"E977.trimOffspring"),sQuery(id+"F68.wireOp",EDGE,"E978.trimOffspring"),sQuery(id+"F68.wireOp",EDGE,"E979.trimOffspring"),sQuery(id+"F68.wireOp",EDGE,"E901")])],"isStart":false}),makeQuery(id+"F71.opExtrude","CAP_FACE",FACE,{"disambiguationData":[OSD([sQuery(id+"F70.wireOp",EDGE,"E1028.bottom"),sQuery(id+"F70.wireOp",EDGE,"E1028.top"),sQuery(id+"F70.wireOp",EDGE,"E1028.left"),sQuery(id+"F70.wireOp",EDGE,"E1028.right")])],"isStart":true}),makeQuery(id+"F71.opExtrude","CAP_FACE",FACE,{"disambiguationData":[OSD([sQuery(id+"F70.wireOp",EDGE,"E1031.MirrorCS"),sQuery(id+"F70.wireOp",EDGE,"E1032.MirrorCS"),sQuery(id+"F70.wireOp",EDGE,"E1033.MirrorCS"),sQuery(id+"F70.wireOp",EDGE,"E1034.MirrorCS")])],"isStart":true}),makeQuery(id+"F71.opExtrude","CAP_FACE",FACE,{"disambiguationData":[OSD([sQuery(id+"F70.wireOp",EDGE,"E1035.MirrorCS"),sQuery(id+"F70.wireOp",EDGE,"E1036.MirrorCS"),sQuery(id+"F70.wireOp",EDGE,"E1037.MirrorCS"),sQuery(id+"F70.wireOp",EDGE,"E1038.MirrorCS")])],"isStart":true}),makeQuery(id+"F71.opExtrude","CAP_FACE",FACE,{"disambiguationData":[OSD([sQuery(id+"F70.wireOp",EDGE,"E1039.MirrorCS"),sQuery(id+"F70.wireOp",EDGE,"E1040.MirrorCS"),sQuery(id+"F70.wireOp",EDGE,"E1041.MirrorCS"),sQuery(id+"F70.wireOp",EDGE,"E1042.MirrorCS")])],"isStart":true})]}),makeQuery(id+"F73.opExtrude","CAP_FACE",FACE,{"disambiguationData":[OSD([sQuery(id+"F72.wireOp",EDGE,"E1047.MirrorCS"),sQuery(id+"F72.wireOp",EDGE,"E1048.MirrorCS"),sQuery(id+"F72.wireOp",EDGE,"E1051"),sQuery(id+"F72.wireOp",EDGE,"E1052")])],"isStart":true}),makeQuery(id+"F73.opExtrude","CAP_FACE",FACE,{"disambiguationData":[OSD([sQuery(id+"F72.wireOp",EDGE,"E1049.MirrorCS"),sQuery(id+"F72.wireOp",EDGE,"E1050.MirrorCS"),sQuery(id+"F72.wireOp",EDGE,"E1053"),sQuery(id+"F72.wireOp",EDGE,"E1054")])],"isStart":true})]});
            var sketch = newSketch(context, id + "F74", { "sketchPlane" : qUnion([Q0])});
            skLineSegment(sketch, "E1055.0", {"start": v(-52.24, -56.85) * mm, "end": v(-53.2, -59.83) * mm});
            skLineSegment(sketch, "E1056.0", {"start": v(-49.36, -56.85) * mm, "end": v(-48.4, -59.83) * mm});
            skArc(sketch, "E1057.0", {"start": v(-51.97, -56.01) * mm, "mid": v(-50.8, -56.14) * mm, "end": v(-49.63, -56.01) * mm});
            skLineSegment(sketch, "E1058", {"start": v(-49.36, -56.85) * mm, "end": v(-49.76, -55.61) * mm});
            skLineSegment(sketch, "E1059", {"start": v(-52.24, -56.85) * mm, "end": v(-51.84, -55.63) * mm});
            skLineSegment(sketch, "E1060.0", {"start": v(-51.3, -60.13) * mm, "end": v(-50.3, -60.13) * mm});
            skLineSegment(sketch, "E1061", {"start": v(-50.3, -60.13) * mm, "end": v(-48.4, -59.83) * mm});
            skLineSegment(sketch, "E1062", {"start": v(-51.3, -60.13) * mm, "end": v(-53.2, -59.83) * mm});
            skSolve(sketch);
        }
        {
            var Q0;
            Q0 = qSketchRegion(id + "F74", true);
            var Q1;
            {var subQ0=sQuery(id+"F4.wireOp",EDGE,"E8");var subQ1=makeQuery(id+"F5.boolean.opBoolean","COPY",FACE,{"derivedFrom":makeQuery(id+"F5.opExtrude","SWEPT_FACE",FACE,{"disambiguationData":[OSD([subQ0])]})});var subQ2=makeQuery(id+"F5.boolean.opBoolean","COPY",FACE,{"derivedFrom":makeQuery(id+"F5.opExtrude","CAP_FACE",FACE,{"disambiguationData":[OSD([subQ0])],"isStart":false})});Q1=makeQuery(id+"F69.boolean.opBoolean","SPLIT",FACE,{"disambiguationData":[TD([makeQuery(id+"F39.opPattern","COPY",FACE,{"derivedFrom":makeQuery(id+"F19.opPattern","COPY",FACE,{"derivedFrom":makeQuery(id+"F17.opPattern","COPY",FACE,{"derivedFrom":subQ1,"instanceName":"1"}),"instanceName":"1"}),"instanceName":"1"})])],"derivedFrom":makeQuery(id+"F39.opPattern","COPY",FACE,{"derivedFrom":makeQuery(id+"F21.boolean.opBoolean","MERGE",FACE,{"derivedFrom":[makeQuery(id+"F19.opPattern","COPY",FACE,{"derivedFrom":makeQuery(id+"F17.opPattern","COPY",FACE,{"derivedFrom":makeQuery(id+"F9.boolean.opBoolean","SPLIT",FACE,{"disambiguationData":[TD([subQ1])],"derivedFrom":subQ2}),"instanceName":"1"}),"instanceName":"1"}),makeQuery(id+"F19.opPattern","COPY",FACE,{"derivedFrom":makeQuery(id+"F17.opPattern","COPY",FACE,{"derivedFrom":makeQuery(id+"F9.boolean.opBoolean","SPLIT",FACE,{"disambiguationData":[TD([makeQuery(id+"F9.opExtrude","SWEPT_FACE",FACE,{"disambiguationData":[OSD([sQuery(id+"F8.wireOp",EDGE,"E25")])]})])],"derivedFrom":subQ2}),"instanceName":"1"}),"instanceName":"1"}),makeQuery(id+"F19.opPattern","COPY",FACE,{"derivedFrom":makeQuery(id+"F17.opPattern","COPY",FACE,{"derivedFrom":makeQuery(id+"F9.boolean.opBoolean","SPLIT",FACE,{"disambiguationData":[TD([makeQuery(id+"F9.opExtrude","SWEPT_FACE",FACE,{"disambiguationData":[OSD([sQuery(id+"F8.wireOp",EDGE,"E32")])]})])],"derivedFrom":subQ2}),"instanceName":"1"}),"instanceName":"1"}),makeQuery(id+"F19.opPattern","COPY",FACE,{"derivedFrom":makeQuery(id+"F17.opPattern","COPY",FACE,{"derivedFrom":makeQuery(id+"F9.boolean.opBoolean","SPLIT",FACE,{"disambiguationData":[TD([makeQuery(id+"F9.opExtrude","SWEPT_FACE",FACE,{"disambiguationData":[OSD([sQuery(id+"F8.wireOp",EDGE,"E33.0")])]})])],"derivedFrom":subQ2}),"instanceName":"1"}),"instanceName":"1"}),makeQuery(id+"F19.opPattern","COPY",FACE,{"derivedFrom":makeQuery(id+"F17.opPattern","COPY",FACE,{"derivedFrom":makeQuery(id+"F9.boolean.opBoolean","SPLIT",FACE,{"disambiguationData":[TD([makeQuery(id+"F9.opExtrude","SWEPT_FACE",FACE,{"disambiguationData":[OSD([sQuery(id+"F8.wireOp",EDGE,"E37")])]})])],"derivedFrom":subQ2}),"instanceName":"1"}),"instanceName":"1"}),makeQuery(id+"F19.opPattern","COPY",FACE,{"derivedFrom":makeQuery(id+"F17.opPattern","COPY",FACE,{"derivedFrom":makeQuery(id+"F9.boolean.opBoolean","SPLIT",FACE,{"disambiguationData":[TD([makeQuery(id+"F9.opExtrude","SWEPT_FACE",FACE,{"disambiguationData":[OSD([sQuery(id+"F8.wireOp",EDGE,"E51.MirrorCS")])]})])],"derivedFrom":subQ2}),"instanceName":"1"}),"instanceName":"1"}),makeQuery(id+"F19.opPattern","COPY",FACE,{"derivedFrom":makeQuery(id+"F17.opPattern","COPY",FACE,{"derivedFrom":makeQuery(id+"F9.boolean.opBoolean","SPLIT",FACE,{"disambiguationData":[TD([makeQuery(id+"F9.opExtrude","SWEPT_FACE",FACE,{"disambiguationData":[OSD([sQuery(id+"F8.wireOp",EDGE,"E53.MirrorCS")])]})])],"derivedFrom":subQ2}),"instanceName":"1"}),"instanceName":"1"}),makeQuery(id+"F19.opPattern","COPY",FACE,{"derivedFrom":makeQuery(id+"F17.opPattern","COPY",FACE,{"derivedFrom":makeQuery(id+"F9.boolean.opBoolean","SPLIT",FACE,{"disambiguationData":[TD([makeQuery(id+"F9.opExtrude","SWEPT_FACE",FACE,{"disambiguationData":[OSD([sQuery(id+"F8.wireOp",EDGE,"E80")])]})])],"derivedFrom":subQ2}),"instanceName":"1"}),"instanceName":"1"}),makeQuery(id+"F19.opPattern","COPY",FACE,{"derivedFrom":makeQuery(id+"F17.opPattern","COPY",FACE,{"derivedFrom":makeQuery(id+"F9.boolean.opBoolean","SPLIT",FACE,{"disambiguationData":[TD([makeQuery(id+"F9.opExtrude","SWEPT_FACE",FACE,{"disambiguationData":[OSD([sQuery(id+"F8.wireOp",EDGE,"E83")])]})])],"derivedFrom":subQ2}),"instanceName":"1"}),"instanceName":"1"})],"fromTools":[makeQuery(id+"F21.opExtrude","CAP_FACE",FACE,{"disambiguationData":[OSD([sQuery(id+"F20.wireOp",EDGE,"E309.0.0")])],"isStart":false})]}),"instanceName":"1"})});}
            extrude(context, id + "F75", {"entities" : qUnion([Q0]), "operationType" : NewBodyOperationType.REMOVE, "endBound" : BoundingType.UP_TO_SURFACE, "oppositeDirection" : true, "depth" : 25.4 * mm, "endBoundEntityFace" : qUnion([Q1]), "offsetDistance" : 25.4 * mm});
        }
        {
            var Q0;
            {var subQ0=sQuery(id+"F4.wireOp",EDGE,"E8");var subQ1=makeQuery(id+"F5.boolean.opBoolean","COPY",FACE,{"derivedFrom":makeQuery(id+"F5.opExtrude","CAP_FACE",FACE,{"disambiguationData":[OSD([subQ0])],"isStart":false})});Q0=makeQuery(id+"F39.opPattern","COPY",FACE,{"derivedFrom":makeQuery(id+"F21.boolean.opBoolean","MERGE",FACE,{"derivedFrom":[makeQuery(id+"F19.opPattern","COPY",FACE,{"derivedFrom":makeQuery(id+"F9.boolean.opBoolean","SPLIT",FACE,{"disambiguationData":[TD([makeQuery(id+"F5.boolean.opBoolean","COPY",FACE,{"derivedFrom":makeQuery(id+"F5.opExtrude","SWEPT_FACE",FACE,{"disambiguationData":[OSD([subQ0])]})})])],"derivedFrom":subQ1}),"instanceName":"1"}),makeQuery(id+"F19.opPattern","COPY",FACE,{"derivedFrom":makeQuery(id+"F9.boolean.opBoolean","SPLIT",FACE,{"disambiguationData":[TD([makeQuery(id+"F9.opExtrude","SWEPT_FACE",FACE,{"disambiguationData":[OSD([sQuery(id+"F8.wireOp",EDGE,"E25")])]})])],"derivedFrom":subQ1}),"instanceName":"1"}),makeQuery(id+"F19.opPattern","COPY",FACE,{"derivedFrom":makeQuery(id+"F9.boolean.opBoolean","SPLIT",FACE,{"disambiguationData":[TD([makeQuery(id+"F9.opExtrude","SWEPT_FACE",FACE,{"disambiguationData":[OSD([sQuery(id+"F8.wireOp",EDGE,"E32")])]})])],"derivedFrom":subQ1}),"instanceName":"1"}),makeQuery(id+"F19.opPattern","COPY",FACE,{"derivedFrom":makeQuery(id+"F9.boolean.opBoolean","SPLIT",FACE,{"disambiguationData":[TD([makeQuery(id+"F9.opExtrude","SWEPT_FACE",FACE,{"disambiguationData":[OSD([sQuery(id+"F8.wireOp",EDGE,"E33.0")])]})])],"derivedFrom":subQ1}),"instanceName":"1"}),makeQuery(id+"F19.opPattern","COPY",FACE,{"derivedFrom":makeQuery(id+"F9.boolean.opBoolean","SPLIT",FACE,{"disambiguationData":[TD([makeQuery(id+"F9.opExtrude","SWEPT_FACE",FACE,{"disambiguationData":[OSD([sQuery(id+"F8.wireOp",EDGE,"E37")])]})])],"derivedFrom":subQ1}),"instanceName":"1"}),makeQuery(id+"F19.opPattern","COPY",FACE,{"derivedFrom":makeQuery(id+"F9.boolean.opBoolean","SPLIT",FACE,{"disambiguationData":[TD([makeQuery(id+"F9.opExtrude","SWEPT_FACE",FACE,{"disambiguationData":[OSD([sQuery(id+"F8.wireOp",EDGE,"E51.MirrorCS")])]})])],"derivedFrom":subQ1}),"instanceName":"1"}),makeQuery(id+"F19.opPattern","COPY",FACE,{"derivedFrom":makeQuery(id+"F9.boolean.opBoolean","SPLIT",FACE,{"disambiguationData":[TD([makeQuery(id+"F9.opExtrude","SWEPT_FACE",FACE,{"disambiguationData":[OSD([sQuery(id+"F8.wireOp",EDGE,"E53.MirrorCS")])]})])],"derivedFrom":subQ1}),"instanceName":"1"}),makeQuery(id+"F19.opPattern","COPY",FACE,{"derivedFrom":makeQuery(id+"F9.boolean.opBoolean","SPLIT",FACE,{"disambiguationData":[TD([makeQuery(id+"F9.opExtrude","SWEPT_FACE",FACE,{"disambiguationData":[OSD([sQuery(id+"F8.wireOp",EDGE,"E80")])]})])],"derivedFrom":subQ1}),"instanceName":"1"}),makeQuery(id+"F19.opPattern","COPY",FACE,{"derivedFrom":makeQuery(id+"F9.boolean.opBoolean","SPLIT",FACE,{"disambiguationData":[TD([makeQuery(id+"F9.opExtrude","SWEPT_FACE",FACE,{"disambiguationData":[OSD([sQuery(id+"F8.wireOp",EDGE,"E83")])]})])],"derivedFrom":subQ1}),"instanceName":"1"}),makeQuery(id+"F21.opExtrude","CAP_FACE",FACE,{"disambiguationData":[OSD([sQuery(id+"F20.wireOp",EDGE,"E308.0.0")])],"isStart":false})]}),"instanceName":"1"});}
            var sketch = newSketch(context, id + "F76", { "sketchPlane" : qUnion([Q0])});
            skCircle(sketch, "E1063", {"center": v(0, -54.5) * mm, "radius": 4.6 * mm});
            skArc(sketch, "E1064", {"start": v(-0.27, -52.99) * mm, "mid": v(-1.08, -53.41) * mm, "end": v(-1.5, -54.22) * mm});
            skArc(sketch, "E1065", {"start": v(-0.9, -50.9) * mm, "mid": v(-2.62, -51.88) * mm, "end": v(-3.59, -53.58) * mm});
            skArc(sketch, "E1066", {"start": v(-0.9, -50.9) * mm, "mid": v(-0.7, -51.39) * mm, "end": v(-0.27, -51.68) * mm});
            skArc(sketch, "E1067.MirrorC", {"start": v(-0.9, -58.08) * mm, "mid": v(-0.7, -57.6) * mm, "end": v(-0.27, -57.3) * mm});
            skArc(sketch, "E1068.MirrorC", {"start": v(3.59, -55.4) * mm, "mid": v(3.1, -55.2) * mm, "end": v(2.81, -54.76) * mm});
            skArc(sketch, "E1069.MirrorC", {"start": v(-3.59, -55.4) * mm, "mid": v(-3.1, -55.2) * mm, "end": v(-2.81, -54.76) * mm});
            skArc(sketch, "E1070.trimOffspring", {"start": v(-3.59, -55.4) * mm, "mid": v(-2.62, -57.1) * mm, "end": v(-0.9, -58.08) * mm});
            skArc(sketch, "E1071.trimOffspring", {"start": v(0.9, -58.08) * mm, "mid": v(2.62, -57.1) * mm, "end": v(3.59, -55.4) * mm});
            skArc(sketch, "E1072.trimOffspring", {"start": v(3.59, -53.58) * mm, "mid": v(2.62, -51.88) * mm, "end": v(0.9, -50.9) * mm});
            skCircle(sketch, "E1073", {"center": v(0, -50.8) * mm, "radius": 0.53 * mm});
            skLineSegment(sketch, "E1074.bottom", {"start": v(2.81, -54.76) * mm, "end": v(1.5, -54.76) * mm});
            skLineSegment(sketch, "E1074.top", {"start": v(2.81, -54.22) * mm, "end": v(1.5, -54.22) * mm});
            skLineSegment(sketch, "E1075.trimOffspring", {"start": v(-1.5, -54.22) * mm, "end": v(-2.81, -54.22) * mm});
            skLineSegment(sketch, "E1076.trimOffspring", {"start": v(-1.5, -54.76) * mm, "end": v(-2.81, -54.76) * mm});
            skPoint(sketch, "E1077.orphan", {"position": v(-4, -54.22) * mm});
            skPoint(sketch, "E1078.orphan", {"position": v(-4, -54.76) * mm});
            skPoint(sketch, "E1079.orphan", {"position": v(4, -54.76) * mm});
            skPoint(sketch, "E1080.orphan", {"position": v(4, -54.22) * mm});
            skLineSegment(sketch, "E1081.MirrorCS", {"start": v(0.27, -51.68) * mm, "end": v(0.27, -52.99) * mm});
            skLineSegment(sketch, "E1082.MirrorCS", {"start": v(-0.27, -51.68) * mm, "end": v(-0.27, -52.99) * mm});
            skLineSegment(sketch, "E1083.MirrorCS", {"start": v(0.27, -56) * mm, "end": v(0.27, -57.3) * mm});
            skLineSegment(sketch, "E1084.MirrorCS", {"start": v(-0.27, -56) * mm, "end": v(-0.27, -57.3) * mm});
            skCircle(sketch, "E1085.MirrorC", {"center": v(0, -58.18) * mm, "radius": 0.53 * mm});
            skCircle(sketch, "E1086.MirrorC", {"center": v(3.7, -54.5) * mm, "radius": 0.53 * mm});
            skCircle(sketch, "E1087.MirrorC", {"center": v(-3.7, -54.5) * mm, "radius": 0.53 * mm});
            skArc(sketch, "E1088.trimOffspring", {"start": v(0.27, -51.68) * mm, "mid": v(0.7, -51.39) * mm, "end": v(0.9, -50.9) * mm});
            skArc(sketch, "E1089.trimOffspring", {"start": v(1.5, -54.22) * mm, "mid": v(1.08, -53.41) * mm, "end": v(0.27, -52.99) * mm});
            skArc(sketch, "E1090.trimOffspring", {"start": v(2.81, -54.22) * mm, "mid": v(3.1, -53.79) * mm, "end": v(3.59, -53.58) * mm});
            skArc(sketch, "E1091.trimOffspring", {"start": v(0.27, -56) * mm, "mid": v(1.08, -55.57) * mm, "end": v(1.5, -54.76) * mm});
            skArc(sketch, "E1092.trimOffspring", {"start": v(-2.81, -54.22) * mm, "mid": v(-3.1, -53.79) * mm, "end": v(-3.59, -53.58) * mm});
            skArc(sketch, "E1093.trimOffspring", {"start": v(-1.5, -54.76) * mm, "mid": v(-1.08, -55.57) * mm, "end": v(-0.27, -56) * mm});
            skArc(sketch, "E1094.trimOffspring", {"start": v(0.27, -57.3) * mm, "mid": v(0.7, -57.6) * mm, "end": v(0.9, -58.08) * mm});
            skCircle(sketch, "E1095", {"center": v(0, -54.5) * mm, "radius": 0.9 * mm});
            skSolve(sketch);
        }
        {
            var Q0;
            Q0 = qSketchRegion(id + "F76", true);
            var Q1;
            Q1=makeQuery(id+"F73.boolean.opBoolean","MERGE",FACE,{"derivedFrom":[makeQuery(id+"F71.boolean.opBoolean","MERGE",FACE,{"derivedFrom":[makeQuery(id+"F69.opExtrude","CAP_FACE",FACE,{"disambiguationData":[OSD([sQuery(id+"F68.wireOp",EDGE,"E900"),sQuery(id+"F68.wireOp",EDGE,"E902.top"),sQuery(id+"F68.wireOp",EDGE,"E902.left"),sQuery(id+"F68.wireOp",EDGE,"E902.right"),sQuery(id+"F68.wireOp",EDGE,"E903"),sQuery(id+"F68.wireOp",EDGE,"E904.MirrorCS"),sQuery(id+"F68.wireOp",EDGE,"E905.MirrorCS"),sQuery(id+"F68.wireOp",EDGE,"E906.MirrorCS"),sQuery(id+"F68.wireOp",EDGE,"E907.MirrorCS"),sQuery(id+"F68.wireOp",EDGE,"E908.MirrorCS"),sQuery(id+"F68.wireOp",EDGE,"E909.MirrorCS"),sQuery(id+"F68.wireOp",EDGE,"E910.MirrorCS"),sQuery(id+"F68.wireOp",EDGE,"E911.MirrorCS"),sQuery(id+"F68.wireOp",EDGE,"E912.MirrorCS"),sQuery(id+"F68.wireOp",EDGE,"E913.MirrorCS"),sQuery(id+"F68.wireOp",EDGE,"E914.MirrorCS"),sQuery(id+"F68.wireOp",EDGE,"E915.MirrorCS"),sQuery(id+"F68.wireOp",EDGE,"E916.MirrorCS"),sQuery(id+"F68.wireOp",EDGE,"E917.MirrorCS"),sQuery(id+"F68.wireOp",EDGE,"E918.MirrorCS"),sQuery(id+"F68.wireOp",EDGE,"E919.MirrorCS"),sQuery(id+"F68.wireOp",EDGE,"E920.MirrorCS"),sQuery(id+"F68.wireOp",EDGE,"E921.MirrorCS"),sQuery(id+"F68.wireOp",EDGE,"E922.trimOffspring"),sQuery(id+"F68.wireOp",EDGE,"E923.trimOffspring"),sQuery(id+"F68.wireOp",EDGE,"E924.trimOffspring"),sQuery(id+"F68.wireOp",EDGE,"E925.trimOffspring"),sQuery(id+"F68.wireOp",EDGE,"E926.trimOffspring"),sQuery(id+"F68.wireOp",EDGE,"E927.trimOffspring"),sQuery(id+"F68.wireOp",EDGE,"E928.trimOffspring"),sQuery(id+"F68.wireOp",EDGE,"E929.trimOffspring"),sQuery(id+"F68.wireOp",EDGE,"E930.trimOffspring"),sQuery(id+"F68.wireOp",EDGE,"E931.trimOffspring"),sQuery(id+"F68.wireOp",EDGE,"E933.trimOffspring"),sQuery(id+"F68.wireOp",EDGE,"E934.trimOffspring"),sQuery(id+"F68.wireOp",EDGE,"E935.trimOffspring"),sQuery(id+"F68.wireOp",EDGE,"E936.trimOffspring"),sQuery(id+"F68.wireOp",EDGE,"E937.trimOffspring"),sQuery(id+"F68.wireOp",EDGE,"E938.trimOffspring"),sQuery(id+"F68.wireOp",EDGE,"E939.trimOffspring"),sQuery(id+"F68.wireOp",EDGE,"E940.trimOffspring"),sQuery(id+"F68.wireOp",EDGE,"E941.trimOffspring"),sQuery(id+"F68.wireOp",EDGE,"E942.trimOffspring"),sQuery(id+"F68.wireOp",EDGE,"E943.trimOffspring"),sQuery(id+"F68.wireOp",EDGE,"E944.trimOffspring"),sQuery(id+"F68.wireOp",EDGE,"E945.trimOffspring"),sQuery(id+"F68.wireOp",EDGE,"E946.trimOffspring"),sQuery(id+"F68.wireOp",EDGE,"E947.trimOffspring"),sQuery(id+"F68.wireOp",EDGE,"E948.trimOffspring"),sQuery(id+"F68.wireOp",EDGE,"E949.trimOffspring"),sQuery(id+"F68.wireOp",EDGE,"E950.trimOffspring"),sQuery(id+"F68.wireOp",EDGE,"E951.trimOffspring"),sQuery(id+"F68.wireOp",EDGE,"E952.trimOffspring"),sQuery(id+"F68.wireOp",EDGE,"E953.trimOffspring"),sQuery(id+"F68.wireOp",EDGE,"E954.trimOffspring"),sQuery(id+"F68.wireOp",EDGE,"E955.trimOffspring"),sQuery(id+"F68.wireOp",EDGE,"E956.trimOffspring"),sQuery(id+"F68.wireOp",EDGE,"E957.trimOffspring"),sQuery(id+"F68.wireOp",EDGE,"E958.trimOffspring"),sQuery(id+"F68.wireOp",EDGE,"E959.trimOffspring"),sQuery(id+"F68.wireOp",EDGE,"E960.trimOffspring"),sQuery(id+"F68.wireOp",EDGE,"E961.trimOffspring"),sQuery(id+"F68.wireOp",EDGE,"E962.trimOffspring"),sQuery(id+"F68.wireOp",EDGE,"E963.trimOffspring"),sQuery(id+"F68.wireOp",EDGE,"E964.trimOffspring"),sQuery(id+"F68.wireOp",EDGE,"E965.trimOffspring"),sQuery(id+"F68.wireOp",EDGE,"E966.trimOffspring"),sQuery(id+"F68.wireOp",EDGE,"E967.trimOffspring"),sQuery(id+"F68.wireOp",EDGE,"E968.trimOffspring"),sQuery(id+"F68.wireOp",EDGE,"E969.trimOffspring"),sQuery(id+"F68.wireOp",EDGE,"E970.trimOffspring"),sQuery(id+"F68.wireOp",EDGE,"E971.trimOffspring"),sQuery(id+"F68.wireOp",EDGE,"E972.trimOffspring"),sQuery(id+"F68.wireOp",EDGE,"E973.trimOffspring"),sQuery(id+"F68.wireOp",EDGE,"E974.trimOffspring"),sQuery(id+"F68.wireOp",EDGE,"E975.trimOffspring"),sQuery(id+"F68.wireOp",EDGE,"E976.trimOffspring"),sQuery(id+"F68.wireOp",EDGE,"E977.trimOffspring"),sQuery(id+"F68.wireOp",EDGE,"E978.trimOffspring"),sQuery(id+"F68.wireOp",EDGE,"E979.trimOffspring"),sQuery(id+"F68.wireOp",EDGE,"E901")])],"isStart":false}),makeQuery(id+"F71.opExtrude","CAP_FACE",FACE,{"disambiguationData":[OSD([sQuery(id+"F70.wireOp",EDGE,"E1028.bottom"),sQuery(id+"F70.wireOp",EDGE,"E1028.top"),sQuery(id+"F70.wireOp",EDGE,"E1028.left"),sQuery(id+"F70.wireOp",EDGE,"E1028.right")])],"isStart":true}),makeQuery(id+"F71.opExtrude","CAP_FACE",FACE,{"disambiguationData":[OSD([sQuery(id+"F70.wireOp",EDGE,"E1031.MirrorCS"),sQuery(id+"F70.wireOp",EDGE,"E1032.MirrorCS"),sQuery(id+"F70.wireOp",EDGE,"E1033.MirrorCS"),sQuery(id+"F70.wireOp",EDGE,"E1034.MirrorCS")])],"isStart":true}),makeQuery(id+"F71.opExtrude","CAP_FACE",FACE,{"disambiguationData":[OSD([sQuery(id+"F70.wireOp",EDGE,"E1035.MirrorCS"),sQuery(id+"F70.wireOp",EDGE,"E1036.MirrorCS"),sQuery(id+"F70.wireOp",EDGE,"E1037.MirrorCS"),sQuery(id+"F70.wireOp",EDGE,"E1038.MirrorCS")])],"isStart":true}),makeQuery(id+"F71.opExtrude","CAP_FACE",FACE,{"disambiguationData":[OSD([sQuery(id+"F70.wireOp",EDGE,"E1039.MirrorCS"),sQuery(id+"F70.wireOp",EDGE,"E1040.MirrorCS"),sQuery(id+"F70.wireOp",EDGE,"E1041.MirrorCS"),sQuery(id+"F70.wireOp",EDGE,"E1042.MirrorCS")])],"isStart":true})]}),makeQuery(id+"F73.opExtrude","CAP_FACE",FACE,{"disambiguationData":[OSD([sQuery(id+"F72.wireOp",EDGE,"E1047.MirrorCS"),sQuery(id+"F72.wireOp",EDGE,"E1048.MirrorCS"),sQuery(id+"F72.wireOp",EDGE,"E1051"),sQuery(id+"F72.wireOp",EDGE,"E1052")])],"isStart":true}),makeQuery(id+"F73.opExtrude","CAP_FACE",FACE,{"disambiguationData":[OSD([sQuery(id+"F72.wireOp",EDGE,"E1049.MirrorCS"),sQuery(id+"F72.wireOp",EDGE,"E1050.MirrorCS"),sQuery(id+"F72.wireOp",EDGE,"E1053"),sQuery(id+"F72.wireOp",EDGE,"E1054")])],"isStart":true})]});
            extrude(context, id + "F77", {"entities" : qUnion([Q0]), "operationType" : NewBodyOperationType.ADD, "endBound" : BoundingType.UP_TO_SURFACE, "depth" : 25.4 * mm, "endBoundEntityFace" : qUnion([Q1]), "offsetDistance" : 25.4 * mm});
        }
        {
            var Q0;
            {var subQ0=sQuery(id+"F4.wireOp",EDGE,"E8");var subQ1=makeQuery(id+"F5.boolean.opBoolean","COPY",FACE,{"derivedFrom":makeQuery(id+"F5.opExtrude","SWEPT_FACE",FACE,{"disambiguationData":[OSD([subQ0])]})});var subQ2=makeQuery(id+"F5.boolean.opBoolean","COPY",FACE,{"derivedFrom":makeQuery(id+"F5.opExtrude","CAP_FACE",FACE,{"disambiguationData":[OSD([subQ0])],"isStart":false})});Q0=makeQuery(id+"F77.boolean.opBoolean","SPLIT",FACE,{"disambiguationData":[TD([makeQuery(id+"F39.opPattern","COPY",FACE,{"derivedFrom":makeQuery(id+"F19.opPattern","COPY",FACE,{"derivedFrom":subQ1,"instanceName":"1"}),"instanceName":"1"})])],"derivedFrom":makeQuery(id+"F39.opPattern","COPY",FACE,{"derivedFrom":makeQuery(id+"F21.boolean.opBoolean","MERGE",FACE,{"derivedFrom":[makeQuery(id+"F19.opPattern","COPY",FACE,{"derivedFrom":makeQuery(id+"F9.boolean.opBoolean","SPLIT",FACE,{"disambiguationData":[TD([subQ1])],"derivedFrom":subQ2}),"instanceName":"1"}),makeQuery(id+"F19.opPattern","COPY",FACE,{"derivedFrom":makeQuery(id+"F9.boolean.opBoolean","SPLIT",FACE,{"disambiguationData":[TD([makeQuery(id+"F9.opExtrude","SWEPT_FACE",FACE,{"disambiguationData":[OSD([sQuery(id+"F8.wireOp",EDGE,"E25")])]})])],"derivedFrom":subQ2}),"instanceName":"1"}),makeQuery(id+"F19.opPattern","COPY",FACE,{"derivedFrom":makeQuery(id+"F9.boolean.opBoolean","SPLIT",FACE,{"disambiguationData":[TD([makeQuery(id+"F9.opExtrude","SWEPT_FACE",FACE,{"disambiguationData":[OSD([sQuery(id+"F8.wireOp",EDGE,"E32")])]})])],"derivedFrom":subQ2}),"instanceName":"1"}),makeQuery(id+"F19.opPattern","COPY",FACE,{"derivedFrom":makeQuery(id+"F9.boolean.opBoolean","SPLIT",FACE,{"disambiguationData":[TD([makeQuery(id+"F9.opExtrude","SWEPT_FACE",FACE,{"disambiguationData":[OSD([sQuery(id+"F8.wireOp",EDGE,"E33.0")])]})])],"derivedFrom":subQ2}),"instanceName":"1"}),makeQuery(id+"F19.opPattern","COPY",FACE,{"derivedFrom":makeQuery(id+"F9.boolean.opBoolean","SPLIT",FACE,{"disambiguationData":[TD([makeQuery(id+"F9.opExtrude","SWEPT_FACE",FACE,{"disambiguationData":[OSD([sQuery(id+"F8.wireOp",EDGE,"E37")])]})])],"derivedFrom":subQ2}),"instanceName":"1"}),makeQuery(id+"F19.opPattern","COPY",FACE,{"derivedFrom":makeQuery(id+"F9.boolean.opBoolean","SPLIT",FACE,{"disambiguationData":[TD([makeQuery(id+"F9.opExtrude","SWEPT_FACE",FACE,{"disambiguationData":[OSD([sQuery(id+"F8.wireOp",EDGE,"E51.MirrorCS")])]})])],"derivedFrom":subQ2}),"instanceName":"1"}),makeQuery(id+"F19.opPattern","COPY",FACE,{"derivedFrom":makeQuery(id+"F9.boolean.opBoolean","SPLIT",FACE,{"disambiguationData":[TD([makeQuery(id+"F9.opExtrude","SWEPT_FACE",FACE,{"disambiguationData":[OSD([sQuery(id+"F8.wireOp",EDGE,"E53.MirrorCS")])]})])],"derivedFrom":subQ2}),"instanceName":"1"}),makeQuery(id+"F19.opPattern","COPY",FACE,{"derivedFrom":makeQuery(id+"F9.boolean.opBoolean","SPLIT",FACE,{"disambiguationData":[TD([makeQuery(id+"F9.opExtrude","SWEPT_FACE",FACE,{"disambiguationData":[OSD([sQuery(id+"F8.wireOp",EDGE,"E80")])]})])],"derivedFrom":subQ2}),"instanceName":"1"}),makeQuery(id+"F19.opPattern","COPY",FACE,{"derivedFrom":makeQuery(id+"F9.boolean.opBoolean","SPLIT",FACE,{"disambiguationData":[TD([makeQuery(id+"F9.opExtrude","SWEPT_FACE",FACE,{"disambiguationData":[OSD([sQuery(id+"F8.wireOp",EDGE,"E83")])]})])],"derivedFrom":subQ2}),"instanceName":"1"})],"fromTools":[makeQuery(id+"F21.opExtrude","CAP_FACE",FACE,{"disambiguationData":[OSD([sQuery(id+"F20.wireOp",EDGE,"E308.0.0")])],"isStart":false})]}),"instanceName":"1"})});}
            var sketch = newSketch(context, id + "F78", { "sketchPlane" : qUnion([Q0])});
            skArc(sketch, "E1096", {"start": v(-2.67, -46.06) * mm, "mid": v(-3.53, -47.42) * mm, "end": v(-2.14, -48.23) * mm});
            skArc(sketch, "E1097", {"start": v(-2.67, -46.06) * mm, "mid": v(-0.87, -44.52) * mm, "end": v(0, -42.32) * mm});
            skArc(sketch, "E1098.0", {"start": v(-2.45, -46.5) * mm, "mid": v(-1.56, -45.95) * mm, "end": v(-0.8, -45.23) * mm});
            skArc(sketch, "E1099", {"start": v(-0.96, -49.98) * mm, "mid": v(-1.3, -48.93) * mm, "end": v(-2.14, -48.23) * mm});
            skArc(sketch, "E1100.0", {"start": v(-0.46, -49.97) * mm, "mid": v(-0.88, -48.65) * mm, "end": v(-1.95, -47.77) * mm});
            skArc(sketch, "E1101.0", {"start": v(0.96, -49.98) * mm, "mid": v(0.7, -49.94) * mm, "end": v(0.46, -49.9) * mm});
            skArc(sketch, "E1102.MirrorC", {"start": v(1.64, -47.93) * mm, "mid": v(1.33, -47) * mm, "end": v(1.89, -46.18) * mm});
            skArc(sketch, "E1103.MirrorCS", {"start": v(2.45, -46.5) * mm, "mid": v(1.56, -45.95) * mm, "end": v(0.8, -45.23) * mm});
            skArc(sketch, "E1104.MirrorCS", {"start": v(2.67, -46.06) * mm, "mid": v(0.87, -44.52) * mm, "end": v(0, -42.32) * mm});
            skArc(sketch, "E1105.MirrorCS", {"start": v(0.46, -49.97) * mm, "mid": v(0.88, -48.65) * mm, "end": v(1.95, -47.77) * mm});
            skArc(sketch, "E1106.MirrorCS", {"start": v(0.96, -49.98) * mm, "mid": v(1.3, -48.93) * mm, "end": v(2.14, -48.23) * mm});
            skArc(sketch, "E1107.trimOffspring", {"start": v(-0.46, -49.9) * mm, "mid": v(-0.7, -49.94) * mm, "end": v(-0.96, -49.98) * mm});
            skArc(sketch, "E1108.trimOffspring", {"start": v(2.67, -46.06) * mm, "mid": v(3.53, -47.42) * mm, "end": v(2.14, -48.23) * mm});
            skArc(sketch, "E1109.trimOffspring", {"start": v(-1.64, -47.93) * mm, "mid": v(-1.33, -47) * mm, "end": v(-1.89, -46.18) * mm});
            skArc(sketch, "E1110.trimOffspring", {"start": v(0.12, -44.26) * mm, "mid": v(-0.27, -43.36) * mm, "end": v(-0.5, -42.4) * mm});
            skArc(sketch, "E1111.trimOffspring", {"start": v(-0.12, -44.26) * mm, "mid": v(0.27, -43.36) * mm, "end": v(0.5, -42.4) * mm});
            skCircle(sketch, "E1112", {"center": v(-2.44, -47.15) * mm, "radius": 0.65 * mm});
            skCircle(sketch, "E1113", {"center": v(2.44, -47.15) * mm, "radius": 0.65 * mm});
            skArc(sketch, "E1114", {"start": v(-0.5, -42.4) * mm, "mid": v(0.47, -44.81) * mm, "end": v(2.45, -46.5) * mm});
            skArc(sketch, "E1115", {"start": v(-2.45, -46.5) * mm, "mid": v(-0.47, -44.81) * mm, "end": v(0.5, -42.4) * mm});
            skCircle(sketch, "E1116", {"center": v(0, -46.58) * mm, "radius": 1.29 * mm});
            skSolve(sketch);
        }
        {
            var Q0;
            Q0 = qSketchRegion(id + "F78", true);
            var Q1;
            Q1=makeQuery(id+"F77.opExtrude","CAP_FACE",FACE,{"disambiguationData":[OSD([sQuery(id+"F76.wireOp",EDGE,"E1063"),sQuery(id+"F76.wireOp",EDGE,"E1064"),sQuery(id+"F76.wireOp",EDGE,"E1065"),sQuery(id+"F76.wireOp",EDGE,"E1066"),sQuery(id+"F76.wireOp",EDGE,"E1067.MirrorC"),sQuery(id+"F76.wireOp",EDGE,"E1068.MirrorC"),sQuery(id+"F76.wireOp",EDGE,"E1069.MirrorC"),sQuery(id+"F76.wireOp",EDGE,"E1070.trimOffspring"),sQuery(id+"F76.wireOp",EDGE,"E1071.trimOffspring"),sQuery(id+"F76.wireOp",EDGE,"E1072.trimOffspring"),sQuery(id+"F76.wireOp",EDGE,"E1073"),sQuery(id+"F76.wireOp",EDGE,"E1074.bottom"),sQuery(id+"F76.wireOp",EDGE,"E1074.top"),sQuery(id+"F76.wireOp",EDGE,"E1075.trimOffspring"),sQuery(id+"F76.wireOp",EDGE,"E1076.trimOffspring"),sQuery(id+"F76.wireOp",EDGE,"E1081.MirrorCS"),sQuery(id+"F76.wireOp",EDGE,"E1082.MirrorCS"),sQuery(id+"F76.wireOp",EDGE,"E1083.MirrorCS"),sQuery(id+"F76.wireOp",EDGE,"E1084.MirrorCS"),sQuery(id+"F76.wireOp",EDGE,"E1085.MirrorC"),sQuery(id+"F76.wireOp",EDGE,"E1086.MirrorC"),sQuery(id+"F76.wireOp",EDGE,"E1087.MirrorC"),sQuery(id+"F76.wireOp",EDGE,"E1088.trimOffspring"),sQuery(id+"F76.wireOp",EDGE,"E1089.trimOffspring"),sQuery(id+"F76.wireOp",EDGE,"E1090.trimOffspring"),sQuery(id+"F76.wireOp",EDGE,"E1091.trimOffspring"),sQuery(id+"F76.wireOp",EDGE,"E1092.trimOffspring"),sQuery(id+"F76.wireOp",EDGE,"E1093.trimOffspring"),sQuery(id+"F76.wireOp",EDGE,"E1094.trimOffspring"),sQuery(id+"F76.wireOp",EDGE,"E1095")])],"isStart":false});
            extrude(context, id + "F79", {"entities" : qUnion([Q0]), "operationType" : NewBodyOperationType.ADD, "endBound" : BoundingType.UP_TO_SURFACE, "depth" : 25.4 * mm, "endBoundEntityFace" : qUnion([Q1]), "offsetDistance" : 25.4 * mm});
        }
        {
            var Q0;
            {var subQ1=sQuery(id+"F4.wireOp",EDGE,"E8");var subQ2=makeQuery(id+"F5.boolean.opBoolean","COPY",FACE,{"derivedFrom":makeQuery(id+"F5.opExtrude","SWEPT_FACE",FACE,{"disambiguationData":[OSD([subQ1])]})});var subQ3=makeQuery(id+"F39.opPattern","COPY",FACE,{"derivedFrom":makeQuery(id+"F19.opPattern","COPY",FACE,{"derivedFrom":subQ2,"instanceName":"1"}),"instanceName":"1"});var subQ4=makeQuery(id+"F5.boolean.opBoolean","COPY",FACE,{"derivedFrom":makeQuery(id+"F5.opExtrude","CAP_FACE",FACE,{"disambiguationData":[OSD([subQ1])],"isStart":false})});Q0=makeQuery(id+"F79.boolean.opBoolean","SPLIT",FACE,{"disambiguationData":[TD([subQ3])],"derivedFrom":makeQuery(id+"F77.boolean.opBoolean","SPLIT",FACE,{"disambiguationData":[TD([subQ3])],"derivedFrom":makeQuery(id+"F39.opPattern","COPY",FACE,{"derivedFrom":makeQuery(id+"F21.boolean.opBoolean","MERGE",FACE,{"derivedFrom":[makeQuery(id+"F19.opPattern","COPY",FACE,{"derivedFrom":makeQuery(id+"F9.boolean.opBoolean","SPLIT",FACE,{"disambiguationData":[TD([subQ2])],"derivedFrom":subQ4}),"instanceName":"1"}),makeQuery(id+"F19.opPattern","COPY",FACE,{"derivedFrom":makeQuery(id+"F9.boolean.opBoolean","SPLIT",FACE,{"disambiguationData":[TD([makeQuery(id+"F9.opExtrude","SWEPT_FACE",FACE,{"disambiguationData":[OSD([sQuery(id+"F8.wireOp",EDGE,"E25")])]})])],"derivedFrom":subQ4}),"instanceName":"1"}),makeQuery(id+"F19.opPattern","COPY",FACE,{"derivedFrom":makeQuery(id+"F9.boolean.opBoolean","SPLIT",FACE,{"disambiguationData":[TD([makeQuery(id+"F9.opExtrude","SWEPT_FACE",FACE,{"disambiguationData":[OSD([sQuery(id+"F8.wireOp",EDGE,"E32")])]})])],"derivedFrom":subQ4}),"instanceName":"1"}),makeQuery(id+"F19.opPattern","COPY",FACE,{"derivedFrom":makeQuery(id+"F9.boolean.opBoolean","SPLIT",FACE,{"disambiguationData":[TD([makeQuery(id+"F9.opExtrude","SWEPT_FACE",FACE,{"disambiguationData":[OSD([sQuery(id+"F8.wireOp",EDGE,"E33.0")])]})])],"derivedFrom":subQ4}),"instanceName":"1"}),makeQuery(id+"F19.opPattern","COPY",FACE,{"derivedFrom":makeQuery(id+"F9.boolean.opBoolean","SPLIT",FACE,{"disambiguationData":[TD([makeQuery(id+"F9.opExtrude","SWEPT_FACE",FACE,{"disambiguationData":[OSD([sQuery(id+"F8.wireOp",EDGE,"E37")])]})])],"derivedFrom":subQ4}),"instanceName":"1"}),makeQuery(id+"F19.opPattern","COPY",FACE,{"derivedFrom":makeQuery(id+"F9.boolean.opBoolean","SPLIT",FACE,{"disambiguationData":[TD([makeQuery(id+"F9.opExtrude","SWEPT_FACE",FACE,{"disambiguationData":[OSD([sQuery(id+"F8.wireOp",EDGE,"E51.MirrorCS")])]})])],"derivedFrom":subQ4}),"instanceName":"1"}),makeQuery(id+"F19.opPattern","COPY",FACE,{"derivedFrom":makeQuery(id+"F9.boolean.opBoolean","SPLIT",FACE,{"disambiguationData":[TD([makeQuery(id+"F9.opExtrude","SWEPT_FACE",FACE,{"disambiguationData":[OSD([sQuery(id+"F8.wireOp",EDGE,"E53.MirrorCS")])]})])],"derivedFrom":subQ4}),"instanceName":"1"}),makeQuery(id+"F19.opPattern","COPY",FACE,{"derivedFrom":makeQuery(id+"F9.boolean.opBoolean","SPLIT",FACE,{"disambiguationData":[TD([makeQuery(id+"F9.opExtrude","SWEPT_FACE",FACE,{"disambiguationData":[OSD([sQuery(id+"F8.wireOp",EDGE,"E80")])]})])],"derivedFrom":subQ4}),"instanceName":"1"}),makeQuery(id+"F19.opPattern","COPY",FACE,{"derivedFrom":makeQuery(id+"F9.boolean.opBoolean","SPLIT",FACE,{"disambiguationData":[TD([makeQuery(id+"F9.opExtrude","SWEPT_FACE",FACE,{"disambiguationData":[OSD([sQuery(id+"F8.wireOp",EDGE,"E83")])]})])],"derivedFrom":subQ4}),"instanceName":"1"})],"fromTools":[makeQuery(id+"F21.opExtrude","CAP_FACE",FACE,{"disambiguationData":[OSD([sQuery(id+"F20.wireOp",EDGE,"E308.0.0")])],"isStart":false})]}),"instanceName":"1"})})});}
            var sketch = newSketch(context, id + "F80", { "sketchPlane" : qUnion([Q0])});
            skCircle(sketch, "E1117", {"center": v(-5.4, -55.5) * mm, "radius": 2.3 * mm});
            skCircle(sketch, "E1118", {"center": v(-5.4, -55.5) * mm, "radius": 1.78 * mm});
            skLineSegment(sketch, "E1119", {"start": v(-5.4, -55.5) * mm, "end": v(-6.82, -50.3) * mm});
            skArc(sketch, "E1120", {"start": v(-6.52, -53.5) * mm, "mid": v(-6.93, -52.33) * mm, "end": v(-8.16, -52.11) * mm});
            skArc(sketch, "E1121", {"start": v(-8.29, -51.27) * mm, "mid": v(-7.62, -49.2) * mm, "end": v(-7.52, -47.02) * mm});
            skArc(sketch, "E1122.MirrorCS", {"start": v(-5.07, -50.39) * mm, "mid": v(-6.7, -48.94) * mm, "end": v(-7.9, -47.12) * mm});
            skArc(sketch, "E1123.MirrorCS", {"start": v(-5.46, -53.2) * mm, "mid": v(-5.7, -51.99) * mm, "end": v(-4.75, -51.18) * mm});
            skArc(sketch, "E1124.0", {"start": v(-7.84, -51.49) * mm, "mid": v(-7.13, -49.28) * mm, "end": v(-7.02, -46.97) * mm});
            skArc(sketch, "E1125.0", {"start": v(-6.02, -53.59) * mm, "mid": v(-6, -53.44) * mm, "end": v(-6, -53.28) * mm});
            skArc(sketch, "E1126", {"start": v(-7.81, -51.54) * mm, "mid": v(-7.82, -51.51) * mm, "end": v(-7.84, -51.49) * mm});
            skArc(sketch, "E1127.MirrorC", {"start": v(-5.34, -50.86) * mm, "mid": v(-5.35, -50.83) * mm, "end": v(-5.35, -50.8) * mm});
            skArc(sketch, "E1128.MirrorCS", {"start": v(-5.35, -50.8) * mm, "mid": v(-7.08, -49.27) * mm, "end": v(-8.36, -47.34) * mm});
            skArc(sketch, "E1129.MirrorCS", {"start": v(-5.83, -53.54) * mm, "mid": v(-5.93, -53.42) * mm, "end": v(-6.01, -53.29) * mm});
            skArc(sketch, "E1130.trimOffspring", {"start": v(-6.26, -52.34) * mm, "mid": v(-7.17, -51.63) * mm, "end": v(-8.33, -51.64) * mm});
            skArc(sketch, "E1131.trimOffspring", {"start": v(-6.26, -52.34) * mm, "mid": v(-5.85, -51.26) * mm, "end": v(-4.84, -50.68) * mm});
            skArc(sketch, "E1132.trimOffspring", {"start": v(-8.27, -51.23) * mm, "mid": v(-8.69, -51.86) * mm, "end": v(-7.95, -52.05) * mm});
            skArc(sketch, "E1133.trimOffspring", {"start": v(-5.1, -50.36) * mm, "mid": v(-4.43, -50.7) * mm, "end": v(-4.96, -51.23) * mm});
            skArc(sketch, "E1134.MirrorCS", {"start": v(7.81, -51.54) * mm, "mid": v(7.82, -51.51) * mm, "end": v(7.84, -51.49) * mm});
            skArc(sketch, "E1135.MirrorCS", {"start": v(5.34, -50.86) * mm, "mid": v(5.35, -50.83) * mm, "end": v(5.35, -50.8) * mm});
            skArc(sketch, "E1136.MirrorCS", {"start": v(6.02, -53.59) * mm, "mid": v(6, -53.44) * mm, "end": v(6, -53.28) * mm});
            skArc(sketch, "E1137.MirrorCS", {"start": v(5.83, -53.54) * mm, "mid": v(5.93, -53.42) * mm, "end": v(6.01, -53.29) * mm});
            skArc(sketch, "E1138.MirrorCS", {"start": v(8.27, -51.23) * mm, "mid": v(8.69, -51.86) * mm, "end": v(7.95, -52.05) * mm});
            skArc(sketch, "E1139.MirrorCS", {"start": v(7.84, -51.49) * mm, "mid": v(7.13, -49.28) * mm, "end": v(7.02, -46.97) * mm});
            skArc(sketch, "E1140.MirrorCS", {"start": v(5.46, -53.2) * mm, "mid": v(5.7, -51.99) * mm, "end": v(4.75, -51.18) * mm});
            skArc(sketch, "E1141.MirrorCS", {"start": v(8.29, -51.27) * mm, "mid": v(7.62, -49.2) * mm, "end": v(7.52, -47.02) * mm});
            skArc(sketch, "E1142.MirrorCS", {"start": v(5.35, -50.8) * mm, "mid": v(7.08, -49.27) * mm, "end": v(8.36, -47.34) * mm});
            skArc(sketch, "E1143.MirrorCS", {"start": v(6.26, -52.34) * mm, "mid": v(7.17, -51.63) * mm, "end": v(8.33, -51.64) * mm});
            skArc(sketch, "E1144.MirrorCS", {"start": v(5.1, -50.36) * mm, "mid": v(4.43, -50.7) * mm, "end": v(4.96, -51.23) * mm});
            skArc(sketch, "E1145.MirrorCS", {"start": v(6.26, -52.34) * mm, "mid": v(5.85, -51.26) * mm, "end": v(4.84, -50.68) * mm});
            skArc(sketch, "E1146.MirrorCS", {"start": v(5.07, -50.39) * mm, "mid": v(6.7, -48.94) * mm, "end": v(7.9, -47.12) * mm});
            skLineSegment(sketch, "E1147.MirrorCS", {"start": v(5.4, -55.5) * mm, "end": v(6.82, -50.3) * mm});
            skCircle(sketch, "E1148.MirrorC", {"center": v(5.4, -55.5) * mm, "radius": 1.78 * mm});
            skArc(sketch, "E1149.MirrorCS", {"start": v(6.52, -53.5) * mm, "mid": v(6.93, -52.33) * mm, "end": v(8.16, -52.11) * mm});
            skCircle(sketch, "E1150.MirrorC", {"center": v(5.4, -55.5) * mm, "radius": 2.3 * mm});
            skSolve(sketch);
        }
        {
            var Q0;
            Q0 = qSketchRegion(id + "F80", true);
            var Q1;
            Q1=makeQuery(id+"F34.opExtrude","CAP_FACE",FACE,{"disambiguationData":[OSD([sQuery(id+"F33.wireOp",EDGE,"E523"),sQuery(id+"F33.wireOp",EDGE,"E524"),sQuery(id+"F33.wireOp",EDGE,"E525"),sQuery(id+"F33.wireOp",EDGE,"E526"),sQuery(id+"F33.wireOp",EDGE,"E527"),sQuery(id+"F33.wireOp",EDGE,"E528.trimOffspring"),sQuery(id+"F33.wireOp",EDGE,"E529.MirrorCS"),sQuery(id+"F33.wireOp",EDGE,"E530.MirrorCS"),sQuery(id+"F33.wireOp",EDGE,"E534.MirrorCS"),sQuery(id+"F33.wireOp",EDGE,"E535.MirrorCS"),sQuery(id+"F33.wireOp",EDGE,"E536.MirrorCS"),sQuery(id+"F33.wireOp",EDGE,"E537.MirrorCS"),sQuery(id+"F33.wireOp",EDGE,"E538.MirrorCS"),sQuery(id+"F33.wireOp",EDGE,"E539.MirrorCS"),sQuery(id+"F33.wireOp",EDGE,"E540.MirrorCS"),sQuery(id+"F33.wireOp",EDGE,"E541.MirrorCS"),sQuery(id+"F33.wireOp",EDGE,"E542.MirrorCS"),sQuery(id+"F33.wireOp",EDGE,"E543.MirrorCS"),sQuery(id+"F33.wireOp",EDGE,"E544.MirrorCS"),sQuery(id+"F33.wireOp",EDGE,"E545.MirrorCS"),sQuery(id+"F33.wireOp",EDGE,"E546.MirrorCS"),sQuery(id+"F33.wireOp",EDGE,"E547.MirrorCS"),sQuery(id+"F33.wireOp",EDGE,"E548.MirrorCS"),sQuery(id+"F33.wireOp",EDGE,"E549.MirrorCS"),sQuery(id+"F33.wireOp",EDGE,"E551.trimOffspring"),sQuery(id+"F33.wireOp",EDGE,"E552.trimOffspring"),sQuery(id+"F33.wireOp",EDGE,"E553.trimOffspring"),sQuery(id+"F33.wireOp",EDGE,"E554.trimOffspring"),sQuery(id+"F33.wireOp",EDGE,"E555.trimOffspring"),sQuery(id+"F33.wireOp",EDGE,"E556.trimOffspring"),sQuery(id+"F33.wireOp",EDGE,"E557.trimOffspring"),sQuery(id+"F33.wireOp",EDGE,"E558.trimOffspring"),sQuery(id+"F33.wireOp",EDGE,"E559.trimOffspring"),sQuery(id+"F33.wireOp",EDGE,"E560.trimOffspring"),sQuery(id+"F33.wireOp",EDGE,"E561.trimOffspring"),sQuery(id+"F33.wireOp",EDGE,"E562.trimOffspring"),sQuery(id+"F33.wireOp",EDGE,"E563.trimOffspring"),sQuery(id+"F33.wireOp",EDGE,"E564.trimOffspring"),sQuery(id+"F33.wireOp",EDGE,"E565.trimOffspring"),sQuery(id+"F33.wireOp",EDGE,"E566.trimOffspring"),sQuery(id+"F33.wireOp",EDGE,"E567.trimOffspring"),sQuery(id+"F33.wireOp",EDGE,"E568.trimOffspring"),sQuery(id+"F33.wireOp",EDGE,"E569.trimOffspring"),sQuery(id+"F33.wireOp",EDGE,"E570.trimOffspring"),sQuery(id+"F33.wireOp",EDGE,"E571.trimOffspring"),sQuery(id+"F33.wireOp",EDGE,"E572.trimOffspring"),sQuery(id+"F33.wireOp",EDGE,"E573.trimOffspring"),sQuery(id+"F33.wireOp",EDGE,"E574.trimOffspring"),sQuery(id+"F33.wireOp",EDGE,"E575.trimOffspring"),sQuery(id+"F33.wireOp",EDGE,"E576.trimOffspring"),sQuery(id+"F33.wireOp",EDGE,"E577.trimOffspring"),sQuery(id+"F33.wireOp",EDGE,"E578.trimOffspring"),sQuery(id+"F33.wireOp",EDGE,"E579.trimOffspring"),sQuery(id+"F33.wireOp",EDGE,"E580.trimOffspring"),sQuery(id+"F33.wireOp",EDGE,"E581.trimOffspring"),sQuery(id+"F33.wireOp",EDGE,"E582.trimOffspring"),sQuery(id+"F33.wireOp",EDGE,"E583.trimOffspring"),sQuery(id+"F33.wireOp",EDGE,"E584.trimOffspring"),sQuery(id+"F33.wireOp",EDGE,"E585.trimOffspring"),sQuery(id+"F33.wireOp",EDGE,"E586.trimOffspring"),sQuery(id+"F33.wireOp",EDGE,"E587.trimOffspring"),sQuery(id+"F33.wireOp",EDGE,"E588.trimOffspring"),sQuery(id+"F33.wireOp",EDGE,"E589.trimOffspring"),sQuery(id+"F33.wireOp",EDGE,"E590.trimOffspring"),sQuery(id+"F33.wireOp",EDGE,"E591.trimOffspring"),sQuery(id+"F33.wireOp",EDGE,"E592.trimOffspring"),sQuery(id+"F33.wireOp",EDGE,"E593.trimOffspring"),sQuery(id+"F33.wireOp",EDGE,"E594.trimOffspring"),sQuery(id+"F33.wireOp",EDGE,"E595.trimOffspring"),sQuery(id+"F33.wireOp",EDGE,"E596.trimOffspring"),sQuery(id+"F33.wireOp",EDGE,"E597.trimOffspring"),sQuery(id+"F33.wireOp",EDGE,"E598.trimOffspring")])],"isStart":false});
            extrude(context, id + "F81", {"entities" : qUnion([Q0]), "operationType" : NewBodyOperationType.ADD, "endBound" : BoundingType.UP_TO_SURFACE, "depth" : 25.4 * mm, "endBoundEntityFace" : qUnion([Q1]), "offsetDistance" : 25.4 * mm});
        }
        {
            var Q0;
            {var subQ8=sQuery(id+"F4.wireOp",EDGE,"E8");var subQ9=makeQuery(id+"F5.boolean.opBoolean","COPY",FACE,{"derivedFrom":makeQuery(id+"F5.opExtrude","CAP_FACE",FACE,{"disambiguationData":[OSD([subQ8])],"isStart":false})});var subQ10=makeQuery(id+"F5.boolean.opBoolean","COPY",FACE,{"derivedFrom":makeQuery(id+"F5.opExtrude","SWEPT_FACE",FACE,{"disambiguationData":[OSD([subQ8])]})});var subQ11=makeQuery(id+"F39.opPattern","COPY",FACE,{"derivedFrom":makeQuery(id+"F21.boolean.opBoolean","MERGE",FACE,{"derivedFrom":[makeQuery(id+"F19.opPattern","COPY",FACE,{"derivedFrom":makeQuery(id+"F9.boolean.opBoolean","SPLIT",FACE,{"disambiguationData":[TD([subQ10])],"derivedFrom":subQ9}),"instanceName":"1"}),makeQuery(id+"F19.opPattern","COPY",FACE,{"derivedFrom":makeQuery(id+"F9.boolean.opBoolean","SPLIT",FACE,{"disambiguationData":[TD([makeQuery(id+"F9.opExtrude","SWEPT_FACE",FACE,{"disambiguationData":[OSD([sQuery(id+"F8.wireOp",EDGE,"E25")])]})])],"derivedFrom":subQ9}),"instanceName":"1"}),makeQuery(id+"F19.opPattern","COPY",FACE,{"derivedFrom":makeQuery(id+"F9.boolean.opBoolean","SPLIT",FACE,{"disambiguationData":[TD([makeQuery(id+"F9.opExtrude","SWEPT_FACE",FACE,{"disambiguationData":[OSD([sQuery(id+"F8.wireOp",EDGE,"E32")])]})])],"derivedFrom":subQ9}),"instanceName":"1"}),makeQuery(id+"F19.opPattern","COPY",FACE,{"derivedFrom":makeQuery(id+"F9.boolean.opBoolean","SPLIT",FACE,{"disambiguationData":[TD([makeQuery(id+"F9.opExtrude","SWEPT_FACE",FACE,{"disambiguationData":[OSD([sQuery(id+"F8.wireOp",EDGE,"E33.0")])]})])],"derivedFrom":subQ9}),"instanceName":"1"}),makeQuery(id+"F19.opPattern","COPY",FACE,{"derivedFrom":makeQuery(id+"F9.boolean.opBoolean","SPLIT",FACE,{"disambiguationData":[TD([makeQuery(id+"F9.opExtrude","SWEPT_FACE",FACE,{"disambiguationData":[OSD([sQuery(id+"F8.wireOp",EDGE,"E37")])]})])],"derivedFrom":subQ9}),"instanceName":"1"}),makeQuery(id+"F19.opPattern","COPY",FACE,{"derivedFrom":makeQuery(id+"F9.boolean.opBoolean","SPLIT",FACE,{"disambiguationData":[TD([makeQuery(id+"F9.opExtrude","SWEPT_FACE",FACE,{"disambiguationData":[OSD([sQuery(id+"F8.wireOp",EDGE,"E51.MirrorCS")])]})])],"derivedFrom":subQ9}),"instanceName":"1"}),makeQuery(id+"F19.opPattern","COPY",FACE,{"derivedFrom":makeQuery(id+"F9.boolean.opBoolean","SPLIT",FACE,{"disambiguationData":[TD([makeQuery(id+"F9.opExtrude","SWEPT_FACE",FACE,{"disambiguationData":[OSD([sQuery(id+"F8.wireOp",EDGE,"E53.MirrorCS")])]})])],"derivedFrom":subQ9}),"instanceName":"1"}),makeQuery(id+"F19.opPattern","COPY",FACE,{"derivedFrom":makeQuery(id+"F9.boolean.opBoolean","SPLIT",FACE,{"disambiguationData":[TD([makeQuery(id+"F9.opExtrude","SWEPT_FACE",FACE,{"disambiguationData":[OSD([sQuery(id+"F8.wireOp",EDGE,"E80")])]})])],"derivedFrom":subQ9}),"instanceName":"1"}),makeQuery(id+"F19.opPattern","COPY",FACE,{"derivedFrom":makeQuery(id+"F9.boolean.opBoolean","SPLIT",FACE,{"disambiguationData":[TD([makeQuery(id+"F9.opExtrude","SWEPT_FACE",FACE,{"disambiguationData":[OSD([sQuery(id+"F8.wireOp",EDGE,"E83")])]})])],"derivedFrom":subQ9}),"instanceName":"1"})],"fromTools":[makeQuery(id+"F21.opExtrude","CAP_FACE",FACE,{"disambiguationData":[OSD([sQuery(id+"F20.wireOp",EDGE,"E308.0.0")])],"isStart":false})]}),"instanceName":"1"});var subQ16=makeQuery(id+"F39.opPattern","COPY",FACE,{"derivedFrom":makeQuery(id+"F19.opPattern","COPY",FACE,{"derivedFrom":subQ10,"instanceName":"1"}),"instanceName":"1"});Q0=makeQuery(id+"F81.boolean.opBoolean","SPLIT",FACE,{"disambiguationData":[TD([subQ16])],"derivedFrom":makeQuery(id+"F79.boolean.opBoolean","SPLIT",FACE,{"disambiguationData":[TD([subQ16])],"derivedFrom":makeQuery(id+"F77.boolean.opBoolean","SPLIT",FACE,{"disambiguationData":[TD([subQ16])],"derivedFrom":subQ11})})});}
            var sketch = newSketch(context, id + "F82", { "sketchPlane" : qUnion([Q0])});
            skLineSegment(sketch, "E1151", {"start": v(0, -49.46) * mm, "end": v(-0.08, -53.85) * mm});
            skArc(sketch, "E1152", {"start": v(-8.44, -53.85) * mm, "mid": v(-0.08, -57.2) * mm, "end": v(8.29, -53.85) * mm});
            skArc(sketch, "E1153.0", {"start": v(-8.79, -54.22) * mm, "mid": v(-0.08, -57.7) * mm, "end": v(8.63, -54.22) * mm});
            skLineSegment(sketch, "E1154", {"start": v(-8.79, -54.22) * mm, "end": v(-8.44, -53.85) * mm});
            skLineSegment(sketch, "E1155", {"start": v(8.29, -53.85) * mm, "end": v(8.63, -54.22) * mm});
            skSolve(sketch);
        }
        {
            var Q0;
            Q0 = qSketchRegion(id + "F82", true);
            var Q1;
            {var subQ0=sQuery(id+"F80.wireOp",EDGE,"E1125.0");var subQ1=sQuery(id+"F80.wireOp",EDGE,"E1124.0");var subQ2=sQuery(id+"F80.wireOp",EDGE,"E1123.MirrorCS");var subQ3=sQuery(id+"F80.wireOp",EDGE,"E1122.MirrorCS");var subQ4=sQuery(id+"F80.wireOp",EDGE,"E1121");var subQ5=sQuery(id+"F80.wireOp",EDGE,"E1120");var subQ6=sQuery(id+"F76.wireOp",EDGE,"E1063");var subQ7=makeQuery(id+"F77.opExtrude","SWEPT_FACE",FACE,{"disambiguationData":[OSD([subQ6])]});var subQ8=sQuery(id+"F80.wireOp",EDGE,"E1117");var subQ14=sQuery(id+"F80.wireOp",EDGE,"E1129.MirrorCS");var subQ16=sQuery(id+"F80.wireOp",EDGE,"E1118");var subQ17=sQuery(id+"F80.wireOp",EDGE,"E1126");var subQ18=sQuery(id+"F80.wireOp",EDGE,"E1127.MirrorC");var subQ19=sQuery(id+"F80.wireOp",EDGE,"E1128.MirrorCS");var subQ20=sQuery(id+"F80.wireOp",EDGE,"E1130.trimOffspring");var subQ21=sQuery(id+"F80.wireOp",EDGE,"E1131.trimOffspring");var subQ22=sQuery(id+"F80.wireOp",EDGE,"E1132.trimOffspring");var subQ23=sQuery(id+"F80.wireOp",EDGE,"E1133.trimOffspring");Q1=makeQuery(id+"F81.boolean.opBoolean","SPLIT",FACE,{"disambiguationData":[TD([subQ7])],"derivedFrom":makeQuery(id+"F81.opExtrude","CAP_FACE",FACE,{"disambiguationData":[OSD([subQ8,subQ16,subQ5,subQ4,subQ3,subQ2,subQ1,subQ0,subQ17,subQ18,subQ19,subQ14,subQ20,subQ21,subQ22,subQ23])],"isStart":false})});}
            extrude(context, id + "F83", {"entities" : qUnion([Q0]), "operationType" : NewBodyOperationType.ADD, "endBound" : BoundingType.UP_TO_SURFACE, "depth" : 25.4 * mm, "endBoundEntityFace" : qUnion([Q1]), "offsetDistance" : 25.4 * mm});
        }
        {
            var Q0;
            {var subQ0=sQuery(id+"F4.wireOp",EDGE,"E8");var subQ1=makeQuery(id+"F5.boolean.opBoolean","COPY",FACE,{"derivedFrom":makeQuery(id+"F5.opExtrude","SWEPT_FACE",FACE,{"disambiguationData":[OSD([subQ0])]})});var subQ2=makeQuery(id+"F5.boolean.opBoolean","COPY",FACE,{"derivedFrom":makeQuery(id+"F5.opExtrude","CAP_FACE",FACE,{"disambiguationData":[OSD([subQ0])],"isStart":false})});var subQ3=makeQuery(id+"F39.opPattern","COPY",FACE,{"derivedFrom":makeQuery(id+"F21.boolean.opBoolean","MERGE",FACE,{"derivedFrom":[makeQuery(id+"F19.opPattern","COPY",FACE,{"derivedFrom":makeQuery(id+"F17.opPattern","COPY",FACE,{"derivedFrom":makeQuery(id+"F9.boolean.opBoolean","SPLIT",FACE,{"disambiguationData":[TD([subQ1])],"derivedFrom":subQ2}),"instanceName":"1"}),"instanceName":"1"}),makeQuery(id+"F19.opPattern","COPY",FACE,{"derivedFrom":makeQuery(id+"F17.opPattern","COPY",FACE,{"derivedFrom":makeQuery(id+"F9.boolean.opBoolean","SPLIT",FACE,{"disambiguationData":[TD([makeQuery(id+"F9.opExtrude","SWEPT_FACE",FACE,{"disambiguationData":[OSD([sQuery(id+"F8.wireOp",EDGE,"E25")])]})])],"derivedFrom":subQ2}),"instanceName":"1"}),"instanceName":"1"}),makeQuery(id+"F19.opPattern","COPY",FACE,{"derivedFrom":makeQuery(id+"F17.opPattern","COPY",FACE,{"derivedFrom":makeQuery(id+"F9.boolean.opBoolean","SPLIT",FACE,{"disambiguationData":[TD([makeQuery(id+"F9.opExtrude","SWEPT_FACE",FACE,{"disambiguationData":[OSD([sQuery(id+"F8.wireOp",EDGE,"E32")])]})])],"derivedFrom":subQ2}),"instanceName":"1"}),"instanceName":"1"}),makeQuery(id+"F19.opPattern","COPY",FACE,{"derivedFrom":makeQuery(id+"F17.opPattern","COPY",FACE,{"derivedFrom":makeQuery(id+"F9.boolean.opBoolean","SPLIT",FACE,{"disambiguationData":[TD([makeQuery(id+"F9.opExtrude","SWEPT_FACE",FACE,{"disambiguationData":[OSD([sQuery(id+"F8.wireOp",EDGE,"E33.0")])]})])],"derivedFrom":subQ2}),"instanceName":"1"}),"instanceName":"1"}),makeQuery(id+"F19.opPattern","COPY",FACE,{"derivedFrom":makeQuery(id+"F17.opPattern","COPY",FACE,{"derivedFrom":makeQuery(id+"F9.boolean.opBoolean","SPLIT",FACE,{"disambiguationData":[TD([makeQuery(id+"F9.opExtrude","SWEPT_FACE",FACE,{"disambiguationData":[OSD([sQuery(id+"F8.wireOp",EDGE,"E37")])]})])],"derivedFrom":subQ2}),"instanceName":"1"}),"instanceName":"1"}),makeQuery(id+"F19.opPattern","COPY",FACE,{"derivedFrom":makeQuery(id+"F17.opPattern","COPY",FACE,{"derivedFrom":makeQuery(id+"F9.boolean.opBoolean","SPLIT",FACE,{"disambiguationData":[TD([makeQuery(id+"F9.opExtrude","SWEPT_FACE",FACE,{"disambiguationData":[OSD([sQuery(id+"F8.wireOp",EDGE,"E51.MirrorCS")])]})])],"derivedFrom":subQ2}),"instanceName":"1"}),"instanceName":"1"}),makeQuery(id+"F19.opPattern","COPY",FACE,{"derivedFrom":makeQuery(id+"F17.opPattern","COPY",FACE,{"derivedFrom":makeQuery(id+"F9.boolean.opBoolean","SPLIT",FACE,{"disambiguationData":[TD([makeQuery(id+"F9.opExtrude","SWEPT_FACE",FACE,{"disambiguationData":[OSD([sQuery(id+"F8.wireOp",EDGE,"E53.MirrorCS")])]})])],"derivedFrom":subQ2}),"instanceName":"1"}),"instanceName":"1"}),makeQuery(id+"F19.opPattern","COPY",FACE,{"derivedFrom":makeQuery(id+"F17.opPattern","COPY",FACE,{"derivedFrom":makeQuery(id+"F9.boolean.opBoolean","SPLIT",FACE,{"disambiguationData":[TD([makeQuery(id+"F9.opExtrude","SWEPT_FACE",FACE,{"disambiguationData":[OSD([sQuery(id+"F8.wireOp",EDGE,"E80")])]})])],"derivedFrom":subQ2}),"instanceName":"1"}),"instanceName":"1"}),makeQuery(id+"F19.opPattern","COPY",FACE,{"derivedFrom":makeQuery(id+"F17.opPattern","COPY",FACE,{"derivedFrom":makeQuery(id+"F9.boolean.opBoolean","SPLIT",FACE,{"disambiguationData":[TD([makeQuery(id+"F9.opExtrude","SWEPT_FACE",FACE,{"disambiguationData":[OSD([sQuery(id+"F8.wireOp",EDGE,"E83")])]})])],"derivedFrom":subQ2}),"instanceName":"1"}),"instanceName":"1"})],"fromTools":[makeQuery(id+"F21.opExtrude","CAP_FACE",FACE,{"disambiguationData":[OSD([sQuery(id+"F20.wireOp",EDGE,"E309.0.0")])],"isStart":false})]}),"instanceName":"1"});Q0=makeQuery(id+"F75.boolean.opBoolean","MERGE",FACE,{"derivedFrom":[makeQuery(id+"F69.boolean.opBoolean","SPLIT",FACE,{"disambiguationData":[TD([makeQuery(id+"F69.opExtrude","SWEPT_FACE",FACE,{"disambiguationData":[OSD([sQuery(id+"F68.wireOp",EDGE,"E901")])]})])],"derivedFrom":subQ3}),makeQuery(id+"F69.boolean.opBoolean","SPLIT",FACE,{"disambiguationData":[TD([makeQuery(id+"F39.opPattern","COPY",FACE,{"derivedFrom":makeQuery(id+"F19.opPattern","COPY",FACE,{"derivedFrom":makeQuery(id+"F17.opPattern","COPY",FACE,{"derivedFrom":subQ1,"instanceName":"1"}),"instanceName":"1"}),"instanceName":"1"})])],"derivedFrom":subQ3})],"fromTools":[makeQuery(id+"F75.opExtrude","CAP_FACE",FACE,{"disambiguationData":[OSD([sQuery(id+"F74.wireOp",EDGE,"E1055.0"),sQuery(id+"F74.wireOp",EDGE,"E1056.0"),sQuery(id+"F74.wireOp",EDGE,"E1057.0"),sQuery(id+"F74.wireOp",EDGE,"E1058"),sQuery(id+"F74.wireOp",EDGE,"E1059"),sQuery(id+"F74.wireOp",EDGE,"E1060.0"),sQuery(id+"F74.wireOp",EDGE,"E1061"),sQuery(id+"F74.wireOp",EDGE,"E1062")])],"isStart":false})]});}
            var sketch = newSketch(context, id + "F84", { "sketchPlane" : qUnion([Q0])});
            skArc(sketch, "E1156", {"start": v(-49.42, -50.55) * mm, "mid": v(-49.5, -50.26) * mm, "end": v(-49.65, -50) * mm});
            skArc(sketch, "E1157", {"start": v(-54.53, -50.55) * mm, "mid": v(-53.47, -50.09) * mm, "end": v(-52.55, -49.4) * mm});
            skLineSegment(sketch, "E1158.left", {"start": v(-50.55, -44.86) * mm, "end": v(-50.55, -49.42) * mm});
            skLineSegment(sketch, "E1158.right", {"start": v(-51.05, -44.86) * mm, "end": v(-51.05, -49.42) * mm});
            skLineSegment(sketch, "E1159.MirrorCS", {"start": v(-46.78, -46.43) * mm, "end": v(-49.4, -49.05) * mm});
            skLineSegment(sketch, "E1160.MirrorCS", {"start": v(-46.43, -46.78) * mm, "end": v(-49.05, -49.4) * mm});
            skLineSegment(sketch, "E1161.MirrorCS", {"start": v(-44.86, -50.55) * mm, "end": v(-49.42, -50.55) * mm});
            skLineSegment(sketch, "E1162.MirrorCS", {"start": v(-44.86, -51.05) * mm, "end": v(-49.42, -51.05) * mm});
            skLineSegment(sketch, "E1163.MirrorCS", {"start": v(-54.82, -46.43) * mm, "end": v(-51.6, -49.65) * mm});
            skLineSegment(sketch, "E1164.MirrorCS", {"start": v(-55.17, -46.78) * mm, "end": v(-51.95, -50) * mm});
            skArc(sketch, "E1165.MirrorCS", {"start": v(-54.53, -51.05) * mm, "mid": v(-53.47, -51.51) * mm, "end": v(-52.55, -52.2) * mm});
            skArc(sketch, "E1166.MirrorCS", {"start": v(-47.07, -50.55) * mm, "mid": v(-48.13, -50.09) * mm, "end": v(-49.05, -49.4) * mm});
            skArc(sketch, "E1167.MirrorCS", {"start": v(-47.07, -51.05) * mm, "mid": v(-48.13, -51.51) * mm, "end": v(-49.05, -52.2) * mm});
            skPoint(sketch, "E1168.orphan", {"position": v(-45.46, -50.8) * mm});
            skLineSegment(sketch, "E1169.trimOffspring", {"start": v(-50.2, -50.55) * mm, "end": v(-50.45, -50.8) * mm});
            skArc(sketch, "E1170.trimOffspring", {"start": v(-51.05, -49.42) * mm, "mid": v(-51.34, -49.5) * mm, "end": v(-51.6, -49.65) * mm});
            skArc(sketch, "E1171.trimOffspring", {"start": v(-50.55, -52.18) * mm, "mid": v(-50.26, -52.1) * mm, "end": v(-50, -51.95) * mm});
            skArc(sketch, "E1172.trimOffspring", {"start": v(-49.65, -51.6) * mm, "mid": v(-49.5, -51.34) * mm, "end": v(-49.42, -51.05) * mm});
            skArc(sketch, "E1173.trimOffspring", {"start": v(-49.4, -52.55) * mm, "mid": v(-50.09, -53.47) * mm, "end": v(-50.55, -54.53) * mm});
            skArc(sketch, "E1174.trimOffspring", {"start": v(-50, -49.65) * mm, "mid": v(-50.26, -49.5) * mm, "end": v(-50.55, -49.42) * mm});
            skArc(sketch, "E1175.trimOffspring", {"start": v(-49.4, -49.05) * mm, "mid": v(-50.09, -48.13) * mm, "end": v(-50.55, -47.07) * mm});
            skArc(sketch, "E1176.trimOffspring", {"start": v(-52.2, -49.05) * mm, "mid": v(-51.51, -48.13) * mm, "end": v(-51.05, -47.07) * mm});
            skArc(sketch, "E1177.trimOffspring", {"start": v(-51.95, -50) * mm, "mid": v(-52.1, -50.26) * mm, "end": v(-52.18, -50.55) * mm});
            skArc(sketch, "E1178.trimOffspring", {"start": v(-51.6, -51.95) * mm, "mid": v(-51.34, -52.1) * mm, "end": v(-51.05, -52.18) * mm});
            skArc(sketch, "E1179.trimOffspring", {"start": v(-52.2, -52.55) * mm, "mid": v(-51.51, -53.47) * mm, "end": v(-51.05, -54.53) * mm});
            skArc(sketch, "E1180.trimOffspring", {"start": v(-52.18, -51.05) * mm, "mid": v(-52.1, -51.34) * mm, "end": v(-51.95, -51.6) * mm});
            skPoint(sketch, "E1181.orphan", {"position": v(-56.14, -50.8) * mm});
            skPoint(sketch, "E1182.orphan", {"position": v(-50.8, -56.14) * mm});
            skLineSegment(sketch, "E1183.trimOffspring", {"start": v(-52.18, -51.05) * mm, "end": v(-56.74, -51.05) * mm});
            skLineSegment(sketch, "E1184.trimOffspring", {"start": v(-52.18, -50.55) * mm, "end": v(-56.74, -50.55) * mm});
            skLineSegment(sketch, "E1185.trimOffspring", {"start": v(-51.4, -50.55) * mm, "end": v(-51.15, -50.8) * mm});
            skLineSegment(sketch, "E1186.trimOffspring", {"start": v(-51.05, -50.2) * mm, "end": v(-50.8, -50.45) * mm});
            skLineSegment(sketch, "E1187.trimOffspring", {"start": v(-51.05, -50.2) * mm, "end": v(-51.05, -50.55) * mm});
            skLineSegment(sketch, "E1188.trimOffspring", {"start": v(-50.55, -50.2) * mm, "end": v(-50.55, -50.55) * mm});
            skLineSegment(sketch, "E1189.trimOffspring", {"start": v(-50.2, -51.05) * mm, "end": v(-50.55, -51.05) * mm});
            skLineSegment(sketch, "E1190.trimOffspring", {"start": v(-50.2, -50.55) * mm, "end": v(-50.55, -50.55) * mm});
            skLineSegment(sketch, "E1191.trimOffspring", {"start": v(-49.65, -51.6) * mm, "end": v(-46.43, -54.82) * mm});
            skLineSegment(sketch, "E1192.trimOffspring", {"start": v(-50, -51.95) * mm, "end": v(-46.78, -55.17) * mm});
            skLineSegment(sketch, "E1193.trimOffspring", {"start": v(-50.55, -52.18) * mm, "end": v(-50.55, -54.53) * mm});
            skLineSegment(sketch, "E1194.trimOffspring", {"start": v(-51.05, -52.18) * mm, "end": v(-51.05, -54.53) * mm});
            skLineSegment(sketch, "E1195.trimOffspring", {"start": v(-51.6, -51.95) * mm, "end": v(-54.82, -55.17) * mm});
            skLineSegment(sketch, "E1196.trimOffspring", {"start": v(-51.95, -51.6) * mm, "end": v(-55.17, -54.82) * mm});
            skLineSegment(sketch, "E1197", {"start": v(-50, -49.65) * mm, "end": v(-49.4, -49.05) * mm});
            skLineSegment(sketch, "E1198", {"start": v(-49.65, -50) * mm, "end": v(-49.05, -49.4) * mm});
            skPoint(sketch, "E1199.orphan", {"position": v(-50.8, -45.46) * mm});
            skLineSegment(sketch, "E1200.trimOffspring", {"start": v(-51.05, -51.05) * mm, "end": v(-51.05, -51.4) * mm});
            skLineSegment(sketch, "E1201.trimOffspring", {"start": v(-51.05, -51.05) * mm, "end": v(-51.4, -51.05) * mm});
            skLineSegment(sketch, "E1202.trimOffspring", {"start": v(-50.8, -51.15) * mm, "end": v(-50.55, -51.4) * mm});
            skLineSegment(sketch, "E1203.trimOffspring", {"start": v(-50.8, -51.15) * mm, "end": v(-51.05, -51.4) * mm});
            skLineSegment(sketch, "E1204.trimOffspring", {"start": v(-50.55, -51.05) * mm, "end": v(-50.55, -51.4) * mm});
            skLineSegment(sketch, "E1205.trimOffspring", {"start": v(-50.45, -50.8) * mm, "end": v(-50.2, -51.05) * mm});
            skLineSegment(sketch, "E1206.trimOffspring", {"start": v(-51.05, -50.55) * mm, "end": v(-51.4, -50.55) * mm});
            skLineSegment(sketch, "E1207.trimOffspring", {"start": v(-51.15, -50.8) * mm, "end": v(-51.4, -51.05) * mm});
            skLineSegment(sketch, "E1208", {"start": v(-50.8, -50.45) * mm, "end": v(-50.55, -50.2) * mm});
            skPoint(sketch, "E1209.orphan", {"position": v(-50.55, -56.74) * mm});
            skPoint(sketch, "E1210.orphan", {"position": v(-51.05, -56.74) * mm});
            skArc(sketch, "E1211", {"start": v(-50.5, -56.2) * mm, "mid": v(-50.8, -54.93) * mm, "end": v(-51.1, -56.2) * mm});
            skArc(sketch, "E1212", {"start": v(-50.58, -56.97) * mm, "mid": v(-50.48, -56.73) * mm, "end": v(-50.58, -56.5) * mm});
            skArc(sketch, "E1213", {"start": v(-51.02, -56.5) * mm, "mid": v(-51.04, -56.34) * mm, "end": v(-51.1, -56.2) * mm});
            skLineSegment(sketch, "E1214", {"start": v(-50.8, -56.74) * mm, "end": v(-50.8, -56.58) * mm});
            skArc(sketch, "E1215.MirrorCS", {"start": v(-50.58, -56.5) * mm, "mid": v(-50.56, -56.34) * mm, "end": v(-50.5, -56.2) * mm});
            skLineSegment(sketch, "E1216.bottom", {"start": v(-49.72, -59.8) * mm, "end": v(-50.43, -59.8) * mm});
            skLineSegment(sketch, "E1216.left", {"start": v(-49.72, -59.8) * mm, "end": v(-49.72, -60.04) * mm});
            skLineSegment(sketch, "E1216.right", {"start": v(-51.88, -59.8) * mm, "end": v(-51.88, -60.04) * mm});
            skPoint(sketch, "E1216.middle", {"position": v(-50.8, -59.92) * mm});
            skLineSegment(sketch, "E1217.bottom", {"start": v(-49.3, -60.17) * mm, "end": v(-52.3, -60.17) * mm});
            skLineSegment(sketch, "E1217.top", {"start": v(-49.3, -59.92) * mm, "end": v(-49.72, -59.92) * mm});
            skLineSegment(sketch, "E1217.left", {"start": v(-49.3, -60.17) * mm, "end": v(-49.3, -59.92) * mm});
            skLineSegment(sketch, "E1217.right", {"start": v(-52.3, -60.17) * mm, "end": v(-52.3, -59.92) * mm});
            skPoint(sketch, "E1217.middle", {"position": v(-50.8, -60.04) * mm});
            skArc(sketch, "E1218.trimOffspring", {"start": v(-51.02, -56.5) * mm, "mid": v(-51.12, -56.73) * mm, "end": v(-51.02, -56.97) * mm});
            skLineSegment(sketch, "E1219.trimOffspring", {"start": v(-51.17, -59.8) * mm, "end": v(-51.88, -59.8) * mm});
            skArc(sketch, "E1220", {"start": v(-50.43, -59.8) * mm, "mid": v(-50.5, -59.67) * mm, "end": v(-50.6, -59.58) * mm});
            skPoint(sketch, "E1221.start.orphan", {"position": v(-51.06, -59.91) * mm});
            skPoint(sketch, "E1222.MirrorCS.start.orphan", {"position": v(-50.54, -59.91) * mm});
            skLineSegment(sketch, "E1223.trimOffspring", {"start": v(-51.88, -59.92) * mm, "end": v(-52.3, -59.92) * mm});
            skArc(sketch, "E1224.trimOffspring", {"start": v(-51, -59.58) * mm, "mid": v(-51.1, -59.67) * mm, "end": v(-51.17, -59.8) * mm});
            skArc(sketch, "E1225", {"start": v(-51.02, -56.97) * mm, "mid": v(-51.08, -58.28) * mm, "end": v(-51, -59.58) * mm});
            skArc(sketch, "E1226.MirrorCS", {"start": v(-50.58, -56.97) * mm, "mid": v(-50.52, -58.28) * mm, "end": v(-50.6, -59.58) * mm});
            skSolve(sketch);
        }
        {
            var Q0;
            Q0 = qSketchRegion(id + "F84", true);
            var Q1;
            Q1=makeQuery(id+"F73.boolean.opBoolean","MERGE",FACE,{"derivedFrom":[makeQuery(id+"F71.boolean.opBoolean","MERGE",FACE,{"derivedFrom":[makeQuery(id+"F69.opExtrude","CAP_FACE",FACE,{"disambiguationData":[OSD([sQuery(id+"F68.wireOp",EDGE,"E900"),sQuery(id+"F68.wireOp",EDGE,"E902.top"),sQuery(id+"F68.wireOp",EDGE,"E902.left"),sQuery(id+"F68.wireOp",EDGE,"E902.right"),sQuery(id+"F68.wireOp",EDGE,"E903"),sQuery(id+"F68.wireOp",EDGE,"E904.MirrorCS"),sQuery(id+"F68.wireOp",EDGE,"E905.MirrorCS"),sQuery(id+"F68.wireOp",EDGE,"E906.MirrorCS"),sQuery(id+"F68.wireOp",EDGE,"E907.MirrorCS"),sQuery(id+"F68.wireOp",EDGE,"E908.MirrorCS"),sQuery(id+"F68.wireOp",EDGE,"E909.MirrorCS"),sQuery(id+"F68.wireOp",EDGE,"E910.MirrorCS"),sQuery(id+"F68.wireOp",EDGE,"E911.MirrorCS"),sQuery(id+"F68.wireOp",EDGE,"E912.MirrorCS"),sQuery(id+"F68.wireOp",EDGE,"E913.MirrorCS"),sQuery(id+"F68.wireOp",EDGE,"E914.MirrorCS"),sQuery(id+"F68.wireOp",EDGE,"E915.MirrorCS"),sQuery(id+"F68.wireOp",EDGE,"E916.MirrorCS"),sQuery(id+"F68.wireOp",EDGE,"E917.MirrorCS"),sQuery(id+"F68.wireOp",EDGE,"E918.MirrorCS"),sQuery(id+"F68.wireOp",EDGE,"E919.MirrorCS"),sQuery(id+"F68.wireOp",EDGE,"E920.MirrorCS"),sQuery(id+"F68.wireOp",EDGE,"E921.MirrorCS"),sQuery(id+"F68.wireOp",EDGE,"E922.trimOffspring"),sQuery(id+"F68.wireOp",EDGE,"E923.trimOffspring"),sQuery(id+"F68.wireOp",EDGE,"E924.trimOffspring"),sQuery(id+"F68.wireOp",EDGE,"E925.trimOffspring"),sQuery(id+"F68.wireOp",EDGE,"E926.trimOffspring"),sQuery(id+"F68.wireOp",EDGE,"E927.trimOffspring"),sQuery(id+"F68.wireOp",EDGE,"E928.trimOffspring"),sQuery(id+"F68.wireOp",EDGE,"E929.trimOffspring"),sQuery(id+"F68.wireOp",EDGE,"E930.trimOffspring"),sQuery(id+"F68.wireOp",EDGE,"E931.trimOffspring"),sQuery(id+"F68.wireOp",EDGE,"E933.trimOffspring"),sQuery(id+"F68.wireOp",EDGE,"E934.trimOffspring"),sQuery(id+"F68.wireOp",EDGE,"E935.trimOffspring"),sQuery(id+"F68.wireOp",EDGE,"E936.trimOffspring"),sQuery(id+"F68.wireOp",EDGE,"E937.trimOffspring"),sQuery(id+"F68.wireOp",EDGE,"E938.trimOffspring"),sQuery(id+"F68.wireOp",EDGE,"E939.trimOffspring"),sQuery(id+"F68.wireOp",EDGE,"E940.trimOffspring"),sQuery(id+"F68.wireOp",EDGE,"E941.trimOffspring"),sQuery(id+"F68.wireOp",EDGE,"E942.trimOffspring"),sQuery(id+"F68.wireOp",EDGE,"E943.trimOffspring"),sQuery(id+"F68.wireOp",EDGE,"E944.trimOffspring"),sQuery(id+"F68.wireOp",EDGE,"E945.trimOffspring"),sQuery(id+"F68.wireOp",EDGE,"E946.trimOffspring"),sQuery(id+"F68.wireOp",EDGE,"E947.trimOffspring"),sQuery(id+"F68.wireOp",EDGE,"E948.trimOffspring"),sQuery(id+"F68.wireOp",EDGE,"E949.trimOffspring"),sQuery(id+"F68.wireOp",EDGE,"E950.trimOffspring"),sQuery(id+"F68.wireOp",EDGE,"E951.trimOffspring"),sQuery(id+"F68.wireOp",EDGE,"E952.trimOffspring"),sQuery(id+"F68.wireOp",EDGE,"E953.trimOffspring"),sQuery(id+"F68.wireOp",EDGE,"E954.trimOffspring"),sQuery(id+"F68.wireOp",EDGE,"E955.trimOffspring"),sQuery(id+"F68.wireOp",EDGE,"E956.trimOffspring"),sQuery(id+"F68.wireOp",EDGE,"E957.trimOffspring"),sQuery(id+"F68.wireOp",EDGE,"E958.trimOffspring"),sQuery(id+"F68.wireOp",EDGE,"E959.trimOffspring"),sQuery(id+"F68.wireOp",EDGE,"E960.trimOffspring"),sQuery(id+"F68.wireOp",EDGE,"E961.trimOffspring"),sQuery(id+"F68.wireOp",EDGE,"E962.trimOffspring"),sQuery(id+"F68.wireOp",EDGE,"E963.trimOffspring"),sQuery(id+"F68.wireOp",EDGE,"E964.trimOffspring"),sQuery(id+"F68.wireOp",EDGE,"E965.trimOffspring"),sQuery(id+"F68.wireOp",EDGE,"E966.trimOffspring"),sQuery(id+"F68.wireOp",EDGE,"E967.trimOffspring"),sQuery(id+"F68.wireOp",EDGE,"E968.trimOffspring"),sQuery(id+"F68.wireOp",EDGE,"E969.trimOffspring"),sQuery(id+"F68.wireOp",EDGE,"E970.trimOffspring"),sQuery(id+"F68.wireOp",EDGE,"E971.trimOffspring"),sQuery(id+"F68.wireOp",EDGE,"E972.trimOffspring"),sQuery(id+"F68.wireOp",EDGE,"E973.trimOffspring"),sQuery(id+"F68.wireOp",EDGE,"E974.trimOffspring"),sQuery(id+"F68.wireOp",EDGE,"E975.trimOffspring"),sQuery(id+"F68.wireOp",EDGE,"E976.trimOffspring"),sQuery(id+"F68.wireOp",EDGE,"E977.trimOffspring"),sQuery(id+"F68.wireOp",EDGE,"E978.trimOffspring"),sQuery(id+"F68.wireOp",EDGE,"E979.trimOffspring"),sQuery(id+"F68.wireOp",EDGE,"E901")])],"isStart":false}),makeQuery(id+"F71.opExtrude","CAP_FACE",FACE,{"disambiguationData":[OSD([sQuery(id+"F70.wireOp",EDGE,"E1028.bottom"),sQuery(id+"F70.wireOp",EDGE,"E1028.top"),sQuery(id+"F70.wireOp",EDGE,"E1028.left"),sQuery(id+"F70.wireOp",EDGE,"E1028.right")])],"isStart":true}),makeQuery(id+"F71.opExtrude","CAP_FACE",FACE,{"disambiguationData":[OSD([sQuery(id+"F70.wireOp",EDGE,"E1031.MirrorCS"),sQuery(id+"F70.wireOp",EDGE,"E1032.MirrorCS"),sQuery(id+"F70.wireOp",EDGE,"E1033.MirrorCS"),sQuery(id+"F70.wireOp",EDGE,"E1034.MirrorCS")])],"isStart":true}),makeQuery(id+"F71.opExtrude","CAP_FACE",FACE,{"disambiguationData":[OSD([sQuery(id+"F70.wireOp",EDGE,"E1035.MirrorCS"),sQuery(id+"F70.wireOp",EDGE,"E1036.MirrorCS"),sQuery(id+"F70.wireOp",EDGE,"E1037.MirrorCS"),sQuery(id+"F70.wireOp",EDGE,"E1038.MirrorCS")])],"isStart":true}),makeQuery(id+"F71.opExtrude","CAP_FACE",FACE,{"disambiguationData":[OSD([sQuery(id+"F70.wireOp",EDGE,"E1039.MirrorCS"),sQuery(id+"F70.wireOp",EDGE,"E1040.MirrorCS"),sQuery(id+"F70.wireOp",EDGE,"E1041.MirrorCS"),sQuery(id+"F70.wireOp",EDGE,"E1042.MirrorCS")])],"isStart":true})]}),makeQuery(id+"F73.opExtrude","CAP_FACE",FACE,{"disambiguationData":[OSD([sQuery(id+"F72.wireOp",EDGE,"E1047.MirrorCS"),sQuery(id+"F72.wireOp",EDGE,"E1048.MirrorCS"),sQuery(id+"F72.wireOp",EDGE,"E1051"),sQuery(id+"F72.wireOp",EDGE,"E1052")])],"isStart":true}),makeQuery(id+"F73.opExtrude","CAP_FACE",FACE,{"disambiguationData":[OSD([sQuery(id+"F72.wireOp",EDGE,"E1049.MirrorCS"),sQuery(id+"F72.wireOp",EDGE,"E1050.MirrorCS"),sQuery(id+"F72.wireOp",EDGE,"E1053"),sQuery(id+"F72.wireOp",EDGE,"E1054")])],"isStart":true})]});
            extrude(context, id + "F85", {"entities" : qUnion([Q0]), "operationType" : NewBodyOperationType.ADD, "endBound" : BoundingType.UP_TO_SURFACE, "depth" : 25.4 * mm, "endBoundEntityFace" : qUnion([Q1]), "offsetDistance" : 25.4 * mm});
        }
        {
            var Q0;
            Q0=makeQuery(id+"F63.opExtrude","CAP_FACE",FACE,{"disambiguationData":[OSD([sQuery(id+"F62.wireOp",EDGE,"E819"),sQuery(id+"F62.wireOp",EDGE,"E820.MirrorCS"),sQuery(id+"F62.wireOp",EDGE,"E828"),sQuery(id+"F62.wireOp",EDGE,"E829"),sQuery(id+"F62.wireOp",EDGE,"E830"),sQuery(id+"F62.wireOp",EDGE,"E831.MirrorCS"),sQuery(id+"F62.wireOp",EDGE,"E832.MirrorCS"),sQuery(id+"F62.wireOp",EDGE,"E833.MirrorCS"),sQuery(id+"F62.wireOp",EDGE,"E834"),sQuery(id+"F62.wireOp",EDGE,"E835"),sQuery(id+"F62.wireOp",EDGE,"E836"),sQuery(id+"F62.wireOp",EDGE,"E837"),sQuery(id+"F62.wireOp",EDGE,"E838.MirrorCS"),sQuery(id+"F62.wireOp",EDGE,"E839.MirrorCS"),sQuery(id+"F62.wireOp",EDGE,"E840.MirrorCS"),sQuery(id+"F62.wireOp",EDGE,"E841.MirrorCS"),sQuery(id+"F62.wireOp",EDGE,"E846"),sQuery(id+"F62.wireOp",EDGE,"E855"),sQuery(id+"F62.wireOp",EDGE,"E856.trimOffspring"),sQuery(id+"F62.wireOp",EDGE,"E857.trimOffspring"),sQuery(id+"F62.wireOp",EDGE,"E858.trimOffspring"),sQuery(id+"F62.wireOp",EDGE,"E859.trimOffspring"),sQuery(id+"F62.wireOp",EDGE,"E860"),sQuery(id+"F62.wireOp",EDGE,"E861"),sQuery(id+"F62.wireOp",EDGE,"E862"),sQuery(id+"F62.wireOp",EDGE,"E863"),sQuery(id+"F62.wireOp",EDGE,"E864.MirrorCS"),sQuery(id+"F62.wireOp",EDGE,"E865.MirrorCS"),sQuery(id+"F62.wireOp",EDGE,"E866.MirrorCS"),sQuery(id+"F62.wireOp",EDGE,"E867.MirrorCS")])],"isStart":false});
            var sketch = newSketch(context, id + "F86", { "sketchPlane" : qUnion([Q0])});
            skCircle(sketch, "E1227.0.0", {"center": v(-101.6, -50.8) * mm, "radius": 10.03 * mm});
            skSolve(sketch);
        }
        {
            var Q0;
            Q0 = qSketchRegion(id + "F86", true);
            var Q1;
            {var subQ4=sQuery(id+"F4.wireOp",EDGE,"E8");var subQ5=makeQuery(id+"F5.boolean.opBoolean","COPY",FACE,{"derivedFrom":makeQuery(id+"F5.opExtrude","SWEPT_FACE",FACE,{"disambiguationData":[OSD([subQ4])]})});var subQ8=makeQuery(id+"F5.boolean.opBoolean","COPY",FACE,{"derivedFrom":makeQuery(id+"F5.opExtrude","CAP_FACE",FACE,{"disambiguationData":[OSD([subQ4])],"isStart":false})});Q1=makeQuery(id+"F67.boolean.opBoolean","MERGE",FACE,{"derivedFrom":[makeQuery(id+"F63.boolean.opBoolean","SPLIT",FACE,{"disambiguationData":[TD([makeQuery(id+"F40.opPattern","COPY",FACE,{"derivedFrom":makeQuery(id+"F39.opPattern","COPY",FACE,{"derivedFrom":makeQuery(id+"F19.opPattern","COPY",FACE,{"derivedFrom":makeQuery(id+"F16.opPattern","COPY",FACE,{"derivedFrom":subQ5,"instanceName":"1"}),"instanceName":"1"}),"instanceName":"1"}),"instanceName":"1"})])],"derivedFrom":makeQuery(id+"F40.opPattern","COPY",FACE,{"derivedFrom":makeQuery(id+"F39.opPattern","COPY",FACE,{"derivedFrom":makeQuery(id+"F21.boolean.opBoolean","MERGE",FACE,{"derivedFrom":[makeQuery(id+"F19.opPattern","COPY",FACE,{"derivedFrom":makeQuery(id+"F16.opPattern","COPY",FACE,{"derivedFrom":makeQuery(id+"F9.boolean.opBoolean","SPLIT",FACE,{"disambiguationData":[TD([subQ5])],"derivedFrom":subQ8}),"instanceName":"1"}),"instanceName":"1"}),makeQuery(id+"F19.opPattern","COPY",FACE,{"derivedFrom":makeQuery(id+"F16.opPattern","COPY",FACE,{"derivedFrom":makeQuery(id+"F9.boolean.opBoolean","SPLIT",FACE,{"disambiguationData":[TD([makeQuery(id+"F9.opExtrude","SWEPT_FACE",FACE,{"disambiguationData":[OSD([sQuery(id+"F8.wireOp",EDGE,"E25")])]})])],"derivedFrom":subQ8}),"instanceName":"1"}),"instanceName":"1"}),makeQuery(id+"F19.opPattern","COPY",FACE,{"derivedFrom":makeQuery(id+"F16.opPattern","COPY",FACE,{"derivedFrom":makeQuery(id+"F9.boolean.opBoolean","SPLIT",FACE,{"disambiguationData":[TD([makeQuery(id+"F9.opExtrude","SWEPT_FACE",FACE,{"disambiguationData":[OSD([sQuery(id+"F8.wireOp",EDGE,"E32")])]})])],"derivedFrom":subQ8}),"instanceName":"1"}),"instanceName":"1"}),makeQuery(id+"F19.opPattern","COPY",FACE,{"derivedFrom":makeQuery(id+"F16.opPattern","COPY",FACE,{"derivedFrom":makeQuery(id+"F9.boolean.opBoolean","SPLIT",FACE,{"disambiguationData":[TD([makeQuery(id+"F9.opExtrude","SWEPT_FACE",FACE,{"disambiguationData":[OSD([sQuery(id+"F8.wireOp",EDGE,"E33.0")])]})])],"derivedFrom":subQ8}),"instanceName":"1"}),"instanceName":"1"}),makeQuery(id+"F19.opPattern","COPY",FACE,{"derivedFrom":makeQuery(id+"F16.opPattern","COPY",FACE,{"derivedFrom":makeQuery(id+"F9.boolean.opBoolean","SPLIT",FACE,{"disambiguationData":[TD([makeQuery(id+"F9.opExtrude","SWEPT_FACE",FACE,{"disambiguationData":[OSD([sQuery(id+"F8.wireOp",EDGE,"E37")])]})])],"derivedFrom":subQ8}),"instanceName":"1"}),"instanceName":"1"}),makeQuery(id+"F19.opPattern","COPY",FACE,{"derivedFrom":makeQuery(id+"F16.opPattern","COPY",FACE,{"derivedFrom":makeQuery(id+"F9.boolean.opBoolean","SPLIT",FACE,{"disambiguationData":[TD([makeQuery(id+"F9.opExtrude","SWEPT_FACE",FACE,{"disambiguationData":[OSD([sQuery(id+"F8.wireOp",EDGE,"E51.MirrorCS")])]})])],"derivedFrom":subQ8}),"instanceName":"1"}),"instanceName":"1"}),makeQuery(id+"F19.opPattern","COPY",FACE,{"derivedFrom":makeQuery(id+"F16.opPattern","COPY",FACE,{"derivedFrom":makeQuery(id+"F9.boolean.opBoolean","SPLIT",FACE,{"disambiguationData":[TD([makeQuery(id+"F9.opExtrude","SWEPT_FACE",FACE,{"disambiguationData":[OSD([sQuery(id+"F8.wireOp",EDGE,"E53.MirrorCS")])]})])],"derivedFrom":subQ8}),"instanceName":"1"}),"instanceName":"1"}),makeQuery(id+"F19.opPattern","COPY",FACE,{"derivedFrom":makeQuery(id+"F16.opPattern","COPY",FACE,{"derivedFrom":makeQuery(id+"F9.boolean.opBoolean","SPLIT",FACE,{"disambiguationData":[TD([makeQuery(id+"F9.opExtrude","SWEPT_FACE",FACE,{"disambiguationData":[OSD([sQuery(id+"F8.wireOp",EDGE,"E80")])]})])],"derivedFrom":subQ8}),"instanceName":"1"}),"instanceName":"1"}),makeQuery(id+"F19.opPattern","COPY",FACE,{"derivedFrom":makeQuery(id+"F16.opPattern","COPY",FACE,{"derivedFrom":makeQuery(id+"F9.boolean.opBoolean","SPLIT",FACE,{"disambiguationData":[TD([makeQuery(id+"F9.opExtrude","SWEPT_FACE",FACE,{"disambiguationData":[OSD([sQuery(id+"F8.wireOp",EDGE,"E83")])]})])],"derivedFrom":subQ8}),"instanceName":"1"}),"instanceName":"1"})],"fromTools":[makeQuery(id+"F21.opExtrude","CAP_FACE",FACE,{"disambiguationData":[OSD([sQuery(id+"F20.wireOp",EDGE,"E307.0.0")])],"isStart":false})]}),"instanceName":"1"}),"instanceName":"1"})})],"fromTools":[makeQuery(id+"F67.opExtrude","CAP_FACE",FACE,{"disambiguationData":[OSD([sQuery(id+"F66.wireOp",EDGE,"E887"),sQuery(id+"F66.wireOp",EDGE,"E888"),sQuery(id+"F66.wireOp",EDGE,"E889.0"),sQuery(id+"F66.wireOp",EDGE,"E890.0"),sQuery(id+"F66.wireOp",EDGE,"E892.MirrorCS"),sQuery(id+"F66.wireOp",EDGE,"E893.MirrorCS"),sQuery(id+"F66.wireOp",EDGE,"E894.trimOffspring"),sQuery(id+"F66.wireOp",EDGE,"E895"),sQuery(id+"F66.wireOp",EDGE,"E896"),sQuery(id+"F66.wireOp",EDGE,"E897.MirrorCS"),sQuery(id+"F66.wireOp",EDGE,"E898.MirrorCS")])],"isStart":false})]});}
            extrude(context, id + "F87", {"entities" : qUnion([Q0]), "operationType" : NewBodyOperationType.REMOVE, "endBound" : BoundingType.UP_TO_SURFACE, "oppositeDirection" : true, "depth" : 25.4 * mm, "endBoundEntityFace" : qUnion([Q1]), "offsetDistance" : 25.4 * mm});
        }
        {
            var Q0;
            {var subQ4=sQuery(id+"F4.wireOp",EDGE,"E8");var subQ5=makeQuery(id+"F5.boolean.opBoolean","COPY",FACE,{"derivedFrom":makeQuery(id+"F5.opExtrude","SWEPT_FACE",FACE,{"disambiguationData":[OSD([subQ4])]})});var subQ8=makeQuery(id+"F5.boolean.opBoolean","COPY",FACE,{"derivedFrom":makeQuery(id+"F5.opExtrude","CAP_FACE",FACE,{"disambiguationData":[OSD([subQ4])],"isStart":false})});var subQ9=makeQuery(id+"F40.opPattern","COPY",FACE,{"derivedFrom":makeQuery(id+"F39.opPattern","COPY",FACE,{"derivedFrom":makeQuery(id+"F21.boolean.opBoolean","MERGE",FACE,{"derivedFrom":[makeQuery(id+"F19.opPattern","COPY",FACE,{"derivedFrom":makeQuery(id+"F16.opPattern","COPY",FACE,{"derivedFrom":makeQuery(id+"F9.boolean.opBoolean","SPLIT",FACE,{"disambiguationData":[TD([subQ5])],"derivedFrom":subQ8}),"instanceName":"1"}),"instanceName":"1"}),makeQuery(id+"F19.opPattern","COPY",FACE,{"derivedFrom":makeQuery(id+"F16.opPattern","COPY",FACE,{"derivedFrom":makeQuery(id+"F9.boolean.opBoolean","SPLIT",FACE,{"disambiguationData":[TD([makeQuery(id+"F9.opExtrude","SWEPT_FACE",FACE,{"disambiguationData":[OSD([sQuery(id+"F8.wireOp",EDGE,"E25")])]})])],"derivedFrom":subQ8}),"instanceName":"1"}),"instanceName":"1"}),makeQuery(id+"F19.opPattern","COPY",FACE,{"derivedFrom":makeQuery(id+"F16.opPattern","COPY",FACE,{"derivedFrom":makeQuery(id+"F9.boolean.opBoolean","SPLIT",FACE,{"disambiguationData":[TD([makeQuery(id+"F9.opExtrude","SWEPT_FACE",FACE,{"disambiguationData":[OSD([sQuery(id+"F8.wireOp",EDGE,"E32")])]})])],"derivedFrom":subQ8}),"instanceName":"1"}),"instanceName":"1"}),makeQuery(id+"F19.opPattern","COPY",FACE,{"derivedFrom":makeQuery(id+"F16.opPattern","COPY",FACE,{"derivedFrom":makeQuery(id+"F9.boolean.opBoolean","SPLIT",FACE,{"disambiguationData":[TD([makeQuery(id+"F9.opExtrude","SWEPT_FACE",FACE,{"disambiguationData":[OSD([sQuery(id+"F8.wireOp",EDGE,"E33.0")])]})])],"derivedFrom":subQ8}),"instanceName":"1"}),"instanceName":"1"}),makeQuery(id+"F19.opPattern","COPY",FACE,{"derivedFrom":makeQuery(id+"F16.opPattern","COPY",FACE,{"derivedFrom":makeQuery(id+"F9.boolean.opBoolean","SPLIT",FACE,{"disambiguationData":[TD([makeQuery(id+"F9.opExtrude","SWEPT_FACE",FACE,{"disambiguationData":[OSD([sQuery(id+"F8.wireOp",EDGE,"E37")])]})])],"derivedFrom":subQ8}),"instanceName":"1"}),"instanceName":"1"}),makeQuery(id+"F19.opPattern","COPY",FACE,{"derivedFrom":makeQuery(id+"F16.opPattern","COPY",FACE,{"derivedFrom":makeQuery(id+"F9.boolean.opBoolean","SPLIT",FACE,{"disambiguationData":[TD([makeQuery(id+"F9.opExtrude","SWEPT_FACE",FACE,{"disambiguationData":[OSD([sQuery(id+"F8.wireOp",EDGE,"E51.MirrorCS")])]})])],"derivedFrom":subQ8}),"instanceName":"1"}),"instanceName":"1"}),makeQuery(id+"F19.opPattern","COPY",FACE,{"derivedFrom":makeQuery(id+"F16.opPattern","COPY",FACE,{"derivedFrom":makeQuery(id+"F9.boolean.opBoolean","SPLIT",FACE,{"disambiguationData":[TD([makeQuery(id+"F9.opExtrude","SWEPT_FACE",FACE,{"disambiguationData":[OSD([sQuery(id+"F8.wireOp",EDGE,"E53.MirrorCS")])]})])],"derivedFrom":subQ8}),"instanceName":"1"}),"instanceName":"1"}),makeQuery(id+"F19.opPattern","COPY",FACE,{"derivedFrom":makeQuery(id+"F16.opPattern","COPY",FACE,{"derivedFrom":makeQuery(id+"F9.boolean.opBoolean","SPLIT",FACE,{"disambiguationData":[TD([makeQuery(id+"F9.opExtrude","SWEPT_FACE",FACE,{"disambiguationData":[OSD([sQuery(id+"F8.wireOp",EDGE,"E80")])]})])],"derivedFrom":subQ8}),"instanceName":"1"}),"instanceName":"1"}),makeQuery(id+"F19.opPattern","COPY",FACE,{"derivedFrom":makeQuery(id+"F16.opPattern","COPY",FACE,{"derivedFrom":makeQuery(id+"F9.boolean.opBoolean","SPLIT",FACE,{"disambiguationData":[TD([makeQuery(id+"F9.opExtrude","SWEPT_FACE",FACE,{"disambiguationData":[OSD([sQuery(id+"F8.wireOp",EDGE,"E83")])]})])],"derivedFrom":subQ8}),"instanceName":"1"}),"instanceName":"1"})],"fromTools":[makeQuery(id+"F21.opExtrude","CAP_FACE",FACE,{"disambiguationData":[OSD([sQuery(id+"F20.wireOp",EDGE,"E307.0.0")])],"isStart":false})]}),"instanceName":"1"}),"instanceName":"1"});Q0=makeQuery(id+"F87.boolean.opBoolean","MERGE",FACE,{"derivedFrom":[makeQuery(id+"F63.boolean.opBoolean","SPLIT",FACE,{"disambiguationData":[TD([makeQuery(id+"F63.opExtrude","SWEPT_FACE",FACE,{"disambiguationData":[OSD([sQuery(id+"F62.wireOp",EDGE,"E828")])]})])],"derivedFrom":subQ9}),makeQuery(id+"F63.boolean.opBoolean","SPLIT",FACE,{"disambiguationData":[TD([makeQuery(id+"F63.opExtrude","SWEPT_FACE",FACE,{"disambiguationData":[OSD([sQuery(id+"F62.wireOp",EDGE,"E834")])]})])],"derivedFrom":subQ9}),makeQuery(id+"F63.boolean.opBoolean","SPLIT",FACE,{"disambiguationData":[TD([makeQuery(id+"F63.opExtrude","SWEPT_FACE",FACE,{"disambiguationData":[OSD([sQuery(id+"F62.wireOp",EDGE,"E838.MirrorCS")])]})])],"derivedFrom":subQ9}),makeQuery(id+"F63.boolean.opBoolean","SPLIT",FACE,{"disambiguationData":[TD([makeQuery(id+"F63.opExtrude","SWEPT_FACE",FACE,{"disambiguationData":[OSD([sQuery(id+"F62.wireOp",EDGE,"E842")])]})])],"derivedFrom":subQ9}),makeQuery(id+"F67.boolean.opBoolean","MERGE",FACE,{"derivedFrom":[makeQuery(id+"F63.boolean.opBoolean","SPLIT",FACE,{"disambiguationData":[TD([makeQuery(id+"F40.opPattern","COPY",FACE,{"derivedFrom":makeQuery(id+"F39.opPattern","COPY",FACE,{"derivedFrom":makeQuery(id+"F19.opPattern","COPY",FACE,{"derivedFrom":makeQuery(id+"F16.opPattern","COPY",FACE,{"derivedFrom":subQ5,"instanceName":"1"}),"instanceName":"1"}),"instanceName":"1"}),"instanceName":"1"})])],"derivedFrom":subQ9})],"fromTools":[makeQuery(id+"F67.opExtrude","CAP_FACE",FACE,{"disambiguationData":[OSD([sQuery(id+"F66.wireOp",EDGE,"E887"),sQuery(id+"F66.wireOp",EDGE,"E888"),sQuery(id+"F66.wireOp",EDGE,"E889.0"),sQuery(id+"F66.wireOp",EDGE,"E890.0"),sQuery(id+"F66.wireOp",EDGE,"E892.MirrorCS"),sQuery(id+"F66.wireOp",EDGE,"E893.MirrorCS"),sQuery(id+"F66.wireOp",EDGE,"E894.trimOffspring"),sQuery(id+"F66.wireOp",EDGE,"E895"),sQuery(id+"F66.wireOp",EDGE,"E896"),sQuery(id+"F66.wireOp",EDGE,"E897.MirrorCS"),sQuery(id+"F66.wireOp",EDGE,"E898.MirrorCS")])],"isStart":false})]})],"fromTools":[makeQuery(id+"F87.opExtrude","CAP_FACE",FACE,{"disambiguationData":[OSD([sQuery(id+"F86.wireOp",EDGE,"E1227.0.0")])],"isStart":false})]});}
            var sketch = newSketch(context, id + "F88", { "sketchPlane" : qUnion([Q0])});
            skLineSegment(sketch, "E1228", {"start": v(-101.6, -50.8) * mm, "end": v(-101.6, -53.82) * mm});
            skLineSegment(sketch, "E1229", {"start": v(-101.1, -53.82) * mm, "end": v(-101.6, -52.3) * mm});
            skLineSegment(sketch, "E1230.MirrorCS", {"start": v(-102.1, -53.82) * mm, "end": v(-101.6, -52.3) * mm});
            skArc(sketch, "E1231", {"start": v(-102.08, -49.37) * mm, "mid": v(-102.91, -50.78) * mm, "end": v(-102.32, -52.31) * mm});
            skLineSegment(sketch, "E1232", {"start": v(-102.32, -52.31) * mm, "end": v(-103.02, -53.17) * mm});
            skLineSegment(sketch, "E1233", {"start": v(-103.02, -53.17) * mm, "end": v(-102.9, -52.31) * mm});
            skArc(sketch, "E1234.0", {"start": v(-101.76, -48.63) * mm, "mid": v(-102.04, -48.73) * mm, "end": v(-102.3, -48.87) * mm});
            skLineSegment(sketch, "E1235", {"start": v(-103.39, -50.4) * mm, "end": v(-104.13, -50.2) * mm});
            skLineSegment(sketch, "E1236", {"start": v(-104.13, -50.2) * mm, "end": v(-103.43, -50.66) * mm});
            skLineSegment(sketch, "E1237", {"start": v(-102.3, -48.87) * mm, "end": v(-102.56, -48.2) * mm});
            skLineSegment(sketch, "E1238", {"start": v(-102.56, -48.2) * mm, "end": v(-102.49, -49) * mm});
            skLineSegment(sketch, "E1239.MirrorCS", {"start": v(-99.07, -50.2) * mm, "end": v(-99.77, -50.66) * mm});
            skLineSegment(sketch, "E1240.MirrorCS", {"start": v(-100.18, -53.17) * mm, "end": v(-100.3, -52.31) * mm});
            skLineSegment(sketch, "E1241.MirrorCS", {"start": v(-99.81, -50.4) * mm, "end": v(-99.07, -50.2) * mm});
            skLineSegment(sketch, "E1242.MirrorCS", {"start": v(-100.64, -48.2) * mm, "end": v(-100.71, -49) * mm});
            skLineSegment(sketch, "E1243.MirrorCS", {"start": v(-100.9, -48.87) * mm, "end": v(-100.64, -48.2) * mm});
            skArc(sketch, "E1244.MirrorCS", {"start": v(-101.44, -48.63) * mm, "mid": v(-101.16, -48.73) * mm, "end": v(-100.9, -48.87) * mm});
            skArc(sketch, "E1245.MirrorCS", {"start": v(-101.12, -49.37) * mm, "mid": v(-100.29, -50.78) * mm, "end": v(-100.88, -52.31) * mm});
            skLineSegment(sketch, "E1246.MirrorCS", {"start": v(-100.88, -52.31) * mm, "end": v(-100.18, -53.17) * mm});
            skPoint(sketch, "E1247.orphan", {"position": v(-100.77, -49.67) * mm});
            skPoint(sketch, "E1248.orphan", {"position": v(-101.1, -49.38) * mm});
            skPoint(sketch, "E1249.orphan", {"position": v(-102.1, -49.38) * mm});
            skPoint(sketch, "E1250.orphan", {"position": v(-102.43, -49.67) * mm});
            skPoint(sketch, "E1251.orphan", {"position": v(-102.92, -51) * mm});
            skPoint(sketch, "E1252.orphan", {"position": v(-102.69, -52.7) * mm});
            skArc(sketch, "E1253.trimOffspring", {"start": v(-103.43, -50.66) * mm, "mid": v(-103.36, -51.6) * mm, "end": v(-102.92, -52.44) * mm});
            skArc(sketch, "E1254.trimOffspring", {"start": v(-102.49, -49) * mm, "mid": v(-103.06, -49.62) * mm, "end": v(-103.39, -50.4) * mm});
            skArc(sketch, "E1255.trimOffspring", {"start": v(-100.71, -49) * mm, "mid": v(-99.77, -50.63) * mm, "end": v(-100.28, -52.44) * mm});
            skPoint(sketch, "E1256.MirrorCS.start.orphan", {"position": v(-100.33, -50.52) * mm});
            skPoint(sketch, "E1257.orphan", {"position": v(-100.28, -51) * mm});
            skPoint(sketch, "E1258.orphan", {"position": v(-100.51, -52.7) * mm});
            skPoint(sketch, "E1259.start.orphan", {"position": v(-102.87, -50.52) * mm});
            skArc(sketch, "E1260", {"start": v(-101.44, -48.63) * mm, "mid": v(-101.6, -48.6) * mm, "end": v(-101.76, -48.63) * mm});
            skArc(sketch, "E1261.trimOffspring", {"start": v(-102.08, -49.37) * mm, "mid": v(-101.6, -49.67) * mm, "end": v(-101.12, -49.37) * mm});
            skCircle(sketch, "E1262", {"center": v(-101.6, -50.8) * mm, "radius": 0.94 * mm});
            skLineSegment(sketch, "E1263", {"start": v(-104.13, -50.2) * mm, "end": v(-103.43, -51.23) * mm});
            skLineSegment(sketch, "E1264", {"start": v(-102.56, -48.2) * mm, "end": v(-102.78, -49.26) * mm});
            skLineSegment(sketch, "E1265.MirrorCS", {"start": v(-99.07, -50.2) * mm, "end": v(-99.77, -51.23) * mm});
            skLineSegment(sketch, "E1266.MirrorCS", {"start": v(-100.64, -48.2) * mm, "end": v(-100.42, -49.26) * mm});
            skLineSegment(sketch, "E1267", {"start": v(-102.1, -53.82) * mm, "end": v(-101.6, -53.43) * mm});
            skLineSegment(sketch, "E1268", {"start": v(-101.6, -53.43) * mm, "end": v(-101.1, -53.82) * mm});
            skSolve(sketch);
        }
        {
            var Q0;
            Q0=makeQuery(id+"F88.imprint","IMPRINT",FACE,{"disambiguationData":[TD([[makeQuery(id+"F88.imprint","IMPRINT",EDGE,{"derivedFrom":sQuery(id+"F88.wireOp",EDGE,"E1229")}),-1.0]])]});
            var sketch = newSketch(context, id + "F89", { "sketchPlane" : qUnion([Q0])});
            skArc(sketch, "E1269", {"start": v(-99.2, -50.07) * mm, "mid": v(-101.68, -42.1) * mm, "end": v(-104.16, -50.07) * mm});
            skLineSegment(sketch, "E1270.right", {"start": v(-99.7, -50.68) * mm, "end": v(-99.7, -52.72) * mm});
            skPoint(sketch, "E1270.middle", {"position": v(-101.68, -50.85) * mm});
            skLineSegment(sketch, "E1271", {"start": v(-104.16, -50.07) * mm, "end": v(-104.9, -50.57) * mm});
            skLineSegment(sketch, "E1272", {"start": v(-104.9, -50.57) * mm, "end": v(-103.66, -50.68) * mm});
            skLineSegment(sketch, "E1273.MirrorCS", {"start": v(-99.2, -50.07) * mm, "end": v(-98.47, -50.57) * mm});
            skLineSegment(sketch, "E1274.MirrorCS", {"start": v(-98.47, -50.57) * mm, "end": v(-99.7, -50.68) * mm});
            skLineSegment(sketch, "E1275", {"start": v(-101.94, -52.72) * mm, "end": v(-101.94, -51.21) * mm});
            skLineSegment(sketch, "E1276", {"start": v(-101.94, -51.21) * mm, "end": v(-102.32, -52.72) * mm});
            skLineSegment(sketch, "E1277", {"start": v(-102.83, -52.72) * mm, "end": v(-102.83, -51.21) * mm});
            skLineSegment(sketch, "E1278", {"start": v(-102.83, -51.21) * mm, "end": v(-103.15, -52.72) * mm});
            skLineSegment(sketch, "E1279", {"start": v(-102.32, -52.72) * mm, "end": v(-102.83, -52.72) * mm});
            skLineSegment(sketch, "E1280", {"start": v(-103.15, -52.72) * mm, "end": v(-103.66, -52.72) * mm});
            skLineSegment(sketch, "E1281.MirrorCS", {"start": v(-101.43, -52.72) * mm, "end": v(-101.43, -51.21) * mm});
            skLineSegment(sketch, "E1282.MirrorCS", {"start": v(-101.43, -51.21) * mm, "end": v(-101.04, -52.72) * mm});
            skLineSegment(sketch, "E1283.MirrorCS", {"start": v(-100.53, -52.72) * mm, "end": v(-100.53, -51.21) * mm});
            skLineSegment(sketch, "E1284.MirrorCS", {"start": v(-100.53, -51.21) * mm, "end": v(-100.21, -52.72) * mm});
            skLineSegment(sketch, "E1285.MirrorCS", {"start": v(-101.04, -52.72) * mm, "end": v(-100.53, -52.72) * mm});
            skLineSegment(sketch, "E1286.MirrorCS", {"start": v(-100.21, -52.72) * mm, "end": v(-99.7, -52.72) * mm});
            skLineSegment(sketch, "E1287", {"start": v(-101.94, -52.72) * mm, "end": v(-101.43, -52.72) * mm});
            skLineSegment(sketch, "E1288", {"start": v(-101.68, -50.85) * mm, "end": v(-101.68, -48.79) * mm});
            skLineSegment(sketch, "E1289", {"start": v(-101.68, -48.79) * mm, "end": v(-102.34, -50.18) * mm});
            skLineSegment(sketch, "E1290", {"start": v(-102.34, -50.18) * mm, "end": v(-101.68, -49.82) * mm});
            skLineSegment(sketch, "E1291.MirrorCS", {"start": v(-101.68, -48.79) * mm, "end": v(-101.02, -50.18) * mm});
            skLineSegment(sketch, "E1292.MirrorCS", {"start": v(-101.02, -50.18) * mm, "end": v(-101.68, -49.82) * mm});
            skLineSegment(sketch, "E1293.MirrorCS", {"start": v(-99.7, -50.37) * mm, "end": v(-99.7, -52.72) * mm});
            skCircle(sketch, "E1294", {"center": v(-101.68, -46.48) * mm, "radius": 1.18 * mm});
            skLineSegment(sketch, "E1295", {"start": v(-103.67, -49.74) * mm, "end": v(-102.4, -48.5) * mm});
            skArc(sketch, "E1296", {"start": v(-101.68, -43.16) * mm, "mid": v(-103.83, -45.6) * mm, "end": v(-102.4, -48.5) * mm});
            skArc(sketch, "E1297.0", {"start": v(-104.66, -44.74) * mm, "mid": v(-104.81, -45.4) * mm, "end": v(-104.86, -46.07) * mm});
            skLineSegment(sketch, "E1298.trimOffspring", {"start": v(-103.66, -50.68) * mm, "end": v(-103.66, -52.72) * mm});
            skPoint(sketch, "E1270.left.start.orphan", {"position": v(-103.66, -48.97) * mm});
            skPoint(sketch, "E1299.orphan", {"position": v(-99.7, -48.97) * mm});
            skLineSegment(sketch, "E1300", {"start": v(-103.67, -49.74) * mm, "end": v(-103.51, -48.94) * mm});
            skLineSegment(sketch, "E1301", {"start": v(-105.58, -46.48) * mm, "end": v(-104.86, -46.07) * mm});
            skArc(sketch, "E1302", {"start": v(-101.68, -42.7) * mm, "mid": v(-102.63, -42.95) * mm, "end": v(-103.48, -43.42) * mm});
            skLineSegment(sketch, "E1303", {"start": v(-103.76, -43.64) * mm, "end": v(-104.18, -43.23) * mm});
            skLineSegment(sketch, "E1304", {"start": v(-104.18, -43.23) * mm, "end": v(-103.48, -43.42) * mm});
            skArc(sketch, "E1305.MirrorCS", {"start": v(-101.68, -43.16) * mm, "mid": v(-99.53, -45.6) * mm, "end": v(-100.95, -48.5) * mm});
            skLineSegment(sketch, "E1306.MirrorCS", {"start": v(-99.7, -49.74) * mm, "end": v(-99.85, -48.94) * mm});
            skArc(sketch, "E1307.MirrorCS", {"start": v(-101.68, -42.7) * mm, "mid": v(-100.74, -42.95) * mm, "end": v(-99.88, -43.42) * mm});
            skLineSegment(sketch, "E1308.MirrorCS", {"start": v(-97.79, -46.48) * mm, "end": v(-98.5, -46.07) * mm});
            skLineSegment(sketch, "E1309.MirrorCS", {"start": v(-98.54, -46.48) * mm, "end": v(-97.79, -46.48) * mm});
            skLineSegment(sketch, "E1310.MirrorCS", {"start": v(-99.6, -43.64) * mm, "end": v(-99.19, -43.23) * mm});
            skArc(sketch, "E1311.MirrorCS", {"start": v(-98.7, -44.74) * mm, "mid": v(-98.55, -45.4) * mm, "end": v(-98.5, -46.07) * mm});
            skLineSegment(sketch, "E1312.MirrorCS", {"start": v(-99.19, -43.23) * mm, "end": v(-99.88, -43.42) * mm});
            skLineSegment(sketch, "E1313.MirrorCS", {"start": v(-99.7, -49.74) * mm, "end": v(-100.95, -48.5) * mm});
            skArc(sketch, "E1314.MirrorCS", {"start": v(-104.17, -50.07) * mm, "mid": v(-101.68, -42.1) * mm, "end": v(-99.2, -50.07) * mm});
            skArc(sketch, "E1315", {"start": v(-102.45, -43.49) * mm, "mid": v(-101.68, -44.58) * mm, "end": v(-100.87, -43.52) * mm});
            skPoint(sketch, "E1316.orphan", {"position": v(-103.27, -47.74) * mm});
            skArc(sketch, "E1317.trimOffspring", {"start": v(-103.15, -49.22) * mm, "mid": v(-103.03, -49.3) * mm, "end": v(-102.91, -49.37) * mm});
            skPoint(sketch, "E1318.orphan", {"position": v(-103.82, -46.48) * mm});
            skPoint(sketch, "E1319.orphan", {"position": v(-103.81, -45.47) * mm});
            skArc(sketch, "E1320.trimOffspring", {"start": v(-104.78, -46.78) * mm, "mid": v(-104.32, -47.97) * mm, "end": v(-103.51, -48.94) * mm});
            skPoint(sketch, "E1321.orphan", {"position": v(-103.23, -44.18) * mm});
            skPoint(sketch, "E1322.orphan", {"position": v(-102.68, -43.64) * mm});
            skArc(sketch, "E1323.trimOffspring", {"start": v(-103.98, -43.85) * mm, "mid": v(-104.35, -44.27) * mm, "end": v(-104.66, -44.74) * mm});
            skLineSegment(sketch, "E1324", {"start": v(-104.18, -43.23) * mm, "end": v(-103.98, -43.85) * mm});
            skLineSegment(sketch, "E1325", {"start": v(-105.58, -46.48) * mm, "end": v(-104.78, -46.78) * mm});
            skLineSegment(sketch, "E1326.MirrorCS", {"start": v(-97.79, -46.48) * mm, "end": v(-98.59, -46.78) * mm});
            skLineSegment(sketch, "E1327.MirrorCS", {"start": v(-99.19, -43.23) * mm, "end": v(-99.38, -43.85) * mm});
            skPoint(sketch, "E1328.orphan", {"position": v(-100.69, -43.64) * mm});
            skPoint(sketch, "E1329.orphan", {"position": v(-100.13, -44.18) * mm});
            skArc(sketch, "E1330.trimOffspring", {"start": v(-99.38, -43.85) * mm, "mid": v(-99.01, -44.27) * mm, "end": v(-98.7, -44.74) * mm});
            skPoint(sketch, "E1331.orphan", {"position": v(-99.55, -45.47) * mm});
            skPoint(sketch, "E1332.orphan", {"position": v(-99.55, -46.48) * mm});
            skArc(sketch, "E1333.trimOffspring", {"start": v(-98.59, -46.78) * mm, "mid": v(-99.04, -47.97) * mm, "end": v(-99.85, -48.94) * mm});
            skPoint(sketch, "E1334.orphan", {"position": v(-100.1, -47.74) * mm});
            skArc(sketch, "E1335.trimOffspring", {"start": v(-100.22, -49.22) * mm, "mid": v(-100.33, -49.3) * mm, "end": v(-100.45, -49.37) * mm});
            skSolve(sketch);
        }
        {
            var Q0;
            Q0 = qSketchRegion(id + "F89", true);
            var Q1;
            Q1=makeQuery(id+"F32.opExtrude","CAP_FACE",FACE,{"disambiguationData":[OSD([sQuery(id+"F31.wireOp",EDGE,"E444"),sQuery(id+"F31.wireOp",EDGE,"E445"),sQuery(id+"F31.wireOp",EDGE,"E446.left"),sQuery(id+"F31.wireOp",EDGE,"E446.right"),sQuery(id+"F31.wireOp",EDGE,"E447.MirrorCS"),sQuery(id+"F31.wireOp",EDGE,"E448.MirrorCS"),sQuery(id+"F31.wireOp",EDGE,"E449.MirrorCS"),sQuery(id+"F31.wireOp",EDGE,"E450.MirrorCS"),sQuery(id+"F31.wireOp",EDGE,"E451.MirrorCS"),sQuery(id+"F31.wireOp",EDGE,"E452.MirrorCS"),sQuery(id+"F31.wireOp",EDGE,"E453.trimOffspring"),sQuery(id+"F31.wireOp",EDGE,"E454.trimOffspring"),sQuery(id+"F31.wireOp",EDGE,"E455.trimOffspring"),sQuery(id+"F31.wireOp",EDGE,"E456.trimOffspring"),sQuery(id+"F31.wireOp",EDGE,"E457.trimOffspring"),sQuery(id+"F31.wireOp",EDGE,"E458.trimOffspring"),sQuery(id+"F31.wireOp",EDGE,"E459.trimOffspring"),sQuery(id+"F31.wireOp",EDGE,"E460.trimOffspring"),sQuery(id+"F31.wireOp",EDGE,"E461.trimOffspring"),sQuery(id+"F31.wireOp",EDGE,"E462.trimOffspring"),sQuery(id+"F31.wireOp",EDGE,"E463.trimOffspring"),sQuery(id+"F31.wireOp",EDGE,"E464.trimOffspring"),sQuery(id+"F31.wireOp",EDGE,"E465.trimOffspring"),sQuery(id+"F31.wireOp",EDGE,"E466.trimOffspring"),sQuery(id+"F31.wireOp",EDGE,"E467.trimOffspring"),sQuery(id+"F31.wireOp",EDGE,"E468.trimOffspring"),sQuery(id+"F31.wireOp",EDGE,"E469.trimOffspring"),sQuery(id+"F31.wireOp",EDGE,"E470.trimOffspring"),sQuery(id+"F31.wireOp",EDGE,"E471.trimOffspring"),sQuery(id+"F31.wireOp",EDGE,"E472.trimOffspring"),sQuery(id+"F31.wireOp",EDGE,"E473.trimOffspring"),sQuery(id+"F31.wireOp",EDGE,"E474.trimOffspring"),sQuery(id+"F31.wireOp",EDGE,"E475")])],"isStart":false});
            extrude(context, id + "F90", {"entities" : qUnion([Q0]), "operationType" : NewBodyOperationType.ADD, "endBound" : BoundingType.UP_TO_SURFACE, "depth" : 25.4 * mm, "endBoundEntityFace" : qUnion([Q1]), "offsetDistance" : 25.4 * mm});
        }
        {
            var Q0;
            {var subQ0=sQuery(id+"F4.wireOp",EDGE,"E8");var subQ1=makeQuery(id+"F5.boolean.opBoolean","COPY",FACE,{"derivedFrom":makeQuery(id+"F5.opExtrude","SWEPT_FACE",FACE,{"disambiguationData":[OSD([subQ0])]})});var subQ2=makeQuery(id+"F40.opPattern","COPY",FACE,{"derivedFrom":makeQuery(id+"F39.opPattern","COPY",FACE,{"derivedFrom":makeQuery(id+"F19.opPattern","COPY",FACE,{"derivedFrom":makeQuery(id+"F16.opPattern","COPY",FACE,{"derivedFrom":subQ1,"instanceName":"1"}),"instanceName":"1"}),"instanceName":"1"}),"instanceName":"1"});var subQ9=makeQuery(id+"F5.boolean.opBoolean","COPY",FACE,{"derivedFrom":makeQuery(id+"F5.opExtrude","CAP_FACE",FACE,{"disambiguationData":[OSD([subQ0])],"isStart":false})});var subQ10=makeQuery(id+"F40.opPattern","COPY",FACE,{"derivedFrom":makeQuery(id+"F39.opPattern","COPY",FACE,{"derivedFrom":makeQuery(id+"F21.boolean.opBoolean","MERGE",FACE,{"derivedFrom":[makeQuery(id+"F19.opPattern","COPY",FACE,{"derivedFrom":makeQuery(id+"F16.opPattern","COPY",FACE,{"derivedFrom":makeQuery(id+"F9.boolean.opBoolean","SPLIT",FACE,{"disambiguationData":[TD([subQ1])],"derivedFrom":subQ9}),"instanceName":"1"}),"instanceName":"1"}),makeQuery(id+"F19.opPattern","COPY",FACE,{"derivedFrom":makeQuery(id+"F16.opPattern","COPY",FACE,{"derivedFrom":makeQuery(id+"F9.boolean.opBoolean","SPLIT",FACE,{"disambiguationData":[TD([makeQuery(id+"F9.opExtrude","SWEPT_FACE",FACE,{"disambiguationData":[OSD([sQuery(id+"F8.wireOp",EDGE,"E25")])]})])],"derivedFrom":subQ9}),"instanceName":"1"}),"instanceName":"1"}),makeQuery(id+"F19.opPattern","COPY",FACE,{"derivedFrom":makeQuery(id+"F16.opPattern","COPY",FACE,{"derivedFrom":makeQuery(id+"F9.boolean.opBoolean","SPLIT",FACE,{"disambiguationData":[TD([makeQuery(id+"F9.opExtrude","SWEPT_FACE",FACE,{"disambiguationData":[OSD([sQuery(id+"F8.wireOp",EDGE,"E32")])]})])],"derivedFrom":subQ9}),"instanceName":"1"}),"instanceName":"1"}),makeQuery(id+"F19.opPattern","COPY",FACE,{"derivedFrom":makeQuery(id+"F16.opPattern","COPY",FACE,{"derivedFrom":makeQuery(id+"F9.boolean.opBoolean","SPLIT",FACE,{"disambiguationData":[TD([makeQuery(id+"F9.opExtrude","SWEPT_FACE",FACE,{"disambiguationData":[OSD([sQuery(id+"F8.wireOp",EDGE,"E33.0")])]})])],"derivedFrom":subQ9}),"instanceName":"1"}),"instanceName":"1"}),makeQuery(id+"F19.opPattern","COPY",FACE,{"derivedFrom":makeQuery(id+"F16.opPattern","COPY",FACE,{"derivedFrom":makeQuery(id+"F9.boolean.opBoolean","SPLIT",FACE,{"disambiguationData":[TD([makeQuery(id+"F9.opExtrude","SWEPT_FACE",FACE,{"disambiguationData":[OSD([sQuery(id+"F8.wireOp",EDGE,"E37")])]})])],"derivedFrom":subQ9}),"instanceName":"1"}),"instanceName":"1"}),makeQuery(id+"F19.opPattern","COPY",FACE,{"derivedFrom":makeQuery(id+"F16.opPattern","COPY",FACE,{"derivedFrom":makeQuery(id+"F9.boolean.opBoolean","SPLIT",FACE,{"disambiguationData":[TD([makeQuery(id+"F9.opExtrude","SWEPT_FACE",FACE,{"disambiguationData":[OSD([sQuery(id+"F8.wireOp",EDGE,"E51.MirrorCS")])]})])],"derivedFrom":subQ9}),"instanceName":"1"}),"instanceName":"1"}),makeQuery(id+"F19.opPattern","COPY",FACE,{"derivedFrom":makeQuery(id+"F16.opPattern","COPY",FACE,{"derivedFrom":makeQuery(id+"F9.boolean.opBoolean","SPLIT",FACE,{"disambiguationData":[TD([makeQuery(id+"F9.opExtrude","SWEPT_FACE",FACE,{"disambiguationData":[OSD([sQuery(id+"F8.wireOp",EDGE,"E53.MirrorCS")])]})])],"derivedFrom":subQ9}),"instanceName":"1"}),"instanceName":"1"}),makeQuery(id+"F19.opPattern","COPY",FACE,{"derivedFrom":makeQuery(id+"F16.opPattern","COPY",FACE,{"derivedFrom":makeQuery(id+"F9.boolean.opBoolean","SPLIT",FACE,{"disambiguationData":[TD([makeQuery(id+"F9.opExtrude","SWEPT_FACE",FACE,{"disambiguationData":[OSD([sQuery(id+"F8.wireOp",EDGE,"E80")])]})])],"derivedFrom":subQ9}),"instanceName":"1"}),"instanceName":"1"}),makeQuery(id+"F19.opPattern","COPY",FACE,{"derivedFrom":makeQuery(id+"F16.opPattern","COPY",FACE,{"derivedFrom":makeQuery(id+"F9.boolean.opBoolean","SPLIT",FACE,{"disambiguationData":[TD([makeQuery(id+"F9.opExtrude","SWEPT_FACE",FACE,{"disambiguationData":[OSD([sQuery(id+"F8.wireOp",EDGE,"E83")])]})])],"derivedFrom":subQ9}),"instanceName":"1"}),"instanceName":"1"})],"fromTools":[makeQuery(id+"F21.opExtrude","CAP_FACE",FACE,{"disambiguationData":[OSD([sQuery(id+"F20.wireOp",EDGE,"E307.0.0")])],"isStart":false})]}),"instanceName":"1"}),"instanceName":"1"});Q0=makeQuery(id+"F90.boolean.opBoolean","SPLIT",FACE,{"disambiguationData":[TD([subQ2])],"derivedFrom":makeQuery(id+"F87.boolean.opBoolean","MERGE",FACE,{"derivedFrom":[makeQuery(id+"F63.boolean.opBoolean","SPLIT",FACE,{"disambiguationData":[TD([makeQuery(id+"F63.opExtrude","SWEPT_FACE",FACE,{"disambiguationData":[OSD([sQuery(id+"F62.wireOp",EDGE,"E828")])]})])],"derivedFrom":subQ10}),makeQuery(id+"F63.boolean.opBoolean","SPLIT",FACE,{"disambiguationData":[TD([makeQuery(id+"F63.opExtrude","SWEPT_FACE",FACE,{"disambiguationData":[OSD([sQuery(id+"F62.wireOp",EDGE,"E834")])]})])],"derivedFrom":subQ10}),makeQuery(id+"F63.boolean.opBoolean","SPLIT",FACE,{"disambiguationData":[TD([makeQuery(id+"F63.opExtrude","SWEPT_FACE",FACE,{"disambiguationData":[OSD([sQuery(id+"F62.wireOp",EDGE,"E838.MirrorCS")])]})])],"derivedFrom":subQ10}),makeQuery(id+"F63.boolean.opBoolean","SPLIT",FACE,{"disambiguationData":[TD([makeQuery(id+"F63.opExtrude","SWEPT_FACE",FACE,{"disambiguationData":[OSD([sQuery(id+"F62.wireOp",EDGE,"E842")])]})])],"derivedFrom":subQ10}),makeQuery(id+"F67.boolean.opBoolean","MERGE",FACE,{"derivedFrom":[makeQuery(id+"F63.boolean.opBoolean","SPLIT",FACE,{"disambiguationData":[TD([subQ2])],"derivedFrom":subQ10})],"fromTools":[makeQuery(id+"F67.opExtrude","CAP_FACE",FACE,{"disambiguationData":[OSD([sQuery(id+"F66.wireOp",EDGE,"E887"),sQuery(id+"F66.wireOp",EDGE,"E888"),sQuery(id+"F66.wireOp",EDGE,"E889.0"),sQuery(id+"F66.wireOp",EDGE,"E890.0"),sQuery(id+"F66.wireOp",EDGE,"E892.MirrorCS"),sQuery(id+"F66.wireOp",EDGE,"E893.MirrorCS"),sQuery(id+"F66.wireOp",EDGE,"E894.trimOffspring"),sQuery(id+"F66.wireOp",EDGE,"E895"),sQuery(id+"F66.wireOp",EDGE,"E896"),sQuery(id+"F66.wireOp",EDGE,"E897.MirrorCS"),sQuery(id+"F66.wireOp",EDGE,"E898.MirrorCS")])],"isStart":false})]})],"fromTools":[makeQuery(id+"F87.opExtrude","CAP_FACE",FACE,{"disambiguationData":[OSD([sQuery(id+"F86.wireOp",EDGE,"E1227.0.0")])],"isStart":false})]})});}
            var sketch = newSketch(context, id + "F91", { "sketchPlane" : qUnion([Q0])});
            skPoint(sketch, "E1336.0", {"position": v(-101.68, -48.79) * mm});
            skLineSegment(sketch, "E1337", {"start": v(-101.68, -48.79) * mm, "end": v(-101.68, -56.83) * mm});
            skLineSegment(sketch, "E1338", {"start": v(-102.24, -57.1) * mm, "end": v(-102.4, -56.95) * mm});
            skLineSegment(sketch, "E1339", {"start": v(-101.2, -57.01) * mm, "end": v(-100.23, -55.9) * mm});
            skArc(sketch, "E1340", {"start": v(-101.28, -56.96) * mm, "mid": v(-101.15, -54.79) * mm, "end": v(-102.6, -53.17) * mm});
            skArc(sketch, "E1341", {"start": v(-102.77, -54.6) * mm, "mid": v(-102.31, -53.93) * mm, "end": v(-102.6, -53.17) * mm});
            skArc(sketch, "E1342.MirrorCS", {"start": v(-104.78, -56.93) * mm, "mid": v(-105.38, -57.48) * mm, "end": v(-106.17, -57.3) * mm});
            skArc(sketch, "E1343.MirrorCS", {"start": v(-102.23, -58.06) * mm, "mid": v(-104.35, -58.5) * mm, "end": v(-106.17, -57.3) * mm});
            skArc(sketch, "E1344", {"start": v(-110.45, -50.01) * mm, "mid": v(-106.74, -52.53) * mm, "end": v(-102.77, -54.6) * mm});
            skArc(sketch, "E1345.MirrorCS", {"start": v(-110.45, -50.01) * mm, "mid": v(-107.41, -53.3) * mm, "end": v(-104.78, -56.93) * mm});
            skArc(sketch, "E1346", {"start": v(-104.57, -55.76) * mm, "mid": v(-102.4, -56.95) * mm, "end": v(-103.9, -54.98) * mm});
            skArc(sketch, "E1347", {"start": v(-106.87, -53.1) * mm, "mid": v(-105.92, -54.6) * mm, "end": v(-104.57, -55.76) * mm});
            skArc(sketch, "E1348.MirrorCS", {"start": v(-106.87, -53.1) * mm, "mid": v(-105.25, -53.82) * mm, "end": v(-103.9, -54.98) * mm});
            skLineSegment(sketch, "E1349.trimOffspring", {"start": v(-106.87, -53.1) * mm, "end": v(-110.45, -50.01) * mm});
            skArc(sketch, "E1350", {"start": v(-101.19, -58.12) * mm, "mid": v(-101.12, -58.05) * mm, "end": v(-101.07, -57.98) * mm});
            skArc(sketch, "E1351", {"start": v(-99.66, -59.19) * mm, "mid": v(-99.73, -59.26) * mm, "end": v(-99.78, -59.33) * mm});
            skArc(sketch, "E1352", {"start": v(-101.47, -58.28) * mm, "mid": v(-100.88, -59.2) * mm, "end": v(-99.88, -59.64) * mm});
            skArc(sketch, "E1353.MirrorCS", {"start": v(-100.95, -57.67) * mm, "mid": v(-99.95, -58.12) * mm, "end": v(-99.37, -59.04) * mm});
            skArc(sketch, "E1354", {"start": v(-101.19, -58.12) * mm, "mid": v(-100.63, -58.89) * mm, "end": v(-99.78, -59.33) * mm});
            skArc(sketch, "E1355.MirrorCS", {"start": v(-101.07, -57.98) * mm, "mid": v(-100.22, -58.42) * mm, "end": v(-99.66, -59.19) * mm});
            skArc(sketch, "E1356.trimOffspring", {"start": v(-99.88, -59.64) * mm, "mid": v(-98.75, -60.1) * mm, "end": v(-99.37, -59.04) * mm});
            skArc(sketch, "E1357.trimOffspring", {"start": v(-100.95, -57.67) * mm, "mid": v(-101.01, -57.27) * mm, "end": v(-101.28, -56.96) * mm});
            skArc(sketch, "E1358.trimOffspring", {"start": v(-101.19, -58.12) * mm, "mid": v(-100.95, -57.51) * mm, "end": v(-101.28, -56.96) * mm});
            skCircle(sketch, "E1359", {"center": v(-101.68, -57.57) * mm, "radius": 0.74 * mm});
            skSolve(sketch);
        }
        {
            var Q0;
            Q0 = qSketchRegion(id + "F91", true);
            var Q1;
            Q1=makeQuery(id+"F90.opExtrude","CAP_FACE",FACE,{"disambiguationData":[OSD([sQuery(id+"F89.wireOp",EDGE,"E1269"),sQuery(id+"F89.wireOp",EDGE,"E1271"),sQuery(id+"F89.wireOp",EDGE,"E1272"),sQuery(id+"F89.wireOp",EDGE,"E1273.MirrorCS"),sQuery(id+"F89.wireOp",EDGE,"E1274.MirrorCS"),sQuery(id+"F89.wireOp",EDGE,"E1275"),sQuery(id+"F89.wireOp",EDGE,"E1276"),sQuery(id+"F89.wireOp",EDGE,"E1277"),sQuery(id+"F89.wireOp",EDGE,"E1278"),sQuery(id+"F89.wireOp",EDGE,"E1279"),sQuery(id+"F89.wireOp",EDGE,"E1280"),sQuery(id+"F89.wireOp",EDGE,"E1281.MirrorCS"),sQuery(id+"F89.wireOp",EDGE,"E1282.MirrorCS"),sQuery(id+"F89.wireOp",EDGE,"E1283.MirrorCS"),sQuery(id+"F89.wireOp",EDGE,"E1284.MirrorCS"),sQuery(id+"F89.wireOp",EDGE,"E1285.MirrorCS"),sQuery(id+"F89.wireOp",EDGE,"E1286.MirrorCS"),sQuery(id+"F89.wireOp",EDGE,"E1287"),sQuery(id+"F89.wireOp",EDGE,"E1290"),sQuery(id+"F89.wireOp",EDGE,"E1292.MirrorCS"),sQuery(id+"F89.wireOp",EDGE,"E1293.MirrorCS"),sQuery(id+"F89.wireOp",EDGE,"E1289"),sQuery(id+"F89.wireOp",EDGE,"E1294"),sQuery(id+"F89.wireOp",EDGE,"E1295"),sQuery(id+"F89.wireOp",EDGE,"E1296"),sQuery(id+"F89.wireOp",EDGE,"E1297.0"),sQuery(id+"F89.wireOp",EDGE,"E1298.trimOffspring"),sQuery(id+"F89.wireOp",EDGE,"E1300"),sQuery(id+"F89.wireOp",EDGE,"E1301"),sQuery(id+"F89.wireOp",EDGE,"E1302"),sQuery(id+"F89.wireOp",EDGE,"E1304"),sQuery(id+"F89.wireOp",EDGE,"E1305.MirrorCS"),sQuery(id+"F89.wireOp",EDGE,"E1306.MirrorCS"),sQuery(id+"F89.wireOp",EDGE,"E1307.MirrorCS"),sQuery(id+"F89.wireOp",EDGE,"E1308.MirrorCS"),sQuery(id+"F89.wireOp",EDGE,"E1294"),sQuery(id+"F89.wireOp",EDGE,"E1311.MirrorCS"),sQuery(id+"F89.wireOp",EDGE,"E1291.MirrorCS"),sQuery(id+"F89.wireOp",EDGE,"E1312.MirrorCS"),sQuery(id+"F89.wireOp",EDGE,"E1313.MirrorCS"),sQuery(id+"F89.wireOp",EDGE,"E1314.MirrorCS"),sQuery(id+"F89.wireOp",EDGE,"E1315"),sQuery(id+"F89.wireOp",EDGE,"E1320.trimOffspring"),sQuery(id+"F89.wireOp",EDGE,"E1323.trimOffspring"),sQuery(id+"F89.wireOp",EDGE,"E1324"),sQuery(id+"F89.wireOp",EDGE,"E1325"),sQuery(id+"F89.wireOp",EDGE,"E1326.MirrorCS"),sQuery(id+"F89.wireOp",EDGE,"E1327.MirrorCS"),sQuery(id+"F89.wireOp",EDGE,"E1330.trimOffspring"),sQuery(id+"F89.wireOp",EDGE,"E1333.trimOffspring")])],"isStart":false});
            extrude(context, id + "F92", {"entities" : qUnion([Q0]), "operationType" : NewBodyOperationType.ADD, "endBound" : BoundingType.UP_TO_SURFACE, "depth" : 25.4 * mm, "endBoundEntityFace" : qUnion([Q1]), "offsetDistance" : 25.4 * mm});
        }
        {
            var Q0;
            {var subQ17=sQuery(id+"F4.wireOp",EDGE,"E8");var subQ18=makeQuery(id+"F5.boolean.opBoolean","COPY",FACE,{"derivedFrom":makeQuery(id+"F5.opExtrude","SWEPT_FACE",FACE,{"disambiguationData":[OSD([subQ17])]})});var subQ19=makeQuery(id+"F40.opPattern","COPY",FACE,{"derivedFrom":makeQuery(id+"F39.opPattern","COPY",FACE,{"derivedFrom":makeQuery(id+"F19.opPattern","COPY",FACE,{"derivedFrom":makeQuery(id+"F16.opPattern","COPY",FACE,{"derivedFrom":subQ18,"instanceName":"1"}),"instanceName":"1"}),"instanceName":"1"}),"instanceName":"1"});var subQ36=makeQuery(id+"F5.boolean.opBoolean","COPY",FACE,{"derivedFrom":makeQuery(id+"F5.opExtrude","CAP_FACE",FACE,{"disambiguationData":[OSD([subQ17])],"isStart":false})});var subQ37=makeQuery(id+"F40.opPattern","COPY",FACE,{"derivedFrom":makeQuery(id+"F39.opPattern","COPY",FACE,{"derivedFrom":makeQuery(id+"F21.boolean.opBoolean","MERGE",FACE,{"derivedFrom":[makeQuery(id+"F19.opPattern","COPY",FACE,{"derivedFrom":makeQuery(id+"F16.opPattern","COPY",FACE,{"derivedFrom":makeQuery(id+"F9.boolean.opBoolean","SPLIT",FACE,{"disambiguationData":[TD([subQ18])],"derivedFrom":subQ36}),"instanceName":"1"}),"instanceName":"1"}),makeQuery(id+"F19.opPattern","COPY",FACE,{"derivedFrom":makeQuery(id+"F16.opPattern","COPY",FACE,{"derivedFrom":makeQuery(id+"F9.boolean.opBoolean","SPLIT",FACE,{"disambiguationData":[TD([makeQuery(id+"F9.opExtrude","SWEPT_FACE",FACE,{"disambiguationData":[OSD([sQuery(id+"F8.wireOp",EDGE,"E25")])]})])],"derivedFrom":subQ36}),"instanceName":"1"}),"instanceName":"1"}),makeQuery(id+"F19.opPattern","COPY",FACE,{"derivedFrom":makeQuery(id+"F16.opPattern","COPY",FACE,{"derivedFrom":makeQuery(id+"F9.boolean.opBoolean","SPLIT",FACE,{"disambiguationData":[TD([makeQuery(id+"F9.opExtrude","SWEPT_FACE",FACE,{"disambiguationData":[OSD([sQuery(id+"F8.wireOp",EDGE,"E32")])]})])],"derivedFrom":subQ36}),"instanceName":"1"}),"instanceName":"1"}),makeQuery(id+"F19.opPattern","COPY",FACE,{"derivedFrom":makeQuery(id+"F16.opPattern","COPY",FACE,{"derivedFrom":makeQuery(id+"F9.boolean.opBoolean","SPLIT",FACE,{"disambiguationData":[TD([makeQuery(id+"F9.opExtrude","SWEPT_FACE",FACE,{"disambiguationData":[OSD([sQuery(id+"F8.wireOp",EDGE,"E33.0")])]})])],"derivedFrom":subQ36}),"instanceName":"1"}),"instanceName":"1"}),makeQuery(id+"F19.opPattern","COPY",FACE,{"derivedFrom":makeQuery(id+"F16.opPattern","COPY",FACE,{"derivedFrom":makeQuery(id+"F9.boolean.opBoolean","SPLIT",FACE,{"disambiguationData":[TD([makeQuery(id+"F9.opExtrude","SWEPT_FACE",FACE,{"disambiguationData":[OSD([sQuery(id+"F8.wireOp",EDGE,"E37")])]})])],"derivedFrom":subQ36}),"instanceName":"1"}),"instanceName":"1"}),makeQuery(id+"F19.opPattern","COPY",FACE,{"derivedFrom":makeQuery(id+"F16.opPattern","COPY",FACE,{"derivedFrom":makeQuery(id+"F9.boolean.opBoolean","SPLIT",FACE,{"disambiguationData":[TD([makeQuery(id+"F9.opExtrude","SWEPT_FACE",FACE,{"disambiguationData":[OSD([sQuery(id+"F8.wireOp",EDGE,"E51.MirrorCS")])]})])],"derivedFrom":subQ36}),"instanceName":"1"}),"instanceName":"1"}),makeQuery(id+"F19.opPattern","COPY",FACE,{"derivedFrom":makeQuery(id+"F16.opPattern","COPY",FACE,{"derivedFrom":makeQuery(id+"F9.boolean.opBoolean","SPLIT",FACE,{"disambiguationData":[TD([makeQuery(id+"F9.opExtrude","SWEPT_FACE",FACE,{"disambiguationData":[OSD([sQuery(id+"F8.wireOp",EDGE,"E53.MirrorCS")])]})])],"derivedFrom":subQ36}),"instanceName":"1"}),"instanceName":"1"}),makeQuery(id+"F19.opPattern","COPY",FACE,{"derivedFrom":makeQuery(id+"F16.opPattern","COPY",FACE,{"derivedFrom":makeQuery(id+"F9.boolean.opBoolean","SPLIT",FACE,{"disambiguationData":[TD([makeQuery(id+"F9.opExtrude","SWEPT_FACE",FACE,{"disambiguationData":[OSD([sQuery(id+"F8.wireOp",EDGE,"E80")])]})])],"derivedFrom":subQ36}),"instanceName":"1"}),"instanceName":"1"}),makeQuery(id+"F19.opPattern","COPY",FACE,{"derivedFrom":makeQuery(id+"F16.opPattern","COPY",FACE,{"derivedFrom":makeQuery(id+"F9.boolean.opBoolean","SPLIT",FACE,{"disambiguationData":[TD([makeQuery(id+"F9.opExtrude","SWEPT_FACE",FACE,{"disambiguationData":[OSD([sQuery(id+"F8.wireOp",EDGE,"E83")])]})])],"derivedFrom":subQ36}),"instanceName":"1"}),"instanceName":"1"})],"fromTools":[makeQuery(id+"F21.opExtrude","CAP_FACE",FACE,{"disambiguationData":[OSD([sQuery(id+"F20.wireOp",EDGE,"E307.0.0")])],"isStart":false})]}),"instanceName":"1"}),"instanceName":"1"});Q0=makeQuery(id+"F92.boolean.opBoolean","SPLIT",FACE,{"disambiguationData":[TD([subQ19])],"derivedFrom":makeQuery(id+"F90.boolean.opBoolean","SPLIT",FACE,{"disambiguationData":[TD([subQ19])],"derivedFrom":makeQuery(id+"F87.boolean.opBoolean","MERGE",FACE,{"derivedFrom":[makeQuery(id+"F63.boolean.opBoolean","SPLIT",FACE,{"disambiguationData":[TD([makeQuery(id+"F63.opExtrude","SWEPT_FACE",FACE,{"disambiguationData":[OSD([sQuery(id+"F62.wireOp",EDGE,"E828")])]})])],"derivedFrom":subQ37}),makeQuery(id+"F63.boolean.opBoolean","SPLIT",FACE,{"disambiguationData":[TD([makeQuery(id+"F63.opExtrude","SWEPT_FACE",FACE,{"disambiguationData":[OSD([sQuery(id+"F62.wireOp",EDGE,"E834")])]})])],"derivedFrom":subQ37}),makeQuery(id+"F63.boolean.opBoolean","SPLIT",FACE,{"disambiguationData":[TD([makeQuery(id+"F63.opExtrude","SWEPT_FACE",FACE,{"disambiguationData":[OSD([sQuery(id+"F62.wireOp",EDGE,"E838.MirrorCS")])]})])],"derivedFrom":subQ37}),makeQuery(id+"F63.boolean.opBoolean","SPLIT",FACE,{"disambiguationData":[TD([makeQuery(id+"F63.opExtrude","SWEPT_FACE",FACE,{"disambiguationData":[OSD([sQuery(id+"F62.wireOp",EDGE,"E842")])]})])],"derivedFrom":subQ37}),makeQuery(id+"F67.boolean.opBoolean","MERGE",FACE,{"derivedFrom":[makeQuery(id+"F63.boolean.opBoolean","SPLIT",FACE,{"disambiguationData":[TD([subQ19])],"derivedFrom":subQ37})],"fromTools":[makeQuery(id+"F67.opExtrude","CAP_FACE",FACE,{"disambiguationData":[OSD([sQuery(id+"F66.wireOp",EDGE,"E887"),sQuery(id+"F66.wireOp",EDGE,"E888"),sQuery(id+"F66.wireOp",EDGE,"E889.0"),sQuery(id+"F66.wireOp",EDGE,"E890.0"),sQuery(id+"F66.wireOp",EDGE,"E892.MirrorCS"),sQuery(id+"F66.wireOp",EDGE,"E893.MirrorCS"),sQuery(id+"F66.wireOp",EDGE,"E894.trimOffspring"),sQuery(id+"F66.wireOp",EDGE,"E895"),sQuery(id+"F66.wireOp",EDGE,"E896"),sQuery(id+"F66.wireOp",EDGE,"E897.MirrorCS"),sQuery(id+"F66.wireOp",EDGE,"E898.MirrorCS")])],"isStart":false})]})],"fromTools":[makeQuery(id+"F87.opExtrude","CAP_FACE",FACE,{"disambiguationData":[OSD([sQuery(id+"F86.wireOp",EDGE,"E1227.0.0")])],"isStart":false})]})})});}
            var sketch = newSketch(context, id + "F93", { "sketchPlane" : qUnion([Q0])});
            skLineSegment(sketch, "E1360", {"start": v(-101.68, -46.48) * mm, "end": v(-101.68, -51.96) * mm});
            skPoint(sketch, "E1360.endSnap0", {"position": v(-102.13, -51.96) * mm});
            skArc(sketch, "E1361.0.0", {"start": v(-100.95, -57.67) * mm, "mid": v(-99.95, -58.12) * mm, "end": v(-99.37, -59.04) * mm});
            skArc(sketch, "E1361.0.1", {"start": v(-100.95, -57.67) * mm, "mid": v(-101.01, -57.27) * mm, "end": v(-101.28, -56.96) * mm});
            skArc(sketch, "E1361.0.2", {"start": v(-101.28, -56.96) * mm, "mid": v(-101.15, -54.79) * mm, "end": v(-102.6, -53.17) * mm});
            skArc(sketch, "E1361.0.3", {"start": v(-102.6, -53.17) * mm, "mid": v(-102.31, -53.93) * mm, "end": v(-102.77, -54.6) * mm});
            skArc(sketch, "E1361.0.4", {"start": v(-102.77, -54.6) * mm, "mid": v(-106.74, -52.53) * mm, "end": v(-110.45, -50.01) * mm});
            skArc(sketch, "E1361.0.5", {"start": v(-110.45, -50.01) * mm, "mid": v(-107.41, -53.3) * mm, "end": v(-104.78, -56.93) * mm});
            skArc(sketch, "E1361.0.6", {"start": v(-104.78, -56.93) * mm, "mid": v(-105.38, -57.48) * mm, "end": v(-106.17, -57.3) * mm});
            skArc(sketch, "E1361.0.7", {"start": v(-102.23, -58.06) * mm, "mid": v(-104.35, -58.5) * mm, "end": v(-106.17, -57.3) * mm});
            skArc(sketch, "E1361.0.8", {"start": v(-102.23, -58.06) * mm, "mid": v(-101.88, -58.28) * mm, "end": v(-101.47, -58.28) * mm});
            skArc(sketch, "E1361.0.9", {"start": v(-101.47, -58.28) * mm, "mid": v(-100.88, -59.2) * mm, "end": v(-99.88, -59.64) * mm});
            skArc(sketch, "E1361.0.10", {"start": v(-99.88, -59.64) * mm, "mid": v(-98.75, -60.1) * mm, "end": v(-99.37, -59.04) * mm});
            skArc(sketch, "E1362.MirrorCS", {"start": v(-101.13, -58.06) * mm, "mid": v(-101.48, -58.28) * mm, "end": v(-101.89, -58.28) * mm});
            skArc(sketch, "E1363.MirrorCS", {"start": v(-102.4, -57.67) * mm, "mid": v(-102.35, -57.27) * mm, "end": v(-102.08, -56.96) * mm});
            skArc(sketch, "E1364.MirrorCS", {"start": v(-103.48, -59.64) * mm, "mid": v(-104.61, -60.1) * mm, "end": v(-104, -59.04) * mm});
            skArc(sketch, "E1365.MirrorCS", {"start": v(-101.13, -58.06) * mm, "mid": v(-99, -58.5) * mm, "end": v(-97.2, -57.3) * mm});
            skArc(sketch, "E1366.MirrorCS", {"start": v(-101.89, -58.28) * mm, "mid": v(-102.48, -59.2) * mm, "end": v(-103.48, -59.64) * mm});
            skArc(sketch, "E1367.MirrorCS", {"start": v(-102.4, -57.67) * mm, "mid": v(-103.4, -58.12) * mm, "end": v(-104, -59.04) * mm});
            skArc(sketch, "E1368.MirrorCS", {"start": v(-92.91, -50.01) * mm, "mid": v(-95.95, -53.3) * mm, "end": v(-98.58, -56.93) * mm});
            skArc(sketch, "E1369.MirrorCS", {"start": v(-102.08, -56.96) * mm, "mid": v(-102.2, -54.79) * mm, "end": v(-100.76, -53.17) * mm});
            skArc(sketch, "E1370.MirrorCS", {"start": v(-100.76, -53.17) * mm, "mid": v(-101.05, -53.93) * mm, "end": v(-100.6, -54.6) * mm});
            skArc(sketch, "E1371.MirrorCS", {"start": v(-98.58, -56.93) * mm, "mid": v(-97.99, -57.48) * mm, "end": v(-97.2, -57.3) * mm});
            skPoint(sketch, "E1372.MirrorP", {"position": v(-101.23, -51.96) * mm});
            skArc(sketch, "E1373.MirrorCS", {"start": v(-100.6, -54.6) * mm, "mid": v(-96.62, -52.53) * mm, "end": v(-92.91, -50.01) * mm});
            skArc(sketch, "E1374.0.0", {"start": v(-104.57, -55.76) * mm, "mid": v(-102.4, -56.95) * mm, "end": v(-103.9, -54.98) * mm});
            skArc(sketch, "E1374.0.1", {"start": v(-103.9, -54.98) * mm, "mid": v(-105.25, -53.82) * mm, "end": v(-106.87, -53.1) * mm});
            skArc(sketch, "E1374.0.2", {"start": v(-106.87, -53.1) * mm, "mid": v(-105.92, -54.6) * mm, "end": v(-104.57, -55.76) * mm});
            skArc(sketch, "E1375.0.0", {"start": v(-99.66, -59.19) * mm, "mid": v(-100.22, -58.42) * mm, "end": v(-101.07, -57.98) * mm});
            skArc(sketch, "E1375.0.1", {"start": v(-101.07, -57.98) * mm, "mid": v(-101.12, -58.05) * mm, "end": v(-101.19, -58.12) * mm});
            skArc(sketch, "E1375.0.2", {"start": v(-101.19, -58.12) * mm, "mid": v(-100.63, -58.89) * mm, "end": v(-99.78, -59.33) * mm});
            skArc(sketch, "E1375.0.3", {"start": v(-99.78, -59.33) * mm, "mid": v(-99.73, -59.26) * mm, "end": v(-99.66, -59.19) * mm});
            skArc(sketch, "E1376.MirrorCS", {"start": v(-102.3, -57.98) * mm, "mid": v(-102.24, -58.05) * mm, "end": v(-102.17, -58.12) * mm});
            skArc(sketch, "E1377.MirrorCS", {"start": v(-103.58, -59.33) * mm, "mid": v(-103.63, -59.26) * mm, "end": v(-103.7, -59.19) * mm});
            skArc(sketch, "E1378.MirrorCS", {"start": v(-103.7, -59.19) * mm, "mid": v(-103.14, -58.42) * mm, "end": v(-102.3, -57.98) * mm});
            skArc(sketch, "E1379.MirrorCS", {"start": v(-99.46, -54.98) * mm, "mid": v(-98.11, -53.82) * mm, "end": v(-96.49, -53.1) * mm});
            skArc(sketch, "E1380.MirrorCS", {"start": v(-98.8, -55.76) * mm, "mid": v(-100.96, -56.95) * mm, "end": v(-99.46, -54.98) * mm});
            skArc(sketch, "E1381.MirrorCS", {"start": v(-96.49, -53.1) * mm, "mid": v(-97.44, -54.6) * mm, "end": v(-98.8, -55.76) * mm});
            skArc(sketch, "E1382.MirrorCS", {"start": v(-102.17, -58.12) * mm, "mid": v(-102.73, -58.89) * mm, "end": v(-103.58, -59.33) * mm});
            skSolve(sketch);
        }
        {
            var Q0;
            Q0 = qSketchRegion(id + "F93", true);
            var Q1;
            Q1=makeQuery(id+"F34.opExtrude","CAP_FACE",FACE,{"disambiguationData":[OSD([sQuery(id+"F33.wireOp",EDGE,"E523"),sQuery(id+"F33.wireOp",EDGE,"E524"),sQuery(id+"F33.wireOp",EDGE,"E525"),sQuery(id+"F33.wireOp",EDGE,"E526"),sQuery(id+"F33.wireOp",EDGE,"E527"),sQuery(id+"F33.wireOp",EDGE,"E528.trimOffspring"),sQuery(id+"F33.wireOp",EDGE,"E529.MirrorCS"),sQuery(id+"F33.wireOp",EDGE,"E530.MirrorCS"),sQuery(id+"F33.wireOp",EDGE,"E534.MirrorCS"),sQuery(id+"F33.wireOp",EDGE,"E535.MirrorCS"),sQuery(id+"F33.wireOp",EDGE,"E536.MirrorCS"),sQuery(id+"F33.wireOp",EDGE,"E537.MirrorCS"),sQuery(id+"F33.wireOp",EDGE,"E538.MirrorCS"),sQuery(id+"F33.wireOp",EDGE,"E539.MirrorCS"),sQuery(id+"F33.wireOp",EDGE,"E540.MirrorCS"),sQuery(id+"F33.wireOp",EDGE,"E541.MirrorCS"),sQuery(id+"F33.wireOp",EDGE,"E542.MirrorCS"),sQuery(id+"F33.wireOp",EDGE,"E543.MirrorCS"),sQuery(id+"F33.wireOp",EDGE,"E544.MirrorCS"),sQuery(id+"F33.wireOp",EDGE,"E545.MirrorCS"),sQuery(id+"F33.wireOp",EDGE,"E546.MirrorCS"),sQuery(id+"F33.wireOp",EDGE,"E547.MirrorCS"),sQuery(id+"F33.wireOp",EDGE,"E548.MirrorCS"),sQuery(id+"F33.wireOp",EDGE,"E549.MirrorCS"),sQuery(id+"F33.wireOp",EDGE,"E551.trimOffspring"),sQuery(id+"F33.wireOp",EDGE,"E552.trimOffspring"),sQuery(id+"F33.wireOp",EDGE,"E553.trimOffspring"),sQuery(id+"F33.wireOp",EDGE,"E554.trimOffspring"),sQuery(id+"F33.wireOp",EDGE,"E555.trimOffspring"),sQuery(id+"F33.wireOp",EDGE,"E556.trimOffspring"),sQuery(id+"F33.wireOp",EDGE,"E557.trimOffspring"),sQuery(id+"F33.wireOp",EDGE,"E558.trimOffspring"),sQuery(id+"F33.wireOp",EDGE,"E559.trimOffspring"),sQuery(id+"F33.wireOp",EDGE,"E560.trimOffspring"),sQuery(id+"F33.wireOp",EDGE,"E561.trimOffspring"),sQuery(id+"F33.wireOp",EDGE,"E562.trimOffspring"),sQuery(id+"F33.wireOp",EDGE,"E563.trimOffspring"),sQuery(id+"F33.wireOp",EDGE,"E564.trimOffspring"),sQuery(id+"F33.wireOp",EDGE,"E565.trimOffspring"),sQuery(id+"F33.wireOp",EDGE,"E566.trimOffspring"),sQuery(id+"F33.wireOp",EDGE,"E567.trimOffspring"),sQuery(id+"F33.wireOp",EDGE,"E568.trimOffspring"),sQuery(id+"F33.wireOp",EDGE,"E569.trimOffspring"),sQuery(id+"F33.wireOp",EDGE,"E570.trimOffspring"),sQuery(id+"F33.wireOp",EDGE,"E571.trimOffspring"),sQuery(id+"F33.wireOp",EDGE,"E572.trimOffspring"),sQuery(id+"F33.wireOp",EDGE,"E573.trimOffspring"),sQuery(id+"F33.wireOp",EDGE,"E574.trimOffspring"),sQuery(id+"F33.wireOp",EDGE,"E575.trimOffspring"),sQuery(id+"F33.wireOp",EDGE,"E576.trimOffspring"),sQuery(id+"F33.wireOp",EDGE,"E577.trimOffspring"),sQuery(id+"F33.wireOp",EDGE,"E578.trimOffspring"),sQuery(id+"F33.wireOp",EDGE,"E579.trimOffspring"),sQuery(id+"F33.wireOp",EDGE,"E580.trimOffspring"),sQuery(id+"F33.wireOp",EDGE,"E581.trimOffspring"),sQuery(id+"F33.wireOp",EDGE,"E582.trimOffspring"),sQuery(id+"F33.wireOp",EDGE,"E583.trimOffspring"),sQuery(id+"F33.wireOp",EDGE,"E584.trimOffspring"),sQuery(id+"F33.wireOp",EDGE,"E585.trimOffspring"),sQuery(id+"F33.wireOp",EDGE,"E586.trimOffspring"),sQuery(id+"F33.wireOp",EDGE,"E587.trimOffspring"),sQuery(id+"F33.wireOp",EDGE,"E588.trimOffspring"),sQuery(id+"F33.wireOp",EDGE,"E589.trimOffspring"),sQuery(id+"F33.wireOp",EDGE,"E590.trimOffspring"),sQuery(id+"F33.wireOp",EDGE,"E591.trimOffspring"),sQuery(id+"F33.wireOp",EDGE,"E592.trimOffspring"),sQuery(id+"F33.wireOp",EDGE,"E593.trimOffspring"),sQuery(id+"F33.wireOp",EDGE,"E594.trimOffspring"),sQuery(id+"F33.wireOp",EDGE,"E595.trimOffspring"),sQuery(id+"F33.wireOp",EDGE,"E596.trimOffspring"),sQuery(id+"F33.wireOp",EDGE,"E597.trimOffspring"),sQuery(id+"F33.wireOp",EDGE,"E598.trimOffspring")])],"isStart":false});
            extrude(context, id + "F94", {"entities" : qUnion([Q0]), "operationType" : NewBodyOperationType.ADD, "endBound" : BoundingType.UP_TO_SURFACE, "depth" : 25.4 * mm, "endBoundEntityFace" : qUnion([Q1]), "offsetDistance" : 25.4 * mm});
        }
        {
            var Q0;
            {var subQ0=sQuery(id+"F4.wireOp",EDGE,"E8");var subQ1=makeQuery(id+"F5.boolean.opBoolean","COPY",FACE,{"derivedFrom":makeQuery(id+"F5.opExtrude","CAP_FACE",FACE,{"disambiguationData":[OSD([subQ0])],"isStart":false})});Q0=makeQuery(id+"F21.boolean.opBoolean","MERGE",FACE,{"derivedFrom":[makeQuery(id+"F19.opPattern","COPY",FACE,{"derivedFrom":makeQuery(id+"F16.opPattern","COPY",FACE,{"derivedFrom":makeQuery(id+"F9.boolean.opBoolean","SPLIT",FACE,{"disambiguationData":[TD([makeQuery(id+"F5.boolean.opBoolean","COPY",FACE,{"derivedFrom":makeQuery(id+"F5.opExtrude","SWEPT_FACE",FACE,{"disambiguationData":[OSD([subQ0])]})})])],"derivedFrom":subQ1}),"instanceName":"1"}),"instanceName":"1"}),makeQuery(id+"F19.opPattern","COPY",FACE,{"derivedFrom":makeQuery(id+"F16.opPattern","COPY",FACE,{"derivedFrom":makeQuery(id+"F9.boolean.opBoolean","SPLIT",FACE,{"disambiguationData":[TD([makeQuery(id+"F9.opExtrude","SWEPT_FACE",FACE,{"disambiguationData":[OSD([sQuery(id+"F8.wireOp",EDGE,"E25")])]})])],"derivedFrom":subQ1}),"instanceName":"1"}),"instanceName":"1"}),makeQuery(id+"F19.opPattern","COPY",FACE,{"derivedFrom":makeQuery(id+"F16.opPattern","COPY",FACE,{"derivedFrom":makeQuery(id+"F9.boolean.opBoolean","SPLIT",FACE,{"disambiguationData":[TD([makeQuery(id+"F9.opExtrude","SWEPT_FACE",FACE,{"disambiguationData":[OSD([sQuery(id+"F8.wireOp",EDGE,"E32")])]})])],"derivedFrom":subQ1}),"instanceName":"1"}),"instanceName":"1"}),makeQuery(id+"F19.opPattern","COPY",FACE,{"derivedFrom":makeQuery(id+"F16.opPattern","COPY",FACE,{"derivedFrom":makeQuery(id+"F9.boolean.opBoolean","SPLIT",FACE,{"disambiguationData":[TD([makeQuery(id+"F9.opExtrude","SWEPT_FACE",FACE,{"disambiguationData":[OSD([sQuery(id+"F8.wireOp",EDGE,"E33.0")])]})])],"derivedFrom":subQ1}),"instanceName":"1"}),"instanceName":"1"}),makeQuery(id+"F19.opPattern","COPY",FACE,{"derivedFrom":makeQuery(id+"F16.opPattern","COPY",FACE,{"derivedFrom":makeQuery(id+"F9.boolean.opBoolean","SPLIT",FACE,{"disambiguationData":[TD([makeQuery(id+"F9.opExtrude","SWEPT_FACE",FACE,{"disambiguationData":[OSD([sQuery(id+"F8.wireOp",EDGE,"E37")])]})])],"derivedFrom":subQ1}),"instanceName":"1"}),"instanceName":"1"}),makeQuery(id+"F19.opPattern","COPY",FACE,{"derivedFrom":makeQuery(id+"F16.opPattern","COPY",FACE,{"derivedFrom":makeQuery(id+"F9.boolean.opBoolean","SPLIT",FACE,{"disambiguationData":[TD([makeQuery(id+"F9.opExtrude","SWEPT_FACE",FACE,{"disambiguationData":[OSD([sQuery(id+"F8.wireOp",EDGE,"E51.MirrorCS")])]})])],"derivedFrom":subQ1}),"instanceName":"1"}),"instanceName":"1"}),makeQuery(id+"F19.opPattern","COPY",FACE,{"derivedFrom":makeQuery(id+"F16.opPattern","COPY",FACE,{"derivedFrom":makeQuery(id+"F9.boolean.opBoolean","SPLIT",FACE,{"disambiguationData":[TD([makeQuery(id+"F9.opExtrude","SWEPT_FACE",FACE,{"disambiguationData":[OSD([sQuery(id+"F8.wireOp",EDGE,"E53.MirrorCS")])]})])],"derivedFrom":subQ1}),"instanceName":"1"}),"instanceName":"1"}),makeQuery(id+"F19.opPattern","COPY",FACE,{"derivedFrom":makeQuery(id+"F16.opPattern","COPY",FACE,{"derivedFrom":makeQuery(id+"F9.boolean.opBoolean","SPLIT",FACE,{"disambiguationData":[TD([makeQuery(id+"F9.opExtrude","SWEPT_FACE",FACE,{"disambiguationData":[OSD([sQuery(id+"F8.wireOp",EDGE,"E80")])]})])],"derivedFrom":subQ1}),"instanceName":"1"}),"instanceName":"1"}),makeQuery(id+"F19.opPattern","COPY",FACE,{"derivedFrom":makeQuery(id+"F16.opPattern","COPY",FACE,{"derivedFrom":makeQuery(id+"F9.boolean.opBoolean","SPLIT",FACE,{"disambiguationData":[TD([makeQuery(id+"F9.opExtrude","SWEPT_FACE",FACE,{"disambiguationData":[OSD([sQuery(id+"F8.wireOp",EDGE,"E83")])]})])],"derivedFrom":subQ1}),"instanceName":"1"}),"instanceName":"1"}),makeQuery(id+"F21.opExtrude","CAP_FACE",FACE,{"disambiguationData":[OSD([sQuery(id+"F20.wireOp",EDGE,"E307.0.0")])],"isStart":false})]});}
            var sketch = newSketch(context, id + "F95", { "sketchPlane" : qUnion([Q0])});
            skPoint(sketch, "E1383.0", {"position": v(50.8, 38.1) * mm});
            skLineSegment(sketch, "E1384", {"start": v(48.32, 43.06) * mm, "end": v(53.28, 43.06) * mm});
            skEllipticalArc(sketch, "E1385", {});
            skEllipticalArc(sketch, "E1386", {});
            skArc(sketch, "E1387", {"start": v(48.37, 44.01) * mm, "mid": v(47.32, 43.69) * mm, "end": v(46.32, 43.22) * mm});
            skLineSegment(sketch, "E1388", {"start": v(50.8, 43.06) * mm, "end": v(50.8, 42.83) * mm});
            skArc(sketch, "E1389.MirrorCS", {"start": v(53.23, 44.01) * mm, "mid": v(54.28, 43.69) * mm, "end": v(55.28, 43.22) * mm});
            skEllipse(sketch, "E1390", {"center": v(50.8, 43.36) * mm, "majorRadius": 1.32 * mm, "minorRadius": 0.3 * mm, "majorAxis": v(1, 0)});
            const initialGuessF95  = {"E1385": [0.0508, 0.043060265481472015, 1, 0, 0.004602055382728565, 0.000695379208512772, 2.907045176759056, 0.23454747683073718], "E1386": [0.0508, 0.04282783086789428, 1, 0, 0.005145917620029898, 0.001341097149963466, 2.062127929981911, 1.0794647236078807]};
            skSetInitialGuess(sketch, initialGuessF95);
            skSolve(sketch);
        }
        {
            var Q0;
            Q0 = qSketchRegion(id + "F95", true);
            var Q1;
            Q1=makeQuery(id+"F34.opExtrude","CAP_FACE",FACE,{"disambiguationData":[OSD([sQuery(id+"F33.wireOp",EDGE,"E523"),sQuery(id+"F33.wireOp",EDGE,"E524"),sQuery(id+"F33.wireOp",EDGE,"E525"),sQuery(id+"F33.wireOp",EDGE,"E526"),sQuery(id+"F33.wireOp",EDGE,"E527"),sQuery(id+"F33.wireOp",EDGE,"E528.trimOffspring"),sQuery(id+"F33.wireOp",EDGE,"E529.MirrorCS"),sQuery(id+"F33.wireOp",EDGE,"E530.MirrorCS"),sQuery(id+"F33.wireOp",EDGE,"E534.MirrorCS"),sQuery(id+"F33.wireOp",EDGE,"E535.MirrorCS"),sQuery(id+"F33.wireOp",EDGE,"E536.MirrorCS"),sQuery(id+"F33.wireOp",EDGE,"E537.MirrorCS"),sQuery(id+"F33.wireOp",EDGE,"E538.MirrorCS"),sQuery(id+"F33.wireOp",EDGE,"E539.MirrorCS"),sQuery(id+"F33.wireOp",EDGE,"E540.MirrorCS"),sQuery(id+"F33.wireOp",EDGE,"E541.MirrorCS"),sQuery(id+"F33.wireOp",EDGE,"E542.MirrorCS"),sQuery(id+"F33.wireOp",EDGE,"E543.MirrorCS"),sQuery(id+"F33.wireOp",EDGE,"E544.MirrorCS"),sQuery(id+"F33.wireOp",EDGE,"E545.MirrorCS"),sQuery(id+"F33.wireOp",EDGE,"E546.MirrorCS"),sQuery(id+"F33.wireOp",EDGE,"E547.MirrorCS"),sQuery(id+"F33.wireOp",EDGE,"E548.MirrorCS"),sQuery(id+"F33.wireOp",EDGE,"E549.MirrorCS"),sQuery(id+"F33.wireOp",EDGE,"E551.trimOffspring"),sQuery(id+"F33.wireOp",EDGE,"E552.trimOffspring"),sQuery(id+"F33.wireOp",EDGE,"E553.trimOffspring"),sQuery(id+"F33.wireOp",EDGE,"E554.trimOffspring"),sQuery(id+"F33.wireOp",EDGE,"E555.trimOffspring"),sQuery(id+"F33.wireOp",EDGE,"E556.trimOffspring"),sQuery(id+"F33.wireOp",EDGE,"E557.trimOffspring"),sQuery(id+"F33.wireOp",EDGE,"E558.trimOffspring"),sQuery(id+"F33.wireOp",EDGE,"E559.trimOffspring"),sQuery(id+"F33.wireOp",EDGE,"E560.trimOffspring"),sQuery(id+"F33.wireOp",EDGE,"E561.trimOffspring"),sQuery(id+"F33.wireOp",EDGE,"E562.trimOffspring"),sQuery(id+"F33.wireOp",EDGE,"E563.trimOffspring"),sQuery(id+"F33.wireOp",EDGE,"E564.trimOffspring"),sQuery(id+"F33.wireOp",EDGE,"E565.trimOffspring"),sQuery(id+"F33.wireOp",EDGE,"E566.trimOffspring"),sQuery(id+"F33.wireOp",EDGE,"E567.trimOffspring"),sQuery(id+"F33.wireOp",EDGE,"E568.trimOffspring"),sQuery(id+"F33.wireOp",EDGE,"E569.trimOffspring"),sQuery(id+"F33.wireOp",EDGE,"E570.trimOffspring"),sQuery(id+"F33.wireOp",EDGE,"E571.trimOffspring"),sQuery(id+"F33.wireOp",EDGE,"E572.trimOffspring"),sQuery(id+"F33.wireOp",EDGE,"E573.trimOffspring"),sQuery(id+"F33.wireOp",EDGE,"E574.trimOffspring"),sQuery(id+"F33.wireOp",EDGE,"E575.trimOffspring"),sQuery(id+"F33.wireOp",EDGE,"E576.trimOffspring"),sQuery(id+"F33.wireOp",EDGE,"E577.trimOffspring"),sQuery(id+"F33.wireOp",EDGE,"E578.trimOffspring"),sQuery(id+"F33.wireOp",EDGE,"E579.trimOffspring"),sQuery(id+"F33.wireOp",EDGE,"E580.trimOffspring"),sQuery(id+"F33.wireOp",EDGE,"E581.trimOffspring"),sQuery(id+"F33.wireOp",EDGE,"E582.trimOffspring"),sQuery(id+"F33.wireOp",EDGE,"E583.trimOffspring"),sQuery(id+"F33.wireOp",EDGE,"E584.trimOffspring"),sQuery(id+"F33.wireOp",EDGE,"E585.trimOffspring"),sQuery(id+"F33.wireOp",EDGE,"E586.trimOffspring"),sQuery(id+"F33.wireOp",EDGE,"E587.trimOffspring"),sQuery(id+"F33.wireOp",EDGE,"E588.trimOffspring"),sQuery(id+"F33.wireOp",EDGE,"E589.trimOffspring"),sQuery(id+"F33.wireOp",EDGE,"E590.trimOffspring"),sQuery(id+"F33.wireOp",EDGE,"E591.trimOffspring"),sQuery(id+"F33.wireOp",EDGE,"E592.trimOffspring"),sQuery(id+"F33.wireOp",EDGE,"E593.trimOffspring"),sQuery(id+"F33.wireOp",EDGE,"E594.trimOffspring"),sQuery(id+"F33.wireOp",EDGE,"E595.trimOffspring"),sQuery(id+"F33.wireOp",EDGE,"E596.trimOffspring"),sQuery(id+"F33.wireOp",EDGE,"E597.trimOffspring"),sQuery(id+"F33.wireOp",EDGE,"E598.trimOffspring")])],"isStart":false});
            extrude(context, id + "F96", {"entities" : qUnion([Q0]), "operationType" : NewBodyOperationType.ADD, "endBound" : BoundingType.UP_TO_SURFACE, "depth" : 25.4 * mm, "endBoundEntityFace" : qUnion([Q1]), "offsetDistance" : 25.4 * mm});
        }
        {
            var Q0;
            Q0=makeQuery(id+"F85.opExtrude","CAP_FACE",FACE,{"disambiguationData":[OSD([sQuery(id+"F84.wireOp",EDGE,"E1211"),sQuery(id+"F84.wireOp",EDGE,"E1212"),sQuery(id+"F84.wireOp",EDGE,"E1213"),sQuery(id+"F84.wireOp",EDGE,"E1215.MirrorCS"),sQuery(id+"F84.wireOp",EDGE,"E1216.bottom"),sQuery(id+"F84.wireOp",EDGE,"E1216.left"),sQuery(id+"F84.wireOp",EDGE,"E1216.right"),sQuery(id+"F84.wireOp",EDGE,"E1217.bottom"),sQuery(id+"F84.wireOp",EDGE,"E1217.top"),sQuery(id+"F84.wireOp",EDGE,"E1217.left"),sQuery(id+"F84.wireOp",EDGE,"E1217.right"),sQuery(id+"F84.wireOp",EDGE,"E1218.trimOffspring"),sQuery(id+"F84.wireOp",EDGE,"E1219.trimOffspring"),sQuery(id+"F84.wireOp",EDGE,"E1220"),sQuery(id+"F84.wireOp",EDGE,"E1223.trimOffspring"),sQuery(id+"F84.wireOp",EDGE,"E1224.trimOffspring"),sQuery(id+"F84.wireOp",EDGE,"E1225"),sQuery(id+"F84.wireOp",EDGE,"E1226.MirrorCS")])],"isStart":false});
            var sketch = newSketch(context, id + "F97", { "sketchPlane" : qUnion([Q0])});
            skCircle(sketch, "E1391", {"center": v(-50.8, -56.74) * mm, "radius": 0.57 * mm});
            skArc(sketch, "E1392", {"start": v(-51.2, -57.15) * mm, "mid": v(-51.6, -58.44) * mm, "end": v(-51.53, -59.8) * mm});
            skLineSegment(sketch, "E1393.bottom", {"start": v(-51.88, -59.3) * mm, "end": v(-49.72, -59.3) * mm});
            skLineSegment(sketch, "E1393.left", {"start": v(-51.88, -59.3) * mm, "end": v(-51.88, -60.53) * mm});
            skLineSegment(sketch, "E1393.right", {"start": v(-49.72, -59.3) * mm, "end": v(-49.72, -60.53) * mm});
            skPoint(sketch, "E1393.middle", {"position": v(-50.8, -59.92) * mm});
            skLineSegment(sketch, "E1394.0", {"start": v(-49.3, -60.17) * mm, "end": v(-52.3, -60.17) * mm});
            skLineSegment(sketch, "E1395", {"start": v(-50.8, -56.74) * mm, "end": v(-50.8, -57.01) * mm});
            skArc(sketch, "E1396.MirrorCS", {"start": v(-50.4, -57.15) * mm, "mid": v(-50, -58.44) * mm, "end": v(-50.07, -59.8) * mm});
            skSolve(sketch);
        }
        {
            var Q0;
            Q0 = qSketchRegion(id + "F97", true);
            var Q1;
            {var subQ0=sQuery(id+"F4.wireOp",EDGE,"E8");var subQ1=makeQuery(id+"F5.boolean.opBoolean","COPY",FACE,{"derivedFrom":makeQuery(id+"F5.opExtrude","SWEPT_FACE",FACE,{"disambiguationData":[OSD([subQ0])]})});var subQ2=makeQuery(id+"F5.boolean.opBoolean","COPY",FACE,{"derivedFrom":makeQuery(id+"F5.opExtrude","CAP_FACE",FACE,{"disambiguationData":[OSD([subQ0])],"isStart":false})});var subQ3=makeQuery(id+"F39.opPattern","COPY",FACE,{"derivedFrom":makeQuery(id+"F21.boolean.opBoolean","MERGE",FACE,{"derivedFrom":[makeQuery(id+"F19.opPattern","COPY",FACE,{"derivedFrom":makeQuery(id+"F17.opPattern","COPY",FACE,{"derivedFrom":makeQuery(id+"F9.boolean.opBoolean","SPLIT",FACE,{"disambiguationData":[TD([subQ1])],"derivedFrom":subQ2}),"instanceName":"1"}),"instanceName":"1"}),makeQuery(id+"F19.opPattern","COPY",FACE,{"derivedFrom":makeQuery(id+"F17.opPattern","COPY",FACE,{"derivedFrom":makeQuery(id+"F9.boolean.opBoolean","SPLIT",FACE,{"disambiguationData":[TD([makeQuery(id+"F9.opExtrude","SWEPT_FACE",FACE,{"disambiguationData":[OSD([sQuery(id+"F8.wireOp",EDGE,"E25")])]})])],"derivedFrom":subQ2}),"instanceName":"1"}),"instanceName":"1"}),makeQuery(id+"F19.opPattern","COPY",FACE,{"derivedFrom":makeQuery(id+"F17.opPattern","COPY",FACE,{"derivedFrom":makeQuery(id+"F9.boolean.opBoolean","SPLIT",FACE,{"disambiguationData":[TD([makeQuery(id+"F9.opExtrude","SWEPT_FACE",FACE,{"disambiguationData":[OSD([sQuery(id+"F8.wireOp",EDGE,"E32")])]})])],"derivedFrom":subQ2}),"instanceName":"1"}),"instanceName":"1"}),makeQuery(id+"F19.opPattern","COPY",FACE,{"derivedFrom":makeQuery(id+"F17.opPattern","COPY",FACE,{"derivedFrom":makeQuery(id+"F9.boolean.opBoolean","SPLIT",FACE,{"disambiguationData":[TD([makeQuery(id+"F9.opExtrude","SWEPT_FACE",FACE,{"disambiguationData":[OSD([sQuery(id+"F8.wireOp",EDGE,"E33.0")])]})])],"derivedFrom":subQ2}),"instanceName":"1"}),"instanceName":"1"}),makeQuery(id+"F19.opPattern","COPY",FACE,{"derivedFrom":makeQuery(id+"F17.opPattern","COPY",FACE,{"derivedFrom":makeQuery(id+"F9.boolean.opBoolean","SPLIT",FACE,{"disambiguationData":[TD([makeQuery(id+"F9.opExtrude","SWEPT_FACE",FACE,{"disambiguationData":[OSD([sQuery(id+"F8.wireOp",EDGE,"E37")])]})])],"derivedFrom":subQ2}),"instanceName":"1"}),"instanceName":"1"}),makeQuery(id+"F19.opPattern","COPY",FACE,{"derivedFrom":makeQuery(id+"F17.opPattern","COPY",FACE,{"derivedFrom":makeQuery(id+"F9.boolean.opBoolean","SPLIT",FACE,{"disambiguationData":[TD([makeQuery(id+"F9.opExtrude","SWEPT_FACE",FACE,{"disambiguationData":[OSD([sQuery(id+"F8.wireOp",EDGE,"E51.MirrorCS")])]})])],"derivedFrom":subQ2}),"instanceName":"1"}),"instanceName":"1"}),makeQuery(id+"F19.opPattern","COPY",FACE,{"derivedFrom":makeQuery(id+"F17.opPattern","COPY",FACE,{"derivedFrom":makeQuery(id+"F9.boolean.opBoolean","SPLIT",FACE,{"disambiguationData":[TD([makeQuery(id+"F9.opExtrude","SWEPT_FACE",FACE,{"disambiguationData":[OSD([sQuery(id+"F8.wireOp",EDGE,"E53.MirrorCS")])]})])],"derivedFrom":subQ2}),"instanceName":"1"}),"instanceName":"1"}),makeQuery(id+"F19.opPattern","COPY",FACE,{"derivedFrom":makeQuery(id+"F17.opPattern","COPY",FACE,{"derivedFrom":makeQuery(id+"F9.boolean.opBoolean","SPLIT",FACE,{"disambiguationData":[TD([makeQuery(id+"F9.opExtrude","SWEPT_FACE",FACE,{"disambiguationData":[OSD([sQuery(id+"F8.wireOp",EDGE,"E80")])]})])],"derivedFrom":subQ2}),"instanceName":"1"}),"instanceName":"1"}),makeQuery(id+"F19.opPattern","COPY",FACE,{"derivedFrom":makeQuery(id+"F17.opPattern","COPY",FACE,{"derivedFrom":makeQuery(id+"F9.boolean.opBoolean","SPLIT",FACE,{"disambiguationData":[TD([makeQuery(id+"F9.opExtrude","SWEPT_FACE",FACE,{"disambiguationData":[OSD([sQuery(id+"F8.wireOp",EDGE,"E83")])]})])],"derivedFrom":subQ2}),"instanceName":"1"}),"instanceName":"1"})],"fromTools":[makeQuery(id+"F21.opExtrude","CAP_FACE",FACE,{"disambiguationData":[OSD([sQuery(id+"F20.wireOp",EDGE,"E309.0.0")])],"isStart":false})]}),"instanceName":"1"});Q1=makeQuery(id+"F75.boolean.opBoolean","MERGE",FACE,{"derivedFrom":[makeQuery(id+"F69.boolean.opBoolean","SPLIT",FACE,{"disambiguationData":[TD([makeQuery(id+"F69.opExtrude","SWEPT_FACE",FACE,{"disambiguationData":[OSD([sQuery(id+"F68.wireOp",EDGE,"E901")])]})])],"derivedFrom":subQ3}),makeQuery(id+"F69.boolean.opBoolean","SPLIT",FACE,{"disambiguationData":[TD([makeQuery(id+"F39.opPattern","COPY",FACE,{"derivedFrom":makeQuery(id+"F19.opPattern","COPY",FACE,{"derivedFrom":makeQuery(id+"F17.opPattern","COPY",FACE,{"derivedFrom":subQ1,"instanceName":"1"}),"instanceName":"1"}),"instanceName":"1"})])],"derivedFrom":subQ3})],"fromTools":[makeQuery(id+"F75.opExtrude","CAP_FACE",FACE,{"disambiguationData":[OSD([sQuery(id+"F74.wireOp",EDGE,"E1055.0"),sQuery(id+"F74.wireOp",EDGE,"E1056.0"),sQuery(id+"F74.wireOp",EDGE,"E1057.0"),sQuery(id+"F74.wireOp",EDGE,"E1058"),sQuery(id+"F74.wireOp",EDGE,"E1059"),sQuery(id+"F74.wireOp",EDGE,"E1060.0"),sQuery(id+"F74.wireOp",EDGE,"E1061"),sQuery(id+"F74.wireOp",EDGE,"E1062")])],"isStart":false})]});}
            extrude(context, id + "F98", {"entities" : qUnion([Q0]), "operationType" : NewBodyOperationType.ADD, "endBound" : BoundingType.UP_TO_SURFACE, "oppositeDirection" : true, "depth" : 25.4 * mm, "endBoundEntityFace" : qUnion([Q1]), "offsetDistance" : 25.4 * mm});
        }
        {
            var Q0;
            {var subQ0=sQuery(id+"F4.wireOp",EDGE,"E8");var subQ1=makeQuery(id+"F5.boolean.opBoolean","COPY",FACE,{"derivedFrom":makeQuery(id+"F5.opExtrude","CAP_FACE",FACE,{"disambiguationData":[OSD([subQ0])],"isStart":false})});Q0=makeQuery(id+"F39.opPattern","COPY",FACE,{"derivedFrom":makeQuery(id+"F21.boolean.opBoolean","MERGE",FACE,{"derivedFrom":[makeQuery(id+"F19.opPattern","COPY",FACE,{"derivedFrom":makeQuery(id+"F16.opPattern","COPY",FACE,{"derivedFrom":makeQuery(id+"F9.boolean.opBoolean","SPLIT",FACE,{"disambiguationData":[TD([makeQuery(id+"F5.boolean.opBoolean","COPY",FACE,{"derivedFrom":makeQuery(id+"F5.opExtrude","SWEPT_FACE",FACE,{"disambiguationData":[OSD([subQ0])]})})])],"derivedFrom":subQ1}),"instanceName":"1"}),"instanceName":"1"}),makeQuery(id+"F19.opPattern","COPY",FACE,{"derivedFrom":makeQuery(id+"F16.opPattern","COPY",FACE,{"derivedFrom":makeQuery(id+"F9.boolean.opBoolean","SPLIT",FACE,{"disambiguationData":[TD([makeQuery(id+"F9.opExtrude","SWEPT_FACE",FACE,{"disambiguationData":[OSD([sQuery(id+"F8.wireOp",EDGE,"E25")])]})])],"derivedFrom":subQ1}),"instanceName":"1"}),"instanceName":"1"}),makeQuery(id+"F19.opPattern","COPY",FACE,{"derivedFrom":makeQuery(id+"F16.opPattern","COPY",FACE,{"derivedFrom":makeQuery(id+"F9.boolean.opBoolean","SPLIT",FACE,{"disambiguationData":[TD([makeQuery(id+"F9.opExtrude","SWEPT_FACE",FACE,{"disambiguationData":[OSD([sQuery(id+"F8.wireOp",EDGE,"E32")])]})])],"derivedFrom":subQ1}),"instanceName":"1"}),"instanceName":"1"}),makeQuery(id+"F19.opPattern","COPY",FACE,{"derivedFrom":makeQuery(id+"F16.opPattern","COPY",FACE,{"derivedFrom":makeQuery(id+"F9.boolean.opBoolean","SPLIT",FACE,{"disambiguationData":[TD([makeQuery(id+"F9.opExtrude","SWEPT_FACE",FACE,{"disambiguationData":[OSD([sQuery(id+"F8.wireOp",EDGE,"E33.0")])]})])],"derivedFrom":subQ1}),"instanceName":"1"}),"instanceName":"1"}),makeQuery(id+"F19.opPattern","COPY",FACE,{"derivedFrom":makeQuery(id+"F16.opPattern","COPY",FACE,{"derivedFrom":makeQuery(id+"F9.boolean.opBoolean","SPLIT",FACE,{"disambiguationData":[TD([makeQuery(id+"F9.opExtrude","SWEPT_FACE",FACE,{"disambiguationData":[OSD([sQuery(id+"F8.wireOp",EDGE,"E37")])]})])],"derivedFrom":subQ1}),"instanceName":"1"}),"instanceName":"1"}),makeQuery(id+"F19.opPattern","COPY",FACE,{"derivedFrom":makeQuery(id+"F16.opPattern","COPY",FACE,{"derivedFrom":makeQuery(id+"F9.boolean.opBoolean","SPLIT",FACE,{"disambiguationData":[TD([makeQuery(id+"F9.opExtrude","SWEPT_FACE",FACE,{"disambiguationData":[OSD([sQuery(id+"F8.wireOp",EDGE,"E51.MirrorCS")])]})])],"derivedFrom":subQ1}),"instanceName":"1"}),"instanceName":"1"}),makeQuery(id+"F19.opPattern","COPY",FACE,{"derivedFrom":makeQuery(id+"F16.opPattern","COPY",FACE,{"derivedFrom":makeQuery(id+"F9.boolean.opBoolean","SPLIT",FACE,{"disambiguationData":[TD([makeQuery(id+"F9.opExtrude","SWEPT_FACE",FACE,{"disambiguationData":[OSD([sQuery(id+"F8.wireOp",EDGE,"E53.MirrorCS")])]})])],"derivedFrom":subQ1}),"instanceName":"1"}),"instanceName":"1"}),makeQuery(id+"F19.opPattern","COPY",FACE,{"derivedFrom":makeQuery(id+"F16.opPattern","COPY",FACE,{"derivedFrom":makeQuery(id+"F9.boolean.opBoolean","SPLIT",FACE,{"disambiguationData":[TD([makeQuery(id+"F9.opExtrude","SWEPT_FACE",FACE,{"disambiguationData":[OSD([sQuery(id+"F8.wireOp",EDGE,"E80")])]})])],"derivedFrom":subQ1}),"instanceName":"1"}),"instanceName":"1"}),makeQuery(id+"F19.opPattern","COPY",FACE,{"derivedFrom":makeQuery(id+"F16.opPattern","COPY",FACE,{"derivedFrom":makeQuery(id+"F9.boolean.opBoolean","SPLIT",FACE,{"disambiguationData":[TD([makeQuery(id+"F9.opExtrude","SWEPT_FACE",FACE,{"disambiguationData":[OSD([sQuery(id+"F8.wireOp",EDGE,"E83")])]})])],"derivedFrom":subQ1}),"instanceName":"1"}),"instanceName":"1"}),makeQuery(id+"F21.opExtrude","CAP_FACE",FACE,{"disambiguationData":[OSD([sQuery(id+"F20.wireOp",EDGE,"E307.0.0")])],"isStart":false})]}),"instanceName":"1"});}
            var sketch = newSketch(context, id + "F99", { "sketchPlane" : qUnion([Q0])});
            skEllipse(sketch, "E1397", {"center": v(46.8, -55.8) * mm, "majorRadius": 4.1 * mm, "minorRadius": 2.17 * mm, "majorAxis": v(0.8, -0.59)});
            skArc(sketch, "E1398", {"start": v(49.2, -44.85) * mm, "mid": v(48.56, -51.21) * mm, "end": v(51.14, -57.05) * mm});
            skArc(sketch, "E1399", {"start": v(50.38, -45.92) * mm, "mid": v(49.46, -51.58) * mm, "end": v(51.14, -57.05) * mm});
            skArc(sketch, "E1400", {"start": v(49.2, -44.85) * mm, "mid": v(49.67, -45.52) * mm, "end": v(50.38, -45.92) * mm});
            skCircle(sketch, "E1401", {"center": v(50.97, -44.07) * mm, "radius": 1.5 * mm});
            skArc(sketch, "E1402", {"start": v(52.58, -46.07) * mm, "mid": v(53.38, -44.95) * mm, "end": v(53.5, -43.58) * mm});
            skArc(sketch, "E1403", {"start": v(57.38, -49.23) * mm, "mid": v(55.4, -47.01) * mm, "end": v(52.58, -46.07) * mm});
            skArc(sketch, "E1404", {"start": v(53.5, -43.58) * mm, "mid": v(54.8, -45.64) * mm, "end": v(56.84, -46.99) * mm});
            skArc(sketch, "E1405", {"start": v(57.38, -49.23) * mm, "mid": v(57.66, -47.98) * mm, "end": v(56.84, -46.99) * mm});
            skCircle(sketch, "E1406", {"center": v(52.59, -46.79) * mm, "radius": 0.36 * mm});
            skCircle(sketch, "E1407", {"center": v(53.88, -47.15) * mm, "radius": 0.36 * mm});
            skCircle(sketch, "E1408", {"center": v(55.05, -47.8) * mm, "radius": 0.36 * mm});
            skCircle(sketch, "E1409", {"center": v(56.05, -48.7) * mm, "radius": 0.36 * mm});
            skCircle(sketch, "E1410", {"center": v(57, -49.63) * mm, "radius": 0.36 * mm});
            skLineSegment(sketch, "E1411", {"start": v(52.59, -46.79) * mm, "end": v(53.88, -47.15) * mm});
            skLineSegment(sketch, "E1412", {"start": v(55.05, -47.8) * mm, "end": v(53.88, -47.15) * mm});
            skLineSegment(sketch, "E1413", {"start": v(55.05, -47.8) * mm, "end": v(56.05, -48.7) * mm});
            skLineSegment(sketch, "E1414", {"start": v(56.05, -48.7) * mm, "end": v(57, -49.63) * mm});
            skFitSpline(sketch, "E1415.0", {"points": [v(49.54, -58.1) * mm, v(49.72, -57.93) * mm, v(49.83, -57.7) * mm, v(49.87, -57.4) * mm, v(49.8, -56.98) * mm, v(49.62, -56.5) * mm, v(49.32, -55.97) * mm, v(48.9, -55.43) * mm, v(48.38, -54.92) * mm, v(47.8, -54.44) * mm, v(47.17, -54.03) * mm, v(46.52, -53.7) * mm, v(45.88, -53.46) * mm, v(45.29, -53.33) * mm, v(44.77, -53.3) * mm, v(44.35, -53.37) * mm, v(44.07, -53.5) * mm, v(43.89, -53.67) * mm, v(43.78, -53.9) * mm, v(43.74, -54.2) * mm, v(43.8, -54.63) * mm, v(43.99, -55.11) * mm, v(44.3, -55.64) * mm, v(44.72, -56.17) * mm, v(45.23, -56.69) * mm, v(45.81, -57.16) * mm, v(46.44, -57.58) * mm, v(47.09, -57.9) * mm, v(47.73, -58.14) * mm, v(48.32, -58.27) * mm, v(48.84, -58.3) * mm, v(49.26, -58.23) * mm, v(49.54, -58.1) * mm, v(49.72, -57.93) * mm, v(49.83, -57.7) * mm]});
            skCircle(sketch, "E1416", {"center": v(43.9, -53.68) * mm, "radius": 0.5 * mm});
            skArc(sketch, "E1417", {"start": v(47.74, -54.95) * mm, "mid": v(48.09, -54.05) * mm, "end": v(47.33, -54.65) * mm});
            skArc(sketch, "E1418.MirrorC", {"start": v(46.28, -56.95) * mm, "mid": v(46.32, -57.2) * mm, "end": v(46.23, -57.43) * mm});
            skCircle(sketch, "E1419.MirrorC", {"center": v(49.7, -57.92) * mm, "radius": 0.5 * mm});
            skArc(sketch, "E1420", {"start": v(46.54, -56.6) * mm, "mid": v(46.93, -56.63) * mm, "end": v(47.3, -56.47) * mm});
            skCircle(sketch, "E1421.0", {"center": v(46.8, -55.8) * mm, "radius": 0.33 * mm});
            skLineSegment(sketch, "E1422.trimOffspring", {"start": v(46.01, -55.53) * mm, "end": v(44.1, -54.14) * mm});
            skLineSegment(sketch, "E1423.trimOffspring", {"start": v(46.3, -55.13) * mm, "end": v(44.4, -53.74) * mm});
            skLineSegment(sketch, "E1424.trimOffspring", {"start": v(47.3, -56.47) * mm, "end": v(49.21, -57.87) * mm});
            skLineSegment(sketch, "E1425.trimOffspring", {"start": v(47.6, -56.07) * mm, "end": v(49.5, -57.46) * mm});
            skLineSegment(sketch, "E1426.trimOffspring", {"start": v(47.48, -55.3) * mm, "end": v(47.74, -54.95) * mm});
            skLineSegment(sketch, "E1427.trimOffspring", {"start": v(47.07, -55.01) * mm, "end": v(47.33, -54.65) * mm});
            skLineSegment(sketch, "E1428.trimOffspring", {"start": v(46.13, -56.3) * mm, "end": v(45.87, -56.66) * mm});
            skLineSegment(sketch, "E1429.trimOffspring", {"start": v(46.54, -56.6) * mm, "end": v(46.28, -56.95) * mm});
            skArc(sketch, "E1430.trimOffspring", {"start": v(46.01, -55.53) * mm, "mid": v(45.98, -55.93) * mm, "end": v(46.13, -56.3) * mm});
            skArc(sketch, "E1431.trimOffspring", {"start": v(47.07, -55.01) * mm, "mid": v(46.68, -54.98) * mm, "end": v(46.3, -55.13) * mm});
            skArc(sketch, "E1432.trimOffspring", {"start": v(47.6, -56.07) * mm, "mid": v(47.63, -55.67) * mm, "end": v(47.48, -55.3) * mm});
            skLineSegment(sketch, "E1433.trimOffspring", {"start": v(45.32, -57.4) * mm, "end": v(45.32, -57.41) * mm});
            skLineSegment(sketch, "E1434.trimOffspring", {"start": v(45.73, -57.7) * mm, "end": v(45.73, -57.7) * mm});
            skArc(sketch, "E1435.trimOffspring", {"start": v(45.43, -56.85) * mm, "mid": v(45.62, -56.7) * mm, "end": v(45.87, -56.66) * mm});
            skLineSegment(sketch, "E1436.trimOffspring", {"start": v(47.59, -54.3) * mm, "end": v(47.88, -53.9) * mm});
            skLineSegment(sketch, "E1437.trimOffspring", {"start": v(48, -54.6) * mm, "end": v(48.29, -54.2) * mm});
            skLineSegment(sketch, "E1438.trimOffspring", {"start": v(49.82, -57.7) * mm, "end": v(50.26, -58.01) * mm});
            skLineSegment(sketch, "E1439.trimOffspring", {"start": v(49.52, -58.1) * mm, "end": v(49.97, -58.42) * mm});
            skLineSegment(sketch, "E1440.trimOffspring", {"start": v(44.09, -53.5) * mm, "end": v(43.64, -53.19) * mm});
            skLineSegment(sketch, "E1441.trimOffspring", {"start": v(43.8, -53.91) * mm, "end": v(43.35, -53.59) * mm});
            skFitSpline(sketch, "E1442.trimOffspring", {"points": [v(49.54, -58.1) * mm, v(49.72, -57.93) * mm, v(49.83, -57.7) * mm, v(49.87, -57.4) * mm, v(49.8, -56.98) * mm, v(49.62, -56.5) * mm, v(49.32, -55.97) * mm, v(48.9, -55.43) * mm, v(48.38, -54.92) * mm, v(47.8, -54.44) * mm, v(47.17, -54.03) * mm, v(46.52, -53.7) * mm, v(45.88, -53.46) * mm, v(45.29, -53.33) * mm, v(44.77, -53.3) * mm, v(44.35, -53.37) * mm, v(44.07, -53.5) * mm, v(43.89, -53.67) * mm, v(43.78, -53.9) * mm, v(43.74, -54.2) * mm, v(43.8, -54.63) * mm, v(43.99, -55.11) * mm, v(44.3, -55.64) * mm, v(44.72, -56.17) * mm, v(45.23, -56.69) * mm, v(45.81, -57.16) * mm, v(46.44, -57.58) * mm, v(47.09, -57.9) * mm, v(47.73, -58.14) * mm, v(48.32, -58.27) * mm, v(48.84, -58.3) * mm, v(49.26, -58.23) * mm, v(49.54, -58.1) * mm, v(49.72, -57.93) * mm, v(49.83, -57.7) * mm]});
            skFitSpline(sketch, "E1443.trimOffspring", {"points": [v(49.54, -58.1) * mm, v(49.72, -57.93) * mm, v(49.83, -57.7) * mm, v(49.87, -57.4) * mm, v(49.8, -56.98) * mm, v(49.62, -56.5) * mm, v(49.32, -55.97) * mm, v(48.9, -55.43) * mm, v(48.38, -54.92) * mm, v(47.8, -54.44) * mm, v(47.17, -54.03) * mm, v(46.52, -53.7) * mm, v(45.88, -53.46) * mm, v(45.29, -53.33) * mm, v(44.77, -53.3) * mm, v(44.35, -53.37) * mm, v(44.07, -53.5) * mm, v(43.89, -53.67) * mm, v(43.78, -53.9) * mm, v(43.74, -54.2) * mm, v(43.8, -54.63) * mm, v(43.99, -55.11) * mm, v(44.3, -55.64) * mm, v(44.72, -56.17) * mm, v(45.23, -56.69) * mm, v(45.81, -57.16) * mm, v(46.44, -57.58) * mm, v(47.09, -57.9) * mm, v(47.73, -58.14) * mm, v(48.32, -58.27) * mm, v(48.84, -58.3) * mm, v(49.26, -58.23) * mm, v(49.54, -58.1) * mm, v(49.72, -57.93) * mm, v(49.83, -57.7) * mm]});
            skFitSpline(sketch, "E1444.trimOffspring", {"points": [v(49.54, -58.1) * mm, v(49.72, -57.93) * mm, v(49.83, -57.7) * mm, v(49.87, -57.4) * mm, v(49.8, -56.98) * mm, v(49.62, -56.5) * mm, v(49.32, -55.97) * mm, v(48.9, -55.43) * mm, v(48.38, -54.92) * mm, v(47.8, -54.44) * mm, v(47.17, -54.03) * mm, v(46.52, -53.7) * mm, v(45.88, -53.46) * mm, v(45.29, -53.33) * mm, v(44.77, -53.3) * mm, v(44.35, -53.37) * mm, v(44.07, -53.5) * mm, v(43.89, -53.67) * mm, v(43.78, -53.9) * mm, v(43.74, -54.2) * mm, v(43.8, -54.63) * mm, v(43.99, -55.11) * mm, v(44.3, -55.64) * mm, v(44.72, -56.17) * mm, v(45.23, -56.69) * mm, v(45.81, -57.16) * mm, v(46.44, -57.58) * mm, v(47.09, -57.9) * mm, v(47.73, -58.14) * mm, v(48.32, -58.27) * mm, v(48.84, -58.3) * mm, v(49.26, -58.23) * mm, v(49.54, -58.1) * mm, v(49.72, -57.93) * mm, v(49.83, -57.7) * mm]});
            skSolve(sketch);
        }
        {
            var Q0;
            Q0 = qSketchRegion(id + "F99", true);
            var Q1;
            Q1=makeQuery(id+"F79.boolean.opBoolean","MERGE",FACE,{"derivedFrom":[makeQuery(id+"F77.opExtrude","CAP_FACE",FACE,{"disambiguationData":[OSD([sQuery(id+"F76.wireOp",EDGE,"E1063"),sQuery(id+"F76.wireOp",EDGE,"E1064"),sQuery(id+"F76.wireOp",EDGE,"E1065"),sQuery(id+"F76.wireOp",EDGE,"E1066"),sQuery(id+"F76.wireOp",EDGE,"E1067.MirrorC"),sQuery(id+"F76.wireOp",EDGE,"E1068.MirrorC"),sQuery(id+"F76.wireOp",EDGE,"E1069.MirrorC"),sQuery(id+"F76.wireOp",EDGE,"E1070.trimOffspring"),sQuery(id+"F76.wireOp",EDGE,"E1071.trimOffspring"),sQuery(id+"F76.wireOp",EDGE,"E1072.trimOffspring"),sQuery(id+"F76.wireOp",EDGE,"E1073"),sQuery(id+"F76.wireOp",EDGE,"E1074.bottom"),sQuery(id+"F76.wireOp",EDGE,"E1074.top"),sQuery(id+"F76.wireOp",EDGE,"E1075.trimOffspring"),sQuery(id+"F76.wireOp",EDGE,"E1076.trimOffspring"),sQuery(id+"F76.wireOp",EDGE,"E1081.MirrorCS"),sQuery(id+"F76.wireOp",EDGE,"E1082.MirrorCS"),sQuery(id+"F76.wireOp",EDGE,"E1083.MirrorCS"),sQuery(id+"F76.wireOp",EDGE,"E1084.MirrorCS"),sQuery(id+"F76.wireOp",EDGE,"E1085.MirrorC"),sQuery(id+"F76.wireOp",EDGE,"E1086.MirrorC"),sQuery(id+"F76.wireOp",EDGE,"E1087.MirrorC"),sQuery(id+"F76.wireOp",EDGE,"E1088.trimOffspring"),sQuery(id+"F76.wireOp",EDGE,"E1089.trimOffspring"),sQuery(id+"F76.wireOp",EDGE,"E1090.trimOffspring"),sQuery(id+"F76.wireOp",EDGE,"E1091.trimOffspring"),sQuery(id+"F76.wireOp",EDGE,"E1092.trimOffspring"),sQuery(id+"F76.wireOp",EDGE,"E1093.trimOffspring"),sQuery(id+"F76.wireOp",EDGE,"E1094.trimOffspring"),sQuery(id+"F76.wireOp",EDGE,"E1095")])],"isStart":false}),makeQuery(id+"F79.opExtrude","CAP_FACE",FACE,{"disambiguationData":[OSD([sQuery(id+"F78.wireOp",EDGE,"E1096"),sQuery(id+"F78.wireOp",EDGE,"E1097"),sQuery(id+"F78.wireOp",EDGE,"E1099"),sQuery(id+"F78.wireOp",EDGE,"E1100.0"),sQuery(id+"F78.wireOp",EDGE,"E1101.0"),sQuery(id+"F78.wireOp",EDGE,"E1102.MirrorC"),sQuery(id+"F78.wireOp",EDGE,"E1104.MirrorCS"),sQuery(id+"F78.wireOp",EDGE,"E1105.MirrorCS"),sQuery(id+"F78.wireOp",EDGE,"E1106.MirrorCS"),sQuery(id+"F78.wireOp",EDGE,"E1107.trimOffspring"),sQuery(id+"F78.wireOp",EDGE,"E1108.trimOffspring"),sQuery(id+"F78.wireOp",EDGE,"E1109.trimOffspring"),sQuery(id+"F78.wireOp",EDGE,"E1112"),sQuery(id+"F78.wireOp",EDGE,"E1113"),sQuery(id+"F78.wireOp",EDGE,"E1114"),sQuery(id+"F78.wireOp",EDGE,"E1115")])],"isStart":false})]});
            extrude(context, id + "F100", {"entities" : qUnion([Q0]), "operationType" : NewBodyOperationType.ADD, "endBound" : BoundingType.UP_TO_SURFACE, "depth" : 25.4 * mm, "endBoundEntityFace" : qUnion([Q1]), "offsetDistance" : 25.4 * mm});
        }
        {
            var Q0;
            {var subQ0=sQuery(id+"F4.wireOp",EDGE,"E8");var subQ1=makeQuery(id+"F5.boolean.opBoolean","COPY",FACE,{"derivedFrom":makeQuery(id+"F5.opExtrude","SWEPT_FACE",FACE,{"disambiguationData":[OSD([subQ0])]})});var subQ2=makeQuery(id+"F5.boolean.opBoolean","COPY",FACE,{"derivedFrom":makeQuery(id+"F5.opExtrude","CAP_FACE",FACE,{"disambiguationData":[OSD([subQ0])],"isStart":false})});Q0=makeQuery(id+"F100.boolean.opBoolean","SPLIT",FACE,{"disambiguationData":[TD([makeQuery(id+"F39.opPattern","COPY",FACE,{"derivedFrom":makeQuery(id+"F19.opPattern","COPY",FACE,{"derivedFrom":makeQuery(id+"F16.opPattern","COPY",FACE,{"derivedFrom":subQ1,"instanceName":"1"}),"instanceName":"1"}),"instanceName":"1"})])],"derivedFrom":makeQuery(id+"F39.opPattern","COPY",FACE,{"derivedFrom":makeQuery(id+"F21.boolean.opBoolean","MERGE",FACE,{"derivedFrom":[makeQuery(id+"F19.opPattern","COPY",FACE,{"derivedFrom":makeQuery(id+"F16.opPattern","COPY",FACE,{"derivedFrom":makeQuery(id+"F9.boolean.opBoolean","SPLIT",FACE,{"disambiguationData":[TD([subQ1])],"derivedFrom":subQ2}),"instanceName":"1"}),"instanceName":"1"}),makeQuery(id+"F19.opPattern","COPY",FACE,{"derivedFrom":makeQuery(id+"F16.opPattern","COPY",FACE,{"derivedFrom":makeQuery(id+"F9.boolean.opBoolean","SPLIT",FACE,{"disambiguationData":[TD([makeQuery(id+"F9.opExtrude","SWEPT_FACE",FACE,{"disambiguationData":[OSD([sQuery(id+"F8.wireOp",EDGE,"E25")])]})])],"derivedFrom":subQ2}),"instanceName":"1"}),"instanceName":"1"}),makeQuery(id+"F19.opPattern","COPY",FACE,{"derivedFrom":makeQuery(id+"F16.opPattern","COPY",FACE,{"derivedFrom":makeQuery(id+"F9.boolean.opBoolean","SPLIT",FACE,{"disambiguationData":[TD([makeQuery(id+"F9.opExtrude","SWEPT_FACE",FACE,{"disambiguationData":[OSD([sQuery(id+"F8.wireOp",EDGE,"E32")])]})])],"derivedFrom":subQ2}),"instanceName":"1"}),"instanceName":"1"}),makeQuery(id+"F19.opPattern","COPY",FACE,{"derivedFrom":makeQuery(id+"F16.opPattern","COPY",FACE,{"derivedFrom":makeQuery(id+"F9.boolean.opBoolean","SPLIT",FACE,{"disambiguationData":[TD([makeQuery(id+"F9.opExtrude","SWEPT_FACE",FACE,{"disambiguationData":[OSD([sQuery(id+"F8.wireOp",EDGE,"E33.0")])]})])],"derivedFrom":subQ2}),"instanceName":"1"}),"instanceName":"1"}),makeQuery(id+"F19.opPattern","COPY",FACE,{"derivedFrom":makeQuery(id+"F16.opPattern","COPY",FACE,{"derivedFrom":makeQuery(id+"F9.boolean.opBoolean","SPLIT",FACE,{"disambiguationData":[TD([makeQuery(id+"F9.opExtrude","SWEPT_FACE",FACE,{"disambiguationData":[OSD([sQuery(id+"F8.wireOp",EDGE,"E37")])]})])],"derivedFrom":subQ2}),"instanceName":"1"}),"instanceName":"1"}),makeQuery(id+"F19.opPattern","COPY",FACE,{"derivedFrom":makeQuery(id+"F16.opPattern","COPY",FACE,{"derivedFrom":makeQuery(id+"F9.boolean.opBoolean","SPLIT",FACE,{"disambiguationData":[TD([makeQuery(id+"F9.opExtrude","SWEPT_FACE",FACE,{"disambiguationData":[OSD([sQuery(id+"F8.wireOp",EDGE,"E51.MirrorCS")])]})])],"derivedFrom":subQ2}),"instanceName":"1"}),"instanceName":"1"}),makeQuery(id+"F19.opPattern","COPY",FACE,{"derivedFrom":makeQuery(id+"F16.opPattern","COPY",FACE,{"derivedFrom":makeQuery(id+"F9.boolean.opBoolean","SPLIT",FACE,{"disambiguationData":[TD([makeQuery(id+"F9.opExtrude","SWEPT_FACE",FACE,{"disambiguationData":[OSD([sQuery(id+"F8.wireOp",EDGE,"E53.MirrorCS")])]})])],"derivedFrom":subQ2}),"instanceName":"1"}),"instanceName":"1"}),makeQuery(id+"F19.opPattern","COPY",FACE,{"derivedFrom":makeQuery(id+"F16.opPattern","COPY",FACE,{"derivedFrom":makeQuery(id+"F9.boolean.opBoolean","SPLIT",FACE,{"disambiguationData":[TD([makeQuery(id+"F9.opExtrude","SWEPT_FACE",FACE,{"disambiguationData":[OSD([sQuery(id+"F8.wireOp",EDGE,"E80")])]})])],"derivedFrom":subQ2}),"instanceName":"1"}),"instanceName":"1"}),makeQuery(id+"F19.opPattern","COPY",FACE,{"derivedFrom":makeQuery(id+"F16.opPattern","COPY",FACE,{"derivedFrom":makeQuery(id+"F9.boolean.opBoolean","SPLIT",FACE,{"disambiguationData":[TD([makeQuery(id+"F9.opExtrude","SWEPT_FACE",FACE,{"disambiguationData":[OSD([sQuery(id+"F8.wireOp",EDGE,"E83")])]})])],"derivedFrom":subQ2}),"instanceName":"1"}),"instanceName":"1"})],"fromTools":[makeQuery(id+"F21.opExtrude","CAP_FACE",FACE,{"disambiguationData":[OSD([sQuery(id+"F20.wireOp",EDGE,"E307.0.0")])],"isStart":false})]}),"instanceName":"1"})});}
            var sketch = newSketch(context, id + "F101", { "sketchPlane" : qUnion([Q0])});
            skLineSegment(sketch, "E1445", {"start": v(52.59, -46.79) * mm, "end": v(49.28, -52.15) * mm});
            skLineSegment(sketch, "E1446", {"start": v(53.88, -47.15) * mm, "end": v(49.63, -54.04) * mm});
            skLineSegment(sketch, "E1447", {"start": v(55.05, -47.8) * mm, "end": v(50.28, -55.54) * mm});
            skLineSegment(sketch, "E1448", {"start": v(56.05, -48.7) * mm, "end": v(51.15, -56.63) * mm});
            skLineSegment(sketch, "E1449", {"start": v(57, -49.63) * mm, "end": v(51.95, -57.83) * mm});
            skLineSegment(sketch, "E1450.0", {"start": v(52.38, -46.66) * mm, "end": v(49.07, -52.02) * mm});
            skLineSegment(sketch, "E1451.0", {"start": v(52.8, -46.92) * mm, "end": v(49.5, -52.28) * mm});
            skLineSegment(sketch, "E1452.0", {"start": v(53.67, -47.02) * mm, "end": v(49.41, -53.91) * mm});
            skLineSegment(sketch, "E1453.0", {"start": v(54.1, -47.28) * mm, "end": v(49.84, -54.17) * mm});
            skLineSegment(sketch, "E1454.0", {"start": v(54.84, -47.67) * mm, "end": v(50.06, -55.4) * mm});
            skLineSegment(sketch, "E1455.0", {"start": v(55.26, -47.93) * mm, "end": v(50.49, -55.67) * mm});
            skLineSegment(sketch, "E1456.0", {"start": v(55.83, -48.56) * mm, "end": v(50.93, -56.5) * mm});
            skLineSegment(sketch, "E1457.0", {"start": v(56.26, -48.83) * mm, "end": v(51.36, -56.77) * mm});
            skLineSegment(sketch, "E1458.0", {"start": v(56.79, -49.5) * mm, "end": v(51.73, -57.7) * mm});
            skLineSegment(sketch, "E1459.0", {"start": v(57.22, -49.76) * mm, "end": v(52.16, -57.96) * mm});
            skArc(sketch, "E1460.0", {"start": v(50.84, -46.11) * mm, "mid": v(49.96, -51.54) * mm, "end": v(51.57, -56.8) * mm});
            skArc(sketch, "E1461", {"start": v(50.84, -46.11) * mm, "mid": v(50.02, -52.15) * mm, "end": v(52.24, -57.82) * mm});
            skLineSegment(sketch, "E1462", {"start": v(52.38, -46.66) * mm, "end": v(52.8, -46.92) * mm});
            skLineSegment(sketch, "E1463", {"start": v(53.67, -47.02) * mm, "end": v(54.1, -47.28) * mm});
            skLineSegment(sketch, "E1464", {"start": v(54.84, -47.67) * mm, "end": v(55.26, -47.93) * mm});
            skLineSegment(sketch, "E1465", {"start": v(55.83, -48.56) * mm, "end": v(56.26, -48.83) * mm});
            skLineSegment(sketch, "E1466", {"start": v(56.79, -49.5) * mm, "end": v(57.22, -49.76) * mm});
            skSolve(sketch);
        }
        {
            var Q0;
            Q0 = qSketchRegion(id + "F101", true);
            var Q1;
            {var subQ0=sQuery(id+"F80.wireOp",EDGE,"E1142.MirrorCS");var subQ1=sQuery(id+"F80.wireOp",EDGE,"E1141.MirrorCS");var subQ2=sQuery(id+"F80.wireOp",EDGE,"E1140.MirrorCS");var subQ3=sQuery(id+"F80.wireOp",EDGE,"E1139.MirrorCS");var subQ4=sQuery(id+"F80.wireOp",EDGE,"E1138.MirrorCS");var subQ5=sQuery(id+"F80.wireOp",EDGE,"E1137.MirrorCS");var subQ6=sQuery(id+"F80.wireOp",EDGE,"E1135.MirrorCS");var subQ7=sQuery(id+"F80.wireOp",EDGE,"E1134.MirrorCS");var subQ8=sQuery(id+"F76.wireOp",EDGE,"E1063");var subQ9=makeQuery(id+"F77.opExtrude","SWEPT_FACE",FACE,{"disambiguationData":[OSD([subQ8])]});var subQ10=sQuery(id+"F80.wireOp",EDGE,"E1136.MirrorCS");var subQ11=sQuery(id+"F80.wireOp",EDGE,"E1143.MirrorCS");var subQ12=sQuery(id+"F80.wireOp",EDGE,"E1144.MirrorCS");var subQ13=sQuery(id+"F80.wireOp",EDGE,"E1145.MirrorCS");var subQ14=sQuery(id+"F80.wireOp",EDGE,"E1146.MirrorCS");var subQ15=sQuery(id+"F80.wireOp",EDGE,"E1148.MirrorC");var subQ16=sQuery(id+"F80.wireOp",EDGE,"E1149.MirrorCS");var subQ17=sQuery(id+"F80.wireOp",EDGE,"E1150.MirrorC");Q1=makeQuery(id+"F83.boolean.opBoolean","MERGE",FACE,{"derivedFrom":[makeQuery(id+"F81.boolean.opBoolean","SPLIT",FACE,{"disambiguationData":[TD([subQ9])],"derivedFrom":makeQuery(id+"F81.opExtrude","CAP_FACE",FACE,{"disambiguationData":[OSD([subQ7,subQ6,subQ10,subQ5,subQ4,subQ3,subQ2,subQ1,subQ0,subQ11,subQ12,subQ13,subQ14,subQ15,subQ16,subQ17])],"isStart":false})}),makeQuery(id+"F83.opExtrude","CAP_FACE",FACE,{"disambiguationData":[OSD([sQuery(id+"F82.wireOp",EDGE,"E1152"),sQuery(id+"F82.wireOp",EDGE,"E1153.0"),sQuery(id+"F82.wireOp",EDGE,"E1154"),sQuery(id+"F82.wireOp",EDGE,"E1155")])],"isStart":false})]});}
            extrude(context, id + "F102", {"entities" : qUnion([Q0]), "operationType" : NewBodyOperationType.ADD, "endBound" : BoundingType.UP_TO_SURFACE, "depth" : 25.4 * mm, "endBoundEntityFace" : qUnion([Q1]), "offsetDistance" : 25.4 * mm});
        }
        {
            var Q0;
            Q0=makeQuery(id+"F100.opExtrude","CAP_FACE",FACE,{"disambiguationData":[OSD([sQuery(id+"F99.wireOp",EDGE,"E1401")])],"isStart":false});
            var sketch = newSketch(context, id + "F103", { "sketchPlane" : qUnion([Q0])});
            skCircle(sketch, "E1467", {"center": v(50.97, -44.07) * mm, "radius": 0.67 * mm});
            skLineSegment(sketch, "E1468.bottom", {"start": v(54.19, -44.33) * mm, "end": v(47.76, -44.33) * mm});
            skLineSegment(sketch, "E1468.top", {"start": v(54.19, -43.8) * mm, "end": v(47.76, -43.8) * mm});
            skArc(sketch, "E1469.0", {"start": v(49.5, -43.8) * mm, "mid": v(49.47, -44.07) * mm, "end": v(49.5, -44.33) * mm});
            skArc(sketch, "E1470.trimOffspring", {"start": v(52.45, -44.33) * mm, "mid": v(52.48, -44.07) * mm, "end": v(52.45, -43.8) * mm});
            skSolve(sketch);
        }
        {
            var Q0;
            Q0 = qSketchRegion(id + "F103", true);
            var Q1;
            {var subQ0=sQuery(id+"F4.wireOp",EDGE,"E8");var subQ1=makeQuery(id+"F5.boolean.opBoolean","COPY",FACE,{"derivedFrom":makeQuery(id+"F5.opExtrude","SWEPT_FACE",FACE,{"disambiguationData":[OSD([subQ0])]})});var subQ2=makeQuery(id+"F5.boolean.opBoolean","COPY",FACE,{"derivedFrom":makeQuery(id+"F5.opExtrude","CAP_FACE",FACE,{"disambiguationData":[OSD([subQ0])],"isStart":false})});Q1=makeQuery(id+"F100.boolean.opBoolean","SPLIT",FACE,{"disambiguationData":[TD([makeQuery(id+"F39.opPattern","COPY",FACE,{"derivedFrom":makeQuery(id+"F19.opPattern","COPY",FACE,{"derivedFrom":makeQuery(id+"F16.opPattern","COPY",FACE,{"derivedFrom":subQ1,"instanceName":"1"}),"instanceName":"1"}),"instanceName":"1"})])],"derivedFrom":makeQuery(id+"F39.opPattern","COPY",FACE,{"derivedFrom":makeQuery(id+"F21.boolean.opBoolean","MERGE",FACE,{"derivedFrom":[makeQuery(id+"F19.opPattern","COPY",FACE,{"derivedFrom":makeQuery(id+"F16.opPattern","COPY",FACE,{"derivedFrom":makeQuery(id+"F9.boolean.opBoolean","SPLIT",FACE,{"disambiguationData":[TD([subQ1])],"derivedFrom":subQ2}),"instanceName":"1"}),"instanceName":"1"}),makeQuery(id+"F19.opPattern","COPY",FACE,{"derivedFrom":makeQuery(id+"F16.opPattern","COPY",FACE,{"derivedFrom":makeQuery(id+"F9.boolean.opBoolean","SPLIT",FACE,{"disambiguationData":[TD([makeQuery(id+"F9.opExtrude","SWEPT_FACE",FACE,{"disambiguationData":[OSD([sQuery(id+"F8.wireOp",EDGE,"E25")])]})])],"derivedFrom":subQ2}),"instanceName":"1"}),"instanceName":"1"}),makeQuery(id+"F19.opPattern","COPY",FACE,{"derivedFrom":makeQuery(id+"F16.opPattern","COPY",FACE,{"derivedFrom":makeQuery(id+"F9.boolean.opBoolean","SPLIT",FACE,{"disambiguationData":[TD([makeQuery(id+"F9.opExtrude","SWEPT_FACE",FACE,{"disambiguationData":[OSD([sQuery(id+"F8.wireOp",EDGE,"E32")])]})])],"derivedFrom":subQ2}),"instanceName":"1"}),"instanceName":"1"}),makeQuery(id+"F19.opPattern","COPY",FACE,{"derivedFrom":makeQuery(id+"F16.opPattern","COPY",FACE,{"derivedFrom":makeQuery(id+"F9.boolean.opBoolean","SPLIT",FACE,{"disambiguationData":[TD([makeQuery(id+"F9.opExtrude","SWEPT_FACE",FACE,{"disambiguationData":[OSD([sQuery(id+"F8.wireOp",EDGE,"E33.0")])]})])],"derivedFrom":subQ2}),"instanceName":"1"}),"instanceName":"1"}),makeQuery(id+"F19.opPattern","COPY",FACE,{"derivedFrom":makeQuery(id+"F16.opPattern","COPY",FACE,{"derivedFrom":makeQuery(id+"F9.boolean.opBoolean","SPLIT",FACE,{"disambiguationData":[TD([makeQuery(id+"F9.opExtrude","SWEPT_FACE",FACE,{"disambiguationData":[OSD([sQuery(id+"F8.wireOp",EDGE,"E37")])]})])],"derivedFrom":subQ2}),"instanceName":"1"}),"instanceName":"1"}),makeQuery(id+"F19.opPattern","COPY",FACE,{"derivedFrom":makeQuery(id+"F16.opPattern","COPY",FACE,{"derivedFrom":makeQuery(id+"F9.boolean.opBoolean","SPLIT",FACE,{"disambiguationData":[TD([makeQuery(id+"F9.opExtrude","SWEPT_FACE",FACE,{"disambiguationData":[OSD([sQuery(id+"F8.wireOp",EDGE,"E51.MirrorCS")])]})])],"derivedFrom":subQ2}),"instanceName":"1"}),"instanceName":"1"}),makeQuery(id+"F19.opPattern","COPY",FACE,{"derivedFrom":makeQuery(id+"F16.opPattern","COPY",FACE,{"derivedFrom":makeQuery(id+"F9.boolean.opBoolean","SPLIT",FACE,{"disambiguationData":[TD([makeQuery(id+"F9.opExtrude","SWEPT_FACE",FACE,{"disambiguationData":[OSD([sQuery(id+"F8.wireOp",EDGE,"E53.MirrorCS")])]})])],"derivedFrom":subQ2}),"instanceName":"1"}),"instanceName":"1"}),makeQuery(id+"F19.opPattern","COPY",FACE,{"derivedFrom":makeQuery(id+"F16.opPattern","COPY",FACE,{"derivedFrom":makeQuery(id+"F9.boolean.opBoolean","SPLIT",FACE,{"disambiguationData":[TD([makeQuery(id+"F9.opExtrude","SWEPT_FACE",FACE,{"disambiguationData":[OSD([sQuery(id+"F8.wireOp",EDGE,"E80")])]})])],"derivedFrom":subQ2}),"instanceName":"1"}),"instanceName":"1"}),makeQuery(id+"F19.opPattern","COPY",FACE,{"derivedFrom":makeQuery(id+"F16.opPattern","COPY",FACE,{"derivedFrom":makeQuery(id+"F9.boolean.opBoolean","SPLIT",FACE,{"disambiguationData":[TD([makeQuery(id+"F9.opExtrude","SWEPT_FACE",FACE,{"disambiguationData":[OSD([sQuery(id+"F8.wireOp",EDGE,"E83")])]})])],"derivedFrom":subQ2}),"instanceName":"1"}),"instanceName":"1"})],"fromTools":[makeQuery(id+"F21.opExtrude","CAP_FACE",FACE,{"disambiguationData":[OSD([sQuery(id+"F20.wireOp",EDGE,"E307.0.0")])],"isStart":false})]}),"instanceName":"1"})});}
            extrude(context, id + "F104", {"entities" : qUnion([Q0]), "operationType" : NewBodyOperationType.REMOVE, "endBound" : BoundingType.UP_TO_SURFACE, "oppositeDirection" : true, "depth" : 25.4 * mm, "endBoundEntityFace" : qUnion([Q1]), "offsetDistance" : 25.4 * mm});
        }
        {
            var Q0;
            {var subQ0=sQuery(id+"F4.wireOp",EDGE,"E8");var subQ1=makeQuery(id+"F5.boolean.opBoolean","COPY",FACE,{"derivedFrom":makeQuery(id+"F5.opExtrude","SWEPT_FACE",FACE,{"disambiguationData":[OSD([subQ0])]})});var subQ2=makeQuery(id+"F5.boolean.opBoolean","COPY",FACE,{"derivedFrom":makeQuery(id+"F5.opExtrude","CAP_FACE",FACE,{"disambiguationData":[OSD([subQ0])],"isStart":false})});Q0=makeQuery(id+"F104.boolean.opBoolean","MERGE",FACE,{"derivedFrom":[makeQuery(id+"F100.boolean.opBoolean","SPLIT",FACE,{"disambiguationData":[TD([makeQuery(id+"F39.opPattern","COPY",FACE,{"derivedFrom":makeQuery(id+"F19.opPattern","COPY",FACE,{"derivedFrom":makeQuery(id+"F16.opPattern","COPY",FACE,{"derivedFrom":subQ1,"instanceName":"1"}),"instanceName":"1"}),"instanceName":"1"})])],"derivedFrom":makeQuery(id+"F39.opPattern","COPY",FACE,{"derivedFrom":makeQuery(id+"F21.boolean.opBoolean","MERGE",FACE,{"derivedFrom":[makeQuery(id+"F19.opPattern","COPY",FACE,{"derivedFrom":makeQuery(id+"F16.opPattern","COPY",FACE,{"derivedFrom":makeQuery(id+"F9.boolean.opBoolean","SPLIT",FACE,{"disambiguationData":[TD([subQ1])],"derivedFrom":subQ2}),"instanceName":"1"}),"instanceName":"1"}),makeQuery(id+"F19.opPattern","COPY",FACE,{"derivedFrom":makeQuery(id+"F16.opPattern","COPY",FACE,{"derivedFrom":makeQuery(id+"F9.boolean.opBoolean","SPLIT",FACE,{"disambiguationData":[TD([makeQuery(id+"F9.opExtrude","SWEPT_FACE",FACE,{"disambiguationData":[OSD([sQuery(id+"F8.wireOp",EDGE,"E25")])]})])],"derivedFrom":subQ2}),"instanceName":"1"}),"instanceName":"1"}),makeQuery(id+"F19.opPattern","COPY",FACE,{"derivedFrom":makeQuery(id+"F16.opPattern","COPY",FACE,{"derivedFrom":makeQuery(id+"F9.boolean.opBoolean","SPLIT",FACE,{"disambiguationData":[TD([makeQuery(id+"F9.opExtrude","SWEPT_FACE",FACE,{"disambiguationData":[OSD([sQuery(id+"F8.wireOp",EDGE,"E32")])]})])],"derivedFrom":subQ2}),"instanceName":"1"}),"instanceName":"1"}),makeQuery(id+"F19.opPattern","COPY",FACE,{"derivedFrom":makeQuery(id+"F16.opPattern","COPY",FACE,{"derivedFrom":makeQuery(id+"F9.boolean.opBoolean","SPLIT",FACE,{"disambiguationData":[TD([makeQuery(id+"F9.opExtrude","SWEPT_FACE",FACE,{"disambiguationData":[OSD([sQuery(id+"F8.wireOp",EDGE,"E33.0")])]})])],"derivedFrom":subQ2}),"instanceName":"1"}),"instanceName":"1"}),makeQuery(id+"F19.opPattern","COPY",FACE,{"derivedFrom":makeQuery(id+"F16.opPattern","COPY",FACE,{"derivedFrom":makeQuery(id+"F9.boolean.opBoolean","SPLIT",FACE,{"disambiguationData":[TD([makeQuery(id+"F9.opExtrude","SWEPT_FACE",FACE,{"disambiguationData":[OSD([sQuery(id+"F8.wireOp",EDGE,"E37")])]})])],"derivedFrom":subQ2}),"instanceName":"1"}),"instanceName":"1"}),makeQuery(id+"F19.opPattern","COPY",FACE,{"derivedFrom":makeQuery(id+"F16.opPattern","COPY",FACE,{"derivedFrom":makeQuery(id+"F9.boolean.opBoolean","SPLIT",FACE,{"disambiguationData":[TD([makeQuery(id+"F9.opExtrude","SWEPT_FACE",FACE,{"disambiguationData":[OSD([sQuery(id+"F8.wireOp",EDGE,"E51.MirrorCS")])]})])],"derivedFrom":subQ2}),"instanceName":"1"}),"instanceName":"1"}),makeQuery(id+"F19.opPattern","COPY",FACE,{"derivedFrom":makeQuery(id+"F16.opPattern","COPY",FACE,{"derivedFrom":makeQuery(id+"F9.boolean.opBoolean","SPLIT",FACE,{"disambiguationData":[TD([makeQuery(id+"F9.opExtrude","SWEPT_FACE",FACE,{"disambiguationData":[OSD([sQuery(id+"F8.wireOp",EDGE,"E53.MirrorCS")])]})])],"derivedFrom":subQ2}),"instanceName":"1"}),"instanceName":"1"}),makeQuery(id+"F19.opPattern","COPY",FACE,{"derivedFrom":makeQuery(id+"F16.opPattern","COPY",FACE,{"derivedFrom":makeQuery(id+"F9.boolean.opBoolean","SPLIT",FACE,{"disambiguationData":[TD([makeQuery(id+"F9.opExtrude","SWEPT_FACE",FACE,{"disambiguationData":[OSD([sQuery(id+"F8.wireOp",EDGE,"E80")])]})])],"derivedFrom":subQ2}),"instanceName":"1"}),"instanceName":"1"}),makeQuery(id+"F19.opPattern","COPY",FACE,{"derivedFrom":makeQuery(id+"F16.opPattern","COPY",FACE,{"derivedFrom":makeQuery(id+"F9.boolean.opBoolean","SPLIT",FACE,{"disambiguationData":[TD([makeQuery(id+"F9.opExtrude","SWEPT_FACE",FACE,{"disambiguationData":[OSD([sQuery(id+"F8.wireOp",EDGE,"E83")])]})])],"derivedFrom":subQ2}),"instanceName":"1"}),"instanceName":"1"})],"fromTools":[makeQuery(id+"F21.opExtrude","CAP_FACE",FACE,{"disambiguationData":[OSD([sQuery(id+"F20.wireOp",EDGE,"E307.0.0")])],"isStart":false})]}),"instanceName":"1"})})],"fromTools":[makeQuery(id+"F104.opExtrude","CAP_FACE",FACE,{"disambiguationData":[OSD([sQuery(id+"F103.wireOp",EDGE,"E1467"),sQuery(id+"F103.wireOp",EDGE,"E1468.bottom"),sQuery(id+"F103.wireOp",EDGE,"E1468.top"),sQuery(id+"F103.wireOp",EDGE,"E1469.0"),sQuery(id+"F103.wireOp",EDGE,"E1470.trimOffspring")])],"isStart":false})]});}
            var sketch = newSketch(context, id + "F105", { "sketchPlane" : qUnion([Q0])});
            skCircle(sketch, "E1471", {"center": v(51.46, -58.7) * mm, "radius": 0.77 * mm});
            skSolve(sketch);
        }
        {
            var Q0;
            Q0 = qSketchRegion(id + "F105", true);
            var Q1;
            Q1=makeQuery(id+"F100.opExtrude","CAP_FACE",FACE,{"disambiguationData":[OSD([sQuery(id+"F99.wireOp",EDGE,"E1397"),sQuery(id+"F99.wireOp",EDGE,"E1415.0"),sQuery(id+"F99.wireOp",EDGE,"E1416"),sQuery(id+"F99.wireOp",EDGE,"E1417"),sQuery(id+"F99.wireOp",EDGE,"E1418.MirrorC"),sQuery(id+"F99.wireOp",EDGE,"E1419.MirrorC"),sQuery(id+"F99.wireOp",EDGE,"E1420"),sQuery(id+"F99.wireOp",EDGE,"E1421.0"),sQuery(id+"F99.wireOp",EDGE,"E1422.trimOffspring"),sQuery(id+"F99.wireOp",EDGE,"E1423.trimOffspring"),sQuery(id+"F99.wireOp",EDGE,"E1424.trimOffspring"),sQuery(id+"F99.wireOp",EDGE,"E1425.trimOffspring"),sQuery(id+"F99.wireOp",EDGE,"E1426.trimOffspring"),sQuery(id+"F99.wireOp",EDGE,"E1427.trimOffspring"),sQuery(id+"F99.wireOp",EDGE,"E1428.trimOffspring"),sQuery(id+"F99.wireOp",EDGE,"E1429.trimOffspring"),sQuery(id+"F99.wireOp",EDGE,"E1430.trimOffspring"),sQuery(id+"F99.wireOp",EDGE,"E1431.trimOffspring"),sQuery(id+"F99.wireOp",EDGE,"E1432.trimOffspring"),sQuery(id+"F99.wireOp",EDGE,"E1435.trimOffspring"),sQuery(id+"F99.wireOp",EDGE,"E1442.trimOffspring"),sQuery(id+"F99.wireOp",EDGE,"E1443.trimOffspring"),sQuery(id+"F99.wireOp",EDGE,"E1444.trimOffspring")])],"isStart":false});
            extrude(context, id + "F106", {"entities" : qUnion([Q0]), "operationType" : NewBodyOperationType.ADD, "endBound" : BoundingType.UP_TO_SURFACE, "depth" : 25.4 * mm, "endBoundEntityFace" : qUnion([Q1]), "offsetDistance" : 25.4 * mm});
        }
        {
            var Q0;
            {var subQ0=sQuery(id+"F4.wireOp",EDGE,"E8");var subQ1=makeQuery(id+"F5.boolean.opBoolean","COPY",FACE,{"derivedFrom":makeQuery(id+"F5.opExtrude","SWEPT_FACE",FACE,{"disambiguationData":[OSD([subQ0])]})});var subQ2=makeQuery(id+"F5.boolean.opBoolean","COPY",FACE,{"derivedFrom":makeQuery(id+"F5.opExtrude","CAP_FACE",FACE,{"disambiguationData":[OSD([subQ0])],"isStart":false})});Q0=makeQuery(id+"F104.boolean.opBoolean","MERGE",FACE,{"derivedFrom":[makeQuery(id+"F100.boolean.opBoolean","SPLIT",FACE,{"disambiguationData":[TD([makeQuery(id+"F39.opPattern","COPY",FACE,{"derivedFrom":makeQuery(id+"F19.opPattern","COPY",FACE,{"derivedFrom":makeQuery(id+"F16.opPattern","COPY",FACE,{"derivedFrom":subQ1,"instanceName":"1"}),"instanceName":"1"}),"instanceName":"1"})])],"derivedFrom":makeQuery(id+"F39.opPattern","COPY",FACE,{"derivedFrom":makeQuery(id+"F21.boolean.opBoolean","MERGE",FACE,{"derivedFrom":[makeQuery(id+"F19.opPattern","COPY",FACE,{"derivedFrom":makeQuery(id+"F16.opPattern","COPY",FACE,{"derivedFrom":makeQuery(id+"F9.boolean.opBoolean","SPLIT",FACE,{"disambiguationData":[TD([subQ1])],"derivedFrom":subQ2}),"instanceName":"1"}),"instanceName":"1"}),makeQuery(id+"F19.opPattern","COPY",FACE,{"derivedFrom":makeQuery(id+"F16.opPattern","COPY",FACE,{"derivedFrom":makeQuery(id+"F9.boolean.opBoolean","SPLIT",FACE,{"disambiguationData":[TD([makeQuery(id+"F9.opExtrude","SWEPT_FACE",FACE,{"disambiguationData":[OSD([sQuery(id+"F8.wireOp",EDGE,"E25")])]})])],"derivedFrom":subQ2}),"instanceName":"1"}),"instanceName":"1"}),makeQuery(id+"F19.opPattern","COPY",FACE,{"derivedFrom":makeQuery(id+"F16.opPattern","COPY",FACE,{"derivedFrom":makeQuery(id+"F9.boolean.opBoolean","SPLIT",FACE,{"disambiguationData":[TD([makeQuery(id+"F9.opExtrude","SWEPT_FACE",FACE,{"disambiguationData":[OSD([sQuery(id+"F8.wireOp",EDGE,"E32")])]})])],"derivedFrom":subQ2}),"instanceName":"1"}),"instanceName":"1"}),makeQuery(id+"F19.opPattern","COPY",FACE,{"derivedFrom":makeQuery(id+"F16.opPattern","COPY",FACE,{"derivedFrom":makeQuery(id+"F9.boolean.opBoolean","SPLIT",FACE,{"disambiguationData":[TD([makeQuery(id+"F9.opExtrude","SWEPT_FACE",FACE,{"disambiguationData":[OSD([sQuery(id+"F8.wireOp",EDGE,"E33.0")])]})])],"derivedFrom":subQ2}),"instanceName":"1"}),"instanceName":"1"}),makeQuery(id+"F19.opPattern","COPY",FACE,{"derivedFrom":makeQuery(id+"F16.opPattern","COPY",FACE,{"derivedFrom":makeQuery(id+"F9.boolean.opBoolean","SPLIT",FACE,{"disambiguationData":[TD([makeQuery(id+"F9.opExtrude","SWEPT_FACE",FACE,{"disambiguationData":[OSD([sQuery(id+"F8.wireOp",EDGE,"E37")])]})])],"derivedFrom":subQ2}),"instanceName":"1"}),"instanceName":"1"}),makeQuery(id+"F19.opPattern","COPY",FACE,{"derivedFrom":makeQuery(id+"F16.opPattern","COPY",FACE,{"derivedFrom":makeQuery(id+"F9.boolean.opBoolean","SPLIT",FACE,{"disambiguationData":[TD([makeQuery(id+"F9.opExtrude","SWEPT_FACE",FACE,{"disambiguationData":[OSD([sQuery(id+"F8.wireOp",EDGE,"E51.MirrorCS")])]})])],"derivedFrom":subQ2}),"instanceName":"1"}),"instanceName":"1"}),makeQuery(id+"F19.opPattern","COPY",FACE,{"derivedFrom":makeQuery(id+"F16.opPattern","COPY",FACE,{"derivedFrom":makeQuery(id+"F9.boolean.opBoolean","SPLIT",FACE,{"disambiguationData":[TD([makeQuery(id+"F9.opExtrude","SWEPT_FACE",FACE,{"disambiguationData":[OSD([sQuery(id+"F8.wireOp",EDGE,"E53.MirrorCS")])]})])],"derivedFrom":subQ2}),"instanceName":"1"}),"instanceName":"1"}),makeQuery(id+"F19.opPattern","COPY",FACE,{"derivedFrom":makeQuery(id+"F16.opPattern","COPY",FACE,{"derivedFrom":makeQuery(id+"F9.boolean.opBoolean","SPLIT",FACE,{"disambiguationData":[TD([makeQuery(id+"F9.opExtrude","SWEPT_FACE",FACE,{"disambiguationData":[OSD([sQuery(id+"F8.wireOp",EDGE,"E80")])]})])],"derivedFrom":subQ2}),"instanceName":"1"}),"instanceName":"1"}),makeQuery(id+"F19.opPattern","COPY",FACE,{"derivedFrom":makeQuery(id+"F16.opPattern","COPY",FACE,{"derivedFrom":makeQuery(id+"F9.boolean.opBoolean","SPLIT",FACE,{"disambiguationData":[TD([makeQuery(id+"F9.opExtrude","SWEPT_FACE",FACE,{"disambiguationData":[OSD([sQuery(id+"F8.wireOp",EDGE,"E83")])]})])],"derivedFrom":subQ2}),"instanceName":"1"}),"instanceName":"1"})],"fromTools":[makeQuery(id+"F21.opExtrude","CAP_FACE",FACE,{"disambiguationData":[OSD([sQuery(id+"F20.wireOp",EDGE,"E307.0.0")])],"isStart":false})]}),"instanceName":"1"})})],"fromTools":[makeQuery(id+"F104.opExtrude","CAP_FACE",FACE,{"disambiguationData":[OSD([sQuery(id+"F103.wireOp",EDGE,"E1467"),sQuery(id+"F103.wireOp",EDGE,"E1468.bottom"),sQuery(id+"F103.wireOp",EDGE,"E1468.top"),sQuery(id+"F103.wireOp",EDGE,"E1469.0"),sQuery(id+"F103.wireOp",EDGE,"E1470.trimOffspring")])],"isStart":false})]});}
            var sketch = newSketch(context, id + "F107", { "sketchPlane" : qUnion([Q0])});
            skArc(sketch, "E1472.0.0", {"start": v(50.38, -45.92) * mm, "mid": v(49.67, -45.52) * mm, "end": v(49.2, -44.85) * mm});
            skArc(sketch, "E1472.0.1", {"start": v(49.2, -44.85) * mm, "mid": v(48.56, -51.21) * mm, "end": v(51.14, -57.05) * mm});
            skArc(sketch, "E1472.0.2", {"start": v(51.14, -57.05) * mm, "mid": v(49.46, -51.58) * mm, "end": v(50.38, -45.92) * mm});
            skLineSegment(sketch, "E1473.0.0", {"start": v(49.5, -43.8) * mm, "end": v(50.36, -43.8) * mm});
            skArc(sketch, "E1473.0.1", {"start": v(50.36, -43.8) * mm, "mid": v(50.97, -43.4) * mm, "end": v(51.59, -43.8) * mm});
            skLineSegment(sketch, "E1473.0.2", {"start": v(51.59, -43.8) * mm, "end": v(52.45, -43.8) * mm});
            skArc(sketch, "E1473.0.3", {"start": v(52.45, -43.8) * mm, "mid": v(50.97, -42.56) * mm, "end": v(49.5, -43.8) * mm});
            skArc(sketch, "E1474.0.0", {"start": v(51.59, -44.33) * mm, "mid": v(50.97, -44.74) * mm, "end": v(50.36, -44.33) * mm});
            skLineSegment(sketch, "E1474.0.1", {"start": v(50.36, -44.33) * mm, "end": v(49.5, -44.33) * mm});
            skArc(sketch, "E1474.0.2", {"start": v(49.5, -44.33) * mm, "mid": v(50.97, -45.57) * mm, "end": v(52.45, -44.33) * mm});
            skLineSegment(sketch, "E1474.0.3", {"start": v(52.45, -44.33) * mm, "end": v(51.59, -44.33) * mm});
            skArc(sketch, "E1475.0.0", {"start": v(52.58, -46.07) * mm, "mid": v(55.4, -47.01) * mm, "end": v(57.38, -49.23) * mm});
            skArc(sketch, "E1475.0.1", {"start": v(57.38, -49.23) * mm, "mid": v(57.66, -47.98) * mm, "end": v(56.84, -46.99) * mm});
            skArc(sketch, "E1475.0.2", {"start": v(56.84, -46.99) * mm, "mid": v(54.8, -45.64) * mm, "end": v(53.5, -43.58) * mm});
            skArc(sketch, "E1475.0.3", {"start": v(53.5, -43.58) * mm, "mid": v(53.38, -44.95) * mm, "end": v(52.58, -46.07) * mm});
            skFitSpline(sketch, "E1476.0", {"points": [v(49.54, -58.1) * mm, v(49.72, -57.93) * mm, v(49.83, -57.7) * mm, v(49.87, -57.4) * mm, v(49.8, -56.98) * mm, v(49.62, -56.5) * mm, v(49.32, -55.97) * mm, v(48.9, -55.43) * mm, v(48.38, -54.92) * mm, v(47.8, -54.44) * mm, v(47.17, -54.03) * mm, v(46.52, -53.7) * mm, v(45.88, -53.46) * mm, v(45.29, -53.33) * mm, v(44.77, -53.3) * mm, v(44.35, -53.37) * mm, v(44.07, -53.5) * mm, v(43.89, -53.67) * mm, v(43.78, -53.9) * mm, v(43.74, -54.2) * mm, v(43.8, -54.63) * mm, v(43.99, -55.11) * mm, v(44.3, -55.64) * mm, v(44.72, -56.17) * mm, v(45.23, -56.69) * mm, v(45.81, -57.16) * mm, v(46.44, -57.58) * mm, v(47.09, -57.9) * mm, v(47.73, -58.14) * mm, v(48.32, -58.27) * mm, v(48.84, -58.3) * mm, v(49.26, -58.23) * mm, v(49.54, -58.1) * mm, v(49.72, -57.93) * mm, v(49.83, -57.7) * mm, v(49.54, -58.1) * mm]});
            skSolve(sketch);
        }
        {
            var Q0;
            Q0 = qSketchRegion(id + "F107", true);
            extrude(context, id + "F108", {"entities" : qUnion([Q0]), "operationType" : NewBodyOperationType.REMOVE, "depth" : 25.4 * mm, "offsetDistance" : 25.4 * mm});
        }
        {
            var Q0;
            {var subQ0=sQuery(id+"F4.wireOp",EDGE,"E8");var subQ1=makeQuery(id+"F5.boolean.opBoolean","COPY",FACE,{"derivedFrom":makeQuery(id+"F5.opExtrude","SWEPT_FACE",FACE,{"disambiguationData":[OSD([subQ0])]})});var subQ2=makeQuery(id+"F5.boolean.opBoolean","COPY",FACE,{"derivedFrom":makeQuery(id+"F5.opExtrude","CAP_FACE",FACE,{"disambiguationData":[OSD([subQ0])],"isStart":false})});Q0=makeQuery(id+"F108.boolean.opBoolean","MERGE",FACE,{"derivedFrom":[makeQuery(id+"F104.boolean.opBoolean","MERGE",FACE,{"derivedFrom":[makeQuery(id+"F100.boolean.opBoolean","SPLIT",FACE,{"disambiguationData":[TD([makeQuery(id+"F39.opPattern","COPY",FACE,{"derivedFrom":makeQuery(id+"F19.opPattern","COPY",FACE,{"derivedFrom":makeQuery(id+"F16.opPattern","COPY",FACE,{"derivedFrom":subQ1,"instanceName":"1"}),"instanceName":"1"}),"instanceName":"1"})])],"derivedFrom":makeQuery(id+"F39.opPattern","COPY",FACE,{"derivedFrom":makeQuery(id+"F21.boolean.opBoolean","MERGE",FACE,{"derivedFrom":[makeQuery(id+"F19.opPattern","COPY",FACE,{"derivedFrom":makeQuery(id+"F16.opPattern","COPY",FACE,{"derivedFrom":makeQuery(id+"F9.boolean.opBoolean","SPLIT",FACE,{"disambiguationData":[TD([subQ1])],"derivedFrom":subQ2}),"instanceName":"1"}),"instanceName":"1"}),makeQuery(id+"F19.opPattern","COPY",FACE,{"derivedFrom":makeQuery(id+"F16.opPattern","COPY",FACE,{"derivedFrom":makeQuery(id+"F9.boolean.opBoolean","SPLIT",FACE,{"disambiguationData":[TD([makeQuery(id+"F9.opExtrude","SWEPT_FACE",FACE,{"disambiguationData":[OSD([sQuery(id+"F8.wireOp",EDGE,"E25")])]})])],"derivedFrom":subQ2}),"instanceName":"1"}),"instanceName":"1"}),makeQuery(id+"F19.opPattern","COPY",FACE,{"derivedFrom":makeQuery(id+"F16.opPattern","COPY",FACE,{"derivedFrom":makeQuery(id+"F9.boolean.opBoolean","SPLIT",FACE,{"disambiguationData":[TD([makeQuery(id+"F9.opExtrude","SWEPT_FACE",FACE,{"disambiguationData":[OSD([sQuery(id+"F8.wireOp",EDGE,"E32")])]})])],"derivedFrom":subQ2}),"instanceName":"1"}),"instanceName":"1"}),makeQuery(id+"F19.opPattern","COPY",FACE,{"derivedFrom":makeQuery(id+"F16.opPattern","COPY",FACE,{"derivedFrom":makeQuery(id+"F9.boolean.opBoolean","SPLIT",FACE,{"disambiguationData":[TD([makeQuery(id+"F9.opExtrude","SWEPT_FACE",FACE,{"disambiguationData":[OSD([sQuery(id+"F8.wireOp",EDGE,"E33.0")])]})])],"derivedFrom":subQ2}),"instanceName":"1"}),"instanceName":"1"}),makeQuery(id+"F19.opPattern","COPY",FACE,{"derivedFrom":makeQuery(id+"F16.opPattern","COPY",FACE,{"derivedFrom":makeQuery(id+"F9.boolean.opBoolean","SPLIT",FACE,{"disambiguationData":[TD([makeQuery(id+"F9.opExtrude","SWEPT_FACE",FACE,{"disambiguationData":[OSD([sQuery(id+"F8.wireOp",EDGE,"E37")])]})])],"derivedFrom":subQ2}),"instanceName":"1"}),"instanceName":"1"}),makeQuery(id+"F19.opPattern","COPY",FACE,{"derivedFrom":makeQuery(id+"F16.opPattern","COPY",FACE,{"derivedFrom":makeQuery(id+"F9.boolean.opBoolean","SPLIT",FACE,{"disambiguationData":[TD([makeQuery(id+"F9.opExtrude","SWEPT_FACE",FACE,{"disambiguationData":[OSD([sQuery(id+"F8.wireOp",EDGE,"E51.MirrorCS")])]})])],"derivedFrom":subQ2}),"instanceName":"1"}),"instanceName":"1"}),makeQuery(id+"F19.opPattern","COPY",FACE,{"derivedFrom":makeQuery(id+"F16.opPattern","COPY",FACE,{"derivedFrom":makeQuery(id+"F9.boolean.opBoolean","SPLIT",FACE,{"disambiguationData":[TD([makeQuery(id+"F9.opExtrude","SWEPT_FACE",FACE,{"disambiguationData":[OSD([sQuery(id+"F8.wireOp",EDGE,"E53.MirrorCS")])]})])],"derivedFrom":subQ2}),"instanceName":"1"}),"instanceName":"1"}),makeQuery(id+"F19.opPattern","COPY",FACE,{"derivedFrom":makeQuery(id+"F16.opPattern","COPY",FACE,{"derivedFrom":makeQuery(id+"F9.boolean.opBoolean","SPLIT",FACE,{"disambiguationData":[TD([makeQuery(id+"F9.opExtrude","SWEPT_FACE",FACE,{"disambiguationData":[OSD([sQuery(id+"F8.wireOp",EDGE,"E80")])]})])],"derivedFrom":subQ2}),"instanceName":"1"}),"instanceName":"1"}),makeQuery(id+"F19.opPattern","COPY",FACE,{"derivedFrom":makeQuery(id+"F16.opPattern","COPY",FACE,{"derivedFrom":makeQuery(id+"F9.boolean.opBoolean","SPLIT",FACE,{"disambiguationData":[TD([makeQuery(id+"F9.opExtrude","SWEPT_FACE",FACE,{"disambiguationData":[OSD([sQuery(id+"F8.wireOp",EDGE,"E83")])]})])],"derivedFrom":subQ2}),"instanceName":"1"}),"instanceName":"1"})],"fromTools":[makeQuery(id+"F21.opExtrude","CAP_FACE",FACE,{"disambiguationData":[OSD([sQuery(id+"F20.wireOp",EDGE,"E307.0.0")])],"isStart":false})]}),"instanceName":"1"})})],"fromTools":[makeQuery(id+"F104.opExtrude","CAP_FACE",FACE,{"disambiguationData":[OSD([sQuery(id+"F103.wireOp",EDGE,"E1467"),sQuery(id+"F103.wireOp",EDGE,"E1468.bottom"),sQuery(id+"F103.wireOp",EDGE,"E1468.top"),sQuery(id+"F103.wireOp",EDGE,"E1469.0"),sQuery(id+"F103.wireOp",EDGE,"E1470.trimOffspring")])],"isStart":false})]})],"fromTools":[makeQuery(id+"F108.opExtrude","CAP_FACE",FACE,{"disambiguationData":[OSD([sQuery(id+"F107.wireOp",EDGE,"E1472.0.0"),sQuery(id+"F107.wireOp",EDGE,"E1472.0.1"),sQuery(id+"F107.wireOp",EDGE,"E1472.0.2")])],"isStart":true}),makeQuery(id+"F108.opExtrude","CAP_FACE",FACE,{"disambiguationData":[OSD([sQuery(id+"F107.wireOp",EDGE,"E1473.0.0"),sQuery(id+"F107.wireOp",EDGE,"E1473.0.1"),sQuery(id+"F107.wireOp",EDGE,"E1473.0.2"),sQuery(id+"F107.wireOp",EDGE,"E1473.0.3")])],"isStart":true}),makeQuery(id+"F108.opExtrude","CAP_FACE",FACE,{"disambiguationData":[OSD([sQuery(id+"F107.wireOp",EDGE,"E1474.0.0"),sQuery(id+"F107.wireOp",EDGE,"E1474.0.1"),sQuery(id+"F107.wireOp",EDGE,"E1474.0.2"),sQuery(id+"F107.wireOp",EDGE,"E1474.0.3")])],"isStart":true}),makeQuery(id+"F108.opExtrude","CAP_FACE",FACE,{"disambiguationData":[OSD([sQuery(id+"F107.wireOp",EDGE,"E1475.0.0"),sQuery(id+"F107.wireOp",EDGE,"E1475.0.1"),sQuery(id+"F107.wireOp",EDGE,"E1475.0.2"),sQuery(id+"F107.wireOp",EDGE,"E1475.0.3")])],"isStart":true})]});}
            var sketch = newSketch(context, id + "F109", { "sketchPlane" : qUnion([Q0])});
            skArc(sketch, "E1477.0", {"start": v(49.93, -50.62) * mm, "mid": v(49.94, -51.07) * mm, "end": v(49.96, -51.53) * mm});
            skArc(sketch, "E1478", {"start": v(50.29, -44.71) * mm, "mid": v(49.46, -51.33) * mm, "end": v(51.65, -57.64) * mm});
            skArc(sketch, "E1479", {"start": v(48.42, -46.1) * mm, "mid": v(48.55, -52.29) * mm, "end": v(51.65, -57.64) * mm});
            skArc(sketch, "E1480", {"start": v(58.2, -49.49) * mm, "mid": v(54.74, -46.28) * mm, "end": v(50.29, -44.71) * mm});
            skArc(sketch, "E1481", {"start": v(58.2, -49.49) * mm, "mid": v(57.5, -46.82) * mm, "end": v(55.32, -45.15) * mm});
            skLineSegment(sketch, "E1482", {"start": v(48.42, -46.1) * mm, "end": v(49.44, -41.72) * mm});
            skArc(sketch, "E1483", {"start": v(49.44, -41.72) * mm, "mid": v(52.05, -44) * mm, "end": v(55.32, -45.15) * mm});
            skCircle(sketch, "E1484", {"center": v(51.15, -46.49) * mm, "radius": 0.36 * mm});
            skSolve(sketch);
        }
        {
            var Q0;
            Q0 = qSketchRegion(id + "F109", true);
            var Q1;
            Q1=makeQuery(id+"F100.opExtrude","CAP_FACE",FACE,{"disambiguationData":[OSD([sQuery(id+"F99.wireOp",EDGE,"E1397"),sQuery(id+"F99.wireOp",EDGE,"E1415.0"),sQuery(id+"F99.wireOp",EDGE,"E1416"),sQuery(id+"F99.wireOp",EDGE,"E1417"),sQuery(id+"F99.wireOp",EDGE,"E1418.MirrorC"),sQuery(id+"F99.wireOp",EDGE,"E1419.MirrorC"),sQuery(id+"F99.wireOp",EDGE,"E1420"),sQuery(id+"F99.wireOp",EDGE,"E1421.0"),sQuery(id+"F99.wireOp",EDGE,"E1422.trimOffspring"),sQuery(id+"F99.wireOp",EDGE,"E1423.trimOffspring"),sQuery(id+"F99.wireOp",EDGE,"E1424.trimOffspring"),sQuery(id+"F99.wireOp",EDGE,"E1425.trimOffspring"),sQuery(id+"F99.wireOp",EDGE,"E1426.trimOffspring"),sQuery(id+"F99.wireOp",EDGE,"E1427.trimOffspring"),sQuery(id+"F99.wireOp",EDGE,"E1428.trimOffspring"),sQuery(id+"F99.wireOp",EDGE,"E1429.trimOffspring"),sQuery(id+"F99.wireOp",EDGE,"E1430.trimOffspring"),sQuery(id+"F99.wireOp",EDGE,"E1431.trimOffspring"),sQuery(id+"F99.wireOp",EDGE,"E1432.trimOffspring"),sQuery(id+"F99.wireOp",EDGE,"E1435.trimOffspring"),sQuery(id+"F99.wireOp",EDGE,"E1442.trimOffspring"),sQuery(id+"F99.wireOp",EDGE,"E1443.trimOffspring"),sQuery(id+"F99.wireOp",EDGE,"E1444.trimOffspring")])],"isStart":false});
            extrude(context, id + "F110", {"entities" : qUnion([Q0]), "operationType" : NewBodyOperationType.ADD, "endBound" : BoundingType.UP_TO_SURFACE, "depth" : 25.4 * mm, "endBoundEntityFace" : qUnion([Q1]), "offsetDistance" : 25.4 * mm});
        }
        {
            var Q0;
            {var subQ0=sQuery(id+"F4.wireOp",EDGE,"E8");var subQ1=makeQuery(id+"F5.boolean.opBoolean","COPY",FACE,{"derivedFrom":makeQuery(id+"F5.opExtrude","SWEPT_FACE",FACE,{"disambiguationData":[OSD([subQ0])]})});var subQ2=makeQuery(id+"F5.boolean.opBoolean","COPY",FACE,{"derivedFrom":makeQuery(id+"F5.opExtrude","CAP_FACE",FACE,{"disambiguationData":[OSD([subQ0])],"isStart":false})});Q0=makeQuery(id+"F108.boolean.opBoolean","MERGE",FACE,{"derivedFrom":[makeQuery(id+"F104.boolean.opBoolean","MERGE",FACE,{"derivedFrom":[makeQuery(id+"F100.boolean.opBoolean","SPLIT",FACE,{"disambiguationData":[TD([makeQuery(id+"F39.opPattern","COPY",FACE,{"derivedFrom":makeQuery(id+"F19.opPattern","COPY",FACE,{"derivedFrom":makeQuery(id+"F16.opPattern","COPY",FACE,{"derivedFrom":subQ1,"instanceName":"1"}),"instanceName":"1"}),"instanceName":"1"})])],"derivedFrom":makeQuery(id+"F39.opPattern","COPY",FACE,{"derivedFrom":makeQuery(id+"F21.boolean.opBoolean","MERGE",FACE,{"derivedFrom":[makeQuery(id+"F19.opPattern","COPY",FACE,{"derivedFrom":makeQuery(id+"F16.opPattern","COPY",FACE,{"derivedFrom":makeQuery(id+"F9.boolean.opBoolean","SPLIT",FACE,{"disambiguationData":[TD([subQ1])],"derivedFrom":subQ2}),"instanceName":"1"}),"instanceName":"1"}),makeQuery(id+"F19.opPattern","COPY",FACE,{"derivedFrom":makeQuery(id+"F16.opPattern","COPY",FACE,{"derivedFrom":makeQuery(id+"F9.boolean.opBoolean","SPLIT",FACE,{"disambiguationData":[TD([makeQuery(id+"F9.opExtrude","SWEPT_FACE",FACE,{"disambiguationData":[OSD([sQuery(id+"F8.wireOp",EDGE,"E25")])]})])],"derivedFrom":subQ2}),"instanceName":"1"}),"instanceName":"1"}),makeQuery(id+"F19.opPattern","COPY",FACE,{"derivedFrom":makeQuery(id+"F16.opPattern","COPY",FACE,{"derivedFrom":makeQuery(id+"F9.boolean.opBoolean","SPLIT",FACE,{"disambiguationData":[TD([makeQuery(id+"F9.opExtrude","SWEPT_FACE",FACE,{"disambiguationData":[OSD([sQuery(id+"F8.wireOp",EDGE,"E32")])]})])],"derivedFrom":subQ2}),"instanceName":"1"}),"instanceName":"1"}),makeQuery(id+"F19.opPattern","COPY",FACE,{"derivedFrom":makeQuery(id+"F16.opPattern","COPY",FACE,{"derivedFrom":makeQuery(id+"F9.boolean.opBoolean","SPLIT",FACE,{"disambiguationData":[TD([makeQuery(id+"F9.opExtrude","SWEPT_FACE",FACE,{"disambiguationData":[OSD([sQuery(id+"F8.wireOp",EDGE,"E33.0")])]})])],"derivedFrom":subQ2}),"instanceName":"1"}),"instanceName":"1"}),makeQuery(id+"F19.opPattern","COPY",FACE,{"derivedFrom":makeQuery(id+"F16.opPattern","COPY",FACE,{"derivedFrom":makeQuery(id+"F9.boolean.opBoolean","SPLIT",FACE,{"disambiguationData":[TD([makeQuery(id+"F9.opExtrude","SWEPT_FACE",FACE,{"disambiguationData":[OSD([sQuery(id+"F8.wireOp",EDGE,"E37")])]})])],"derivedFrom":subQ2}),"instanceName":"1"}),"instanceName":"1"}),makeQuery(id+"F19.opPattern","COPY",FACE,{"derivedFrom":makeQuery(id+"F16.opPattern","COPY",FACE,{"derivedFrom":makeQuery(id+"F9.boolean.opBoolean","SPLIT",FACE,{"disambiguationData":[TD([makeQuery(id+"F9.opExtrude","SWEPT_FACE",FACE,{"disambiguationData":[OSD([sQuery(id+"F8.wireOp",EDGE,"E51.MirrorCS")])]})])],"derivedFrom":subQ2}),"instanceName":"1"}),"instanceName":"1"}),makeQuery(id+"F19.opPattern","COPY",FACE,{"derivedFrom":makeQuery(id+"F16.opPattern","COPY",FACE,{"derivedFrom":makeQuery(id+"F9.boolean.opBoolean","SPLIT",FACE,{"disambiguationData":[TD([makeQuery(id+"F9.opExtrude","SWEPT_FACE",FACE,{"disambiguationData":[OSD([sQuery(id+"F8.wireOp",EDGE,"E53.MirrorCS")])]})])],"derivedFrom":subQ2}),"instanceName":"1"}),"instanceName":"1"}),makeQuery(id+"F19.opPattern","COPY",FACE,{"derivedFrom":makeQuery(id+"F16.opPattern","COPY",FACE,{"derivedFrom":makeQuery(id+"F9.boolean.opBoolean","SPLIT",FACE,{"disambiguationData":[TD([makeQuery(id+"F9.opExtrude","SWEPT_FACE",FACE,{"disambiguationData":[OSD([sQuery(id+"F8.wireOp",EDGE,"E80")])]})])],"derivedFrom":subQ2}),"instanceName":"1"}),"instanceName":"1"}),makeQuery(id+"F19.opPattern","COPY",FACE,{"derivedFrom":makeQuery(id+"F16.opPattern","COPY",FACE,{"derivedFrom":makeQuery(id+"F9.boolean.opBoolean","SPLIT",FACE,{"disambiguationData":[TD([makeQuery(id+"F9.opExtrude","SWEPT_FACE",FACE,{"disambiguationData":[OSD([sQuery(id+"F8.wireOp",EDGE,"E83")])]})])],"derivedFrom":subQ2}),"instanceName":"1"}),"instanceName":"1"})],"fromTools":[makeQuery(id+"F21.opExtrude","CAP_FACE",FACE,{"disambiguationData":[OSD([sQuery(id+"F20.wireOp",EDGE,"E307.0.0")])],"isStart":false})]}),"instanceName":"1"})})],"fromTools":[makeQuery(id+"F104.opExtrude","CAP_FACE",FACE,{"disambiguationData":[OSD([sQuery(id+"F103.wireOp",EDGE,"E1467"),sQuery(id+"F103.wireOp",EDGE,"E1468.bottom"),sQuery(id+"F103.wireOp",EDGE,"E1468.top"),sQuery(id+"F103.wireOp",EDGE,"E1469.0"),sQuery(id+"F103.wireOp",EDGE,"E1470.trimOffspring")])],"isStart":false})]})],"fromTools":[makeQuery(id+"F108.opExtrude","CAP_FACE",FACE,{"disambiguationData":[OSD([sQuery(id+"F107.wireOp",EDGE,"E1472.0.0"),sQuery(id+"F107.wireOp",EDGE,"E1472.0.1"),sQuery(id+"F107.wireOp",EDGE,"E1472.0.2")])],"isStart":true}),makeQuery(id+"F108.opExtrude","CAP_FACE",FACE,{"disambiguationData":[OSD([sQuery(id+"F107.wireOp",EDGE,"E1473.0.0"),sQuery(id+"F107.wireOp",EDGE,"E1473.0.1"),sQuery(id+"F107.wireOp",EDGE,"E1473.0.2"),sQuery(id+"F107.wireOp",EDGE,"E1473.0.3")])],"isStart":true}),makeQuery(id+"F108.opExtrude","CAP_FACE",FACE,{"disambiguationData":[OSD([sQuery(id+"F107.wireOp",EDGE,"E1474.0.0"),sQuery(id+"F107.wireOp",EDGE,"E1474.0.1"),sQuery(id+"F107.wireOp",EDGE,"E1474.0.2"),sQuery(id+"F107.wireOp",EDGE,"E1474.0.3")])],"isStart":true}),makeQuery(id+"F108.opExtrude","CAP_FACE",FACE,{"disambiguationData":[OSD([sQuery(id+"F107.wireOp",EDGE,"E1475.0.0"),sQuery(id+"F107.wireOp",EDGE,"E1475.0.1"),sQuery(id+"F107.wireOp",EDGE,"E1475.0.2"),sQuery(id+"F107.wireOp",EDGE,"E1475.0.3")])],"isStart":true})]});}
            var sketch = newSketch(context, id + "F111", { "sketchPlane" : qUnion([Q0])});
            skLineSegment(sketch, "E1485", {"start": v(50.8, -46.58) * mm, "end": v(49.96, -47.94) * mm});
            skLineSegment(sketch, "E1486", {"start": v(51.23, -46.84) * mm, "end": v(49.79, -49.17) * mm});
            skLineSegment(sketch, "E1487", {"start": v(51.27, -48.45) * mm, "end": v(51.7, -48.72) * mm});
            skLineSegment(sketch, "E1488", {"start": v(50.66, -47.75) * mm, "end": v(50.24, -47.5) * mm});
            skLineSegment(sketch, "E1489", {"start": v(50.45, -47.62) * mm, "end": v(51.15, -46.49) * mm});
            skCircle(sketch, "E1490.0", {"center": v(51.15, -46.49) * mm, "radius": 0.36 * mm});
            skLineSegment(sketch, "E1491", {"start": v(49.79, -49.17) * mm, "end": v(49.79, -47.85) * mm});
            skLineSegment(sketch, "E1492", {"start": v(49.96, -47.94) * mm, "end": v(49.6, -48.53) * mm});
            skSolve(sketch);
        }
        {
            var Q0;
            Q0 = qSketchRegion(id + "F111", true);
            var Q1;
            Q1=makeQuery(id+"F102.opExtrude","CAP_FACE",FACE,{"disambiguationData":[OSD([sQuery(id+"F101.wireOp",EDGE,"E1450.0"),sQuery(id+"F101.wireOp",EDGE,"E1451.0"),sQuery(id+"F101.wireOp",EDGE,"E1461"),sQuery(id+"F101.wireOp",EDGE,"E1462")])],"isStart":false});
            extrude(context, id + "F112", {"entities" : qUnion([Q0]), "operationType" : NewBodyOperationType.ADD, "endBound" : BoundingType.UP_TO_SURFACE, "depth" : 25.4 * mm, "endBoundEntityFace" : qUnion([Q1]), "offsetDistance" : 25.4 * mm});
        }
        {
            var Q0;
            {var subQ0=sQuery(id+"F4.wireOp",EDGE,"E8");var subQ1=makeQuery(id+"F5.boolean.opBoolean","COPY",FACE,{"derivedFrom":makeQuery(id+"F5.opExtrude","SWEPT_FACE",FACE,{"disambiguationData":[OSD([subQ0])]})});var subQ2=makeQuery(id+"F5.boolean.opBoolean","COPY",FACE,{"derivedFrom":makeQuery(id+"F5.opExtrude","CAP_FACE",FACE,{"disambiguationData":[OSD([subQ0])],"isStart":false})});Q0=makeQuery(id+"F108.boolean.opBoolean","MERGE",FACE,{"derivedFrom":[makeQuery(id+"F104.boolean.opBoolean","MERGE",FACE,{"derivedFrom":[makeQuery(id+"F100.boolean.opBoolean","SPLIT",FACE,{"disambiguationData":[TD([makeQuery(id+"F39.opPattern","COPY",FACE,{"derivedFrom":makeQuery(id+"F19.opPattern","COPY",FACE,{"derivedFrom":makeQuery(id+"F16.opPattern","COPY",FACE,{"derivedFrom":subQ1,"instanceName":"1"}),"instanceName":"1"}),"instanceName":"1"})])],"derivedFrom":makeQuery(id+"F39.opPattern","COPY",FACE,{"derivedFrom":makeQuery(id+"F21.boolean.opBoolean","MERGE",FACE,{"derivedFrom":[makeQuery(id+"F19.opPattern","COPY",FACE,{"derivedFrom":makeQuery(id+"F16.opPattern","COPY",FACE,{"derivedFrom":makeQuery(id+"F9.boolean.opBoolean","SPLIT",FACE,{"disambiguationData":[TD([subQ1])],"derivedFrom":subQ2}),"instanceName":"1"}),"instanceName":"1"}),makeQuery(id+"F19.opPattern","COPY",FACE,{"derivedFrom":makeQuery(id+"F16.opPattern","COPY",FACE,{"derivedFrom":makeQuery(id+"F9.boolean.opBoolean","SPLIT",FACE,{"disambiguationData":[TD([makeQuery(id+"F9.opExtrude","SWEPT_FACE",FACE,{"disambiguationData":[OSD([sQuery(id+"F8.wireOp",EDGE,"E25")])]})])],"derivedFrom":subQ2}),"instanceName":"1"}),"instanceName":"1"}),makeQuery(id+"F19.opPattern","COPY",FACE,{"derivedFrom":makeQuery(id+"F16.opPattern","COPY",FACE,{"derivedFrom":makeQuery(id+"F9.boolean.opBoolean","SPLIT",FACE,{"disambiguationData":[TD([makeQuery(id+"F9.opExtrude","SWEPT_FACE",FACE,{"disambiguationData":[OSD([sQuery(id+"F8.wireOp",EDGE,"E32")])]})])],"derivedFrom":subQ2}),"instanceName":"1"}),"instanceName":"1"}),makeQuery(id+"F19.opPattern","COPY",FACE,{"derivedFrom":makeQuery(id+"F16.opPattern","COPY",FACE,{"derivedFrom":makeQuery(id+"F9.boolean.opBoolean","SPLIT",FACE,{"disambiguationData":[TD([makeQuery(id+"F9.opExtrude","SWEPT_FACE",FACE,{"disambiguationData":[OSD([sQuery(id+"F8.wireOp",EDGE,"E33.0")])]})])],"derivedFrom":subQ2}),"instanceName":"1"}),"instanceName":"1"}),makeQuery(id+"F19.opPattern","COPY",FACE,{"derivedFrom":makeQuery(id+"F16.opPattern","COPY",FACE,{"derivedFrom":makeQuery(id+"F9.boolean.opBoolean","SPLIT",FACE,{"disambiguationData":[TD([makeQuery(id+"F9.opExtrude","SWEPT_FACE",FACE,{"disambiguationData":[OSD([sQuery(id+"F8.wireOp",EDGE,"E37")])]})])],"derivedFrom":subQ2}),"instanceName":"1"}),"instanceName":"1"}),makeQuery(id+"F19.opPattern","COPY",FACE,{"derivedFrom":makeQuery(id+"F16.opPattern","COPY",FACE,{"derivedFrom":makeQuery(id+"F9.boolean.opBoolean","SPLIT",FACE,{"disambiguationData":[TD([makeQuery(id+"F9.opExtrude","SWEPT_FACE",FACE,{"disambiguationData":[OSD([sQuery(id+"F8.wireOp",EDGE,"E51.MirrorCS")])]})])],"derivedFrom":subQ2}),"instanceName":"1"}),"instanceName":"1"}),makeQuery(id+"F19.opPattern","COPY",FACE,{"derivedFrom":makeQuery(id+"F16.opPattern","COPY",FACE,{"derivedFrom":makeQuery(id+"F9.boolean.opBoolean","SPLIT",FACE,{"disambiguationData":[TD([makeQuery(id+"F9.opExtrude","SWEPT_FACE",FACE,{"disambiguationData":[OSD([sQuery(id+"F8.wireOp",EDGE,"E53.MirrorCS")])]})])],"derivedFrom":subQ2}),"instanceName":"1"}),"instanceName":"1"}),makeQuery(id+"F19.opPattern","COPY",FACE,{"derivedFrom":makeQuery(id+"F16.opPattern","COPY",FACE,{"derivedFrom":makeQuery(id+"F9.boolean.opBoolean","SPLIT",FACE,{"disambiguationData":[TD([makeQuery(id+"F9.opExtrude","SWEPT_FACE",FACE,{"disambiguationData":[OSD([sQuery(id+"F8.wireOp",EDGE,"E80")])]})])],"derivedFrom":subQ2}),"instanceName":"1"}),"instanceName":"1"}),makeQuery(id+"F19.opPattern","COPY",FACE,{"derivedFrom":makeQuery(id+"F16.opPattern","COPY",FACE,{"derivedFrom":makeQuery(id+"F9.boolean.opBoolean","SPLIT",FACE,{"disambiguationData":[TD([makeQuery(id+"F9.opExtrude","SWEPT_FACE",FACE,{"disambiguationData":[OSD([sQuery(id+"F8.wireOp",EDGE,"E83")])]})])],"derivedFrom":subQ2}),"instanceName":"1"}),"instanceName":"1"})],"fromTools":[makeQuery(id+"F21.opExtrude","CAP_FACE",FACE,{"disambiguationData":[OSD([sQuery(id+"F20.wireOp",EDGE,"E307.0.0")])],"isStart":false})]}),"instanceName":"1"})})],"fromTools":[makeQuery(id+"F104.opExtrude","CAP_FACE",FACE,{"disambiguationData":[OSD([sQuery(id+"F103.wireOp",EDGE,"E1467"),sQuery(id+"F103.wireOp",EDGE,"E1468.bottom"),sQuery(id+"F103.wireOp",EDGE,"E1468.top"),sQuery(id+"F103.wireOp",EDGE,"E1469.0"),sQuery(id+"F103.wireOp",EDGE,"E1470.trimOffspring")])],"isStart":false})]})],"fromTools":[makeQuery(id+"F108.opExtrude","CAP_FACE",FACE,{"disambiguationData":[OSD([sQuery(id+"F107.wireOp",EDGE,"E1472.0.0"),sQuery(id+"F107.wireOp",EDGE,"E1472.0.1"),sQuery(id+"F107.wireOp",EDGE,"E1472.0.2")])],"isStart":true}),makeQuery(id+"F108.opExtrude","CAP_FACE",FACE,{"disambiguationData":[OSD([sQuery(id+"F107.wireOp",EDGE,"E1473.0.0"),sQuery(id+"F107.wireOp",EDGE,"E1473.0.1"),sQuery(id+"F107.wireOp",EDGE,"E1473.0.2"),sQuery(id+"F107.wireOp",EDGE,"E1473.0.3")])],"isStart":true}),makeQuery(id+"F108.opExtrude","CAP_FACE",FACE,{"disambiguationData":[OSD([sQuery(id+"F107.wireOp",EDGE,"E1474.0.0"),sQuery(id+"F107.wireOp",EDGE,"E1474.0.1"),sQuery(id+"F107.wireOp",EDGE,"E1474.0.2"),sQuery(id+"F107.wireOp",EDGE,"E1474.0.3")])],"isStart":true}),makeQuery(id+"F108.opExtrude","CAP_FACE",FACE,{"disambiguationData":[OSD([sQuery(id+"F107.wireOp",EDGE,"E1475.0.0"),sQuery(id+"F107.wireOp",EDGE,"E1475.0.1"),sQuery(id+"F107.wireOp",EDGE,"E1475.0.2"),sQuery(id+"F107.wireOp",EDGE,"E1475.0.3")])],"isStart":true})]});}
            var sketch = newSketch(context, id + "F113", { "sketchPlane" : qUnion([Q0])});
            skEllipse(sketch, "E1493", {"center": v(43.54, -50.12) * mm, "majorRadius": 1.29 * mm, "minorRadius": 0.7 * mm, "majorAxis": v(0.83, 0.55)});
            skLineSegment(sketch, "E1494", {"start": v(44.87, -49.4) * mm, "end": v(45.3, -46.67) * mm});
            skPoint(sketch, "E1494.startSnap0", {"position": v(44.6, -49.4) * mm});
            skLineSegment(sketch, "E1495", {"start": v(44.43, -49.01) * mm, "end": v(44.9, -46.06) * mm});
            skArc(sketch, "E1496", {"start": v(45.25, -47) * mm, "mid": v(46.09, -47.34) * mm, "end": v(46.99, -47.35) * mm});
            skLineSegment(sketch, "E1497", {"start": v(46.7, -47.38) * mm, "end": v(46.25, -50.24) * mm});
            skLineSegment(sketch, "E1498.0", {"start": v(47.2, -47.46) * mm, "end": v(46.74, -50.32) * mm});
            skLineSegment(sketch, "E1499", {"start": v(47.17, -47.6) * mm, "end": v(47.47, -45.72) * mm});
            skArc(sketch, "E1500", {"start": v(44.9, -46.06) * mm, "mid": v(46, -46.76) * mm, "end": v(47.25, -47.09) * mm});
            skFitSpline(sketch, "E1501.0", {"points": [v(44.92, -49.47) * mm, v(44.83, -49.26) * mm, v(44.67, -49.1) * mm, v(44.47, -49) * mm, v(44.24, -48.95) * mm, v(43.92, -48.95) * mm, v(43.5, -49.05) * mm, v(43, -49.31) * mm, v(42.57, -49.67) * mm, v(42.3, -50.02) * mm, v(42.18, -50.31) * mm, v(42.13, -50.53) * mm, v(42.15, -50.76) * mm, v(42.24, -50.98) * mm, v(42.4, -51.14) * mm, v(42.6, -51.25) * mm, v(42.83, -51.3) * mm, v(43.15, -51.29) * mm, v(43.57, -51.18) * mm, v(44.07, -50.92) * mm, v(44.5, -50.57) * mm, v(44.76, -50.22) * mm, v(44.9, -49.93) * mm, v(44.94, -49.7) * mm, v(44.92, -49.47) * mm, v(44.83, -49.26) * mm, v(44.67, -49.1) * mm]});
            skLineSegment(sketch, "E1502", {"start": v(45.68, -49.52) * mm, "end": v(43.5, -52.17) * mm});
            skEllipse(sketch, "E1503", {"center": v(45.63, -51.25) * mm, "majorRadius": 1.2 * mm, "minorRadius": 0.6 * mm, "majorAxis": v(0.85, 0.53)});
            skFitSpline(sketch, "E1504.0", {"points": [v(47.02, -50.67) * mm, v(46.94, -50.44) * mm, v(46.77, -50.26) * mm, v(46.56, -50.16) * mm, v(46.33, -50.11) * mm, v(46.02, -50.12) * mm, v(45.61, -50.22) * mm, v(45.13, -50.45) * mm, v(44.7, -50.78) * mm, v(44.44, -51.1) * mm, v(44.3, -51.38) * mm, v(44.24, -51.6) * mm, v(44.24, -51.84) * mm, v(44.33, -52.07) * mm, v(44.5, -52.25) * mm, v(44.71, -52.35) * mm, v(44.94, -52.4) * mm, v(45.25, -52.4) * mm, v(45.65, -52.3) * mm, v(46.13, -52.06) * mm, v(46.56, -51.73) * mm, v(46.83, -51.4) * mm, v(46.97, -51.13) * mm, v(47.03, -50.9) * mm, v(47.02, -50.67) * mm, v(46.94, -50.44) * mm, v(46.77, -50.26) * mm]});
            skSolve(sketch);
        }
        {
            var Q0;
            Q0 = qSketchRegion(id + "F113", true);
            var Q1;
            Q1=makeQuery(id+"F102.opExtrude","CAP_FACE",FACE,{"disambiguationData":[OSD([sQuery(id+"F101.wireOp",EDGE,"E1458.0"),sQuery(id+"F101.wireOp",EDGE,"E1459.0"),sQuery(id+"F101.wireOp",EDGE,"E1461"),sQuery(id+"F101.wireOp",EDGE,"E1466")])],"isStart":false});
            extrude(context, id + "F114", {"entities" : qUnion([Q0]), "operationType" : NewBodyOperationType.ADD, "endBound" : BoundingType.UP_TO_SURFACE, "depth" : 25.4 * mm, "endBoundEntityFace" : qUnion([Q1]), "offsetDistance" : 25.4 * mm});
        }
    });
